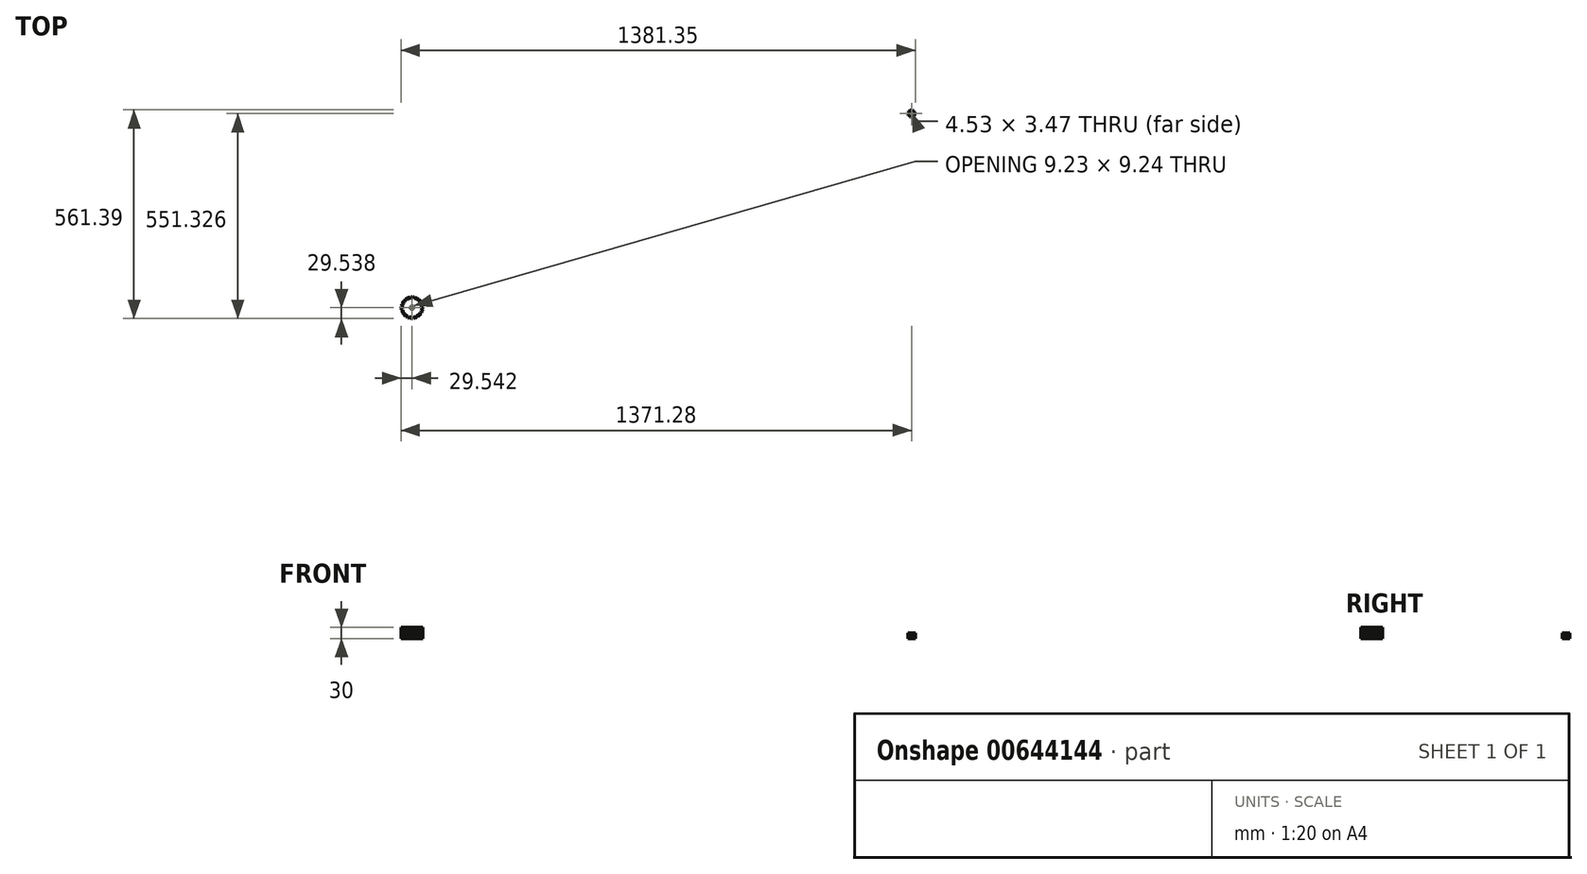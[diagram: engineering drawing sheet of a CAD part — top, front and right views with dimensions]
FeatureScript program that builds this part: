
annotation { "Feature Type Name" : "Feature", "Feature Type Description" : "" }
export const myFeature = defineFeature(function(context is Context, id is Id, definition is map)
    precondition{}
    {
        {
            var Q0;
            Q0=qCreatedBy(makeId("Top.planeOp"),FACE);
            var sketch = newSketch(context, id + "F0", { "sketchPlane" : qUnion([Q0])});
            skLineSegment(sketch, "E0", {"start": v(-554.7, 834.7) * mm, "end": v(-554.7, 832.86) * mm});
            skLineSegment(sketch, "E1", {"start": v(-545.46, 834.7) * mm, "end": v(-545.46, 832.86) * mm});
            skLineSegment(sketch, "E2", {"start": v(-499.13, 795.45) * mm, "end": v(-499.01, 795.41) * mm});
            skLineSegment(sketch, "E3", {"start": v(-499.01, 795.41) * mm, "end": v(-498.9, 795.4) * mm});
            skLineSegment(sketch, "E4", {"start": v(-498.9, 795.4) * mm, "end": v(-498.78, 795.37) * mm});
            skLineSegment(sketch, "E5", {"start": v(-498.78, 795.37) * mm, "end": v(-498.66, 795.35) * mm});
            skLineSegment(sketch, "E6", {"start": v(-498.66, 795.35) * mm, "end": v(-498.54, 795.33) * mm});
            skLineSegment(sketch, "E7", {"start": v(-498.54, 795.33) * mm, "end": v(-498.42, 795.3) * mm});
            skLineSegment(sketch, "E8", {"start": v(-498.42, 795.3) * mm, "end": v(-498.3, 795.27) * mm});
            skLineSegment(sketch, "E9", {"start": v(-498.3, 795.27) * mm, "end": v(-498.19, 795.24) * mm});
            skLineSegment(sketch, "E10", {"start": v(-498.19, 795.24) * mm, "end": v(-498.07, 795.2) * mm});
            skLineSegment(sketch, "E11", {"start": v(-498.07, 795.2) * mm, "end": v(-497.95, 795.17) * mm});
            skLineSegment(sketch, "E12", {"start": v(-497.95, 795.17) * mm, "end": v(-497.84, 795.14) * mm});
            skLineSegment(sketch, "E13", {"start": v(-497.84, 795.14) * mm, "end": v(-497.72, 795.1) * mm});
            skLineSegment(sketch, "E14", {"start": v(-497.72, 795.1) * mm, "end": v(-497.6, 795.06) * mm});
            skLineSegment(sketch, "E15", {"start": v(-497.6, 795.06) * mm, "end": v(-497.48, 795.02) * mm});
            skLineSegment(sketch, "E16", {"start": v(-497.48, 795.02) * mm, "end": v(-497.37, 794.98) * mm});
            skLineSegment(sketch, "E17", {"start": v(-497.37, 794.98) * mm, "end": v(-497.25, 794.93) * mm});
            skLineSegment(sketch, "E18", {"start": v(-497.25, 794.93) * mm, "end": v(-497.13, 794.88) * mm});
            skLineSegment(sketch, "E19", {"start": v(-497.13, 794.88) * mm, "end": v(-497.02, 794.84) * mm});
            skLineSegment(sketch, "E20", {"start": v(-497.02, 794.84) * mm, "end": v(-496.9, 794.79) * mm});
            skLineSegment(sketch, "E21", {"start": v(-496.9, 794.79) * mm, "end": v(-496.78, 794.74) * mm});
            skLineSegment(sketch, "E22", {"start": v(-496.78, 794.74) * mm, "end": v(-496.67, 794.68) * mm});
            skLineSegment(sketch, "E23", {"start": v(-496.67, 794.68) * mm, "end": v(-496.55, 794.63) * mm});
            skLineSegment(sketch, "E24", {"start": v(-496.55, 794.63) * mm, "end": v(-496.43, 794.57) * mm});
            skLineSegment(sketch, "E25", {"start": v(-496.43, 794.57) * mm, "end": v(-496.32, 794.51) * mm});
            skLineSegment(sketch, "E26", {"start": v(-496.32, 794.51) * mm, "end": v(-496.2, 794.45) * mm});
            skLineSegment(sketch, "E27", {"start": v(-496.2, 794.45) * mm, "end": v(-496.08, 794.4) * mm});
            skLineSegment(sketch, "E28", {"start": v(-496.08, 794.4) * mm, "end": v(-495.97, 794.33) * mm});
            skLineSegment(sketch, "E29", {"start": v(-495.97, 794.33) * mm, "end": v(-495.85, 794.27) * mm});
            skLineSegment(sketch, "E30", {"start": v(-495.85, 794.27) * mm, "end": v(-495.74, 794.2) * mm});
            skLineSegment(sketch, "E31", {"start": v(-495.74, 794.2) * mm, "end": v(-495.62, 794.13) * mm});
            skLineSegment(sketch, "E32", {"start": v(-495.62, 794.13) * mm, "end": v(-495.65, 793.46) * mm});
            skLineSegment(sketch, "E33", {"start": v(-495.65, 793.46) * mm, "end": v(-495.7, 792.79) * mm});
            skLineSegment(sketch, "E34", {"start": v(-495.7, 792.79) * mm, "end": v(-495.81, 792.73) * mm});
            skLineSegment(sketch, "E35", {"start": v(-495.81, 792.73) * mm, "end": v(-495.93, 792.68) * mm});
            skLineSegment(sketch, "E36", {"start": v(-495.93, 792.68) * mm, "end": v(-496.06, 792.63) * mm});
            skLineSegment(sketch, "E37", {"start": v(-496.06, 792.63) * mm, "end": v(-496.18, 792.58) * mm});
            skLineSegment(sketch, "E38", {"start": v(-496.18, 792.58) * mm, "end": v(-496.3, 792.53) * mm});
            skLineSegment(sketch, "E39", {"start": v(-496.3, 792.53) * mm, "end": v(-496.42, 792.49) * mm});
            skLineSegment(sketch, "E40", {"start": v(-496.42, 792.49) * mm, "end": v(-496.54, 792.44) * mm});
            skLineSegment(sketch, "E41", {"start": v(-496.54, 792.44) * mm, "end": v(-496.67, 792.4) * mm});
            skLineSegment(sketch, "E42", {"start": v(-496.67, 792.4) * mm, "end": v(-496.79, 792.35) * mm});
            skLineSegment(sketch, "E43", {"start": v(-496.79, 792.35) * mm, "end": v(-496.9, 792.31) * mm});
            skLineSegment(sketch, "E44", {"start": v(-496.9, 792.31) * mm, "end": v(-497.03, 792.27) * mm});
            skLineSegment(sketch, "E45", {"start": v(-497.03, 792.27) * mm, "end": v(-497.15, 792.24) * mm});
            skLineSegment(sketch, "E46", {"start": v(-497.15, 792.24) * mm, "end": v(-497.27, 792.2) * mm});
            skLineSegment(sketch, "E47", {"start": v(-497.27, 792.2) * mm, "end": v(-497.4, 792.17) * mm});
            skLineSegment(sketch, "E48", {"start": v(-497.4, 792.17) * mm, "end": v(-497.52, 792.14) * mm});
            skLineSegment(sketch, "E49", {"start": v(-497.52, 792.14) * mm, "end": v(-497.64, 792.1) * mm});
            skLineSegment(sketch, "E50", {"start": v(-497.64, 792.1) * mm, "end": v(-497.76, 792.08) * mm});
            skLineSegment(sketch, "E51", {"start": v(-497.76, 792.08) * mm, "end": v(-497.88, 792.05) * mm});
            skLineSegment(sketch, "E52", {"start": v(-497.88, 792.05) * mm, "end": v(-498, 792.02) * mm});
            skLineSegment(sketch, "E53", {"start": v(-498, 792.02) * mm, "end": v(-498.12, 792) * mm});
            skLineSegment(sketch, "E54", {"start": v(-498.12, 792) * mm, "end": v(-498.24, 791.98) * mm});
            skLineSegment(sketch, "E55", {"start": v(-498.24, 791.98) * mm, "end": v(-498.36, 791.96) * mm});
            skLineSegment(sketch, "E56", {"start": v(-498.36, 791.96) * mm, "end": v(-498.48, 791.94) * mm});
            skLineSegment(sketch, "E57", {"start": v(-498.48, 791.94) * mm, "end": v(-498.6, 791.92) * mm});
            skLineSegment(sketch, "E58", {"start": v(-498.6, 791.92) * mm, "end": v(-498.72, 791.91) * mm});
            skLineSegment(sketch, "E59", {"start": v(-498.72, 791.91) * mm, "end": v(-498.84, 791.9) * mm});
            skLineSegment(sketch, "E60", {"start": v(-498.84, 791.9) * mm, "end": v(-498.96, 791.89) * mm});
            skLineSegment(sketch, "E61", {"start": v(-498.96, 791.89) * mm, "end": v(-499.08, 791.88) * mm});
            skLineSegment(sketch, "E62", {"start": v(-499.08, 791.88) * mm, "end": v(-499.2, 791.87) * mm});
            skLineSegment(sketch, "E63", {"start": v(-499.2, 791.87) * mm, "end": v(-499.32, 791.85) * mm});
            skLineSegment(sketch, "E64", {"start": v(-499.32, 791.85) * mm, "end": v(-499.95, 791.93) * mm});
            skLineSegment(sketch, "E65", {"start": v(-499.95, 791.93) * mm, "end": v(-500.23, 790.15) * mm});
            skLineSegment(sketch, "E66", {"start": v(-500.23, 790.15) * mm, "end": v(-499.6, 790.03) * mm});
            skLineSegment(sketch, "E67", {"start": v(-499.6, 790.03) * mm, "end": v(-499.5, 789.97) * mm});
            skLineSegment(sketch, "E68", {"start": v(-499.5, 789.97) * mm, "end": v(-499.39, 789.92) * mm});
            skLineSegment(sketch, "E69", {"start": v(-499.39, 789.92) * mm, "end": v(-499.28, 789.88) * mm});
            skLineSegment(sketch, "E70", {"start": v(-499.28, 789.88) * mm, "end": v(-499.17, 789.83) * mm});
            skLineSegment(sketch, "E71", {"start": v(-499.17, 789.83) * mm, "end": v(-499.06, 789.78) * mm});
            skLineSegment(sketch, "E72", {"start": v(-499.06, 789.78) * mm, "end": v(-498.95, 789.73) * mm});
            skLineSegment(sketch, "E73", {"start": v(-498.95, 789.73) * mm, "end": v(-498.84, 789.68) * mm});
            skLineSegment(sketch, "E74", {"start": v(-498.84, 789.68) * mm, "end": v(-498.73, 789.63) * mm});
            skLineSegment(sketch, "E75", {"start": v(-498.73, 789.63) * mm, "end": v(-498.62, 789.57) * mm});
            skLineSegment(sketch, "E76", {"start": v(-498.62, 789.57) * mm, "end": v(-498.51, 789.51) * mm});
            skLineSegment(sketch, "E77", {"start": v(-498.51, 789.51) * mm, "end": v(-498.4, 789.45) * mm});
            skLineSegment(sketch, "E78", {"start": v(-498.4, 789.45) * mm, "end": v(-498.3, 789.4) * mm});
            skLineSegment(sketch, "E79", {"start": v(-498.3, 789.4) * mm, "end": v(-498.2, 789.33) * mm});
            skLineSegment(sketch, "E80", {"start": v(-498.2, 789.33) * mm, "end": v(-498.09, 789.26) * mm});
            skLineSegment(sketch, "E81", {"start": v(-498.09, 789.26) * mm, "end": v(-497.98, 789.2) * mm});
            skLineSegment(sketch, "E82", {"start": v(-497.98, 789.2) * mm, "end": v(-497.88, 789.13) * mm});
            skLineSegment(sketch, "E83", {"start": v(-497.88, 789.13) * mm, "end": v(-497.77, 789.06) * mm});
            skLineSegment(sketch, "E84", {"start": v(-497.77, 789.06) * mm, "end": v(-497.67, 788.99) * mm});
            skLineSegment(sketch, "E85", {"start": v(-497.67, 788.99) * mm, "end": v(-497.56, 788.92) * mm});
            skLineSegment(sketch, "E86", {"start": v(-497.56, 788.92) * mm, "end": v(-497.46, 788.84) * mm});
            skLineSegment(sketch, "E87", {"start": v(-497.46, 788.84) * mm, "end": v(-497.36, 788.77) * mm});
            skLineSegment(sketch, "E88", {"start": v(-497.36, 788.77) * mm, "end": v(-497.25, 788.69) * mm});
            skLineSegment(sketch, "E89", {"start": v(-497.25, 788.69) * mm, "end": v(-497.15, 788.6) * mm});
            skLineSegment(sketch, "E90", {"start": v(-497.15, 788.6) * mm, "end": v(-497.05, 788.53) * mm});
            skLineSegment(sketch, "E91", {"start": v(-497.05, 788.53) * mm, "end": v(-496.95, 788.45) * mm});
            skLineSegment(sketch, "E92", {"start": v(-496.95, 788.45) * mm, "end": v(-496.85, 788.36) * mm});
            skLineSegment(sketch, "E93", {"start": v(-496.85, 788.36) * mm, "end": v(-496.75, 788.28) * mm});
            skLineSegment(sketch, "E94", {"start": v(-496.75, 788.28) * mm, "end": v(-496.65, 788.2) * mm});
            skLineSegment(sketch, "E95", {"start": v(-496.65, 788.2) * mm, "end": v(-496.55, 788.1) * mm});
            skLineSegment(sketch, "E96", {"start": v(-496.55, 788.1) * mm, "end": v(-496.45, 788.01) * mm});
            skLineSegment(sketch, "E97", {"start": v(-496.45, 788.01) * mm, "end": v(-496.61, 787.36) * mm});
            skLineSegment(sketch, "E98", {"start": v(-496.61, 787.36) * mm, "end": v(-496.8, 786.7) * mm});
            skLineSegment(sketch, "E99", {"start": v(-496.8, 786.7) * mm, "end": v(-496.93, 786.68) * mm});
            skLineSegment(sketch, "E100", {"start": v(-496.93, 786.68) * mm, "end": v(-497.06, 786.66) * mm});
            skLineSegment(sketch, "E101", {"start": v(-497.06, 786.66) * mm, "end": v(-497.19, 786.63) * mm});
            skLineSegment(sketch, "E102", {"start": v(-497.19, 786.63) * mm, "end": v(-497.32, 786.6) * mm});
            skLineSegment(sketch, "E103", {"start": v(-497.32, 786.6) * mm, "end": v(-497.45, 786.59) * mm});
            skLineSegment(sketch, "E104", {"start": v(-497.45, 786.59) * mm, "end": v(-497.57, 786.57) * mm});
            skLineSegment(sketch, "E105", {"start": v(-497.57, 786.57) * mm, "end": v(-497.7, 786.55) * mm});
            skLineSegment(sketch, "E106", {"start": v(-497.7, 786.55) * mm, "end": v(-497.83, 786.53) * mm});
            skLineSegment(sketch, "E107", {"start": v(-497.83, 786.53) * mm, "end": v(-497.96, 786.51) * mm});
            skLineSegment(sketch, "E108", {"start": v(-497.96, 786.51) * mm, "end": v(-498.09, 786.5) * mm});
            skLineSegment(sketch, "E109", {"start": v(-498.09, 786.5) * mm, "end": v(-498.21, 786.49) * mm});
            skLineSegment(sketch, "E110", {"start": v(-498.21, 786.49) * mm, "end": v(-498.34, 786.48) * mm});
            skLineSegment(sketch, "E111", {"start": v(-498.34, 786.48) * mm, "end": v(-498.47, 786.47) * mm});
            skLineSegment(sketch, "E112", {"start": v(-498.47, 786.47) * mm, "end": v(-498.6, 786.46) * mm});
            skLineSegment(sketch, "E113", {"start": v(-498.6, 786.46) * mm, "end": v(-498.72, 786.45) * mm});
            skLineSegment(sketch, "E114", {"start": v(-498.72, 786.45) * mm, "end": v(-498.84, 786.45) * mm});
            skLineSegment(sketch, "E115", {"start": v(-498.84, 786.45) * mm, "end": v(-498.97, 786.44) * mm});
            skLineSegment(sketch, "E116", {"start": v(-498.97, 786.44) * mm, "end": v(-499.1, 786.44) * mm});
            skLineSegment(sketch, "E117", {"start": v(-499.1, 786.44) * mm, "end": v(-499.21, 786.44) * mm});
            skLineSegment(sketch, "E118", {"start": v(-499.21, 786.44) * mm, "end": v(-499.34, 786.44) * mm});
            skLineSegment(sketch, "E119", {"start": v(-499.34, 786.44) * mm, "end": v(-499.46, 786.45) * mm});
            skLineSegment(sketch, "E120", {"start": v(-499.46, 786.45) * mm, "end": v(-499.58, 786.45) * mm});
            skLineSegment(sketch, "E121", {"start": v(-499.58, 786.45) * mm, "end": v(-499.7, 786.46) * mm});
            skLineSegment(sketch, "E122", {"start": v(-499.7, 786.46) * mm, "end": v(-499.82, 786.47) * mm});
            skLineSegment(sketch, "E123", {"start": v(-499.82, 786.47) * mm, "end": v(-499.94, 786.48) * mm});
            skLineSegment(sketch, "E124", {"start": v(-499.94, 786.48) * mm, "end": v(-500.06, 786.5) * mm});
            skLineSegment(sketch, "E125", {"start": v(-500.06, 786.5) * mm, "end": v(-500.18, 786.51) * mm});
            skLineSegment(sketch, "E126", {"start": v(-500.18, 786.51) * mm, "end": v(-500.3, 786.53) * mm});
            skLineSegment(sketch, "E127", {"start": v(-500.3, 786.53) * mm, "end": v(-500.42, 786.54) * mm});
            skLineSegment(sketch, "E128", {"start": v(-500.42, 786.54) * mm, "end": v(-500.54, 786.55) * mm});
            skLineSegment(sketch, "E129", {"start": v(-500.54, 786.55) * mm, "end": v(-501.14, 786.75) * mm});
            skLineSegment(sketch, "E130", {"start": v(-501.14, 786.75) * mm, "end": v(-501.79, 785.07) * mm});
            skLineSegment(sketch, "E131", {"start": v(-501.79, 785.07) * mm, "end": v(-501.2, 784.82) * mm});
            skLineSegment(sketch, "E132", {"start": v(-501.2, 784.82) * mm, "end": v(-501.1, 784.74) * mm});
            skLineSegment(sketch, "E133", {"start": v(-501.1, 784.74) * mm, "end": v(-501, 784.67) * mm});
            skLineSegment(sketch, "E134", {"start": v(-501, 784.67) * mm, "end": v(-500.91, 784.6) * mm});
            skLineSegment(sketch, "E135", {"start": v(-500.91, 784.6) * mm, "end": v(-500.81, 784.54) * mm});
            skLineSegment(sketch, "E136", {"start": v(-500.81, 784.54) * mm, "end": v(-500.71, 784.47) * mm});
            skLineSegment(sketch, "E137", {"start": v(-500.71, 784.47) * mm, "end": v(-500.62, 784.4) * mm});
            skLineSegment(sketch, "E138", {"start": v(-500.62, 784.4) * mm, "end": v(-500.52, 784.33) * mm});
            skLineSegment(sketch, "E139", {"start": v(-500.52, 784.33) * mm, "end": v(-500.43, 784.25) * mm});
            skLineSegment(sketch, "E140", {"start": v(-500.43, 784.25) * mm, "end": v(-500.33, 784.17) * mm});
            skLineSegment(sketch, "E141", {"start": v(-500.33, 784.17) * mm, "end": v(-500.24, 784.1) * mm});
            skLineSegment(sketch, "E142", {"start": v(-500.24, 784.1) * mm, "end": v(-500.15, 784.01) * mm});
            skLineSegment(sketch, "E143", {"start": v(-500.15, 784.01) * mm, "end": v(-500.05, 783.93) * mm});
            skLineSegment(sketch, "E144", {"start": v(-500.05, 783.93) * mm, "end": v(-499.96, 783.85) * mm});
            skLineSegment(sketch, "E145", {"start": v(-499.96, 783.85) * mm, "end": v(-499.87, 783.76) * mm});
            skLineSegment(sketch, "E146", {"start": v(-499.87, 783.76) * mm, "end": v(-499.78, 783.67) * mm});
            skLineSegment(sketch, "E147", {"start": v(-499.78, 783.67) * mm, "end": v(-499.7, 783.59) * mm});
            skLineSegment(sketch, "E148", {"start": v(-499.7, 783.59) * mm, "end": v(-499.6, 783.5) * mm});
            skLineSegment(sketch, "E149", {"start": v(-499.6, 783.5) * mm, "end": v(-499.52, 783.4) * mm});
            skLineSegment(sketch, "E150", {"start": v(-499.52, 783.4) * mm, "end": v(-499.43, 783.31) * mm});
            skLineSegment(sketch, "E151", {"start": v(-499.43, 783.31) * mm, "end": v(-499.35, 783.22) * mm});
            skLineSegment(sketch, "E152", {"start": v(-499.35, 783.22) * mm, "end": v(-499.26, 783.12) * mm});
            skLineSegment(sketch, "E153", {"start": v(-499.26, 783.12) * mm, "end": v(-499.18, 783.02) * mm});
            skLineSegment(sketch, "E154", {"start": v(-499.18, 783.02) * mm, "end": v(-499.1, 782.93) * mm});
            skLineSegment(sketch, "E155", {"start": v(-499.1, 782.93) * mm, "end": v(-499.01, 782.82) * mm});
            skLineSegment(sketch, "E156", {"start": v(-499.01, 782.82) * mm, "end": v(-498.93, 782.72) * mm});
            skLineSegment(sketch, "E157", {"start": v(-498.93, 782.72) * mm, "end": v(-498.85, 782.62) * mm});
            skLineSegment(sketch, "E158", {"start": v(-498.85, 782.62) * mm, "end": v(-498.77, 782.52) * mm});
            skLineSegment(sketch, "E159", {"start": v(-498.77, 782.52) * mm, "end": v(-498.69, 782.41) * mm});
            skLineSegment(sketch, "E160", {"start": v(-498.69, 782.41) * mm, "end": v(-498.6, 782.3) * mm});
            skLineSegment(sketch, "E161", {"start": v(-498.6, 782.3) * mm, "end": v(-498.53, 782.2) * mm});
            skLineSegment(sketch, "E162", {"start": v(-498.53, 782.2) * mm, "end": v(-498.83, 781.6) * mm});
            skLineSegment(sketch, "E163", {"start": v(-498.83, 781.6) * mm, "end": v(-499.14, 781) * mm});
            skLineSegment(sketch, "E164", {"start": v(-499.14, 781) * mm, "end": v(-499.27, 781) * mm});
            skLineSegment(sketch, "E165", {"start": v(-499.27, 781) * mm, "end": v(-499.4, 781) * mm});
            skLineSegment(sketch, "E166", {"start": v(-499.4, 781) * mm, "end": v(-499.54, 781) * mm});
            skLineSegment(sketch, "E167", {"start": v(-499.54, 781) * mm, "end": v(-499.67, 781) * mm});
            skLineSegment(sketch, "E168", {"start": v(-499.67, 781) * mm, "end": v(-499.8, 781) * mm});
            skLineSegment(sketch, "E169", {"start": v(-499.8, 781) * mm, "end": v(-499.93, 781.02) * mm});
            skLineSegment(sketch, "E170", {"start": v(-499.93, 781.02) * mm, "end": v(-500.06, 781.02) * mm});
            skLineSegment(sketch, "E171", {"start": v(-500.06, 781.02) * mm, "end": v(-500.2, 781.03) * mm});
            skLineSegment(sketch, "E172", {"start": v(-500.2, 781.03) * mm, "end": v(-500.32, 781.04) * mm});
            skLineSegment(sketch, "E173", {"start": v(-500.32, 781.04) * mm, "end": v(-500.45, 781.06) * mm});
            skLineSegment(sketch, "E174", {"start": v(-500.45, 781.06) * mm, "end": v(-500.57, 781.07) * mm});
            skLineSegment(sketch, "E175", {"start": v(-500.57, 781.07) * mm, "end": v(-500.7, 781.09) * mm});
            skLineSegment(sketch, "E176", {"start": v(-500.7, 781.09) * mm, "end": v(-500.83, 781.1) * mm});
            skLineSegment(sketch, "E177", {"start": v(-500.83, 781.1) * mm, "end": v(-500.95, 781.12) * mm});
            skLineSegment(sketch, "E178", {"start": v(-500.95, 781.12) * mm, "end": v(-501.07, 781.14) * mm});
            skLineSegment(sketch, "E179", {"start": v(-501.07, 781.14) * mm, "end": v(-501.2, 781.16) * mm});
            skLineSegment(sketch, "E180", {"start": v(-501.2, 781.16) * mm, "end": v(-501.32, 781.18) * mm});
            skLineSegment(sketch, "E181", {"start": v(-501.32, 781.18) * mm, "end": v(-501.44, 781.2) * mm});
            skLineSegment(sketch, "E182", {"start": v(-501.44, 781.2) * mm, "end": v(-501.56, 781.24) * mm});
            skLineSegment(sketch, "E183", {"start": v(-501.56, 781.24) * mm, "end": v(-501.68, 781.26) * mm});
            skLineSegment(sketch, "E184", {"start": v(-501.68, 781.26) * mm, "end": v(-501.8, 781.3) * mm});
            skLineSegment(sketch, "E185", {"start": v(-501.8, 781.3) * mm, "end": v(-501.92, 781.32) * mm});
            skLineSegment(sketch, "E186", {"start": v(-501.92, 781.32) * mm, "end": v(-502.03, 781.35) * mm});
            skLineSegment(sketch, "E187", {"start": v(-502.03, 781.35) * mm, "end": v(-502.15, 781.39) * mm});
            skLineSegment(sketch, "E188", {"start": v(-502.15, 781.39) * mm, "end": v(-502.27, 781.42) * mm});
            skLineSegment(sketch, "E189", {"start": v(-502.27, 781.42) * mm, "end": v(-502.38, 781.46) * mm});
            skLineSegment(sketch, "E190", {"start": v(-502.38, 781.46) * mm, "end": v(-502.5, 781.5) * mm});
            skLineSegment(sketch, "E191", {"start": v(-502.5, 781.5) * mm, "end": v(-502.6, 781.54) * mm});
            skLineSegment(sketch, "E192", {"start": v(-502.6, 781.54) * mm, "end": v(-502.72, 781.58) * mm});
            skLineSegment(sketch, "E193", {"start": v(-502.72, 781.58) * mm, "end": v(-502.84, 781.61) * mm});
            skLineSegment(sketch, "E194", {"start": v(-502.84, 781.61) * mm, "end": v(-503.38, 781.94) * mm});
            skLineSegment(sketch, "E195", {"start": v(-503.38, 781.94) * mm, "end": v(-504.36, 780.43) * mm});
            skLineSegment(sketch, "E196", {"start": v(-504.36, 780.43) * mm, "end": v(-503.84, 780.07) * mm});
            skLineSegment(sketch, "E197", {"start": v(-503.84, 780.07) * mm, "end": v(-503.77, 779.97) * mm});
            skLineSegment(sketch, "E198", {"start": v(-503.77, 779.97) * mm, "end": v(-503.68, 779.88) * mm});
            skLineSegment(sketch, "E199", {"start": v(-503.68, 779.88) * mm, "end": v(-503.6, 779.8) * mm});
            skLineSegment(sketch, "E200", {"start": v(-503.6, 779.8) * mm, "end": v(-503.52, 779.7) * mm});
            skLineSegment(sketch, "E201", {"start": v(-503.52, 779.7) * mm, "end": v(-503.44, 779.62) * mm});
            skLineSegment(sketch, "E202", {"start": v(-503.44, 779.62) * mm, "end": v(-503.36, 779.53) * mm});
            skLineSegment(sketch, "E203", {"start": v(-503.36, 779.53) * mm, "end": v(-503.28, 779.44) * mm});
            skLineSegment(sketch, "E204", {"start": v(-503.28, 779.44) * mm, "end": v(-503.2, 779.34) * mm});
            skLineSegment(sketch, "E205", {"start": v(-503.2, 779.34) * mm, "end": v(-503.13, 779.25) * mm});
            skLineSegment(sketch, "E206", {"start": v(-503.13, 779.25) * mm, "end": v(-503.05, 779.15) * mm});
            skLineSegment(sketch, "E207", {"start": v(-503.05, 779.15) * mm, "end": v(-502.98, 779.05) * mm});
            skLineSegment(sketch, "E208", {"start": v(-502.98, 779.05) * mm, "end": v(-502.9, 778.95) * mm});
            skLineSegment(sketch, "E209", {"start": v(-502.9, 778.95) * mm, "end": v(-502.83, 778.85) * mm});
            skLineSegment(sketch, "E210", {"start": v(-502.83, 778.85) * mm, "end": v(-502.76, 778.75) * mm});
            skLineSegment(sketch, "E211", {"start": v(-502.76, 778.75) * mm, "end": v(-502.7, 778.65) * mm});
            skLineSegment(sketch, "E212", {"start": v(-502.7, 778.65) * mm, "end": v(-502.62, 778.54) * mm});
            skLineSegment(sketch, "E213", {"start": v(-502.62, 778.54) * mm, "end": v(-502.56, 778.43) * mm});
            skLineSegment(sketch, "E214", {"start": v(-502.56, 778.43) * mm, "end": v(-502.5, 778.33) * mm});
            skLineSegment(sketch, "E215", {"start": v(-502.5, 778.33) * mm, "end": v(-502.43, 778.22) * mm});
            skLineSegment(sketch, "E216", {"start": v(-502.43, 778.22) * mm, "end": v(-502.36, 778.1) * mm});
            skLineSegment(sketch, "E217", {"start": v(-502.36, 778.1) * mm, "end": v(-502.3, 778) * mm});
            skLineSegment(sketch, "E218", {"start": v(-502.3, 778) * mm, "end": v(-502.24, 777.88) * mm});
            skLineSegment(sketch, "E219", {"start": v(-502.24, 777.88) * mm, "end": v(-502.18, 777.77) * mm});
            skLineSegment(sketch, "E220", {"start": v(-502.18, 777.77) * mm, "end": v(-502.11, 777.65) * mm});
            skLineSegment(sketch, "E221", {"start": v(-502.11, 777.65) * mm, "end": v(-502.06, 777.54) * mm});
            skLineSegment(sketch, "E222", {"start": v(-502.06, 777.54) * mm, "end": v(-502, 777.42) * mm});
            skLineSegment(sketch, "E223", {"start": v(-502, 777.42) * mm, "end": v(-501.94, 777.3) * mm});
            skLineSegment(sketch, "E224", {"start": v(-501.94, 777.3) * mm, "end": v(-501.88, 777.18) * mm});
            skLineSegment(sketch, "E225", {"start": v(-501.88, 777.18) * mm, "end": v(-501.83, 777.06) * mm});
            skLineSegment(sketch, "E226", {"start": v(-501.83, 777.06) * mm, "end": v(-501.77, 776.94) * mm});
            skLineSegment(sketch, "E227", {"start": v(-501.77, 776.94) * mm, "end": v(-502.2, 776.41) * mm});
            skLineSegment(sketch, "E228", {"start": v(-502.2, 776.41) * mm, "end": v(-502.62, 775.9) * mm});
            skLineSegment(sketch, "E229", {"start": v(-502.62, 775.9) * mm, "end": v(-502.75, 775.92) * mm});
            skLineSegment(sketch, "E230", {"start": v(-502.75, 775.92) * mm, "end": v(-502.88, 775.95) * mm});
            skLineSegment(sketch, "E231", {"start": v(-502.88, 775.95) * mm, "end": v(-503.01, 775.98) * mm});
            skLineSegment(sketch, "E232", {"start": v(-503.01, 775.98) * mm, "end": v(-503.14, 776.01) * mm});
            skLineSegment(sketch, "E233", {"start": v(-503.14, 776.01) * mm, "end": v(-503.27, 776.04) * mm});
            skLineSegment(sketch, "E234", {"start": v(-503.27, 776.04) * mm, "end": v(-503.4, 776.08) * mm});
            skLineSegment(sketch, "E235", {"start": v(-503.4, 776.08) * mm, "end": v(-503.52, 776.11) * mm});
            skLineSegment(sketch, "E236", {"start": v(-503.52, 776.11) * mm, "end": v(-503.64, 776.15) * mm});
            skLineSegment(sketch, "E237", {"start": v(-503.64, 776.15) * mm, "end": v(-503.77, 776.18) * mm});
            skLineSegment(sketch, "E238", {"start": v(-503.77, 776.18) * mm, "end": v(-503.89, 776.22) * mm});
            skLineSegment(sketch, "E239", {"start": v(-503.89, 776.22) * mm, "end": v(-504, 776.26) * mm});
            skLineSegment(sketch, "E240", {"start": v(-504, 776.26) * mm, "end": v(-504.13, 776.3) * mm});
            skLineSegment(sketch, "E241", {"start": v(-504.13, 776.3) * mm, "end": v(-504.25, 776.35) * mm});
            skLineSegment(sketch, "E242", {"start": v(-504.25, 776.35) * mm, "end": v(-504.37, 776.4) * mm});
            skLineSegment(sketch, "E243", {"start": v(-504.37, 776.4) * mm, "end": v(-504.48, 776.44) * mm});
            skLineSegment(sketch, "E244", {"start": v(-504.48, 776.44) * mm, "end": v(-504.6, 776.48) * mm});
            skLineSegment(sketch, "E245", {"start": v(-504.6, 776.48) * mm, "end": v(-504.71, 776.53) * mm});
            skLineSegment(sketch, "E246", {"start": v(-504.71, 776.53) * mm, "end": v(-504.83, 776.58) * mm});
            skLineSegment(sketch, "E247", {"start": v(-504.83, 776.58) * mm, "end": v(-504.94, 776.63) * mm});
            skLineSegment(sketch, "E248", {"start": v(-504.94, 776.63) * mm, "end": v(-505.05, 776.68) * mm});
            skLineSegment(sketch, "E249", {"start": v(-505.05, 776.68) * mm, "end": v(-505.16, 776.74) * mm});
            skLineSegment(sketch, "E250", {"start": v(-505.16, 776.74) * mm, "end": v(-505.27, 776.8) * mm});
            skLineSegment(sketch, "E251", {"start": v(-505.27, 776.8) * mm, "end": v(-505.38, 776.85) * mm});
            skLineSegment(sketch, "E252", {"start": v(-505.38, 776.85) * mm, "end": v(-505.48, 776.9) * mm});
            skLineSegment(sketch, "E253", {"start": v(-505.48, 776.9) * mm, "end": v(-505.59, 776.96) * mm});
            skLineSegment(sketch, "E254", {"start": v(-505.59, 776.96) * mm, "end": v(-505.7, 777.02) * mm});
            skLineSegment(sketch, "E255", {"start": v(-505.7, 777.02) * mm, "end": v(-505.8, 777.09) * mm});
            skLineSegment(sketch, "E256", {"start": v(-505.8, 777.09) * mm, "end": v(-505.9, 777.15) * mm});
            skLineSegment(sketch, "E257", {"start": v(-505.9, 777.15) * mm, "end": v(-506, 777.21) * mm});
            skLineSegment(sketch, "E258", {"start": v(-506, 777.21) * mm, "end": v(-506.1, 777.26) * mm});
            skLineSegment(sketch, "E259", {"start": v(-506.1, 777.26) * mm, "end": v(-506.58, 777.7) * mm});
            skLineSegment(sketch, "E260", {"start": v(-506.58, 777.7) * mm, "end": v(-507.85, 776.43) * mm});
            skLineSegment(sketch, "E261", {"start": v(-507.85, 776.43) * mm, "end": v(-507.41, 775.96) * mm});
            skLineSegment(sketch, "E262", {"start": v(-507.41, 775.96) * mm, "end": v(-507.36, 775.85) * mm});
            skLineSegment(sketch, "E263", {"start": v(-507.36, 775.85) * mm, "end": v(-507.3, 775.75) * mm});
            skLineSegment(sketch, "E264", {"start": v(-507.3, 775.75) * mm, "end": v(-507.24, 775.65) * mm});
            skLineSegment(sketch, "E265", {"start": v(-507.24, 775.65) * mm, "end": v(-507.17, 775.54) * mm});
            skLineSegment(sketch, "E266", {"start": v(-507.17, 775.54) * mm, "end": v(-507.11, 775.44) * mm});
            skLineSegment(sketch, "E267", {"start": v(-507.11, 775.44) * mm, "end": v(-507.05, 775.33) * mm});
            skLineSegment(sketch, "E268", {"start": v(-507.05, 775.33) * mm, "end": v(-507, 775.23) * mm});
            skLineSegment(sketch, "E269", {"start": v(-507, 775.23) * mm, "end": v(-506.94, 775.12) * mm});
            skLineSegment(sketch, "E270", {"start": v(-506.94, 775.12) * mm, "end": v(-506.89, 775.01) * mm});
            skLineSegment(sketch, "E271", {"start": v(-506.89, 775.01) * mm, "end": v(-506.83, 774.9) * mm});
            skLineSegment(sketch, "E272", {"start": v(-506.83, 774.9) * mm, "end": v(-506.78, 774.8) * mm});
            skLineSegment(sketch, "E273", {"start": v(-506.78, 774.8) * mm, "end": v(-506.73, 774.68) * mm});
            skLineSegment(sketch, "E274", {"start": v(-506.73, 774.68) * mm, "end": v(-506.68, 774.56) * mm});
            skLineSegment(sketch, "E275", {"start": v(-506.68, 774.56) * mm, "end": v(-506.63, 774.45) * mm});
            skLineSegment(sketch, "E276", {"start": v(-506.63, 774.45) * mm, "end": v(-506.59, 774.33) * mm});
            skLineSegment(sketch, "E277", {"start": v(-506.59, 774.33) * mm, "end": v(-506.54, 774.22) * mm});
            skLineSegment(sketch, "E278", {"start": v(-506.54, 774.22) * mm, "end": v(-506.5, 774.1) * mm});
            skLineSegment(sketch, "E279", {"start": v(-506.5, 774.1) * mm, "end": v(-506.46, 773.98) * mm});
            skLineSegment(sketch, "E280", {"start": v(-506.46, 773.98) * mm, "end": v(-506.41, 773.86) * mm});
            skLineSegment(sketch, "E281", {"start": v(-506.41, 773.86) * mm, "end": v(-506.37, 773.74) * mm});
            skLineSegment(sketch, "E282", {"start": v(-506.37, 773.74) * mm, "end": v(-506.33, 773.62) * mm});
            skLineSegment(sketch, "E283", {"start": v(-506.33, 773.62) * mm, "end": v(-506.3, 773.5) * mm});
            skLineSegment(sketch, "E284", {"start": v(-506.3, 773.5) * mm, "end": v(-506.26, 773.37) * mm});
            skLineSegment(sketch, "E285", {"start": v(-506.26, 773.37) * mm, "end": v(-506.23, 773.24) * mm});
            skLineSegment(sketch, "E286", {"start": v(-506.23, 773.24) * mm, "end": v(-506.2, 773.12) * mm});
            skLineSegment(sketch, "E287", {"start": v(-506.2, 773.12) * mm, "end": v(-506.16, 773) * mm});
            skLineSegment(sketch, "E288", {"start": v(-506.16, 773) * mm, "end": v(-506.13, 772.86) * mm});
            skLineSegment(sketch, "E289", {"start": v(-506.13, 772.86) * mm, "end": v(-506.1, 772.73) * mm});
            skLineSegment(sketch, "E290", {"start": v(-506.1, 772.73) * mm, "end": v(-506.07, 772.6) * mm});
            skLineSegment(sketch, "E291", {"start": v(-506.07, 772.6) * mm, "end": v(-506.04, 772.47) * mm});
            skLineSegment(sketch, "E292", {"start": v(-506.04, 772.47) * mm, "end": v(-506.56, 772.04) * mm});
            skLineSegment(sketch, "E293", {"start": v(-506.56, 772.04) * mm, "end": v(-507.1, 771.62) * mm});
            skLineSegment(sketch, "E294", {"start": v(-507.1, 771.62) * mm, "end": v(-507.21, 771.68) * mm});
            skLineSegment(sketch, "E295", {"start": v(-507.21, 771.68) * mm, "end": v(-507.33, 771.73) * mm});
            skLineSegment(sketch, "E296", {"start": v(-507.33, 771.73) * mm, "end": v(-507.45, 771.8) * mm});
            skLineSegment(sketch, "E297", {"start": v(-507.45, 771.8) * mm, "end": v(-507.57, 771.85) * mm});
            skLineSegment(sketch, "E298", {"start": v(-507.57, 771.85) * mm, "end": v(-507.69, 771.9) * mm});
            skLineSegment(sketch, "E299", {"start": v(-507.69, 771.9) * mm, "end": v(-507.8, 771.96) * mm});
            skLineSegment(sketch, "E300", {"start": v(-507.8, 771.96) * mm, "end": v(-507.92, 772.03) * mm});
            skLineSegment(sketch, "E301", {"start": v(-507.92, 772.03) * mm, "end": v(-508.03, 772.09) * mm});
            skLineSegment(sketch, "E302", {"start": v(-508.03, 772.09) * mm, "end": v(-508.15, 772.15) * mm});
            skLineSegment(sketch, "E303", {"start": v(-508.15, 772.15) * mm, "end": v(-508.26, 772.21) * mm});
            skLineSegment(sketch, "E304", {"start": v(-508.26, 772.21) * mm, "end": v(-508.37, 772.28) * mm});
            skLineSegment(sketch, "E305", {"start": v(-508.37, 772.28) * mm, "end": v(-508.48, 772.34) * mm});
            skLineSegment(sketch, "E306", {"start": v(-508.48, 772.34) * mm, "end": v(-508.59, 772.4) * mm});
            skLineSegment(sketch, "E307", {"start": v(-508.59, 772.4) * mm, "end": v(-508.7, 772.47) * mm});
            skLineSegment(sketch, "E308", {"start": v(-508.7, 772.47) * mm, "end": v(-508.8, 772.54) * mm});
            skLineSegment(sketch, "E309", {"start": v(-508.8, 772.54) * mm, "end": v(-508.9, 772.61) * mm});
            skLineSegment(sketch, "E310", {"start": v(-508.9, 772.61) * mm, "end": v(-509, 772.68) * mm});
            skLineSegment(sketch, "E311", {"start": v(-509, 772.68) * mm, "end": v(-509.1, 772.76) * mm});
            skLineSegment(sketch, "E312", {"start": v(-509.1, 772.76) * mm, "end": v(-509.2, 772.83) * mm});
            skLineSegment(sketch, "E313", {"start": v(-509.2, 772.83) * mm, "end": v(-509.3, 772.9) * mm});
            skLineSegment(sketch, "E314", {"start": v(-509.3, 772.9) * mm, "end": v(-509.4, 772.98) * mm});
            skLineSegment(sketch, "E315", {"start": v(-509.4, 772.98) * mm, "end": v(-509.5, 773.05) * mm});
            skLineSegment(sketch, "E316", {"start": v(-509.5, 773.05) * mm, "end": v(-509.59, 773.13) * mm});
            skLineSegment(sketch, "E317", {"start": v(-509.59, 773.13) * mm, "end": v(-509.68, 773.2) * mm});
            skLineSegment(sketch, "E318", {"start": v(-509.68, 773.2) * mm, "end": v(-509.77, 773.29) * mm});
            skLineSegment(sketch, "E319", {"start": v(-509.77, 773.29) * mm, "end": v(-509.86, 773.37) * mm});
            skLineSegment(sketch, "E320", {"start": v(-509.86, 773.37) * mm, "end": v(-509.94, 773.45) * mm});
            skLineSegment(sketch, "E321", {"start": v(-509.94, 773.45) * mm, "end": v(-510.03, 773.53) * mm});
            skLineSegment(sketch, "E322", {"start": v(-510.03, 773.53) * mm, "end": v(-510.12, 773.62) * mm});
            skLineSegment(sketch, "E323", {"start": v(-510.12, 773.62) * mm, "end": v(-510.22, 773.7) * mm});
            skLineSegment(sketch, "E324", {"start": v(-510.22, 773.7) * mm, "end": v(-510.58, 774.21) * mm});
            skLineSegment(sketch, "E325", {"start": v(-510.58, 774.21) * mm, "end": v(-512.1, 773.23) * mm});
            skLineSegment(sketch, "E326", {"start": v(-512.1, 773.23) * mm, "end": v(-511.76, 772.69) * mm});
            skLineSegment(sketch, "E327", {"start": v(-511.76, 772.69) * mm, "end": v(-511.73, 772.57) * mm});
            skLineSegment(sketch, "E328", {"start": v(-511.73, 772.57) * mm, "end": v(-511.7, 772.46) * mm});
            skLineSegment(sketch, "E329", {"start": v(-511.7, 772.46) * mm, "end": v(-511.65, 772.34) * mm});
            skLineSegment(sketch, "E330", {"start": v(-511.65, 772.34) * mm, "end": v(-511.61, 772.23) * mm});
            skLineSegment(sketch, "E331", {"start": v(-511.61, 772.23) * mm, "end": v(-511.58, 772.12) * mm});
            skLineSegment(sketch, "E332", {"start": v(-511.58, 772.12) * mm, "end": v(-511.54, 772) * mm});
            skLineSegment(sketch, "E333", {"start": v(-511.54, 772) * mm, "end": v(-511.5, 771.88) * mm});
            skLineSegment(sketch, "E334", {"start": v(-511.5, 771.88) * mm, "end": v(-511.47, 771.77) * mm});
            skLineSegment(sketch, "E335", {"start": v(-511.47, 771.77) * mm, "end": v(-511.44, 771.65) * mm});
            skLineSegment(sketch, "E336", {"start": v(-511.44, 771.65) * mm, "end": v(-511.41, 771.53) * mm});
            skLineSegment(sketch, "E337", {"start": v(-511.41, 771.53) * mm, "end": v(-511.38, 771.41) * mm});
            skLineSegment(sketch, "E338", {"start": v(-511.38, 771.41) * mm, "end": v(-511.36, 771.3) * mm});
            skLineSegment(sketch, "E339", {"start": v(-511.36, 771.3) * mm, "end": v(-511.33, 771.17) * mm});
            skLineSegment(sketch, "E340", {"start": v(-511.33, 771.17) * mm, "end": v(-511.31, 771.05) * mm});
            skLineSegment(sketch, "E341", {"start": v(-511.31, 771.05) * mm, "end": v(-511.3, 770.92) * mm});
            skLineSegment(sketch, "E342", {"start": v(-511.3, 770.92) * mm, "end": v(-511.27, 770.8) * mm});
            skLineSegment(sketch, "E343", {"start": v(-511.27, 770.8) * mm, "end": v(-511.25, 770.67) * mm});
            skLineSegment(sketch, "E344", {"start": v(-511.25, 770.67) * mm, "end": v(-511.24, 770.55) * mm});
            skLineSegment(sketch, "E345", {"start": v(-511.24, 770.55) * mm, "end": v(-511.22, 770.42) * mm});
            skLineSegment(sketch, "E346", {"start": v(-511.22, 770.42) * mm, "end": v(-511.2, 770.3) * mm});
            skLineSegment(sketch, "E347", {"start": v(-511.2, 770.3) * mm, "end": v(-511.2, 770.17) * mm});
            skLineSegment(sketch, "E348", {"start": v(-511.2, 770.17) * mm, "end": v(-511.18, 770.04) * mm});
            skLineSegment(sketch, "E349", {"start": v(-511.18, 770.04) * mm, "end": v(-511.17, 769.91) * mm});
            skLineSegment(sketch, "E350", {"start": v(-511.17, 769.91) * mm, "end": v(-511.17, 769.78) * mm});
            skLineSegment(sketch, "E351", {"start": v(-511.17, 769.78) * mm, "end": v(-511.16, 769.65) * mm});
            skLineSegment(sketch, "E352", {"start": v(-511.16, 769.65) * mm, "end": v(-511.15, 769.52) * mm});
            skLineSegment(sketch, "E353", {"start": v(-511.15, 769.52) * mm, "end": v(-511.15, 769.4) * mm});
            skLineSegment(sketch, "E354", {"start": v(-511.15, 769.4) * mm, "end": v(-511.15, 769.26) * mm});
            skLineSegment(sketch, "E355", {"start": v(-511.15, 769.26) * mm, "end": v(-511.14, 769.12) * mm});
            skLineSegment(sketch, "E356", {"start": v(-511.14, 769.12) * mm, "end": v(-511.14, 769) * mm});
            skLineSegment(sketch, "E357", {"start": v(-511.14, 769) * mm, "end": v(-511.74, 768.68) * mm});
            skLineSegment(sketch, "E358", {"start": v(-511.74, 768.68) * mm, "end": v(-512.35, 768.38) * mm});
            skLineSegment(sketch, "E359", {"start": v(-512.35, 768.38) * mm, "end": v(-512.46, 768.46) * mm});
            skLineSegment(sketch, "E360", {"start": v(-512.46, 768.46) * mm, "end": v(-512.56, 768.54) * mm});
            skLineSegment(sketch, "E361", {"start": v(-512.56, 768.54) * mm, "end": v(-512.67, 768.62) * mm});
            skLineSegment(sketch, "E362", {"start": v(-512.67, 768.62) * mm, "end": v(-512.77, 768.7) * mm});
            skLineSegment(sketch, "E363", {"start": v(-512.77, 768.7) * mm, "end": v(-512.87, 768.78) * mm});
            skLineSegment(sketch, "E364", {"start": v(-512.87, 768.78) * mm, "end": v(-512.98, 768.86) * mm});
            skLineSegment(sketch, "E365", {"start": v(-512.98, 768.86) * mm, "end": v(-513.08, 768.94) * mm});
            skLineSegment(sketch, "E366", {"start": v(-513.08, 768.94) * mm, "end": v(-513.17, 769.03) * mm});
            skLineSegment(sketch, "E367", {"start": v(-513.17, 769.03) * mm, "end": v(-513.27, 769.11) * mm});
            skLineSegment(sketch, "E368", {"start": v(-513.27, 769.11) * mm, "end": v(-513.37, 769.2) * mm});
            skLineSegment(sketch, "E369", {"start": v(-513.37, 769.2) * mm, "end": v(-513.46, 769.28) * mm});
            skLineSegment(sketch, "E370", {"start": v(-513.46, 769.28) * mm, "end": v(-513.55, 769.37) * mm});
            skLineSegment(sketch, "E371", {"start": v(-513.55, 769.37) * mm, "end": v(-513.65, 769.45) * mm});
            skLineSegment(sketch, "E372", {"start": v(-513.65, 769.45) * mm, "end": v(-513.74, 769.54) * mm});
            skLineSegment(sketch, "E373", {"start": v(-513.74, 769.54) * mm, "end": v(-513.82, 769.63) * mm});
            skLineSegment(sketch, "E374", {"start": v(-513.82, 769.63) * mm, "end": v(-513.91, 769.72) * mm});
            skLineSegment(sketch, "E375", {"start": v(-513.91, 769.72) * mm, "end": v(-514, 769.81) * mm});
            skLineSegment(sketch, "E376", {"start": v(-514, 769.81) * mm, "end": v(-514.08, 769.9) * mm});
            skLineSegment(sketch, "E377", {"start": v(-514.08, 769.9) * mm, "end": v(-514.16, 770) * mm});
            skLineSegment(sketch, "E378", {"start": v(-514.16, 770) * mm, "end": v(-514.24, 770.09) * mm});
            skLineSegment(sketch, "E379", {"start": v(-514.24, 770.09) * mm, "end": v(-514.32, 770.18) * mm});
            skLineSegment(sketch, "E380", {"start": v(-514.32, 770.18) * mm, "end": v(-514.4, 770.28) * mm});
            skLineSegment(sketch, "E381", {"start": v(-514.4, 770.28) * mm, "end": v(-514.48, 770.37) * mm});
            skLineSegment(sketch, "E382", {"start": v(-514.48, 770.37) * mm, "end": v(-514.55, 770.47) * mm});
            skLineSegment(sketch, "E383", {"start": v(-514.55, 770.47) * mm, "end": v(-514.62, 770.56) * mm});
            skLineSegment(sketch, "E384", {"start": v(-514.62, 770.56) * mm, "end": v(-514.7, 770.66) * mm});
            skLineSegment(sketch, "E385", {"start": v(-514.7, 770.66) * mm, "end": v(-514.76, 770.76) * mm});
            skLineSegment(sketch, "E386", {"start": v(-514.76, 770.76) * mm, "end": v(-514.83, 770.86) * mm});
            skLineSegment(sketch, "E387", {"start": v(-514.83, 770.86) * mm, "end": v(-514.9, 770.96) * mm});
            skLineSegment(sketch, "E388", {"start": v(-514.9, 770.96) * mm, "end": v(-514.97, 771.05) * mm});
            skLineSegment(sketch, "E389", {"start": v(-514.97, 771.05) * mm, "end": v(-515.22, 771.64) * mm});
            skLineSegment(sketch, "E390", {"start": v(-515.22, 771.64) * mm, "end": v(-516.9, 771) * mm});
            skLineSegment(sketch, "E391", {"start": v(-516.9, 771) * mm, "end": v(-516.7, 770.39) * mm});
            skLineSegment(sketch, "E392", {"start": v(-516.7, 770.39) * mm, "end": v(-516.7, 770.27) * mm});
            skLineSegment(sketch, "E393", {"start": v(-516.7, 770.27) * mm, "end": v(-516.68, 770.15) * mm});
            skLineSegment(sketch, "E394", {"start": v(-516.68, 770.15) * mm, "end": v(-516.66, 770.03) * mm});
            skLineSegment(sketch, "E395", {"start": v(-516.66, 770.03) * mm, "end": v(-516.64, 769.91) * mm});
            skLineSegment(sketch, "E396", {"start": v(-516.64, 769.91) * mm, "end": v(-516.63, 769.8) * mm});
            skLineSegment(sketch, "E397", {"start": v(-516.63, 769.8) * mm, "end": v(-516.62, 769.67) * mm});
            skLineSegment(sketch, "E398", {"start": v(-516.62, 769.67) * mm, "end": v(-516.61, 769.55) * mm});
            skLineSegment(sketch, "E399", {"start": v(-516.61, 769.55) * mm, "end": v(-516.6, 769.43) * mm});
            skLineSegment(sketch, "E400", {"start": v(-516.6, 769.43) * mm, "end": v(-516.6, 769.3) * mm});
            skLineSegment(sketch, "E401", {"start": v(-516.6, 769.3) * mm, "end": v(-516.6, 769.19) * mm});
            skLineSegment(sketch, "E402", {"start": v(-516.6, 769.19) * mm, "end": v(-516.6, 769.06) * mm});
            skLineSegment(sketch, "E403", {"start": v(-516.6, 769.06) * mm, "end": v(-516.6, 768.94) * mm});
            skLineSegment(sketch, "E404", {"start": v(-516.6, 768.94) * mm, "end": v(-516.6, 768.82) * mm});
            skLineSegment(sketch, "E405", {"start": v(-516.6, 768.82) * mm, "end": v(-516.6, 768.7) * mm});
            skLineSegment(sketch, "E406", {"start": v(-516.6, 768.7) * mm, "end": v(-516.6, 768.57) * mm});
            skLineSegment(sketch, "E407", {"start": v(-516.6, 768.57) * mm, "end": v(-516.6, 768.44) * mm});
            skLineSegment(sketch, "E408", {"start": v(-516.6, 768.44) * mm, "end": v(-516.62, 768.32) * mm});
            skLineSegment(sketch, "E409", {"start": v(-516.62, 768.32) * mm, "end": v(-516.63, 768.2) * mm});
            skLineSegment(sketch, "E410", {"start": v(-516.63, 768.2) * mm, "end": v(-516.64, 768.06) * mm});
            skLineSegment(sketch, "E411", {"start": v(-516.64, 768.06) * mm, "end": v(-516.65, 767.94) * mm});
            skLineSegment(sketch, "E412", {"start": v(-516.65, 767.94) * mm, "end": v(-516.66, 767.8) * mm});
            skLineSegment(sketch, "E413", {"start": v(-516.66, 767.8) * mm, "end": v(-516.68, 767.68) * mm});
            skLineSegment(sketch, "E414", {"start": v(-516.68, 767.68) * mm, "end": v(-516.7, 767.55) * mm});
            skLineSegment(sketch, "E415", {"start": v(-516.7, 767.55) * mm, "end": v(-516.71, 767.42) * mm});
            skLineSegment(sketch, "E416", {"start": v(-516.71, 767.42) * mm, "end": v(-516.74, 767.3) * mm});
            skLineSegment(sketch, "E417", {"start": v(-516.74, 767.3) * mm, "end": v(-516.76, 767.17) * mm});
            skLineSegment(sketch, "E418", {"start": v(-516.76, 767.17) * mm, "end": v(-516.78, 767.04) * mm});
            skLineSegment(sketch, "E419", {"start": v(-516.78, 767.04) * mm, "end": v(-516.8, 766.9) * mm});
            skLineSegment(sketch, "E420", {"start": v(-516.8, 766.9) * mm, "end": v(-516.83, 766.78) * mm});
            skLineSegment(sketch, "E421", {"start": v(-516.83, 766.78) * mm, "end": v(-516.86, 766.65) * mm});
            skLineSegment(sketch, "E422", {"start": v(-516.86, 766.65) * mm, "end": v(-517.51, 766.46) * mm});
            skLineSegment(sketch, "E423", {"start": v(-517.51, 766.46) * mm, "end": v(-518.16, 766.3) * mm});
            skLineSegment(sketch, "E424", {"start": v(-518.16, 766.3) * mm, "end": v(-518.25, 766.4) * mm});
            skLineSegment(sketch, "E425", {"start": v(-518.25, 766.4) * mm, "end": v(-518.34, 766.5) * mm});
            skLineSegment(sketch, "E426", {"start": v(-518.34, 766.5) * mm, "end": v(-518.43, 766.6) * mm});
            skLineSegment(sketch, "E427", {"start": v(-518.43, 766.6) * mm, "end": v(-518.51, 766.7) * mm});
            skLineSegment(sketch, "E428", {"start": v(-518.51, 766.7) * mm, "end": v(-518.6, 766.8) * mm});
            skLineSegment(sketch, "E429", {"start": v(-518.6, 766.8) * mm, "end": v(-518.68, 766.9) * mm});
            skLineSegment(sketch, "E430", {"start": v(-518.68, 766.9) * mm, "end": v(-518.76, 767) * mm});
            skLineSegment(sketch, "E431", {"start": v(-518.76, 767) * mm, "end": v(-518.84, 767.1) * mm});
            skLineSegment(sketch, "E432", {"start": v(-518.84, 767.1) * mm, "end": v(-518.92, 767.2) * mm});
            skLineSegment(sketch, "E433", {"start": v(-518.92, 767.2) * mm, "end": v(-519, 767.3) * mm});
            skLineSegment(sketch, "E434", {"start": v(-519, 767.3) * mm, "end": v(-519.07, 767.41) * mm});
            skLineSegment(sketch, "E435", {"start": v(-519.07, 767.41) * mm, "end": v(-519.14, 767.52) * mm});
            skLineSegment(sketch, "E436", {"start": v(-519.14, 767.52) * mm, "end": v(-519.21, 767.62) * mm});
            skLineSegment(sketch, "E437", {"start": v(-519.21, 767.62) * mm, "end": v(-519.28, 767.73) * mm});
            skLineSegment(sketch, "E438", {"start": v(-519.28, 767.73) * mm, "end": v(-519.35, 767.83) * mm});
            skLineSegment(sketch, "E439", {"start": v(-519.35, 767.83) * mm, "end": v(-519.41, 767.94) * mm});
            skLineSegment(sketch, "E440", {"start": v(-519.41, 767.94) * mm, "end": v(-519.48, 768.04) * mm});
            skLineSegment(sketch, "E441", {"start": v(-519.48, 768.04) * mm, "end": v(-519.54, 768.15) * mm});
            skLineSegment(sketch, "E442", {"start": v(-519.54, 768.15) * mm, "end": v(-519.6, 768.26) * mm});
            skLineSegment(sketch, "E443", {"start": v(-519.6, 768.26) * mm, "end": v(-519.66, 768.36) * mm});
            skLineSegment(sketch, "E444", {"start": v(-519.66, 768.36) * mm, "end": v(-519.72, 768.47) * mm});
            skLineSegment(sketch, "E445", {"start": v(-519.72, 768.47) * mm, "end": v(-519.78, 768.58) * mm});
            skLineSegment(sketch, "E446", {"start": v(-519.78, 768.58) * mm, "end": v(-519.83, 768.69) * mm});
            skLineSegment(sketch, "E447", {"start": v(-519.83, 768.69) * mm, "end": v(-519.88, 768.8) * mm});
            skLineSegment(sketch, "E448", {"start": v(-519.88, 768.8) * mm, "end": v(-519.93, 768.9) * mm});
            skLineSegment(sketch, "E449", {"start": v(-519.93, 768.9) * mm, "end": v(-519.98, 769.02) * mm});
            skLineSegment(sketch, "E450", {"start": v(-519.98, 769.02) * mm, "end": v(-520.03, 769.13) * mm});
            skLineSegment(sketch, "E451", {"start": v(-520.03, 769.13) * mm, "end": v(-520.07, 769.24) * mm});
            skLineSegment(sketch, "E452", {"start": v(-520.07, 769.24) * mm, "end": v(-520.12, 769.35) * mm});
            skLineSegment(sketch, "E453", {"start": v(-520.12, 769.35) * mm, "end": v(-520.18, 769.46) * mm});
            skLineSegment(sketch, "E454", {"start": v(-520.18, 769.46) * mm, "end": v(-520.3, 770.08) * mm});
            skLineSegment(sketch, "E455", {"start": v(-520.3, 770.08) * mm, "end": v(-522.08, 769.8) * mm});
            skLineSegment(sketch, "E456", {"start": v(-522.08, 769.8) * mm, "end": v(-522, 769.17) * mm});
            skLineSegment(sketch, "E457", {"start": v(-522, 769.17) * mm, "end": v(-522.02, 769.05) * mm});
            skLineSegment(sketch, "E458", {"start": v(-522.02, 769.05) * mm, "end": v(-522.03, 768.93) * mm});
            skLineSegment(sketch, "E459", {"start": v(-522.03, 768.93) * mm, "end": v(-522.04, 768.8) * mm});
            skLineSegment(sketch, "E460", {"start": v(-522.04, 768.8) * mm, "end": v(-522.05, 768.69) * mm});
            skLineSegment(sketch, "E461", {"start": v(-522.05, 768.69) * mm, "end": v(-522.06, 768.57) * mm});
            skLineSegment(sketch, "E462", {"start": v(-522.06, 768.57) * mm, "end": v(-522.07, 768.45) * mm});
            skLineSegment(sketch, "E463", {"start": v(-522.07, 768.45) * mm, "end": v(-522.1, 768.33) * mm});
            skLineSegment(sketch, "E464", {"start": v(-522.1, 768.33) * mm, "end": v(-522.1, 768.2) * mm});
            skLineSegment(sketch, "E465", {"start": v(-522.1, 768.2) * mm, "end": v(-522.13, 768.1) * mm});
            skLineSegment(sketch, "E466", {"start": v(-522.13, 768.1) * mm, "end": v(-522.15, 767.97) * mm});
            skLineSegment(sketch, "E467", {"start": v(-522.15, 767.97) * mm, "end": v(-522.17, 767.85) * mm});
            skLineSegment(sketch, "E468", {"start": v(-522.17, 767.85) * mm, "end": v(-522.2, 767.73) * mm});
            skLineSegment(sketch, "E469", {"start": v(-522.2, 767.73) * mm, "end": v(-522.23, 767.6) * mm});
            skLineSegment(sketch, "E470", {"start": v(-522.23, 767.6) * mm, "end": v(-522.25, 767.49) * mm});
            skLineSegment(sketch, "E471", {"start": v(-522.25, 767.49) * mm, "end": v(-522.29, 767.37) * mm});
            skLineSegment(sketch, "E472", {"start": v(-522.29, 767.37) * mm, "end": v(-522.32, 767.24) * mm});
            skLineSegment(sketch, "E473", {"start": v(-522.32, 767.24) * mm, "end": v(-522.35, 767.12) * mm});
            skLineSegment(sketch, "E474", {"start": v(-522.35, 767.12) * mm, "end": v(-522.39, 767) * mm});
            skLineSegment(sketch, "E475", {"start": v(-522.39, 767) * mm, "end": v(-522.42, 766.88) * mm});
            skLineSegment(sketch, "E476", {"start": v(-522.42, 766.88) * mm, "end": v(-522.46, 766.76) * mm});
            skLineSegment(sketch, "E477", {"start": v(-522.46, 766.76) * mm, "end": v(-522.5, 766.64) * mm});
            skLineSegment(sketch, "E478", {"start": v(-522.5, 766.64) * mm, "end": v(-522.55, 766.52) * mm});
            skLineSegment(sketch, "E479", {"start": v(-522.55, 766.52) * mm, "end": v(-522.6, 766.4) * mm});
            skLineSegment(sketch, "E480", {"start": v(-522.6, 766.4) * mm, "end": v(-522.64, 766.27) * mm});
            skLineSegment(sketch, "E481", {"start": v(-522.64, 766.27) * mm, "end": v(-522.68, 766.15) * mm});
            skLineSegment(sketch, "E482", {"start": v(-522.68, 766.15) * mm, "end": v(-522.73, 766.03) * mm});
            skLineSegment(sketch, "E483", {"start": v(-522.73, 766.03) * mm, "end": v(-522.78, 765.9) * mm});
            skLineSegment(sketch, "E484", {"start": v(-522.78, 765.9) * mm, "end": v(-522.83, 765.78) * mm});
            skLineSegment(sketch, "E485", {"start": v(-522.83, 765.78) * mm, "end": v(-522.88, 765.66) * mm});
            skLineSegment(sketch, "E486", {"start": v(-522.88, 765.66) * mm, "end": v(-522.94, 765.54) * mm});
            skLineSegment(sketch, "E487", {"start": v(-522.94, 765.54) * mm, "end": v(-523.61, 765.5) * mm});
            skLineSegment(sketch, "E488", {"start": v(-523.61, 765.5) * mm, "end": v(-524.28, 765.47) * mm});
            skLineSegment(sketch, "E489", {"start": v(-524.28, 765.47) * mm, "end": v(-524.35, 765.59) * mm});
            skLineSegment(sketch, "E490", {"start": v(-524.35, 765.59) * mm, "end": v(-524.42, 765.7) * mm});
            skLineSegment(sketch, "E491", {"start": v(-524.42, 765.7) * mm, "end": v(-524.48, 765.82) * mm});
            skLineSegment(sketch, "E492", {"start": v(-524.48, 765.82) * mm, "end": v(-524.54, 765.93) * mm});
            skLineSegment(sketch, "E493", {"start": v(-524.54, 765.93) * mm, "end": v(-524.6, 766.05) * mm});
            skLineSegment(sketch, "E494", {"start": v(-524.6, 766.05) * mm, "end": v(-524.66, 766.17) * mm});
            skLineSegment(sketch, "E495", {"start": v(-524.66, 766.17) * mm, "end": v(-524.72, 766.28) * mm});
            skLineSegment(sketch, "E496", {"start": v(-524.72, 766.28) * mm, "end": v(-524.78, 766.4) * mm});
            skLineSegment(sketch, "E497", {"start": v(-524.78, 766.4) * mm, "end": v(-524.83, 766.52) * mm});
            skLineSegment(sketch, "E498", {"start": v(-524.83, 766.52) * mm, "end": v(-524.88, 766.63) * mm});
            skLineSegment(sketch, "E499", {"start": v(-524.88, 766.63) * mm, "end": v(-524.94, 766.75) * mm});
            skLineSegment(sketch, "E500", {"start": v(-524.94, 766.75) * mm, "end": v(-524.99, 766.87) * mm});
            skLineSegment(sketch, "E501", {"start": v(-524.99, 766.87) * mm, "end": v(-525.03, 766.98) * mm});
            skLineSegment(sketch, "E502", {"start": v(-525.03, 766.98) * mm, "end": v(-525.08, 767.1) * mm});
            skLineSegment(sketch, "E503", {"start": v(-525.08, 767.1) * mm, "end": v(-525.13, 767.22) * mm});
            skLineSegment(sketch, "E504", {"start": v(-525.13, 767.22) * mm, "end": v(-525.17, 767.33) * mm});
            skLineSegment(sketch, "E505", {"start": v(-525.17, 767.33) * mm, "end": v(-525.2, 767.45) * mm});
            skLineSegment(sketch, "E506", {"start": v(-525.2, 767.45) * mm, "end": v(-525.25, 767.57) * mm});
            skLineSegment(sketch, "E507", {"start": v(-525.25, 767.57) * mm, "end": v(-525.29, 767.69) * mm});
            skLineSegment(sketch, "E508", {"start": v(-525.29, 767.69) * mm, "end": v(-525.32, 767.8) * mm});
            skLineSegment(sketch, "E509", {"start": v(-525.32, 767.8) * mm, "end": v(-525.36, 767.92) * mm});
            skLineSegment(sketch, "E510", {"start": v(-525.36, 767.92) * mm, "end": v(-525.39, 768.04) * mm});
            skLineSegment(sketch, "E511", {"start": v(-525.39, 768.04) * mm, "end": v(-525.42, 768.16) * mm});
            skLineSegment(sketch, "E512", {"start": v(-525.42, 768.16) * mm, "end": v(-525.45, 768.27) * mm});
            skLineSegment(sketch, "E513", {"start": v(-525.45, 768.27) * mm, "end": v(-525.48, 768.4) * mm});
            skLineSegment(sketch, "E514", {"start": v(-525.48, 768.4) * mm, "end": v(-525.5, 768.5) * mm});
            skLineSegment(sketch, "E515", {"start": v(-525.5, 768.5) * mm, "end": v(-525.52, 768.63) * mm});
            skLineSegment(sketch, "E516", {"start": v(-525.52, 768.63) * mm, "end": v(-525.54, 768.74) * mm});
            skLineSegment(sketch, "E517", {"start": v(-525.54, 768.74) * mm, "end": v(-525.56, 768.86) * mm});
            skLineSegment(sketch, "E518", {"start": v(-525.56, 768.86) * mm, "end": v(-525.6, 768.98) * mm});
            skLineSegment(sketch, "E519", {"start": v(-525.6, 768.98) * mm, "end": v(-525.59, 769.62) * mm});
            skLineSegment(sketch, "E520", {"start": v(-525.59, 769.62) * mm, "end": v(-527.38, 769.71) * mm});
            skLineSegment(sketch, "E521", {"start": v(-527.38, 769.71) * mm, "end": v(-527.44, 769.08) * mm});
            skLineSegment(sketch, "E522", {"start": v(-527.44, 769.08) * mm, "end": v(-527.5, 768.96) * mm});
            skLineSegment(sketch, "E523", {"start": v(-527.5, 768.96) * mm, "end": v(-527.52, 768.85) * mm});
            skLineSegment(sketch, "E524", {"start": v(-527.52, 768.85) * mm, "end": v(-527.55, 768.73) * mm});
            skLineSegment(sketch, "E525", {"start": v(-527.55, 768.73) * mm, "end": v(-527.59, 768.62) * mm});
            skLineSegment(sketch, "E526", {"start": v(-527.59, 768.62) * mm, "end": v(-527.63, 768.5) * mm});
            skLineSegment(sketch, "E527", {"start": v(-527.63, 768.5) * mm, "end": v(-527.66, 768.39) * mm});
            skLineSegment(sketch, "E528", {"start": v(-527.66, 768.39) * mm, "end": v(-527.7, 768.28) * mm});
            skLineSegment(sketch, "E529", {"start": v(-527.7, 768.28) * mm, "end": v(-527.75, 768.16) * mm});
            skLineSegment(sketch, "E530", {"start": v(-527.75, 768.16) * mm, "end": v(-527.8, 768.05) * mm});
            skLineSegment(sketch, "E531", {"start": v(-527.8, 768.05) * mm, "end": v(-527.84, 767.93) * mm});
            skLineSegment(sketch, "E532", {"start": v(-527.84, 767.93) * mm, "end": v(-527.89, 767.82) * mm});
            skLineSegment(sketch, "E533", {"start": v(-527.89, 767.82) * mm, "end": v(-527.94, 767.7) * mm});
            skLineSegment(sketch, "E534", {"start": v(-527.94, 767.7) * mm, "end": v(-527.99, 767.6) * mm});
            skLineSegment(sketch, "E535", {"start": v(-527.99, 767.6) * mm, "end": v(-528.04, 767.48) * mm});
            skLineSegment(sketch, "E536", {"start": v(-528.04, 767.48) * mm, "end": v(-528.1, 767.37) * mm});
            skLineSegment(sketch, "E537", {"start": v(-528.1, 767.37) * mm, "end": v(-528.15, 767.26) * mm});
            skLineSegment(sketch, "E538", {"start": v(-528.15, 767.26) * mm, "end": v(-528.21, 767.15) * mm});
            skLineSegment(sketch, "E539", {"start": v(-528.21, 767.15) * mm, "end": v(-528.27, 767.04) * mm});
            skLineSegment(sketch, "E540", {"start": v(-528.27, 767.04) * mm, "end": v(-528.33, 766.93) * mm});
            skLineSegment(sketch, "E541", {"start": v(-528.33, 766.93) * mm, "end": v(-528.4, 766.82) * mm});
            skLineSegment(sketch, "E542", {"start": v(-528.4, 766.82) * mm, "end": v(-528.46, 766.7) * mm});
            skLineSegment(sketch, "E543", {"start": v(-528.46, 766.7) * mm, "end": v(-528.53, 766.6) * mm});
            skLineSegment(sketch, "E544", {"start": v(-528.53, 766.6) * mm, "end": v(-528.6, 766.49) * mm});
            skLineSegment(sketch, "E545", {"start": v(-528.6, 766.49) * mm, "end": v(-528.66, 766.37) * mm});
            skLineSegment(sketch, "E546", {"start": v(-528.66, 766.37) * mm, "end": v(-528.74, 766.27) * mm});
            skLineSegment(sketch, "E547", {"start": v(-528.74, 766.27) * mm, "end": v(-528.8, 766.16) * mm});
            skLineSegment(sketch, "E548", {"start": v(-528.8, 766.16) * mm, "end": v(-528.88, 766.05) * mm});
            skLineSegment(sketch, "E549", {"start": v(-528.88, 766.05) * mm, "end": v(-528.96, 765.94) * mm});
            skLineSegment(sketch, "E550", {"start": v(-528.96, 765.94) * mm, "end": v(-529.03, 765.83) * mm});
            skLineSegment(sketch, "E551", {"start": v(-529.03, 765.83) * mm, "end": v(-529.11, 765.72) * mm});
            skLineSegment(sketch, "E552", {"start": v(-529.11, 765.72) * mm, "end": v(-529.78, 765.82) * mm});
            skLineSegment(sketch, "E553", {"start": v(-529.78, 765.82) * mm, "end": v(-530.45, 765.93) * mm});
            skLineSegment(sketch, "E554", {"start": v(-530.45, 765.93) * mm, "end": v(-530.49, 766.06) * mm});
            skLineSegment(sketch, "E555", {"start": v(-530.49, 766.06) * mm, "end": v(-530.53, 766.19) * mm});
            skLineSegment(sketch, "E556", {"start": v(-530.53, 766.19) * mm, "end": v(-530.56, 766.31) * mm});
            skLineSegment(sketch, "E557", {"start": v(-530.56, 766.31) * mm, "end": v(-530.6, 766.44) * mm});
            skLineSegment(sketch, "E558", {"start": v(-530.6, 766.44) * mm, "end": v(-530.64, 766.57) * mm});
            skLineSegment(sketch, "E559", {"start": v(-530.64, 766.57) * mm, "end": v(-530.67, 766.7) * mm});
            skLineSegment(sketch, "E560", {"start": v(-530.67, 766.7) * mm, "end": v(-530.7, 766.82) * mm});
            skLineSegment(sketch, "E561", {"start": v(-530.7, 766.82) * mm, "end": v(-530.73, 766.95) * mm});
            skLineSegment(sketch, "E562", {"start": v(-530.73, 766.95) * mm, "end": v(-530.76, 767.07) * mm});
            skLineSegment(sketch, "E563", {"start": v(-530.76, 767.07) * mm, "end": v(-530.8, 767.2) * mm});
            skLineSegment(sketch, "E564", {"start": v(-530.8, 767.2) * mm, "end": v(-530.82, 767.32) * mm});
            skLineSegment(sketch, "E565", {"start": v(-530.82, 767.32) * mm, "end": v(-530.84, 767.45) * mm});
            skLineSegment(sketch, "E566", {"start": v(-530.84, 767.45) * mm, "end": v(-530.86, 767.57) * mm});
            skLineSegment(sketch, "E567", {"start": v(-530.86, 767.57) * mm, "end": v(-530.89, 767.7) * mm});
            skLineSegment(sketch, "E568", {"start": v(-530.89, 767.7) * mm, "end": v(-530.9, 767.82) * mm});
            skLineSegment(sketch, "E569", {"start": v(-530.9, 767.82) * mm, "end": v(-530.92, 767.94) * mm});
            skLineSegment(sketch, "E570", {"start": v(-530.92, 767.94) * mm, "end": v(-530.94, 768.07) * mm});
            skLineSegment(sketch, "E571", {"start": v(-530.94, 768.07) * mm, "end": v(-530.95, 768.19) * mm});
            skLineSegment(sketch, "E572", {"start": v(-530.95, 768.19) * mm, "end": v(-530.97, 768.3) * mm});
            skLineSegment(sketch, "E573", {"start": v(-530.97, 768.3) * mm, "end": v(-530.98, 768.43) * mm});
            skLineSegment(sketch, "E574", {"start": v(-530.98, 768.43) * mm, "end": v(-530.99, 768.55) * mm});
            skLineSegment(sketch, "E575", {"start": v(-530.99, 768.55) * mm, "end": v(-531, 768.68) * mm});
            skLineSegment(sketch, "E576", {"start": v(-531, 768.68) * mm, "end": v(-531, 768.8) * mm});
            skLineSegment(sketch, "E577", {"start": v(-531, 768.8) * mm, "end": v(-531, 768.92) * mm});
            skLineSegment(sketch, "E578", {"start": v(-531, 768.92) * mm, "end": v(-531, 769.04) * mm});
            skLineSegment(sketch, "E579", {"start": v(-531, 769.04) * mm, "end": v(-531, 769.16) * mm});
            skLineSegment(sketch, "E580", {"start": v(-531, 769.16) * mm, "end": v(-531, 769.28) * mm});
            skLineSegment(sketch, "E581", {"start": v(-531, 769.28) * mm, "end": v(-531, 769.4) * mm});
            skLineSegment(sketch, "E582", {"start": v(-531, 769.4) * mm, "end": v(-530.99, 769.52) * mm});
            skLineSegment(sketch, "E583", {"start": v(-530.99, 769.52) * mm, "end": v(-531, 769.64) * mm});
            skLineSegment(sketch, "E584", {"start": v(-531, 769.64) * mm, "end": v(-530.86, 770.26) * mm});
            skLineSegment(sketch, "E585", {"start": v(-530.86, 770.26) * mm, "end": v(-532.6, 770.73) * mm});
            skLineSegment(sketch, "E586", {"start": v(-532.6, 770.73) * mm, "end": v(-532.78, 770.12) * mm});
            skLineSegment(sketch, "E587", {"start": v(-532.78, 770.12) * mm, "end": v(-532.85, 770.02) * mm});
            skLineSegment(sketch, "E588", {"start": v(-532.85, 770.02) * mm, "end": v(-532.91, 769.91) * mm});
            skLineSegment(sketch, "E589", {"start": v(-532.91, 769.91) * mm, "end": v(-532.96, 769.8) * mm});
            skLineSegment(sketch, "E590", {"start": v(-532.96, 769.8) * mm, "end": v(-533.02, 769.7) * mm});
            skLineSegment(sketch, "E591", {"start": v(-533.02, 769.7) * mm, "end": v(-533.08, 769.6) * mm});
            skLineSegment(sketch, "E592", {"start": v(-533.08, 769.6) * mm, "end": v(-533.14, 769.5) * mm});
            skLineSegment(sketch, "E593", {"start": v(-533.14, 769.5) * mm, "end": v(-533.2, 769.39) * mm});
            skLineSegment(sketch, "E594", {"start": v(-533.2, 769.39) * mm, "end": v(-533.27, 769.29) * mm});
            skLineSegment(sketch, "E595", {"start": v(-533.27, 769.29) * mm, "end": v(-533.34, 769.19) * mm});
            skLineSegment(sketch, "E596", {"start": v(-533.34, 769.19) * mm, "end": v(-533.4, 769.08) * mm});
            skLineSegment(sketch, "E597", {"start": v(-533.4, 769.08) * mm, "end": v(-533.48, 768.98) * mm});
            skLineSegment(sketch, "E598", {"start": v(-533.48, 768.98) * mm, "end": v(-533.55, 768.88) * mm});
            skLineSegment(sketch, "E599", {"start": v(-533.55, 768.88) * mm, "end": v(-533.62, 768.78) * mm});
            skLineSegment(sketch, "E600", {"start": v(-533.62, 768.78) * mm, "end": v(-533.7, 768.68) * mm});
            skLineSegment(sketch, "E601", {"start": v(-533.7, 768.68) * mm, "end": v(-533.78, 768.59) * mm});
            skLineSegment(sketch, "E602", {"start": v(-533.78, 768.59) * mm, "end": v(-533.86, 768.49) * mm});
            skLineSegment(sketch, "E603", {"start": v(-533.86, 768.49) * mm, "end": v(-533.94, 768.4) * mm});
            skLineSegment(sketch, "E604", {"start": v(-533.94, 768.4) * mm, "end": v(-534.02, 768.3) * mm});
            skLineSegment(sketch, "E605", {"start": v(-534.02, 768.3) * mm, "end": v(-534.1, 768.2) * mm});
            skLineSegment(sketch, "E606", {"start": v(-534.1, 768.2) * mm, "end": v(-534.19, 768.1) * mm});
            skLineSegment(sketch, "E607", {"start": v(-534.19, 768.1) * mm, "end": v(-534.27, 768.01) * mm});
            skLineSegment(sketch, "E608", {"start": v(-534.27, 768.01) * mm, "end": v(-534.36, 767.92) * mm});
            skLineSegment(sketch, "E609", {"start": v(-534.36, 767.92) * mm, "end": v(-534.45, 767.82) * mm});
            skLineSegment(sketch, "E610", {"start": v(-534.45, 767.82) * mm, "end": v(-534.54, 767.73) * mm});
            skLineSegment(sketch, "E611", {"start": v(-534.54, 767.73) * mm, "end": v(-534.63, 767.64) * mm});
            skLineSegment(sketch, "E612", {"start": v(-534.63, 767.64) * mm, "end": v(-534.73, 767.55) * mm});
            skLineSegment(sketch, "E613", {"start": v(-534.73, 767.55) * mm, "end": v(-534.82, 767.46) * mm});
            skLineSegment(sketch, "E614", {"start": v(-534.82, 767.46) * mm, "end": v(-534.92, 767.37) * mm});
            skLineSegment(sketch, "E615", {"start": v(-534.92, 767.37) * mm, "end": v(-535.02, 767.28) * mm});
            skLineSegment(sketch, "E616", {"start": v(-535.02, 767.28) * mm, "end": v(-535.11, 767.19) * mm});
            skLineSegment(sketch, "E617", {"start": v(-535.11, 767.19) * mm, "end": v(-535.75, 767.42) * mm});
            skLineSegment(sketch, "E618", {"start": v(-535.75, 767.42) * mm, "end": v(-536.38, 767.67) * mm});
            skLineSegment(sketch, "E619", {"start": v(-536.38, 767.67) * mm, "end": v(-536.39, 767.8) * mm});
            skLineSegment(sketch, "E620", {"start": v(-536.39, 767.8) * mm, "end": v(-536.4, 767.93) * mm});
            skLineSegment(sketch, "E621", {"start": v(-536.4, 767.93) * mm, "end": v(-536.41, 768.07) * mm});
            skLineSegment(sketch, "E622", {"start": v(-536.41, 768.07) * mm, "end": v(-536.42, 768.2) * mm});
            skLineSegment(sketch, "E623", {"start": v(-536.42, 768.2) * mm, "end": v(-536.43, 768.33) * mm});
            skLineSegment(sketch, "E624", {"start": v(-536.43, 768.33) * mm, "end": v(-536.44, 768.46) * mm});
            skLineSegment(sketch, "E625", {"start": v(-536.44, 768.46) * mm, "end": v(-536.44, 768.59) * mm});
            skLineSegment(sketch, "E626", {"start": v(-536.44, 768.59) * mm, "end": v(-536.45, 768.72) * mm});
            skLineSegment(sketch, "E627", {"start": v(-536.45, 768.72) * mm, "end": v(-536.45, 768.85) * mm});
            skLineSegment(sketch, "E628", {"start": v(-536.45, 768.85) * mm, "end": v(-536.45, 768.97) * mm});
            skLineSegment(sketch, "E629", {"start": v(-536.45, 768.97) * mm, "end": v(-536.45, 769.1) * mm});
            skLineSegment(sketch, "E630", {"start": v(-536.45, 769.1) * mm, "end": v(-536.45, 769.23) * mm});
            skLineSegment(sketch, "E631", {"start": v(-536.45, 769.23) * mm, "end": v(-536.44, 769.36) * mm});
            skLineSegment(sketch, "E632", {"start": v(-536.44, 769.36) * mm, "end": v(-536.44, 769.48) * mm});
            skLineSegment(sketch, "E633", {"start": v(-536.44, 769.48) * mm, "end": v(-536.43, 769.6) * mm});
            skLineSegment(sketch, "E634", {"start": v(-536.43, 769.6) * mm, "end": v(-536.42, 769.73) * mm});
            skLineSegment(sketch, "E635", {"start": v(-536.42, 769.73) * mm, "end": v(-536.41, 769.86) * mm});
            skLineSegment(sketch, "E636", {"start": v(-536.41, 769.86) * mm, "end": v(-536.4, 769.98) * mm});
            skLineSegment(sketch, "E637", {"start": v(-536.4, 769.98) * mm, "end": v(-536.39, 770.1) * mm});
            skLineSegment(sketch, "E638", {"start": v(-536.39, 770.1) * mm, "end": v(-536.37, 770.22) * mm});
            skLineSegment(sketch, "E639", {"start": v(-536.37, 770.22) * mm, "end": v(-536.36, 770.34) * mm});
            skLineSegment(sketch, "E640", {"start": v(-536.36, 770.34) * mm, "end": v(-536.34, 770.46) * mm});
            skLineSegment(sketch, "E641", {"start": v(-536.34, 770.46) * mm, "end": v(-536.32, 770.58) * mm});
            skLineSegment(sketch, "E642", {"start": v(-536.32, 770.58) * mm, "end": v(-536.3, 770.7) * mm});
            skLineSegment(sketch, "E643", {"start": v(-536.3, 770.7) * mm, "end": v(-536.27, 770.82) * mm});
            skLineSegment(sketch, "E644", {"start": v(-536.27, 770.82) * mm, "end": v(-536.25, 770.94) * mm});
            skLineSegment(sketch, "E645", {"start": v(-536.25, 770.94) * mm, "end": v(-536.22, 771.06) * mm});
            skLineSegment(sketch, "E646", {"start": v(-536.22, 771.06) * mm, "end": v(-536.2, 771.17) * mm});
            skLineSegment(sketch, "E647", {"start": v(-536.2, 771.17) * mm, "end": v(-536.16, 771.29) * mm});
            skLineSegment(sketch, "E648", {"start": v(-536.16, 771.29) * mm, "end": v(-536.15, 771.4) * mm});
            skLineSegment(sketch, "E649", {"start": v(-536.15, 771.4) * mm, "end": v(-535.88, 771.99) * mm});
            skLineSegment(sketch, "E650", {"start": v(-535.88, 771.99) * mm, "end": v(-537.48, 772.8) * mm});
            skLineSegment(sketch, "E651", {"start": v(-537.48, 772.8) * mm, "end": v(-537.8, 772.25) * mm});
            skLineSegment(sketch, "E652", {"start": v(-537.8, 772.25) * mm, "end": v(-537.88, 772.16) * mm});
            skLineSegment(sketch, "E653", {"start": v(-537.88, 772.16) * mm, "end": v(-537.96, 772.07) * mm});
            skLineSegment(sketch, "E654", {"start": v(-537.96, 772.07) * mm, "end": v(-538.04, 771.98) * mm});
            skLineSegment(sketch, "E655", {"start": v(-538.04, 771.98) * mm, "end": v(-538.11, 771.89) * mm});
            skLineSegment(sketch, "E656", {"start": v(-538.11, 771.89) * mm, "end": v(-538.2, 771.8) * mm});
            skLineSegment(sketch, "E657", {"start": v(-538.2, 771.8) * mm, "end": v(-538.27, 771.71) * mm});
            skLineSegment(sketch, "E658", {"start": v(-538.27, 771.71) * mm, "end": v(-538.36, 771.62) * mm});
            skLineSegment(sketch, "E659", {"start": v(-538.36, 771.62) * mm, "end": v(-538.44, 771.54) * mm});
            skLineSegment(sketch, "E660", {"start": v(-538.44, 771.54) * mm, "end": v(-538.53, 771.45) * mm});
            skLineSegment(sketch, "E661", {"start": v(-538.53, 771.45) * mm, "end": v(-538.62, 771.37) * mm});
            skLineSegment(sketch, "E662", {"start": v(-538.62, 771.37) * mm, "end": v(-538.7, 771.28) * mm});
            skLineSegment(sketch, "E663", {"start": v(-538.7, 771.28) * mm, "end": v(-538.8, 771.2) * mm});
            skLineSegment(sketch, "E664", {"start": v(-538.8, 771.2) * mm, "end": v(-538.9, 771.12) * mm});
            skLineSegment(sketch, "E665", {"start": v(-538.9, 771.12) * mm, "end": v(-538.99, 771.04) * mm});
            skLineSegment(sketch, "E666", {"start": v(-538.99, 771.04) * mm, "end": v(-539.08, 770.96) * mm});
            skLineSegment(sketch, "E667", {"start": v(-539.08, 770.96) * mm, "end": v(-539.18, 770.88) * mm});
            skLineSegment(sketch, "E668", {"start": v(-539.18, 770.88) * mm, "end": v(-539.28, 770.8) * mm});
            skLineSegment(sketch, "E669", {"start": v(-539.28, 770.8) * mm, "end": v(-539.38, 770.72) * mm});
            skLineSegment(sketch, "E670", {"start": v(-539.38, 770.72) * mm, "end": v(-539.48, 770.65) * mm});
            skLineSegment(sketch, "E671", {"start": v(-539.48, 770.65) * mm, "end": v(-539.58, 770.57) * mm});
            skLineSegment(sketch, "E672", {"start": v(-539.58, 770.57) * mm, "end": v(-539.69, 770.5) * mm});
            skLineSegment(sketch, "E673", {"start": v(-539.69, 770.5) * mm, "end": v(-539.8, 770.42) * mm});
            skLineSegment(sketch, "E674", {"start": v(-539.8, 770.42) * mm, "end": v(-539.9, 770.35) * mm});
            skLineSegment(sketch, "E675", {"start": v(-539.9, 770.35) * mm, "end": v(-540, 770.28) * mm});
            skLineSegment(sketch, "E676", {"start": v(-540, 770.28) * mm, "end": v(-540.12, 770.2) * mm});
            skLineSegment(sketch, "E677", {"start": v(-540.12, 770.2) * mm, "end": v(-540.23, 770.14) * mm});
            skLineSegment(sketch, "E678", {"start": v(-540.23, 770.14) * mm, "end": v(-540.34, 770.07) * mm});
            skLineSegment(sketch, "E679", {"start": v(-540.34, 770.07) * mm, "end": v(-540.45, 770) * mm});
            skLineSegment(sketch, "E680", {"start": v(-540.45, 770) * mm, "end": v(-540.57, 769.93) * mm});
            skLineSegment(sketch, "E681", {"start": v(-540.57, 769.93) * mm, "end": v(-540.68, 769.86) * mm});
            skLineSegment(sketch, "E682", {"start": v(-540.68, 769.86) * mm, "end": v(-541.25, 770.23) * mm});
            skLineSegment(sketch, "E683", {"start": v(-541.25, 770.23) * mm, "end": v(-541.81, 770.6) * mm});
            skLineSegment(sketch, "E684", {"start": v(-541.81, 770.6) * mm, "end": v(-541.8, 770.73) * mm});
            skLineSegment(sketch, "E685", {"start": v(-541.8, 770.73) * mm, "end": v(-541.79, 770.86) * mm});
            skLineSegment(sketch, "E686", {"start": v(-541.79, 770.86) * mm, "end": v(-541.77, 771) * mm});
            skLineSegment(sketch, "E687", {"start": v(-541.77, 771) * mm, "end": v(-541.75, 771.12) * mm});
            skLineSegment(sketch, "E688", {"start": v(-541.75, 771.12) * mm, "end": v(-541.73, 771.26) * mm});
            skLineSegment(sketch, "E689", {"start": v(-541.73, 771.26) * mm, "end": v(-541.71, 771.38) * mm});
            skLineSegment(sketch, "E690", {"start": v(-541.71, 771.38) * mm, "end": v(-541.7, 771.51) * mm});
            skLineSegment(sketch, "E691", {"start": v(-541.7, 771.51) * mm, "end": v(-541.67, 771.64) * mm});
            skLineSegment(sketch, "E692", {"start": v(-541.67, 771.64) * mm, "end": v(-541.64, 771.77) * mm});
            skLineSegment(sketch, "E693", {"start": v(-541.64, 771.77) * mm, "end": v(-541.62, 771.9) * mm});
            skLineSegment(sketch, "E694", {"start": v(-541.62, 771.9) * mm, "end": v(-541.59, 772.02) * mm});
            skLineSegment(sketch, "E695", {"start": v(-541.59, 772.02) * mm, "end": v(-541.56, 772.14) * mm});
            skLineSegment(sketch, "E696", {"start": v(-541.56, 772.14) * mm, "end": v(-541.53, 772.26) * mm});
            skLineSegment(sketch, "E697", {"start": v(-541.53, 772.26) * mm, "end": v(-541.5, 772.38) * mm});
            skLineSegment(sketch, "E698", {"start": v(-541.5, 772.38) * mm, "end": v(-541.47, 772.5) * mm});
            skLineSegment(sketch, "E699", {"start": v(-541.47, 772.5) * mm, "end": v(-541.43, 772.63) * mm});
            skLineSegment(sketch, "E700", {"start": v(-541.43, 772.63) * mm, "end": v(-541.4, 772.74) * mm});
            skLineSegment(sketch, "E701", {"start": v(-541.4, 772.74) * mm, "end": v(-541.36, 772.86) * mm});
            skLineSegment(sketch, "E702", {"start": v(-541.36, 772.86) * mm, "end": v(-541.32, 772.98) * mm});
            skLineSegment(sketch, "E703", {"start": v(-541.32, 772.98) * mm, "end": v(-541.28, 773.1) * mm});
            skLineSegment(sketch, "E704", {"start": v(-541.28, 773.1) * mm, "end": v(-541.24, 773.21) * mm});
            skLineSegment(sketch, "E705", {"start": v(-541.24, 773.21) * mm, "end": v(-541.2, 773.32) * mm});
            skLineSegment(sketch, "E706", {"start": v(-541.2, 773.32) * mm, "end": v(-541.15, 773.44) * mm});
            skLineSegment(sketch, "E707", {"start": v(-541.15, 773.44) * mm, "end": v(-541.1, 773.55) * mm});
            skLineSegment(sketch, "E708", {"start": v(-541.1, 773.55) * mm, "end": v(-541.06, 773.66) * mm});
            skLineSegment(sketch, "E709", {"start": v(-541.06, 773.66) * mm, "end": v(-541, 773.77) * mm});
            skLineSegment(sketch, "E710", {"start": v(-541, 773.77) * mm, "end": v(-540.96, 773.88) * mm});
            skLineSegment(sketch, "E711", {"start": v(-540.96, 773.88) * mm, "end": v(-540.9, 773.99) * mm});
            skLineSegment(sketch, "E712", {"start": v(-540.9, 773.99) * mm, "end": v(-540.85, 774.1) * mm});
            skLineSegment(sketch, "E713", {"start": v(-540.85, 774.1) * mm, "end": v(-540.81, 774.21) * mm});
            skLineSegment(sketch, "E714", {"start": v(-540.81, 774.21) * mm, "end": v(-540.43, 774.72) * mm});
            skLineSegment(sketch, "E715", {"start": v(-540.43, 774.72) * mm, "end": v(-541.83, 775.85) * mm});
            skLineSegment(sketch, "E716", {"start": v(-541.83, 775.85) * mm, "end": v(-542.25, 775.37) * mm});
            skLineSegment(sketch, "E717", {"start": v(-542.25, 775.37) * mm, "end": v(-542.35, 775.3) * mm});
            skLineSegment(sketch, "E718", {"start": v(-542.35, 775.3) * mm, "end": v(-542.45, 775.23) * mm});
            skLineSegment(sketch, "E719", {"start": v(-542.45, 775.23) * mm, "end": v(-542.54, 775.16) * mm});
            skLineSegment(sketch, "E720", {"start": v(-542.54, 775.16) * mm, "end": v(-542.64, 775.09) * mm});
            skLineSegment(sketch, "E721", {"start": v(-542.64, 775.09) * mm, "end": v(-542.73, 775.02) * mm});
            skLineSegment(sketch, "E722", {"start": v(-542.73, 775.02) * mm, "end": v(-542.83, 774.95) * mm});
            skLineSegment(sketch, "E723", {"start": v(-542.83, 774.95) * mm, "end": v(-542.93, 774.88) * mm});
            skLineSegment(sketch, "E724", {"start": v(-542.93, 774.88) * mm, "end": v(-543.03, 774.81) * mm});
            skLineSegment(sketch, "E725", {"start": v(-543.03, 774.81) * mm, "end": v(-543.13, 774.75) * mm});
            skLineSegment(sketch, "E726", {"start": v(-543.13, 774.75) * mm, "end": v(-543.24, 774.68) * mm});
            skLineSegment(sketch, "E727", {"start": v(-543.24, 774.68) * mm, "end": v(-543.34, 774.62) * mm});
            skLineSegment(sketch, "E728", {"start": v(-543.34, 774.62) * mm, "end": v(-543.45, 774.56) * mm});
            skLineSegment(sketch, "E729", {"start": v(-543.45, 774.56) * mm, "end": v(-543.56, 774.5) * mm});
            skLineSegment(sketch, "E730", {"start": v(-543.56, 774.5) * mm, "end": v(-543.67, 774.44) * mm});
            skLineSegment(sketch, "E731", {"start": v(-543.67, 774.44) * mm, "end": v(-543.78, 774.38) * mm});
            skLineSegment(sketch, "E732", {"start": v(-543.78, 774.38) * mm, "end": v(-543.9, 774.32) * mm});
            skLineSegment(sketch, "E733", {"start": v(-543.9, 774.32) * mm, "end": v(-544, 774.26) * mm});
            skLineSegment(sketch, "E734", {"start": v(-544, 774.26) * mm, "end": v(-544.12, 774.2) * mm});
            skLineSegment(sketch, "E735", {"start": v(-544.12, 774.2) * mm, "end": v(-544.23, 774.16) * mm});
            skLineSegment(sketch, "E736", {"start": v(-544.23, 774.16) * mm, "end": v(-544.35, 774.1) * mm});
            skLineSegment(sketch, "E737", {"start": v(-544.35, 774.1) * mm, "end": v(-544.47, 774.05) * mm});
            skLineSegment(sketch, "E738", {"start": v(-544.47, 774.05) * mm, "end": v(-544.58, 774) * mm});
            skLineSegment(sketch, "E739", {"start": v(-544.58, 774) * mm, "end": v(-544.7, 773.95) * mm});
            skLineSegment(sketch, "E740", {"start": v(-544.7, 773.95) * mm, "end": v(-544.83, 773.9) * mm});
            skLineSegment(sketch, "E741", {"start": v(-544.83, 773.9) * mm, "end": v(-544.95, 773.86) * mm});
            skLineSegment(sketch, "E742", {"start": v(-544.95, 773.86) * mm, "end": v(-545.07, 773.81) * mm});
            skLineSegment(sketch, "E743", {"start": v(-545.07, 773.81) * mm, "end": v(-545.2, 773.77) * mm});
            skLineSegment(sketch, "E744", {"start": v(-545.2, 773.77) * mm, "end": v(-545.32, 773.73) * mm});
            skLineSegment(sketch, "E745", {"start": v(-545.32, 773.73) * mm, "end": v(-545.44, 773.68) * mm});
            skLineSegment(sketch, "E746", {"start": v(-545.44, 773.68) * mm, "end": v(-545.57, 773.64) * mm});
            skLineSegment(sketch, "E747", {"start": v(-545.57, 773.64) * mm, "end": v(-546.05, 774.11) * mm});
            skLineSegment(sketch, "E748", {"start": v(-546.05, 774.11) * mm, "end": v(-546.53, 774.6) * mm});
            skLineSegment(sketch, "E749", {"start": v(-546.53, 774.6) * mm, "end": v(-546.48, 774.72) * mm});
            skLineSegment(sketch, "E750", {"start": v(-546.48, 774.72) * mm, "end": v(-546.44, 774.85) * mm});
            skLineSegment(sketch, "E751", {"start": v(-546.44, 774.85) * mm, "end": v(-546.4, 774.97) * mm});
            skLineSegment(sketch, "E752", {"start": v(-546.4, 774.97) * mm, "end": v(-546.35, 775.1) * mm});
            skLineSegment(sketch, "E753", {"start": v(-546.35, 775.1) * mm, "end": v(-546.3, 775.22) * mm});
            skLineSegment(sketch, "E754", {"start": v(-546.3, 775.22) * mm, "end": v(-546.26, 775.34) * mm});
            skLineSegment(sketch, "E755", {"start": v(-546.26, 775.34) * mm, "end": v(-546.21, 775.46) * mm});
            skLineSegment(sketch, "E756", {"start": v(-546.21, 775.46) * mm, "end": v(-546.16, 775.58) * mm});
            skLineSegment(sketch, "E757", {"start": v(-546.16, 775.58) * mm, "end": v(-546.12, 775.7) * mm});
            skLineSegment(sketch, "E758", {"start": v(-546.12, 775.7) * mm, "end": v(-546.06, 775.82) * mm});
            skLineSegment(sketch, "E759", {"start": v(-546.06, 775.82) * mm, "end": v(-546.01, 775.93) * mm});
            skLineSegment(sketch, "E760", {"start": v(-546.01, 775.93) * mm, "end": v(-545.96, 776.05) * mm});
            skLineSegment(sketch, "E761", {"start": v(-545.96, 776.05) * mm, "end": v(-545.9, 776.16) * mm});
            skLineSegment(sketch, "E762", {"start": v(-545.9, 776.16) * mm, "end": v(-545.85, 776.28) * mm});
            skLineSegment(sketch, "E763", {"start": v(-545.85, 776.28) * mm, "end": v(-545.79, 776.39) * mm});
            skLineSegment(sketch, "E764", {"start": v(-545.79, 776.39) * mm, "end": v(-545.73, 776.5) * mm});
            skLineSegment(sketch, "E765", {"start": v(-545.73, 776.5) * mm, "end": v(-545.67, 776.6) * mm});
            skLineSegment(sketch, "E766", {"start": v(-545.67, 776.6) * mm, "end": v(-545.61, 776.72) * mm});
            skLineSegment(sketch, "E767", {"start": v(-545.61, 776.72) * mm, "end": v(-545.55, 776.82) * mm});
            skLineSegment(sketch, "E768", {"start": v(-545.55, 776.82) * mm, "end": v(-545.49, 776.93) * mm});
            skLineSegment(sketch, "E769", {"start": v(-545.49, 776.93) * mm, "end": v(-545.42, 777.03) * mm});
            skLineSegment(sketch, "E770", {"start": v(-545.42, 777.03) * mm, "end": v(-545.35, 777.13) * mm});
            skLineSegment(sketch, "E771", {"start": v(-545.35, 777.13) * mm, "end": v(-545.29, 777.24) * mm});
            skLineSegment(sketch, "E772", {"start": v(-545.29, 777.24) * mm, "end": v(-545.22, 777.34) * mm});
            skLineSegment(sketch, "E773", {"start": v(-545.22, 777.34) * mm, "end": v(-545.15, 777.43) * mm});
            skLineSegment(sketch, "E774", {"start": v(-545.15, 777.43) * mm, "end": v(-545.08, 777.53) * mm});
            skLineSegment(sketch, "E775", {"start": v(-545.08, 777.53) * mm, "end": v(-545, 777.63) * mm});
            skLineSegment(sketch, "E776", {"start": v(-545, 777.63) * mm, "end": v(-544.93, 777.72) * mm});
            skLineSegment(sketch, "E777", {"start": v(-544.93, 777.72) * mm, "end": v(-544.86, 777.81) * mm});
            skLineSegment(sketch, "E778", {"start": v(-544.86, 777.81) * mm, "end": v(-544.8, 777.92) * mm});
            skLineSegment(sketch, "E779", {"start": v(-544.8, 777.92) * mm, "end": v(-544.31, 778.34) * mm});
            skLineSegment(sketch, "E780", {"start": v(-544.31, 778.34) * mm, "end": v(-545.45, 779.74) * mm});
            skLineSegment(sketch, "E781", {"start": v(-545.45, 779.74) * mm, "end": v(-545.96, 779.35) * mm});
            skLineSegment(sketch, "E782", {"start": v(-545.96, 779.35) * mm, "end": v(-546.07, 779.31) * mm});
            skLineSegment(sketch, "E783", {"start": v(-546.07, 779.31) * mm, "end": v(-546.18, 779.26) * mm});
            skLineSegment(sketch, "E784", {"start": v(-546.18, 779.26) * mm, "end": v(-546.29, 779.2) * mm});
            skLineSegment(sketch, "E785", {"start": v(-546.29, 779.2) * mm, "end": v(-546.4, 779.16) * mm});
            skLineSegment(sketch, "E786", {"start": v(-546.4, 779.16) * mm, "end": v(-546.5, 779.1) * mm});
            skLineSegment(sketch, "E787", {"start": v(-546.5, 779.1) * mm, "end": v(-546.62, 779.06) * mm});
            skLineSegment(sketch, "E788", {"start": v(-546.62, 779.06) * mm, "end": v(-546.73, 779.01) * mm});
            skLineSegment(sketch, "E789", {"start": v(-546.73, 779.01) * mm, "end": v(-546.84, 778.97) * mm});
            skLineSegment(sketch, "E790", {"start": v(-546.84, 778.97) * mm, "end": v(-546.96, 778.92) * mm});
            skLineSegment(sketch, "E791", {"start": v(-546.96, 778.92) * mm, "end": v(-547.07, 778.88) * mm});
            skLineSegment(sketch, "E792", {"start": v(-547.07, 778.88) * mm, "end": v(-547.19, 778.84) * mm});
            skLineSegment(sketch, "E793", {"start": v(-547.19, 778.84) * mm, "end": v(-547.3, 778.8) * mm});
            skLineSegment(sketch, "E794", {"start": v(-547.3, 778.8) * mm, "end": v(-547.42, 778.77) * mm});
            skLineSegment(sketch, "E795", {"start": v(-547.42, 778.77) * mm, "end": v(-547.54, 778.73) * mm});
            skLineSegment(sketch, "E796", {"start": v(-547.54, 778.73) * mm, "end": v(-547.66, 778.7) * mm});
            skLineSegment(sketch, "E797", {"start": v(-547.66, 778.7) * mm, "end": v(-547.78, 778.67) * mm});
            skLineSegment(sketch, "E798", {"start": v(-547.78, 778.67) * mm, "end": v(-547.9, 778.64) * mm});
            skLineSegment(sketch, "E799", {"start": v(-547.9, 778.64) * mm, "end": v(-548.03, 778.6) * mm});
            skLineSegment(sketch, "E800", {"start": v(-548.03, 778.6) * mm, "end": v(-548.15, 778.58) * mm});
            skLineSegment(sketch, "E801", {"start": v(-548.15, 778.58) * mm, "end": v(-548.27, 778.55) * mm});
            skLineSegment(sketch, "E802", {"start": v(-548.27, 778.55) * mm, "end": v(-548.4, 778.52) * mm});
            skLineSegment(sketch, "E803", {"start": v(-548.4, 778.52) * mm, "end": v(-548.53, 778.5) * mm});
            skLineSegment(sketch, "E804", {"start": v(-548.53, 778.5) * mm, "end": v(-548.65, 778.48) * mm});
            skLineSegment(sketch, "E805", {"start": v(-548.65, 778.48) * mm, "end": v(-548.78, 778.46) * mm});
            skLineSegment(sketch, "E806", {"start": v(-548.78, 778.46) * mm, "end": v(-548.91, 778.43) * mm});
            skLineSegment(sketch, "E807", {"start": v(-548.91, 778.43) * mm, "end": v(-549.04, 778.42) * mm});
            skLineSegment(sketch, "E808", {"start": v(-549.04, 778.42) * mm, "end": v(-549.17, 778.4) * mm});
            skLineSegment(sketch, "E809", {"start": v(-549.17, 778.4) * mm, "end": v(-549.3, 778.38) * mm});
            skLineSegment(sketch, "E810", {"start": v(-549.3, 778.38) * mm, "end": v(-549.43, 778.37) * mm});
            skLineSegment(sketch, "E811", {"start": v(-549.43, 778.37) * mm, "end": v(-549.57, 778.35) * mm});
            skLineSegment(sketch, "E812", {"start": v(-549.57, 778.35) * mm, "end": v(-549.94, 778.91) * mm});
            skLineSegment(sketch, "E813", {"start": v(-549.94, 778.91) * mm, "end": v(-550.3, 779.48) * mm});
            skLineSegment(sketch, "E814", {"start": v(-550.3, 779.48) * mm, "end": v(-550.24, 779.6) * mm});
            skLineSegment(sketch, "E815", {"start": v(-550.24, 779.6) * mm, "end": v(-550.17, 779.71) * mm});
            skLineSegment(sketch, "E816", {"start": v(-550.17, 779.71) * mm, "end": v(-550.1, 779.83) * mm});
            skLineSegment(sketch, "E817", {"start": v(-550.1, 779.83) * mm, "end": v(-550.03, 779.94) * mm});
            skLineSegment(sketch, "E818", {"start": v(-550.03, 779.94) * mm, "end": v(-549.96, 780.05) * mm});
            skLineSegment(sketch, "E819", {"start": v(-549.96, 780.05) * mm, "end": v(-549.89, 780.16) * mm});
            skLineSegment(sketch, "E820", {"start": v(-549.89, 780.16) * mm, "end": v(-549.82, 780.27) * mm});
            skLineSegment(sketch, "E821", {"start": v(-549.82, 780.27) * mm, "end": v(-549.74, 780.37) * mm});
            skLineSegment(sketch, "E822", {"start": v(-549.74, 780.37) * mm, "end": v(-549.67, 780.48) * mm});
            skLineSegment(sketch, "E823", {"start": v(-549.67, 780.48) * mm, "end": v(-549.6, 780.58) * mm});
            skLineSegment(sketch, "E824", {"start": v(-549.6, 780.58) * mm, "end": v(-549.52, 780.69) * mm});
            skLineSegment(sketch, "E825", {"start": v(-549.52, 780.69) * mm, "end": v(-549.44, 780.79) * mm});
            skLineSegment(sketch, "E826", {"start": v(-549.44, 780.79) * mm, "end": v(-549.37, 780.89) * mm});
            skLineSegment(sketch, "E827", {"start": v(-549.37, 780.89) * mm, "end": v(-549.29, 780.99) * mm});
            skLineSegment(sketch, "E828", {"start": v(-549.29, 780.99) * mm, "end": v(-549.2, 781.08) * mm});
            skLineSegment(sketch, "E829", {"start": v(-549.2, 781.08) * mm, "end": v(-549.13, 781.18) * mm});
            skLineSegment(sketch, "E830", {"start": v(-549.13, 781.18) * mm, "end": v(-549.05, 781.27) * mm});
            skLineSegment(sketch, "E831", {"start": v(-549.05, 781.27) * mm, "end": v(-548.97, 781.37) * mm});
            skLineSegment(sketch, "E832", {"start": v(-548.97, 781.37) * mm, "end": v(-548.88, 781.46) * mm});
            skLineSegment(sketch, "E833", {"start": v(-548.88, 781.46) * mm, "end": v(-548.8, 781.55) * mm});
            skLineSegment(sketch, "E834", {"start": v(-548.8, 781.55) * mm, "end": v(-548.72, 781.64) * mm});
            skLineSegment(sketch, "E835", {"start": v(-548.72, 781.64) * mm, "end": v(-548.63, 781.72) * mm});
            skLineSegment(sketch, "E836", {"start": v(-548.63, 781.72) * mm, "end": v(-548.54, 781.8) * mm});
            skLineSegment(sketch, "E837", {"start": v(-548.54, 781.8) * mm, "end": v(-548.46, 781.9) * mm});
            skLineSegment(sketch, "E838", {"start": v(-548.46, 781.9) * mm, "end": v(-548.37, 781.97) * mm});
            skLineSegment(sketch, "E839", {"start": v(-548.37, 781.97) * mm, "end": v(-548.28, 782.05) * mm});
            skLineSegment(sketch, "E840", {"start": v(-548.28, 782.05) * mm, "end": v(-548.19, 782.13) * mm});
            skLineSegment(sketch, "E841", {"start": v(-548.19, 782.13) * mm, "end": v(-548.1, 782.2) * mm});
            skLineSegment(sketch, "E842", {"start": v(-548.1, 782.2) * mm, "end": v(-548, 782.28) * mm});
            skLineSegment(sketch, "E843", {"start": v(-548, 782.28) * mm, "end": v(-547.92, 782.38) * mm});
            skLineSegment(sketch, "E844", {"start": v(-547.92, 782.38) * mm, "end": v(-547.36, 782.69) * mm});
            skLineSegment(sketch, "E845", {"start": v(-547.36, 782.69) * mm, "end": v(-548.18, 784.29) * mm});
            skLineSegment(sketch, "E846", {"start": v(-548.18, 784.29) * mm, "end": v(-548.76, 784.02) * mm});
            skLineSegment(sketch, "E847", {"start": v(-548.76, 784.02) * mm, "end": v(-548.88, 784) * mm});
            skLineSegment(sketch, "E848", {"start": v(-548.88, 784) * mm, "end": v(-549, 783.98) * mm});
            skLineSegment(sketch, "E849", {"start": v(-549, 783.98) * mm, "end": v(-549.11, 783.95) * mm});
            skLineSegment(sketch, "E850", {"start": v(-549.11, 783.95) * mm, "end": v(-549.23, 783.92) * mm});
            skLineSegment(sketch, "E851", {"start": v(-549.23, 783.92) * mm, "end": v(-549.35, 783.9) * mm});
            skLineSegment(sketch, "E852", {"start": v(-549.35, 783.9) * mm, "end": v(-549.46, 783.87) * mm});
            skLineSegment(sketch, "E853", {"start": v(-549.46, 783.87) * mm, "end": v(-549.58, 783.85) * mm});
            skLineSegment(sketch, "E854", {"start": v(-549.58, 783.85) * mm, "end": v(-549.7, 783.83) * mm});
            skLineSegment(sketch, "E855", {"start": v(-549.7, 783.83) * mm, "end": v(-549.82, 783.8) * mm});
            skLineSegment(sketch, "E856", {"start": v(-549.82, 783.8) * mm, "end": v(-549.94, 783.8) * mm});
            skLineSegment(sketch, "E857", {"start": v(-549.94, 783.8) * mm, "end": v(-550.07, 783.78) * mm});
            skLineSegment(sketch, "E858", {"start": v(-550.07, 783.78) * mm, "end": v(-550.19, 783.76) * mm});
            skLineSegment(sketch, "E859", {"start": v(-550.19, 783.76) * mm, "end": v(-550.31, 783.75) * mm});
            skLineSegment(sketch, "E860", {"start": v(-550.31, 783.75) * mm, "end": v(-550.43, 783.74) * mm});
            skLineSegment(sketch, "E861", {"start": v(-550.43, 783.74) * mm, "end": v(-550.56, 783.73) * mm});
            skLineSegment(sketch, "E862", {"start": v(-550.56, 783.73) * mm, "end": v(-550.68, 783.73) * mm});
            skLineSegment(sketch, "E863", {"start": v(-550.68, 783.73) * mm, "end": v(-550.81, 783.72) * mm});
            skLineSegment(sketch, "E864", {"start": v(-550.81, 783.72) * mm, "end": v(-550.94, 783.72) * mm});
            skLineSegment(sketch, "E865", {"start": v(-550.94, 783.72) * mm, "end": v(-551.06, 783.72) * mm});
            skLineSegment(sketch, "E866", {"start": v(-551.06, 783.72) * mm, "end": v(-551.2, 783.72) * mm});
            skLineSegment(sketch, "E867", {"start": v(-551.2, 783.72) * mm, "end": v(-551.32, 783.72) * mm});
            skLineSegment(sketch, "E868", {"start": v(-551.32, 783.72) * mm, "end": v(-551.45, 783.72) * mm});
            skLineSegment(sketch, "E869", {"start": v(-551.45, 783.72) * mm, "end": v(-551.58, 783.72) * mm});
            skLineSegment(sketch, "E870", {"start": v(-551.58, 783.72) * mm, "end": v(-551.7, 783.73) * mm});
            skLineSegment(sketch, "E871", {"start": v(-551.7, 783.73) * mm, "end": v(-551.84, 783.73) * mm});
            skLineSegment(sketch, "E872", {"start": v(-551.84, 783.73) * mm, "end": v(-551.97, 783.74) * mm});
            skLineSegment(sketch, "E873", {"start": v(-551.97, 783.74) * mm, "end": v(-552.1, 783.75) * mm});
            skLineSegment(sketch, "E874", {"start": v(-552.1, 783.75) * mm, "end": v(-552.23, 783.76) * mm});
            skLineSegment(sketch, "E875", {"start": v(-552.23, 783.76) * mm, "end": v(-552.36, 783.78) * mm});
            skLineSegment(sketch, "E876", {"start": v(-552.36, 783.78) * mm, "end": v(-552.5, 783.8) * mm});
            skLineSegment(sketch, "E877", {"start": v(-552.5, 783.8) * mm, "end": v(-552.74, 784.42) * mm});
            skLineSegment(sketch, "E878", {"start": v(-552.74, 784.42) * mm, "end": v(-552.98, 785.05) * mm});
            skLineSegment(sketch, "E879", {"start": v(-552.98, 785.05) * mm, "end": v(-552.9, 785.15) * mm});
            skLineSegment(sketch, "E880", {"start": v(-552.9, 785.15) * mm, "end": v(-552.8, 785.25) * mm});
            skLineSegment(sketch, "E881", {"start": v(-552.8, 785.25) * mm, "end": v(-552.71, 785.34) * mm});
            skLineSegment(sketch, "E882", {"start": v(-552.71, 785.34) * mm, "end": v(-552.62, 785.44) * mm});
            skLineSegment(sketch, "E883", {"start": v(-552.62, 785.44) * mm, "end": v(-552.53, 785.53) * mm});
            skLineSegment(sketch, "E884", {"start": v(-552.53, 785.53) * mm, "end": v(-552.44, 785.62) * mm});
            skLineSegment(sketch, "E885", {"start": v(-552.44, 785.62) * mm, "end": v(-552.34, 785.71) * mm});
            skLineSegment(sketch, "E886", {"start": v(-552.34, 785.71) * mm, "end": v(-552.25, 785.8) * mm});
            skLineSegment(sketch, "E887", {"start": v(-552.25, 785.8) * mm, "end": v(-552.16, 785.9) * mm});
            skLineSegment(sketch, "E888", {"start": v(-552.16, 785.9) * mm, "end": v(-552.06, 785.98) * mm});
            skLineSegment(sketch, "E889", {"start": v(-552.06, 785.98) * mm, "end": v(-551.96, 786.06) * mm});
            skLineSegment(sketch, "E890", {"start": v(-551.96, 786.06) * mm, "end": v(-551.87, 786.15) * mm});
            skLineSegment(sketch, "E891", {"start": v(-551.87, 786.15) * mm, "end": v(-551.77, 786.23) * mm});
            skLineSegment(sketch, "E892", {"start": v(-551.77, 786.23) * mm, "end": v(-551.68, 786.31) * mm});
            skLineSegment(sketch, "E893", {"start": v(-551.68, 786.31) * mm, "end": v(-551.58, 786.39) * mm});
            skLineSegment(sketch, "E894", {"start": v(-551.58, 786.39) * mm, "end": v(-551.48, 786.47) * mm});
            skLineSegment(sketch, "E895", {"start": v(-551.48, 786.47) * mm, "end": v(-551.38, 786.54) * mm});
            skLineSegment(sketch, "E896", {"start": v(-551.38, 786.54) * mm, "end": v(-551.28, 786.62) * mm});
            skLineSegment(sketch, "E897", {"start": v(-551.28, 786.62) * mm, "end": v(-551.18, 786.69) * mm});
            skLineSegment(sketch, "E898", {"start": v(-551.18, 786.69) * mm, "end": v(-551.08, 786.76) * mm});
            skLineSegment(sketch, "E899", {"start": v(-551.08, 786.76) * mm, "end": v(-550.98, 786.83) * mm});
            skLineSegment(sketch, "E900", {"start": v(-550.98, 786.83) * mm, "end": v(-550.88, 786.9) * mm});
            skLineSegment(sketch, "E901", {"start": v(-550.88, 786.9) * mm, "end": v(-550.78, 786.96) * mm});
            skLineSegment(sketch, "E902", {"start": v(-550.78, 786.96) * mm, "end": v(-550.67, 787.02) * mm});
            skLineSegment(sketch, "E903", {"start": v(-550.67, 787.02) * mm, "end": v(-550.57, 787.08) * mm});
            skLineSegment(sketch, "E904", {"start": v(-550.57, 787.08) * mm, "end": v(-550.47, 787.14) * mm});
            skLineSegment(sketch, "E905", {"start": v(-550.47, 787.14) * mm, "end": v(-550.36, 787.2) * mm});
            skLineSegment(sketch, "E906", {"start": v(-550.36, 787.2) * mm, "end": v(-550.25, 787.26) * mm});
            skLineSegment(sketch, "E907", {"start": v(-550.25, 787.26) * mm, "end": v(-550.15, 787.31) * mm});
            skLineSegment(sketch, "E908", {"start": v(-550.15, 787.31) * mm, "end": v(-550.05, 787.38) * mm});
            skLineSegment(sketch, "E909", {"start": v(-550.05, 787.38) * mm, "end": v(-549.44, 787.57) * mm});
            skLineSegment(sketch, "E910", {"start": v(-549.44, 787.57) * mm, "end": v(-549.9, 789.3) * mm});
            skLineSegment(sketch, "E911", {"start": v(-549.9, 789.3) * mm, "end": v(-550.53, 789.16) * mm});
            skLineSegment(sketch, "E912", {"start": v(-550.53, 789.16) * mm, "end": v(-550.65, 789.18) * mm});
            skLineSegment(sketch, "E913", {"start": v(-550.65, 789.18) * mm, "end": v(-550.77, 789.17) * mm});
            skLineSegment(sketch, "E914", {"start": v(-550.77, 789.17) * mm, "end": v(-550.89, 789.17) * mm});
            skLineSegment(sketch, "E915", {"start": v(-550.89, 789.17) * mm, "end": v(-551, 789.16) * mm});
            skLineSegment(sketch, "E916", {"start": v(-551, 789.16) * mm, "end": v(-551.13, 789.16) * mm});
            skLineSegment(sketch, "E917", {"start": v(-551.13, 789.16) * mm, "end": v(-551.25, 789.17) * mm});
            skLineSegment(sketch, "E918", {"start": v(-551.25, 789.17) * mm, "end": v(-551.37, 789.17) * mm});
            skLineSegment(sketch, "E919", {"start": v(-551.37, 789.17) * mm, "end": v(-551.5, 789.17) * mm});
            skLineSegment(sketch, "E920", {"start": v(-551.5, 789.17) * mm, "end": v(-551.61, 789.18) * mm});
            skLineSegment(sketch, "E921", {"start": v(-551.61, 789.18) * mm, "end": v(-551.73, 789.19) * mm});
            skLineSegment(sketch, "E922", {"start": v(-551.73, 789.19) * mm, "end": v(-551.86, 789.2) * mm});
            skLineSegment(sketch, "E923", {"start": v(-551.86, 789.2) * mm, "end": v(-551.98, 789.21) * mm});
            skLineSegment(sketch, "E924", {"start": v(-551.98, 789.21) * mm, "end": v(-552.1, 789.23) * mm});
            skLineSegment(sketch, "E925", {"start": v(-552.1, 789.23) * mm, "end": v(-552.22, 789.24) * mm});
            skLineSegment(sketch, "E926", {"start": v(-552.22, 789.24) * mm, "end": v(-552.35, 789.26) * mm});
            skLineSegment(sketch, "E927", {"start": v(-552.35, 789.26) * mm, "end": v(-552.47, 789.28) * mm});
            skLineSegment(sketch, "E928", {"start": v(-552.47, 789.28) * mm, "end": v(-552.6, 789.3) * mm});
            skLineSegment(sketch, "E929", {"start": v(-552.6, 789.3) * mm, "end": v(-552.72, 789.32) * mm});
            skLineSegment(sketch, "E930", {"start": v(-552.72, 789.32) * mm, "end": v(-552.85, 789.35) * mm});
            skLineSegment(sketch, "E931", {"start": v(-552.85, 789.35) * mm, "end": v(-552.97, 789.38) * mm});
            skLineSegment(sketch, "E932", {"start": v(-552.97, 789.38) * mm, "end": v(-553.1, 789.4) * mm});
            skLineSegment(sketch, "E933", {"start": v(-553.1, 789.4) * mm, "end": v(-553.22, 789.43) * mm});
            skLineSegment(sketch, "E934", {"start": v(-553.22, 789.43) * mm, "end": v(-553.35, 789.46) * mm});
            skLineSegment(sketch, "E935", {"start": v(-553.35, 789.46) * mm, "end": v(-553.47, 789.5) * mm});
            skLineSegment(sketch, "E936", {"start": v(-553.47, 789.5) * mm, "end": v(-553.6, 789.53) * mm});
            skLineSegment(sketch, "E937", {"start": v(-553.6, 789.53) * mm, "end": v(-553.73, 789.56) * mm});
            skLineSegment(sketch, "E938", {"start": v(-553.73, 789.56) * mm, "end": v(-553.85, 789.6) * mm});
            skLineSegment(sketch, "E939", {"start": v(-553.85, 789.6) * mm, "end": v(-553.98, 789.64) * mm});
            skLineSegment(sketch, "E940", {"start": v(-553.98, 789.64) * mm, "end": v(-554.1, 789.68) * mm});
            skLineSegment(sketch, "E941", {"start": v(-554.1, 789.68) * mm, "end": v(-554.23, 789.72) * mm});
            skLineSegment(sketch, "E942", {"start": v(-554.23, 789.72) * mm, "end": v(-554.34, 790.39) * mm});
            skLineSegment(sketch, "E943", {"start": v(-554.34, 790.39) * mm, "end": v(-554.44, 791.05) * mm});
            skLineSegment(sketch, "E944", {"start": v(-554.44, 791.05) * mm, "end": v(-554.33, 791.13) * mm});
            skLineSegment(sketch, "E945", {"start": v(-554.33, 791.13) * mm, "end": v(-554.23, 791.2) * mm});
            skLineSegment(sketch, "E946", {"start": v(-554.23, 791.2) * mm, "end": v(-554.12, 791.28) * mm});
            skLineSegment(sketch, "E947", {"start": v(-554.12, 791.28) * mm, "end": v(-554, 791.36) * mm});
            skLineSegment(sketch, "E948", {"start": v(-554, 791.36) * mm, "end": v(-553.9, 791.43) * mm});
            skLineSegment(sketch, "E949", {"start": v(-553.9, 791.43) * mm, "end": v(-553.8, 791.5) * mm});
            skLineSegment(sketch, "E950", {"start": v(-553.8, 791.5) * mm, "end": v(-553.68, 791.57) * mm});
            skLineSegment(sketch, "E951", {"start": v(-553.68, 791.57) * mm, "end": v(-553.57, 791.64) * mm});
            skLineSegment(sketch, "E952", {"start": v(-553.57, 791.64) * mm, "end": v(-553.46, 791.7) * mm});
            skLineSegment(sketch, "E953", {"start": v(-553.46, 791.7) * mm, "end": v(-553.35, 791.77) * mm});
            skLineSegment(sketch, "E954", {"start": v(-553.35, 791.77) * mm, "end": v(-553.24, 791.83) * mm});
            skLineSegment(sketch, "E955", {"start": v(-553.24, 791.83) * mm, "end": v(-553.13, 791.9) * mm});
            skLineSegment(sketch, "E956", {"start": v(-553.13, 791.9) * mm, "end": v(-553.02, 791.96) * mm});
            skLineSegment(sketch, "E957", {"start": v(-553.02, 791.96) * mm, "end": v(-552.9, 792.01) * mm});
            skLineSegment(sketch, "E958", {"start": v(-552.9, 792.01) * mm, "end": v(-552.8, 792.07) * mm});
            skLineSegment(sketch, "E959", {"start": v(-552.8, 792.07) * mm, "end": v(-552.68, 792.13) * mm});
            skLineSegment(sketch, "E960", {"start": v(-552.68, 792.13) * mm, "end": v(-552.57, 792.18) * mm});
            skLineSegment(sketch, "E961", {"start": v(-552.57, 792.18) * mm, "end": v(-552.46, 792.23) * mm});
            skLineSegment(sketch, "E962", {"start": v(-552.46, 792.23) * mm, "end": v(-552.34, 792.28) * mm});
            skLineSegment(sketch, "E963", {"start": v(-552.34, 792.28) * mm, "end": v(-552.23, 792.33) * mm});
            skLineSegment(sketch, "E964", {"start": v(-552.23, 792.33) * mm, "end": v(-552.12, 792.38) * mm});
            skLineSegment(sketch, "E965", {"start": v(-552.12, 792.38) * mm, "end": v(-552, 792.42) * mm});
            skLineSegment(sketch, "E966", {"start": v(-552, 792.42) * mm, "end": v(-551.9, 792.46) * mm});
            skLineSegment(sketch, "E967", {"start": v(-551.9, 792.46) * mm, "end": v(-551.78, 792.5) * mm});
            skLineSegment(sketch, "E968", {"start": v(-551.78, 792.5) * mm, "end": v(-551.66, 792.54) * mm});
            skLineSegment(sketch, "E969", {"start": v(-551.66, 792.54) * mm, "end": v(-551.55, 792.58) * mm});
            skLineSegment(sketch, "E970", {"start": v(-551.55, 792.58) * mm, "end": v(-551.43, 792.61) * mm});
            skLineSegment(sketch, "E971", {"start": v(-551.43, 792.61) * mm, "end": v(-551.32, 792.64) * mm});
            skLineSegment(sketch, "E972", {"start": v(-551.32, 792.64) * mm, "end": v(-551.2, 792.68) * mm});
            skLineSegment(sketch, "E973", {"start": v(-551.2, 792.68) * mm, "end": v(-551.1, 792.73) * mm});
            skLineSegment(sketch, "E974", {"start": v(-551.1, 792.73) * mm, "end": v(-550.45, 792.78) * mm});
            skLineSegment(sketch, "E975", {"start": v(-550.45, 792.78) * mm, "end": v(-550.55, 794.58) * mm});
            skLineSegment(sketch, "E976", {"start": v(-550.55, 794.58) * mm, "end": v(-551.19, 794.57) * mm});
            skLineSegment(sketch, "E977", {"start": v(-551.19, 794.57) * mm, "end": v(-551.3, 794.6) * mm});
            skLineSegment(sketch, "E978", {"start": v(-551.3, 794.6) * mm, "end": v(-551.42, 794.62) * mm});
            skLineSegment(sketch, "E979", {"start": v(-551.42, 794.62) * mm, "end": v(-551.54, 794.65) * mm});
            skLineSegment(sketch, "E980", {"start": v(-551.54, 794.65) * mm, "end": v(-551.66, 794.67) * mm});
            skLineSegment(sketch, "E981", {"start": v(-551.66, 794.67) * mm, "end": v(-551.78, 794.7) * mm});
            skLineSegment(sketch, "E982", {"start": v(-551.78, 794.7) * mm, "end": v(-551.9, 794.72) * mm});
            skLineSegment(sketch, "E983", {"start": v(-551.9, 794.72) * mm, "end": v(-552, 794.75) * mm});
            skLineSegment(sketch, "E984", {"start": v(-552, 794.75) * mm, "end": v(-552.13, 794.78) * mm});
            skLineSegment(sketch, "E985", {"start": v(-552.13, 794.78) * mm, "end": v(-552.24, 794.8) * mm});
            skLineSegment(sketch, "E986", {"start": v(-552.24, 794.8) * mm, "end": v(-552.36, 794.84) * mm});
            skLineSegment(sketch, "E987", {"start": v(-552.36, 794.84) * mm, "end": v(-552.48, 794.88) * mm});
            skLineSegment(sketch, "E988", {"start": v(-552.48, 794.88) * mm, "end": v(-552.6, 794.92) * mm});
            skLineSegment(sketch, "E989", {"start": v(-552.6, 794.92) * mm, "end": v(-552.72, 794.96) * mm});
            skLineSegment(sketch, "E990", {"start": v(-552.72, 794.96) * mm, "end": v(-552.83, 795) * mm});
            skLineSegment(sketch, "E991", {"start": v(-552.83, 795) * mm, "end": v(-552.95, 795.04) * mm});
            skLineSegment(sketch, "E992", {"start": v(-552.95, 795.04) * mm, "end": v(-553.07, 795.08) * mm});
            skLineSegment(sketch, "E993", {"start": v(-553.07, 795.08) * mm, "end": v(-553.18, 795.13) * mm});
            skLineSegment(sketch, "E994", {"start": v(-553.18, 795.13) * mm, "end": v(-553.3, 795.18) * mm});
            skLineSegment(sketch, "E995", {"start": v(-553.3, 795.18) * mm, "end": v(-553.42, 795.23) * mm});
            skLineSegment(sketch, "E996", {"start": v(-553.42, 795.23) * mm, "end": v(-553.53, 795.28) * mm});
            skLineSegment(sketch, "E997", {"start": v(-553.53, 795.28) * mm, "end": v(-553.65, 795.34) * mm});
            skLineSegment(sketch, "E998", {"start": v(-553.65, 795.34) * mm, "end": v(-553.77, 795.39) * mm});
            skLineSegment(sketch, "E999", {"start": v(-553.77, 795.39) * mm, "end": v(-553.88, 795.44) * mm});
            skLineSegment(sketch, "E1000", {"start": v(-553.88, 795.44) * mm, "end": v(-554, 795.5) * mm});
            skLineSegment(sketch, "E1001", {"start": v(-554, 795.5) * mm, "end": v(-554.23, 795.62) * mm});
            skLineSegment(sketch, "E1002", {"start": v(-554.23, 795.62) * mm, "end": v(-554.35, 795.68) * mm});
            skLineSegment(sketch, "E1003", {"start": v(-554.35, 795.68) * mm, "end": v(-554.46, 795.75) * mm});
            skLineSegment(sketch, "E1004", {"start": v(-554.46, 795.75) * mm, "end": v(-554.58, 795.81) * mm});
            skLineSegment(sketch, "E1005", {"start": v(-554.58, 795.81) * mm, "end": v(-554.7, 795.88) * mm});
            skLineSegment(sketch, "E1006", {"start": v(-554.7, 795.88) * mm, "end": v(-554.67, 796.55) * mm});
            skLineSegment(sketch, "E1007", {"start": v(-554.67, 796.55) * mm, "end": v(-554.63, 797.23) * mm});
            skLineSegment(sketch, "E1008", {"start": v(-554.63, 797.23) * mm, "end": v(-554.5, 797.28) * mm});
            skLineSegment(sketch, "E1009", {"start": v(-554.5, 797.28) * mm, "end": v(-554.38, 797.33) * mm});
            skLineSegment(sketch, "E1010", {"start": v(-554.38, 797.33) * mm, "end": v(-554.26, 797.39) * mm});
            skLineSegment(sketch, "E1011", {"start": v(-554.26, 797.39) * mm, "end": v(-554.14, 797.44) * mm});
            skLineSegment(sketch, "E1012", {"start": v(-554.14, 797.44) * mm, "end": v(-554.02, 797.49) * mm});
            skLineSegment(sketch, "E1013", {"start": v(-554.02, 797.49) * mm, "end": v(-553.9, 797.53) * mm});
            skLineSegment(sketch, "E1014", {"start": v(-553.9, 797.53) * mm, "end": v(-553.77, 797.58) * mm});
            skLineSegment(sketch, "E1015", {"start": v(-553.77, 797.58) * mm, "end": v(-553.65, 797.62) * mm});
            skLineSegment(sketch, "E1016", {"start": v(-553.65, 797.62) * mm, "end": v(-553.53, 797.66) * mm});
            skLineSegment(sketch, "E1017", {"start": v(-553.53, 797.66) * mm, "end": v(-553.4, 797.7) * mm});
            skLineSegment(sketch, "E1018", {"start": v(-553.4, 797.7) * mm, "end": v(-553.29, 797.74) * mm});
            skLineSegment(sketch, "E1019", {"start": v(-553.29, 797.74) * mm, "end": v(-553.17, 797.78) * mm});
            skLineSegment(sketch, "E1020", {"start": v(-553.17, 797.78) * mm, "end": v(-553.04, 797.81) * mm});
            skLineSegment(sketch, "E1021", {"start": v(-553.04, 797.81) * mm, "end": v(-552.92, 797.85) * mm});
            skLineSegment(sketch, "E1022", {"start": v(-552.92, 797.85) * mm, "end": v(-552.8, 797.88) * mm});
            skLineSegment(sketch, "E1023", {"start": v(-552.8, 797.88) * mm, "end": v(-552.68, 797.91) * mm});
            skLineSegment(sketch, "E1024", {"start": v(-552.68, 797.91) * mm, "end": v(-552.56, 797.94) * mm});
            skLineSegment(sketch, "E1025", {"start": v(-552.56, 797.94) * mm, "end": v(-552.44, 797.97) * mm});
            skLineSegment(sketch, "E1026", {"start": v(-552.44, 797.97) * mm, "end": v(-552.32, 798) * mm});
            skLineSegment(sketch, "E1027", {"start": v(-552.32, 798) * mm, "end": v(-552.2, 798.02) * mm});
            skLineSegment(sketch, "E1028", {"start": v(-552.2, 798.02) * mm, "end": v(-552.08, 798.04) * mm});
            skLineSegment(sketch, "E1029", {"start": v(-552.08, 798.04) * mm, "end": v(-551.96, 798.06) * mm});
            skLineSegment(sketch, "E1030", {"start": v(-551.96, 798.06) * mm, "end": v(-551.84, 798.08) * mm});
            skLineSegment(sketch, "E1031", {"start": v(-551.84, 798.08) * mm, "end": v(-551.71, 798.1) * mm});
            skLineSegment(sketch, "E1032", {"start": v(-551.71, 798.1) * mm, "end": v(-551.6, 798.1) * mm});
            skLineSegment(sketch, "E1033", {"start": v(-551.6, 798.1) * mm, "end": v(-551.48, 798.12) * mm});
            skLineSegment(sketch, "E1034", {"start": v(-551.48, 798.12) * mm, "end": v(-551.36, 798.13) * mm});
            skLineSegment(sketch, "E1035", {"start": v(-551.36, 798.13) * mm, "end": v(-551.24, 798.14) * mm});
            skLineSegment(sketch, "E1036", {"start": v(-551.24, 798.14) * mm, "end": v(-551.12, 798.14) * mm});
            skLineSegment(sketch, "E1037", {"start": v(-551.12, 798.14) * mm, "end": v(-551, 798.17) * mm});
            skLineSegment(sketch, "E1038", {"start": v(-551, 798.17) * mm, "end": v(-550.36, 798.1) * mm});
            skLineSegment(sketch, "E1039", {"start": v(-550.36, 798.1) * mm, "end": v(-550.08, 799.87) * mm});
            skLineSegment(sketch, "E1040", {"start": v(-550.08, 799.87) * mm, "end": v(-550.71, 799.99) * mm});
            skLineSegment(sketch, "E1041", {"start": v(-550.71, 799.99) * mm, "end": v(-550.82, 800.05) * mm});
            skLineSegment(sketch, "E1042", {"start": v(-550.82, 800.05) * mm, "end": v(-550.93, 800.1) * mm});
            skLineSegment(sketch, "E1043", {"start": v(-550.93, 800.1) * mm, "end": v(-551.04, 800.14) * mm});
            skLineSegment(sketch, "E1044", {"start": v(-551.04, 800.14) * mm, "end": v(-551.15, 800.18) * mm});
            skLineSegment(sketch, "E1045", {"start": v(-551.15, 800.18) * mm, "end": v(-551.26, 800.23) * mm});
            skLineSegment(sketch, "E1046", {"start": v(-551.26, 800.23) * mm, "end": v(-551.37, 800.28) * mm});
            skLineSegment(sketch, "E1047", {"start": v(-551.37, 800.28) * mm, "end": v(-551.48, 800.33) * mm});
            skLineSegment(sketch, "E1048", {"start": v(-551.48, 800.33) * mm, "end": v(-551.59, 800.39) * mm});
            skLineSegment(sketch, "E1049", {"start": v(-551.59, 800.39) * mm, "end": v(-551.7, 800.44) * mm});
            skLineSegment(sketch, "E1050", {"start": v(-551.7, 800.44) * mm, "end": v(-551.8, 800.5) * mm});
            skLineSegment(sketch, "E1051", {"start": v(-551.8, 800.5) * mm, "end": v(-551.91, 800.56) * mm});
            skLineSegment(sketch, "E1052", {"start": v(-551.91, 800.56) * mm, "end": v(-552.02, 800.62) * mm});
            skLineSegment(sketch, "E1053", {"start": v(-552.02, 800.62) * mm, "end": v(-552.12, 800.69) * mm});
            skLineSegment(sketch, "E1054", {"start": v(-552.12, 800.69) * mm, "end": v(-552.23, 800.75) * mm});
            skLineSegment(sketch, "E1055", {"start": v(-552.23, 800.75) * mm, "end": v(-552.33, 800.82) * mm});
            skLineSegment(sketch, "E1056", {"start": v(-552.33, 800.82) * mm, "end": v(-552.44, 800.89) * mm});
            skLineSegment(sketch, "E1057", {"start": v(-552.44, 800.89) * mm, "end": v(-552.55, 800.96) * mm});
            skLineSegment(sketch, "E1058", {"start": v(-552.55, 800.96) * mm, "end": v(-552.65, 801.03) * mm});
            skLineSegment(sketch, "E1059", {"start": v(-552.65, 801.03) * mm, "end": v(-552.75, 801.1) * mm});
            skLineSegment(sketch, "E1060", {"start": v(-552.75, 801.1) * mm, "end": v(-552.86, 801.18) * mm});
            skLineSegment(sketch, "E1061", {"start": v(-552.86, 801.18) * mm, "end": v(-552.96, 801.25) * mm});
            skLineSegment(sketch, "E1062", {"start": v(-552.96, 801.25) * mm, "end": v(-553.06, 801.33) * mm});
            skLineSegment(sketch, "E1063", {"start": v(-553.06, 801.33) * mm, "end": v(-553.17, 801.4) * mm});
            skLineSegment(sketch, "E1064", {"start": v(-553.17, 801.4) * mm, "end": v(-553.27, 801.49) * mm});
            skLineSegment(sketch, "E1065", {"start": v(-553.27, 801.49) * mm, "end": v(-553.37, 801.57) * mm});
            skLineSegment(sketch, "E1066", {"start": v(-553.37, 801.57) * mm, "end": v(-553.47, 801.65) * mm});
            skLineSegment(sketch, "E1067", {"start": v(-553.47, 801.65) * mm, "end": v(-553.57, 801.74) * mm});
            skLineSegment(sketch, "E1068", {"start": v(-553.57, 801.74) * mm, "end": v(-553.67, 801.83) * mm});
            skLineSegment(sketch, "E1069", {"start": v(-553.67, 801.83) * mm, "end": v(-553.77, 801.91) * mm});
            skLineSegment(sketch, "E1070", {"start": v(-553.77, 801.91) * mm, "end": v(-553.87, 802) * mm});
            skLineSegment(sketch, "E1071", {"start": v(-553.87, 802) * mm, "end": v(-553.7, 802.66) * mm});
            skLineSegment(sketch, "E1072", {"start": v(-553.7, 802.66) * mm, "end": v(-553.52, 803.3) * mm});
            skLineSegment(sketch, "E1073", {"start": v(-553.52, 803.3) * mm, "end": v(-553.39, 803.33) * mm});
            skLineSegment(sketch, "E1074", {"start": v(-553.39, 803.33) * mm, "end": v(-553.26, 803.36) * mm});
            skLineSegment(sketch, "E1075", {"start": v(-553.26, 803.36) * mm, "end": v(-553.13, 803.38) * mm});
            skLineSegment(sketch, "E1076", {"start": v(-553.13, 803.38) * mm, "end": v(-553, 803.4) * mm});
            skLineSegment(sketch, "E1077", {"start": v(-553, 803.4) * mm, "end": v(-552.87, 803.43) * mm});
            skLineSegment(sketch, "E1078", {"start": v(-552.87, 803.43) * mm, "end": v(-552.74, 803.45) * mm});
            skLineSegment(sketch, "E1079", {"start": v(-552.74, 803.45) * mm, "end": v(-552.61, 803.47) * mm});
            skLineSegment(sketch, "E1080", {"start": v(-552.61, 803.47) * mm, "end": v(-552.48, 803.49) * mm});
            skLineSegment(sketch, "E1081", {"start": v(-552.48, 803.49) * mm, "end": v(-552.36, 803.5) * mm});
            skLineSegment(sketch, "E1082", {"start": v(-552.36, 803.5) * mm, "end": v(-552.23, 803.52) * mm});
            skLineSegment(sketch, "E1083", {"start": v(-552.23, 803.52) * mm, "end": v(-552.1, 803.53) * mm});
            skLineSegment(sketch, "E1084", {"start": v(-552.1, 803.53) * mm, "end": v(-551.98, 803.54) * mm});
            skLineSegment(sketch, "E1085", {"start": v(-551.98, 803.54) * mm, "end": v(-551.85, 803.55) * mm});
            skLineSegment(sketch, "E1086", {"start": v(-551.85, 803.55) * mm, "end": v(-551.72, 803.56) * mm});
            skLineSegment(sketch, "E1087", {"start": v(-551.72, 803.56) * mm, "end": v(-551.6, 803.57) * mm});
            skLineSegment(sketch, "E1088", {"start": v(-551.6, 803.57) * mm, "end": v(-551.47, 803.57) * mm});
            skLineSegment(sketch, "E1089", {"start": v(-551.47, 803.57) * mm, "end": v(-551.35, 803.57) * mm});
            skLineSegment(sketch, "E1090", {"start": v(-551.35, 803.57) * mm, "end": v(-551.23, 803.57) * mm});
            skLineSegment(sketch, "E1091", {"start": v(-551.23, 803.57) * mm, "end": v(-551.1, 803.57) * mm});
            skLineSegment(sketch, "E1092", {"start": v(-551.1, 803.57) * mm, "end": v(-550.98, 803.57) * mm});
            skLineSegment(sketch, "E1093", {"start": v(-550.98, 803.57) * mm, "end": v(-550.86, 803.57) * mm});
            skLineSegment(sketch, "E1094", {"start": v(-550.86, 803.57) * mm, "end": v(-550.74, 803.56) * mm});
            skLineSegment(sketch, "E1095", {"start": v(-550.74, 803.56) * mm, "end": v(-550.61, 803.56) * mm});
            skLineSegment(sketch, "E1096", {"start": v(-550.61, 803.56) * mm, "end": v(-550.5, 803.55) * mm});
            skLineSegment(sketch, "E1097", {"start": v(-550.5, 803.55) * mm, "end": v(-550.37, 803.53) * mm});
            skLineSegment(sketch, "E1098", {"start": v(-550.37, 803.53) * mm, "end": v(-550.25, 803.52) * mm});
            skLineSegment(sketch, "E1099", {"start": v(-550.25, 803.52) * mm, "end": v(-550.14, 803.5) * mm});
            skLineSegment(sketch, "E1100", {"start": v(-550.14, 803.5) * mm, "end": v(-550.02, 803.49) * mm});
            skLineSegment(sketch, "E1101", {"start": v(-550.02, 803.49) * mm, "end": v(-549.9, 803.47) * mm});
            skLineSegment(sketch, "E1102", {"start": v(-549.9, 803.47) * mm, "end": v(-549.78, 803.47) * mm});
            skLineSegment(sketch, "E1103", {"start": v(-549.78, 803.47) * mm, "end": v(-549.17, 803.26) * mm});
            skLineSegment(sketch, "E1104", {"start": v(-549.17, 803.26) * mm, "end": v(-548.53, 804.94) * mm});
            skLineSegment(sketch, "E1105", {"start": v(-548.53, 804.94) * mm, "end": v(-549.12, 805.2) * mm});
            skLineSegment(sketch, "E1106", {"start": v(-549.12, 805.2) * mm, "end": v(-549.2, 805.27) * mm});
            skLineSegment(sketch, "E1107", {"start": v(-549.2, 805.27) * mm, "end": v(-549.3, 805.34) * mm});
            skLineSegment(sketch, "E1108", {"start": v(-549.3, 805.34) * mm, "end": v(-549.4, 805.4) * mm});
            skLineSegment(sketch, "E1109", {"start": v(-549.4, 805.4) * mm, "end": v(-549.5, 805.48) * mm});
            skLineSegment(sketch, "E1110", {"start": v(-549.5, 805.48) * mm, "end": v(-549.6, 805.55) * mm});
            skLineSegment(sketch, "E1111", {"start": v(-549.6, 805.55) * mm, "end": v(-549.7, 805.62) * mm});
            skLineSegment(sketch, "E1112", {"start": v(-549.7, 805.62) * mm, "end": v(-549.8, 805.7) * mm});
            skLineSegment(sketch, "E1113", {"start": v(-549.8, 805.7) * mm, "end": v(-549.9, 805.77) * mm});
            skLineSegment(sketch, "E1114", {"start": v(-549.9, 805.77) * mm, "end": v(-549.99, 805.84) * mm});
            skLineSegment(sketch, "E1115", {"start": v(-549.99, 805.84) * mm, "end": v(-550.08, 805.92) * mm});
            skLineSegment(sketch, "E1116", {"start": v(-550.08, 805.92) * mm, "end": v(-550.17, 806) * mm});
            skLineSegment(sketch, "E1117", {"start": v(-550.17, 806) * mm, "end": v(-550.26, 806.09) * mm});
            skLineSegment(sketch, "E1118", {"start": v(-550.26, 806.09) * mm, "end": v(-550.35, 806.17) * mm});
            skLineSegment(sketch, "E1119", {"start": v(-550.35, 806.17) * mm, "end": v(-550.44, 806.26) * mm});
            skLineSegment(sketch, "E1120", {"start": v(-550.44, 806.26) * mm, "end": v(-550.53, 806.34) * mm});
            skLineSegment(sketch, "E1121", {"start": v(-550.53, 806.34) * mm, "end": v(-550.62, 806.43) * mm});
            skLineSegment(sketch, "E1122", {"start": v(-550.62, 806.43) * mm, "end": v(-550.71, 806.52) * mm});
            skLineSegment(sketch, "E1123", {"start": v(-550.71, 806.52) * mm, "end": v(-550.8, 806.61) * mm});
            skLineSegment(sketch, "E1124", {"start": v(-550.8, 806.61) * mm, "end": v(-550.88, 806.7) * mm});
            skLineSegment(sketch, "E1125", {"start": v(-550.88, 806.7) * mm, "end": v(-550.97, 806.8) * mm});
            skLineSegment(sketch, "E1126", {"start": v(-550.97, 806.8) * mm, "end": v(-551.05, 806.9) * mm});
            skLineSegment(sketch, "E1127", {"start": v(-551.05, 806.9) * mm, "end": v(-551.14, 807) * mm});
            skLineSegment(sketch, "E1128", {"start": v(-551.14, 807) * mm, "end": v(-551.22, 807.1) * mm});
            skLineSegment(sketch, "E1129", {"start": v(-551.22, 807.1) * mm, "end": v(-551.3, 807.2) * mm});
            skLineSegment(sketch, "E1130", {"start": v(-551.3, 807.2) * mm, "end": v(-551.39, 807.3) * mm});
            skLineSegment(sketch, "E1131", {"start": v(-551.39, 807.3) * mm, "end": v(-551.47, 807.4) * mm});
            skLineSegment(sketch, "E1132", {"start": v(-551.47, 807.4) * mm, "end": v(-551.55, 807.5) * mm});
            skLineSegment(sketch, "E1133", {"start": v(-551.55, 807.5) * mm, "end": v(-551.63, 807.6) * mm});
            skLineSegment(sketch, "E1134", {"start": v(-551.63, 807.6) * mm, "end": v(-551.7, 807.71) * mm});
            skLineSegment(sketch, "E1135", {"start": v(-551.7, 807.71) * mm, "end": v(-551.79, 807.82) * mm});
            skLineSegment(sketch, "E1136", {"start": v(-551.79, 807.82) * mm, "end": v(-551.49, 808.42) * mm});
            skLineSegment(sketch, "E1137", {"start": v(-551.49, 808.42) * mm, "end": v(-551.18, 809.02) * mm});
            skLineSegment(sketch, "E1138", {"start": v(-551.18, 809.02) * mm, "end": v(-551.04, 809.02) * mm});
            skLineSegment(sketch, "E1139", {"start": v(-551.04, 809.02) * mm, "end": v(-550.9, 809.02) * mm});
            skLineSegment(sketch, "E1140", {"start": v(-550.9, 809.02) * mm, "end": v(-550.78, 809.02) * mm});
            skLineSegment(sketch, "E1141", {"start": v(-550.78, 809.02) * mm, "end": v(-550.65, 809.01) * mm});
            skLineSegment(sketch, "E1142", {"start": v(-550.65, 809.01) * mm, "end": v(-550.51, 809) * mm});
            skLineSegment(sketch, "E1143", {"start": v(-550.51, 809) * mm, "end": v(-550.38, 809) * mm});
            skLineSegment(sketch, "E1144", {"start": v(-550.38, 809) * mm, "end": v(-550.25, 809) * mm});
            skLineSegment(sketch, "E1145", {"start": v(-550.25, 809) * mm, "end": v(-550.13, 808.98) * mm});
            skLineSegment(sketch, "E1146", {"start": v(-550.13, 808.98) * mm, "end": v(-550, 808.97) * mm});
            skLineSegment(sketch, "E1147", {"start": v(-550, 808.97) * mm, "end": v(-549.87, 808.96) * mm});
            skLineSegment(sketch, "E1148", {"start": v(-549.87, 808.96) * mm, "end": v(-549.74, 808.95) * mm});
            skLineSegment(sketch, "E1149", {"start": v(-549.74, 808.95) * mm, "end": v(-549.62, 808.93) * mm});
            skLineSegment(sketch, "E1150", {"start": v(-549.62, 808.93) * mm, "end": v(-549.5, 808.91) * mm});
            skLineSegment(sketch, "E1151", {"start": v(-549.5, 808.91) * mm, "end": v(-549.37, 808.9) * mm});
            skLineSegment(sketch, "E1152", {"start": v(-549.37, 808.9) * mm, "end": v(-549.24, 808.88) * mm});
            skLineSegment(sketch, "E1153", {"start": v(-549.24, 808.88) * mm, "end": v(-549.12, 808.85) * mm});
            skLineSegment(sketch, "E1154", {"start": v(-549.12, 808.85) * mm, "end": v(-549, 808.83) * mm});
            skLineSegment(sketch, "E1155", {"start": v(-549, 808.83) * mm, "end": v(-548.87, 808.8) * mm});
            skLineSegment(sketch, "E1156", {"start": v(-548.87, 808.8) * mm, "end": v(-548.76, 808.78) * mm});
            skLineSegment(sketch, "E1157", {"start": v(-548.76, 808.78) * mm, "end": v(-548.63, 808.75) * mm});
            skLineSegment(sketch, "E1158", {"start": v(-548.63, 808.75) * mm, "end": v(-548.52, 808.72) * mm});
            skLineSegment(sketch, "E1159", {"start": v(-548.52, 808.72) * mm, "end": v(-548.4, 808.7) * mm});
            skLineSegment(sketch, "E1160", {"start": v(-548.4, 808.7) * mm, "end": v(-548.28, 808.66) * mm});
            skLineSegment(sketch, "E1161", {"start": v(-548.28, 808.66) * mm, "end": v(-548.17, 808.63) * mm});
            skLineSegment(sketch, "E1162", {"start": v(-548.17, 808.63) * mm, "end": v(-548.05, 808.6) * mm});
            skLineSegment(sketch, "E1163", {"start": v(-548.05, 808.6) * mm, "end": v(-547.94, 808.55) * mm});
            skLineSegment(sketch, "E1164", {"start": v(-547.94, 808.55) * mm, "end": v(-547.82, 808.51) * mm});
            skLineSegment(sketch, "E1165", {"start": v(-547.82, 808.51) * mm, "end": v(-547.71, 808.47) * mm});
            skLineSegment(sketch, "E1166", {"start": v(-547.71, 808.47) * mm, "end": v(-547.6, 808.43) * mm});
            skLineSegment(sketch, "E1167", {"start": v(-547.6, 808.43) * mm, "end": v(-547.48, 808.4) * mm});
            skLineSegment(sketch, "E1168", {"start": v(-547.48, 808.4) * mm, "end": v(-546.93, 808.08) * mm});
            skLineSegment(sketch, "E1169", {"start": v(-546.93, 808.08) * mm, "end": v(-545.95, 809.58) * mm});
            skLineSegment(sketch, "E1170", {"start": v(-545.95, 809.58) * mm, "end": v(-546.47, 809.95) * mm});
            skLineSegment(sketch, "E1171", {"start": v(-546.47, 809.95) * mm, "end": v(-546.55, 810.05) * mm});
            skLineSegment(sketch, "E1172", {"start": v(-546.55, 810.05) * mm, "end": v(-546.63, 810.13) * mm});
            skLineSegment(sketch, "E1173", {"start": v(-546.63, 810.13) * mm, "end": v(-546.72, 810.22) * mm});
            skLineSegment(sketch, "E1174", {"start": v(-546.72, 810.22) * mm, "end": v(-546.8, 810.3) * mm});
            skLineSegment(sketch, "E1175", {"start": v(-546.8, 810.3) * mm, "end": v(-546.88, 810.4) * mm});
            skLineSegment(sketch, "E1176", {"start": v(-546.88, 810.4) * mm, "end": v(-546.96, 810.49) * mm});
            skLineSegment(sketch, "E1177", {"start": v(-546.96, 810.49) * mm, "end": v(-547.04, 810.58) * mm});
            skLineSegment(sketch, "E1178", {"start": v(-547.04, 810.58) * mm, "end": v(-547.11, 810.67) * mm});
            skLineSegment(sketch, "E1179", {"start": v(-547.11, 810.67) * mm, "end": v(-547.2, 810.77) * mm});
            skLineSegment(sketch, "E1180", {"start": v(-547.2, 810.77) * mm, "end": v(-547.26, 810.86) * mm});
            skLineSegment(sketch, "E1181", {"start": v(-547.26, 810.86) * mm, "end": v(-547.34, 810.96) * mm});
            skLineSegment(sketch, "E1182", {"start": v(-547.34, 810.96) * mm, "end": v(-547.41, 811.06) * mm});
            skLineSegment(sketch, "E1183", {"start": v(-547.41, 811.06) * mm, "end": v(-547.48, 811.16) * mm});
            skLineSegment(sketch, "E1184", {"start": v(-547.48, 811.16) * mm, "end": v(-547.55, 811.27) * mm});
            skLineSegment(sketch, "E1185", {"start": v(-547.55, 811.27) * mm, "end": v(-547.62, 811.37) * mm});
            skLineSegment(sketch, "E1186", {"start": v(-547.62, 811.37) * mm, "end": v(-547.7, 811.48) * mm});
            skLineSegment(sketch, "E1187", {"start": v(-547.7, 811.48) * mm, "end": v(-547.76, 811.58) * mm});
            skLineSegment(sketch, "E1188", {"start": v(-547.76, 811.58) * mm, "end": v(-547.83, 811.69) * mm});
            skLineSegment(sketch, "E1189", {"start": v(-547.83, 811.69) * mm, "end": v(-547.89, 811.8) * mm});
            skLineSegment(sketch, "E1190", {"start": v(-547.89, 811.8) * mm, "end": v(-547.95, 811.9) * mm});
            skLineSegment(sketch, "E1191", {"start": v(-547.95, 811.9) * mm, "end": v(-548.02, 812.02) * mm});
            skLineSegment(sketch, "E1192", {"start": v(-548.02, 812.02) * mm, "end": v(-548.08, 812.13) * mm});
            skLineSegment(sketch, "E1193", {"start": v(-548.08, 812.13) * mm, "end": v(-548.14, 812.25) * mm});
            skLineSegment(sketch, "E1194", {"start": v(-548.14, 812.25) * mm, "end": v(-548.2, 812.36) * mm});
            skLineSegment(sketch, "E1195", {"start": v(-548.2, 812.36) * mm, "end": v(-548.26, 812.48) * mm});
            skLineSegment(sketch, "E1196", {"start": v(-548.26, 812.48) * mm, "end": v(-548.32, 812.6) * mm});
            skLineSegment(sketch, "E1197", {"start": v(-548.32, 812.6) * mm, "end": v(-548.38, 812.71) * mm});
            skLineSegment(sketch, "E1198", {"start": v(-548.38, 812.71) * mm, "end": v(-548.43, 812.83) * mm});
            skLineSegment(sketch, "E1199", {"start": v(-548.43, 812.83) * mm, "end": v(-548.49, 812.95) * mm});
            skLineSegment(sketch, "E1200", {"start": v(-548.49, 812.95) * mm, "end": v(-548.54, 813.08) * mm});
            skLineSegment(sketch, "E1201", {"start": v(-548.54, 813.08) * mm, "end": v(-548.12, 813.6) * mm});
            skLineSegment(sketch, "E1202", {"start": v(-548.12, 813.6) * mm, "end": v(-547.7, 814.12) * mm});
            skLineSegment(sketch, "E1203", {"start": v(-547.7, 814.12) * mm, "end": v(-547.56, 814.1) * mm});
            skLineSegment(sketch, "E1204", {"start": v(-547.56, 814.1) * mm, "end": v(-547.43, 814.07) * mm});
            skLineSegment(sketch, "E1205", {"start": v(-547.43, 814.07) * mm, "end": v(-547.3, 814.04) * mm});
            skLineSegment(sketch, "E1206", {"start": v(-547.3, 814.04) * mm, "end": v(-547.18, 814) * mm});
            skLineSegment(sketch, "E1207", {"start": v(-547.18, 814) * mm, "end": v(-547.05, 813.97) * mm});
            skLineSegment(sketch, "E1208", {"start": v(-547.05, 813.97) * mm, "end": v(-546.92, 813.94) * mm});
            skLineSegment(sketch, "E1209", {"start": v(-546.92, 813.94) * mm, "end": v(-546.8, 813.9) * mm});
            skLineSegment(sketch, "E1210", {"start": v(-546.8, 813.9) * mm, "end": v(-546.67, 813.87) * mm});
            skLineSegment(sketch, "E1211", {"start": v(-546.67, 813.87) * mm, "end": v(-546.55, 813.83) * mm});
            skLineSegment(sketch, "E1212", {"start": v(-546.55, 813.83) * mm, "end": v(-546.43, 813.8) * mm});
            skLineSegment(sketch, "E1213", {"start": v(-546.43, 813.8) * mm, "end": v(-546.3, 813.75) * mm});
            skLineSegment(sketch, "E1214", {"start": v(-546.3, 813.75) * mm, "end": v(-546.19, 813.71) * mm});
            skLineSegment(sketch, "E1215", {"start": v(-546.19, 813.71) * mm, "end": v(-546.07, 813.67) * mm});
            skLineSegment(sketch, "E1216", {"start": v(-546.07, 813.67) * mm, "end": v(-545.95, 813.63) * mm});
            skLineSegment(sketch, "E1217", {"start": v(-545.95, 813.63) * mm, "end": v(-545.83, 813.58) * mm});
            skLineSegment(sketch, "E1218", {"start": v(-545.83, 813.58) * mm, "end": v(-545.72, 813.53) * mm});
            skLineSegment(sketch, "E1219", {"start": v(-545.72, 813.53) * mm, "end": v(-545.6, 813.48) * mm});
            skLineSegment(sketch, "E1220", {"start": v(-545.6, 813.48) * mm, "end": v(-545.49, 813.44) * mm});
            skLineSegment(sketch, "E1221", {"start": v(-545.49, 813.44) * mm, "end": v(-545.38, 813.39) * mm});
            skLineSegment(sketch, "E1222", {"start": v(-545.38, 813.39) * mm, "end": v(-545.26, 813.33) * mm});
            skLineSegment(sketch, "E1223", {"start": v(-545.26, 813.33) * mm, "end": v(-545.15, 813.28) * mm});
            skLineSegment(sketch, "E1224", {"start": v(-545.15, 813.28) * mm, "end": v(-545.05, 813.23) * mm});
            skLineSegment(sketch, "E1225", {"start": v(-545.05, 813.23) * mm, "end": v(-544.94, 813.17) * mm});
            skLineSegment(sketch, "E1226", {"start": v(-544.94, 813.17) * mm, "end": v(-544.83, 813.11) * mm});
            skLineSegment(sketch, "E1227", {"start": v(-544.83, 813.11) * mm, "end": v(-544.73, 813.05) * mm});
            skLineSegment(sketch, "E1228", {"start": v(-544.73, 813.05) * mm, "end": v(-544.62, 813) * mm});
            skLineSegment(sketch, "E1229", {"start": v(-544.62, 813) * mm, "end": v(-544.52, 812.93) * mm});
            skLineSegment(sketch, "E1230", {"start": v(-544.52, 812.93) * mm, "end": v(-544.42, 812.87) * mm});
            skLineSegment(sketch, "E1231", {"start": v(-544.42, 812.87) * mm, "end": v(-544.32, 812.8) * mm});
            skLineSegment(sketch, "E1232", {"start": v(-544.32, 812.8) * mm, "end": v(-544.2, 812.75) * mm});
            skLineSegment(sketch, "E1233", {"start": v(-544.2, 812.75) * mm, "end": v(-543.74, 812.32) * mm});
            skLineSegment(sketch, "E1234", {"start": v(-543.74, 812.32) * mm, "end": v(-542.47, 813.59) * mm});
            skLineSegment(sketch, "E1235", {"start": v(-542.47, 813.59) * mm, "end": v(-542.9, 814.06) * mm});
            skLineSegment(sketch, "E1236", {"start": v(-542.9, 814.06) * mm, "end": v(-542.95, 814.17) * mm});
            skLineSegment(sketch, "E1237", {"start": v(-542.95, 814.17) * mm, "end": v(-543.02, 814.27) * mm});
            skLineSegment(sketch, "E1238", {"start": v(-543.02, 814.27) * mm, "end": v(-543.08, 814.37) * mm});
            skLineSegment(sketch, "E1239", {"start": v(-543.08, 814.37) * mm, "end": v(-543.14, 814.47) * mm});
            skLineSegment(sketch, "E1240", {"start": v(-543.14, 814.47) * mm, "end": v(-543.2, 814.58) * mm});
            skLineSegment(sketch, "E1241", {"start": v(-543.2, 814.58) * mm, "end": v(-543.26, 814.68) * mm});
            skLineSegment(sketch, "E1242", {"start": v(-543.26, 814.68) * mm, "end": v(-543.32, 814.79) * mm});
            skLineSegment(sketch, "E1243", {"start": v(-543.32, 814.79) * mm, "end": v(-543.38, 814.9) * mm});
            skLineSegment(sketch, "E1244", {"start": v(-543.38, 814.9) * mm, "end": v(-543.43, 815) * mm});
            skLineSegment(sketch, "E1245", {"start": v(-543.43, 815) * mm, "end": v(-543.48, 815.11) * mm});
            skLineSegment(sketch, "E1246", {"start": v(-543.48, 815.11) * mm, "end": v(-543.54, 815.23) * mm});
            skLineSegment(sketch, "E1247", {"start": v(-543.54, 815.23) * mm, "end": v(-543.59, 815.34) * mm});
            skLineSegment(sketch, "E1248", {"start": v(-543.59, 815.34) * mm, "end": v(-543.64, 815.45) * mm});
            skLineSegment(sketch, "E1249", {"start": v(-543.64, 815.45) * mm, "end": v(-543.68, 815.57) * mm});
            skLineSegment(sketch, "E1250", {"start": v(-543.68, 815.57) * mm, "end": v(-543.73, 815.68) * mm});
            skLineSegment(sketch, "E1251", {"start": v(-543.73, 815.68) * mm, "end": v(-543.78, 815.8) * mm});
            skLineSegment(sketch, "E1252", {"start": v(-543.78, 815.8) * mm, "end": v(-543.82, 815.92) * mm});
            skLineSegment(sketch, "E1253", {"start": v(-543.82, 815.92) * mm, "end": v(-543.86, 816.04) * mm});
            skLineSegment(sketch, "E1254", {"start": v(-543.86, 816.04) * mm, "end": v(-543.9, 816.16) * mm});
            skLineSegment(sketch, "E1255", {"start": v(-543.9, 816.16) * mm, "end": v(-543.94, 816.28) * mm});
            skLineSegment(sketch, "E1256", {"start": v(-543.94, 816.28) * mm, "end": v(-543.98, 816.4) * mm});
            skLineSegment(sketch, "E1257", {"start": v(-543.98, 816.4) * mm, "end": v(-544.02, 816.52) * mm});
            skLineSegment(sketch, "E1258", {"start": v(-544.02, 816.52) * mm, "end": v(-544.06, 816.65) * mm});
            skLineSegment(sketch, "E1259", {"start": v(-544.06, 816.65) * mm, "end": v(-544.1, 816.77) * mm});
            skLineSegment(sketch, "E1260", {"start": v(-544.1, 816.77) * mm, "end": v(-544.12, 816.9) * mm});
            skLineSegment(sketch, "E1261", {"start": v(-544.12, 816.9) * mm, "end": v(-544.16, 817.03) * mm});
            skLineSegment(sketch, "E1262", {"start": v(-544.16, 817.03) * mm, "end": v(-544.19, 817.15) * mm});
            skLineSegment(sketch, "E1263", {"start": v(-544.19, 817.15) * mm, "end": v(-544.22, 817.28) * mm});
            skLineSegment(sketch, "E1264", {"start": v(-544.22, 817.28) * mm, "end": v(-544.25, 817.41) * mm});
            skLineSegment(sketch, "E1265", {"start": v(-544.25, 817.41) * mm, "end": v(-544.27, 817.54) * mm});
            skLineSegment(sketch, "E1266", {"start": v(-544.27, 817.54) * mm, "end": v(-543.75, 817.97) * mm});
            skLineSegment(sketch, "E1267", {"start": v(-543.75, 817.97) * mm, "end": v(-543.23, 818.4) * mm});
            skLineSegment(sketch, "E1268", {"start": v(-543.23, 818.4) * mm, "end": v(-543.1, 818.34) * mm});
            skLineSegment(sketch, "E1269", {"start": v(-543.1, 818.34) * mm, "end": v(-542.98, 818.28) * mm});
            skLineSegment(sketch, "E1270", {"start": v(-542.98, 818.28) * mm, "end": v(-542.86, 818.23) * mm});
            skLineSegment(sketch, "E1271", {"start": v(-542.86, 818.23) * mm, "end": v(-542.75, 818.17) * mm});
            skLineSegment(sketch, "E1272", {"start": v(-542.75, 818.17) * mm, "end": v(-542.63, 818.11) * mm});
            skLineSegment(sketch, "E1273", {"start": v(-542.63, 818.11) * mm, "end": v(-542.51, 818.05) * mm});
            skLineSegment(sketch, "E1274", {"start": v(-542.51, 818.05) * mm, "end": v(-542.4, 818) * mm});
            skLineSegment(sketch, "E1275", {"start": v(-542.4, 818) * mm, "end": v(-542.28, 817.93) * mm});
            skLineSegment(sketch, "E1276", {"start": v(-542.28, 817.93) * mm, "end": v(-542.17, 817.87) * mm});
            skLineSegment(sketch, "E1277", {"start": v(-542.17, 817.87) * mm, "end": v(-542.06, 817.8) * mm});
            skLineSegment(sketch, "E1278", {"start": v(-542.06, 817.8) * mm, "end": v(-541.95, 817.74) * mm});
            skLineSegment(sketch, "E1279", {"start": v(-541.95, 817.74) * mm, "end": v(-541.84, 817.68) * mm});
            skLineSegment(sketch, "E1280", {"start": v(-541.84, 817.68) * mm, "end": v(-541.73, 817.6) * mm});
            skLineSegment(sketch, "E1281", {"start": v(-541.73, 817.6) * mm, "end": v(-541.63, 817.54) * mm});
            skLineSegment(sketch, "E1282", {"start": v(-541.63, 817.54) * mm, "end": v(-541.52, 817.47) * mm});
            skLineSegment(sketch, "E1283", {"start": v(-541.52, 817.47) * mm, "end": v(-541.42, 817.4) * mm});
            skLineSegment(sketch, "E1284", {"start": v(-541.42, 817.4) * mm, "end": v(-541.31, 817.33) * mm});
            skLineSegment(sketch, "E1285", {"start": v(-541.31, 817.33) * mm, "end": v(-541.21, 817.26) * mm});
            skLineSegment(sketch, "E1286", {"start": v(-541.21, 817.26) * mm, "end": v(-541.11, 817.19) * mm});
            skLineSegment(sketch, "E1287", {"start": v(-541.11, 817.19) * mm, "end": v(-541.02, 817.11) * mm});
            skLineSegment(sketch, "E1288", {"start": v(-541.02, 817.11) * mm, "end": v(-540.92, 817.04) * mm});
            skLineSegment(sketch, "E1289", {"start": v(-540.92, 817.04) * mm, "end": v(-540.82, 816.96) * mm});
            skLineSegment(sketch, "E1290", {"start": v(-540.82, 816.96) * mm, "end": v(-540.73, 816.89) * mm});
            skLineSegment(sketch, "E1291", {"start": v(-540.73, 816.89) * mm, "end": v(-540.64, 816.8) * mm});
            skLineSegment(sketch, "E1292", {"start": v(-540.64, 816.8) * mm, "end": v(-540.55, 816.73) * mm});
            skLineSegment(sketch, "E1293", {"start": v(-540.55, 816.73) * mm, "end": v(-540.46, 816.65) * mm});
            skLineSegment(sketch, "E1294", {"start": v(-540.46, 816.65) * mm, "end": v(-540.37, 816.57) * mm});
            skLineSegment(sketch, "E1295", {"start": v(-540.37, 816.57) * mm, "end": v(-540.28, 816.48) * mm});
            skLineSegment(sketch, "E1296", {"start": v(-540.28, 816.48) * mm, "end": v(-540.2, 816.4) * mm});
            skLineSegment(sketch, "E1297", {"start": v(-540.2, 816.4) * mm, "end": v(-540.1, 816.32) * mm});
            skLineSegment(sketch, "E1298", {"start": v(-540.1, 816.32) * mm, "end": v(-539.74, 815.8) * mm});
            skLineSegment(sketch, "E1299", {"start": v(-539.74, 815.8) * mm, "end": v(-538.23, 816.78) * mm});
            skLineSegment(sketch, "E1300", {"start": v(-538.23, 816.78) * mm, "end": v(-538.55, 817.33) * mm});
            skLineSegment(sketch, "E1301", {"start": v(-538.55, 817.33) * mm, "end": v(-538.58, 817.45) * mm});
            skLineSegment(sketch, "E1302", {"start": v(-538.58, 817.45) * mm, "end": v(-538.62, 817.56) * mm});
            skLineSegment(sketch, "E1303", {"start": v(-538.62, 817.56) * mm, "end": v(-538.66, 817.67) * mm});
            skLineSegment(sketch, "E1304", {"start": v(-538.66, 817.67) * mm, "end": v(-538.7, 817.79) * mm});
            skLineSegment(sketch, "E1305", {"start": v(-538.7, 817.79) * mm, "end": v(-538.74, 817.9) * mm});
            skLineSegment(sketch, "E1306", {"start": v(-538.74, 817.9) * mm, "end": v(-538.78, 818.02) * mm});
            skLineSegment(sketch, "E1307", {"start": v(-538.78, 818.02) * mm, "end": v(-538.81, 818.13) * mm});
            skLineSegment(sketch, "E1308", {"start": v(-538.81, 818.13) * mm, "end": v(-538.84, 818.25) * mm});
            skLineSegment(sketch, "E1309", {"start": v(-538.84, 818.25) * mm, "end": v(-538.87, 818.37) * mm});
            skLineSegment(sketch, "E1310", {"start": v(-538.87, 818.37) * mm, "end": v(-538.9, 818.48) * mm});
            skLineSegment(sketch, "E1311", {"start": v(-538.9, 818.48) * mm, "end": v(-538.93, 818.6) * mm});
            skLineSegment(sketch, "E1312", {"start": v(-538.93, 818.6) * mm, "end": v(-538.96, 818.72) * mm});
            skLineSegment(sketch, "E1313", {"start": v(-538.96, 818.72) * mm, "end": v(-538.98, 818.85) * mm});
            skLineSegment(sketch, "E1314", {"start": v(-538.98, 818.85) * mm, "end": v(-539, 818.97) * mm});
            skLineSegment(sketch, "E1315", {"start": v(-539, 818.97) * mm, "end": v(-539.03, 819.1) * mm});
            skLineSegment(sketch, "E1316", {"start": v(-539.03, 819.1) * mm, "end": v(-539.05, 819.22) * mm});
            skLineSegment(sketch, "E1317", {"start": v(-539.05, 819.22) * mm, "end": v(-539.06, 819.34) * mm});
            skLineSegment(sketch, "E1318", {"start": v(-539.06, 819.34) * mm, "end": v(-539.08, 819.47) * mm});
            skLineSegment(sketch, "E1319", {"start": v(-539.08, 819.47) * mm, "end": v(-539.1, 819.6) * mm});
            skLineSegment(sketch, "E1320", {"start": v(-539.1, 819.6) * mm, "end": v(-539.1, 819.72) * mm});
            skLineSegment(sketch, "E1321", {"start": v(-539.1, 819.72) * mm, "end": v(-539.12, 819.85) * mm});
            skLineSegment(sketch, "E1322", {"start": v(-539.12, 819.85) * mm, "end": v(-539.13, 819.97) * mm});
            skLineSegment(sketch, "E1323", {"start": v(-539.13, 819.97) * mm, "end": v(-539.14, 820.1) * mm});
            skLineSegment(sketch, "E1324", {"start": v(-539.14, 820.1) * mm, "end": v(-539.15, 820.23) * mm});
            skLineSegment(sketch, "E1325", {"start": v(-539.15, 820.23) * mm, "end": v(-539.16, 820.36) * mm});
            skLineSegment(sketch, "E1326", {"start": v(-539.16, 820.36) * mm, "end": v(-539.16, 820.5) * mm});
            skLineSegment(sketch, "E1327", {"start": v(-539.16, 820.5) * mm, "end": v(-539.17, 820.63) * mm});
            skLineSegment(sketch, "E1328", {"start": v(-539.17, 820.63) * mm, "end": v(-539.17, 820.76) * mm});
            skLineSegment(sketch, "E1329", {"start": v(-539.17, 820.76) * mm, "end": v(-539.17, 820.9) * mm});
            skLineSegment(sketch, "E1330", {"start": v(-539.17, 820.9) * mm, "end": v(-539.17, 821.02) * mm});
            skLineSegment(sketch, "E1331", {"start": v(-539.17, 821.02) * mm, "end": v(-538.57, 821.34) * mm});
            skLineSegment(sketch, "E1332", {"start": v(-538.57, 821.34) * mm, "end": v(-537.97, 821.64) * mm});
            skLineSegment(sketch, "E1333", {"start": v(-537.97, 821.64) * mm, "end": v(-537.86, 821.56) * mm});
            skLineSegment(sketch, "E1334", {"start": v(-537.86, 821.56) * mm, "end": v(-537.76, 821.48) * mm});
            skLineSegment(sketch, "E1335", {"start": v(-537.76, 821.48) * mm, "end": v(-537.65, 821.4) * mm});
            skLineSegment(sketch, "E1336", {"start": v(-537.65, 821.4) * mm, "end": v(-537.54, 821.32) * mm});
            skLineSegment(sketch, "E1337", {"start": v(-537.54, 821.32) * mm, "end": v(-537.44, 821.24) * mm});
            skLineSegment(sketch, "E1338", {"start": v(-537.44, 821.24) * mm, "end": v(-537.34, 821.16) * mm});
            skLineSegment(sketch, "E1339", {"start": v(-537.34, 821.16) * mm, "end": v(-537.24, 821.07) * mm});
            skLineSegment(sketch, "E1340", {"start": v(-537.24, 821.07) * mm, "end": v(-537.14, 820.99) * mm});
            skLineSegment(sketch, "E1341", {"start": v(-537.14, 820.99) * mm, "end": v(-537.05, 820.9) * mm});
            skLineSegment(sketch, "E1342", {"start": v(-537.05, 820.9) * mm, "end": v(-536.95, 820.82) * mm});
            skLineSegment(sketch, "E1343", {"start": v(-536.95, 820.82) * mm, "end": v(-536.85, 820.73) * mm});
            skLineSegment(sketch, "E1344", {"start": v(-536.85, 820.73) * mm, "end": v(-536.76, 820.65) * mm});
            skLineSegment(sketch, "E1345", {"start": v(-536.76, 820.65) * mm, "end": v(-536.67, 820.56) * mm});
            skLineSegment(sketch, "E1346", {"start": v(-536.67, 820.56) * mm, "end": v(-536.58, 820.47) * mm});
            skLineSegment(sketch, "E1347", {"start": v(-536.58, 820.47) * mm, "end": v(-536.5, 820.38) * mm});
            skLineSegment(sketch, "E1348", {"start": v(-536.5, 820.38) * mm, "end": v(-536.4, 820.3) * mm});
            skLineSegment(sketch, "E1349", {"start": v(-536.4, 820.3) * mm, "end": v(-536.32, 820.2) * mm});
            skLineSegment(sketch, "E1350", {"start": v(-536.32, 820.2) * mm, "end": v(-536.23, 820.11) * mm});
            skLineSegment(sketch, "E1351", {"start": v(-536.23, 820.11) * mm, "end": v(-536.15, 820.02) * mm});
            skLineSegment(sketch, "E1352", {"start": v(-536.15, 820.02) * mm, "end": v(-536.07, 819.93) * mm});
            skLineSegment(sketch, "E1353", {"start": v(-536.07, 819.93) * mm, "end": v(-536, 819.84) * mm});
            skLineSegment(sketch, "E1354", {"start": v(-536, 819.84) * mm, "end": v(-535.92, 819.74) * mm});
            skLineSegment(sketch, "E1355", {"start": v(-535.92, 819.74) * mm, "end": v(-535.84, 819.65) * mm});
            skLineSegment(sketch, "E1356", {"start": v(-535.84, 819.65) * mm, "end": v(-535.77, 819.55) * mm});
            skLineSegment(sketch, "E1357", {"start": v(-535.77, 819.55) * mm, "end": v(-535.7, 819.45) * mm});
            skLineSegment(sketch, "E1358", {"start": v(-535.7, 819.45) * mm, "end": v(-535.63, 819.35) * mm});
            skLineSegment(sketch, "E1359", {"start": v(-535.63, 819.35) * mm, "end": v(-535.56, 819.26) * mm});
            skLineSegment(sketch, "E1360", {"start": v(-535.56, 819.26) * mm, "end": v(-535.5, 819.16) * mm});
            skLineSegment(sketch, "E1361", {"start": v(-535.5, 819.16) * mm, "end": v(-535.42, 819.06) * mm});
            skLineSegment(sketch, "E1362", {"start": v(-535.42, 819.06) * mm, "end": v(-535.34, 818.97) * mm});
            skLineSegment(sketch, "E1363", {"start": v(-535.34, 818.97) * mm, "end": v(-535.1, 818.38) * mm});
            skLineSegment(sketch, "E1364", {"start": v(-535.1, 818.38) * mm, "end": v(-533.41, 819.02) * mm});
            skLineSegment(sketch, "E1365", {"start": v(-533.41, 819.02) * mm, "end": v(-533.62, 819.63) * mm});
            skLineSegment(sketch, "E1366", {"start": v(-533.62, 819.63) * mm, "end": v(-533.62, 819.75) * mm});
            skLineSegment(sketch, "E1367", {"start": v(-533.62, 819.75) * mm, "end": v(-533.64, 819.87) * mm});
            skLineSegment(sketch, "E1368", {"start": v(-533.64, 819.87) * mm, "end": v(-533.66, 819.99) * mm});
            skLineSegment(sketch, "E1369", {"start": v(-533.66, 819.99) * mm, "end": v(-533.67, 820.1) * mm});
            skLineSegment(sketch, "E1370", {"start": v(-533.67, 820.1) * mm, "end": v(-533.68, 820.22) * mm});
            skLineSegment(sketch, "E1371", {"start": v(-533.68, 820.22) * mm, "end": v(-533.7, 820.34) * mm});
            skLineSegment(sketch, "E1372", {"start": v(-533.7, 820.34) * mm, "end": v(-533.7, 820.46) * mm});
            skLineSegment(sketch, "E1373", {"start": v(-533.7, 820.46) * mm, "end": v(-533.71, 820.59) * mm});
            skLineSegment(sketch, "E1374", {"start": v(-533.71, 820.59) * mm, "end": v(-533.72, 820.7) * mm});
            skLineSegment(sketch, "E1375", {"start": v(-533.72, 820.7) * mm, "end": v(-533.72, 820.83) * mm});
            skLineSegment(sketch, "E1376", {"start": v(-533.72, 820.83) * mm, "end": v(-533.72, 820.95) * mm});
            skLineSegment(sketch, "E1377", {"start": v(-533.72, 820.95) * mm, "end": v(-533.73, 821.08) * mm});
            skLineSegment(sketch, "E1378", {"start": v(-533.73, 821.08) * mm, "end": v(-533.72, 821.2) * mm});
            skLineSegment(sketch, "E1379", {"start": v(-533.72, 821.2) * mm, "end": v(-533.72, 821.32) * mm});
            skLineSegment(sketch, "E1380", {"start": v(-533.72, 821.32) * mm, "end": v(-533.72, 821.45) * mm});
            skLineSegment(sketch, "E1381", {"start": v(-533.72, 821.45) * mm, "end": v(-533.7, 821.57) * mm});
            skLineSegment(sketch, "E1382", {"start": v(-533.7, 821.57) * mm, "end": v(-533.7, 821.7) * mm});
            skLineSegment(sketch, "E1383", {"start": v(-533.7, 821.7) * mm, "end": v(-533.7, 821.83) * mm});
            skLineSegment(sketch, "E1384", {"start": v(-533.7, 821.83) * mm, "end": v(-533.68, 821.95) * mm});
            skLineSegment(sketch, "E1385", {"start": v(-533.68, 821.95) * mm, "end": v(-533.67, 822.08) * mm});
            skLineSegment(sketch, "E1386", {"start": v(-533.67, 822.08) * mm, "end": v(-533.65, 822.2) * mm});
            skLineSegment(sketch, "E1387", {"start": v(-533.65, 822.2) * mm, "end": v(-533.64, 822.34) * mm});
            skLineSegment(sketch, "E1388", {"start": v(-533.64, 822.34) * mm, "end": v(-533.62, 822.46) * mm});
            skLineSegment(sketch, "E1389", {"start": v(-533.62, 822.46) * mm, "end": v(-533.6, 822.6) * mm});
            skLineSegment(sketch, "E1390", {"start": v(-533.6, 822.6) * mm, "end": v(-533.58, 822.72) * mm});
            skLineSegment(sketch, "E1391", {"start": v(-533.58, 822.72) * mm, "end": v(-533.56, 822.85) * mm});
            skLineSegment(sketch, "E1392", {"start": v(-533.56, 822.85) * mm, "end": v(-533.54, 822.98) * mm});
            skLineSegment(sketch, "E1393", {"start": v(-533.54, 822.98) * mm, "end": v(-533.51, 823.1) * mm});
            skLineSegment(sketch, "E1394", {"start": v(-533.51, 823.1) * mm, "end": v(-533.48, 823.24) * mm});
            skLineSegment(sketch, "E1395", {"start": v(-533.48, 823.24) * mm, "end": v(-533.46, 823.37) * mm});
            skLineSegment(sketch, "E1396", {"start": v(-533.46, 823.37) * mm, "end": v(-532.8, 823.55) * mm});
            skLineSegment(sketch, "E1397", {"start": v(-532.8, 823.55) * mm, "end": v(-532.15, 823.72) * mm});
            skLineSegment(sketch, "E1398", {"start": v(-532.15, 823.72) * mm, "end": v(-532.06, 823.62) * mm});
            skLineSegment(sketch, "E1399", {"start": v(-532.06, 823.62) * mm, "end": v(-531.98, 823.52) * mm});
            skLineSegment(sketch, "E1400", {"start": v(-531.98, 823.52) * mm, "end": v(-531.89, 823.42) * mm});
            skLineSegment(sketch, "E1401", {"start": v(-531.89, 823.42) * mm, "end": v(-531.8, 823.32) * mm});
            skLineSegment(sketch, "E1402", {"start": v(-531.8, 823.32) * mm, "end": v(-531.72, 823.22) * mm});
            skLineSegment(sketch, "E1403", {"start": v(-531.72, 823.22) * mm, "end": v(-531.64, 823.12) * mm});
            skLineSegment(sketch, "E1404", {"start": v(-531.64, 823.12) * mm, "end": v(-531.56, 823.02) * mm});
            skLineSegment(sketch, "E1405", {"start": v(-531.56, 823.02) * mm, "end": v(-531.48, 822.91) * mm});
            skLineSegment(sketch, "E1406", {"start": v(-531.48, 822.91) * mm, "end": v(-531.4, 822.81) * mm});
            skLineSegment(sketch, "E1407", {"start": v(-531.4, 822.81) * mm, "end": v(-531.33, 822.7) * mm});
            skLineSegment(sketch, "E1408", {"start": v(-531.33, 822.7) * mm, "end": v(-531.25, 822.6) * mm});
            skLineSegment(sketch, "E1409", {"start": v(-531.25, 822.6) * mm, "end": v(-531.18, 822.5) * mm});
            skLineSegment(sketch, "E1410", {"start": v(-531.18, 822.5) * mm, "end": v(-531.1, 822.4) * mm});
            skLineSegment(sketch, "E1411", {"start": v(-531.1, 822.4) * mm, "end": v(-531.04, 822.3) * mm});
            skLineSegment(sketch, "E1412", {"start": v(-531.04, 822.3) * mm, "end": v(-530.97, 822.18) * mm});
            skLineSegment(sketch, "E1413", {"start": v(-530.97, 822.18) * mm, "end": v(-530.9, 822.08) * mm});
            skLineSegment(sketch, "E1414", {"start": v(-530.9, 822.08) * mm, "end": v(-530.84, 821.97) * mm});
            skLineSegment(sketch, "E1415", {"start": v(-530.84, 821.97) * mm, "end": v(-530.77, 821.87) * mm});
            skLineSegment(sketch, "E1416", {"start": v(-530.77, 821.87) * mm, "end": v(-530.71, 821.76) * mm});
            skLineSegment(sketch, "E1417", {"start": v(-530.71, 821.76) * mm, "end": v(-530.65, 821.65) * mm});
            skLineSegment(sketch, "E1418", {"start": v(-530.65, 821.65) * mm, "end": v(-530.6, 821.55) * mm});
            skLineSegment(sketch, "E1419", {"start": v(-530.6, 821.55) * mm, "end": v(-530.54, 821.44) * mm});
            skLineSegment(sketch, "E1420", {"start": v(-530.54, 821.44) * mm, "end": v(-530.48, 821.33) * mm});
            skLineSegment(sketch, "E1421", {"start": v(-530.48, 821.33) * mm, "end": v(-530.43, 821.22) * mm});
            skLineSegment(sketch, "E1422", {"start": v(-530.43, 821.22) * mm, "end": v(-530.38, 821.1) * mm});
            skLineSegment(sketch, "E1423", {"start": v(-530.38, 821.1) * mm, "end": v(-530.33, 821) * mm});
            skLineSegment(sketch, "E1424", {"start": v(-530.33, 821) * mm, "end": v(-530.29, 820.89) * mm});
            skLineSegment(sketch, "E1425", {"start": v(-530.29, 820.89) * mm, "end": v(-530.24, 820.78) * mm});
            skLineSegment(sketch, "E1426", {"start": v(-530.24, 820.78) * mm, "end": v(-530.2, 820.67) * mm});
            skLineSegment(sketch, "E1427", {"start": v(-530.2, 820.67) * mm, "end": v(-530.14, 820.56) * mm});
            skLineSegment(sketch, "E1428", {"start": v(-530.14, 820.56) * mm, "end": v(-530.02, 819.93) * mm});
            skLineSegment(sketch, "E1429", {"start": v(-530.02, 819.93) * mm, "end": v(-528.24, 820.21) * mm});
            skLineSegment(sketch, "E1430", {"start": v(-528.24, 820.21) * mm, "end": v(-528.32, 820.85) * mm});
            skLineSegment(sketch, "E1431", {"start": v(-528.32, 820.85) * mm, "end": v(-528.3, 820.97) * mm});
            skLineSegment(sketch, "E1432", {"start": v(-528.3, 820.97) * mm, "end": v(-528.29, 821.09) * mm});
            skLineSegment(sketch, "E1433", {"start": v(-528.29, 821.09) * mm, "end": v(-528.28, 821.2) * mm});
            skLineSegment(sketch, "E1434", {"start": v(-528.28, 821.2) * mm, "end": v(-528.27, 821.33) * mm});
            skLineSegment(sketch, "E1435", {"start": v(-528.27, 821.33) * mm, "end": v(-528.25, 821.45) * mm});
            skLineSegment(sketch, "E1436", {"start": v(-528.25, 821.45) * mm, "end": v(-528.24, 821.57) * mm});
            skLineSegment(sketch, "E1437", {"start": v(-528.24, 821.57) * mm, "end": v(-528.23, 821.69) * mm});
            skLineSegment(sketch, "E1438", {"start": v(-528.23, 821.69) * mm, "end": v(-528.2, 821.8) * mm});
            skLineSegment(sketch, "E1439", {"start": v(-528.2, 821.8) * mm, "end": v(-528.19, 821.93) * mm});
            skLineSegment(sketch, "E1440", {"start": v(-528.19, 821.93) * mm, "end": v(-528.17, 822.05) * mm});
            skLineSegment(sketch, "E1441", {"start": v(-528.17, 822.05) * mm, "end": v(-528.14, 822.17) * mm});
            skLineSegment(sketch, "E1442", {"start": v(-528.14, 822.17) * mm, "end": v(-528.12, 822.29) * mm});
            skLineSegment(sketch, "E1443", {"start": v(-528.12, 822.29) * mm, "end": v(-528.1, 822.4) * mm});
            skLineSegment(sketch, "E1444", {"start": v(-528.1, 822.4) * mm, "end": v(-528.06, 822.53) * mm});
            skLineSegment(sketch, "E1445", {"start": v(-528.06, 822.53) * mm, "end": v(-528.03, 822.65) * mm});
            skLineSegment(sketch, "E1446", {"start": v(-528.03, 822.65) * mm, "end": v(-528, 822.77) * mm});
            skLineSegment(sketch, "E1447", {"start": v(-528, 822.77) * mm, "end": v(-527.97, 822.9) * mm});
            skLineSegment(sketch, "E1448", {"start": v(-527.97, 822.9) * mm, "end": v(-527.93, 823.02) * mm});
            skLineSegment(sketch, "E1449", {"start": v(-527.93, 823.02) * mm, "end": v(-527.9, 823.14) * mm});
            skLineSegment(sketch, "E1450", {"start": v(-527.9, 823.14) * mm, "end": v(-527.85, 823.26) * mm});
            skLineSegment(sketch, "E1451", {"start": v(-527.85, 823.26) * mm, "end": v(-527.81, 823.38) * mm});
            skLineSegment(sketch, "E1452", {"start": v(-527.81, 823.38) * mm, "end": v(-527.77, 823.5) * mm});
            skLineSegment(sketch, "E1453", {"start": v(-527.77, 823.5) * mm, "end": v(-527.73, 823.62) * mm});
            skLineSegment(sketch, "E1454", {"start": v(-527.73, 823.62) * mm, "end": v(-527.68, 823.74) * mm});
            skLineSegment(sketch, "E1455", {"start": v(-527.68, 823.74) * mm, "end": v(-527.63, 823.87) * mm});
            skLineSegment(sketch, "E1456", {"start": v(-527.63, 823.87) * mm, "end": v(-527.59, 823.99) * mm});
            skLineSegment(sketch, "E1457", {"start": v(-527.59, 823.99) * mm, "end": v(-527.54, 824.1) * mm});
            skLineSegment(sketch, "E1458", {"start": v(-527.54, 824.1) * mm, "end": v(-527.48, 824.23) * mm});
            skLineSegment(sketch, "E1459", {"start": v(-527.48, 824.23) * mm, "end": v(-527.43, 824.35) * mm});
            skLineSegment(sketch, "E1460", {"start": v(-527.43, 824.35) * mm, "end": v(-527.38, 824.48) * mm});
            skLineSegment(sketch, "E1461", {"start": v(-527.38, 824.48) * mm, "end": v(-526.7, 824.52) * mm});
            skLineSegment(sketch, "E1462", {"start": v(-526.7, 824.52) * mm, "end": v(-526.03, 824.55) * mm});
            skLineSegment(sketch, "E1463", {"start": v(-526.03, 824.55) * mm, "end": v(-525.96, 824.43) * mm});
            skLineSegment(sketch, "E1464", {"start": v(-525.96, 824.43) * mm, "end": v(-525.9, 824.32) * mm});
            skLineSegment(sketch, "E1465", {"start": v(-525.9, 824.32) * mm, "end": v(-525.83, 824.2) * mm});
            skLineSegment(sketch, "E1466", {"start": v(-525.83, 824.2) * mm, "end": v(-525.77, 824.08) * mm});
            skLineSegment(sketch, "E1467", {"start": v(-525.77, 824.08) * mm, "end": v(-525.71, 823.97) * mm});
            skLineSegment(sketch, "E1468", {"start": v(-525.71, 823.97) * mm, "end": v(-525.65, 823.85) * mm});
            skLineSegment(sketch, "E1469", {"start": v(-525.65, 823.85) * mm, "end": v(-525.6, 823.73) * mm});
            skLineSegment(sketch, "E1470", {"start": v(-525.6, 823.73) * mm, "end": v(-525.54, 823.62) * mm});
            skLineSegment(sketch, "E1471", {"start": v(-525.54, 823.62) * mm, "end": v(-525.48, 823.5) * mm});
            skLineSegment(sketch, "E1472", {"start": v(-525.48, 823.5) * mm, "end": v(-525.43, 823.38) * mm});
            skLineSegment(sketch, "E1473", {"start": v(-525.43, 823.38) * mm, "end": v(-525.38, 823.27) * mm});
            skLineSegment(sketch, "E1474", {"start": v(-525.38, 823.27) * mm, "end": v(-525.33, 823.15) * mm});
            skLineSegment(sketch, "E1475", {"start": v(-525.33, 823.15) * mm, "end": v(-525.28, 823.03) * mm});
            skLineSegment(sketch, "E1476", {"start": v(-525.28, 823.03) * mm, "end": v(-525.23, 822.92) * mm});
            skLineSegment(sketch, "E1477", {"start": v(-525.23, 822.92) * mm, "end": v(-525.2, 822.8) * mm});
            skLineSegment(sketch, "E1478", {"start": v(-525.2, 822.8) * mm, "end": v(-525.15, 822.68) * mm});
            skLineSegment(sketch, "E1479", {"start": v(-525.15, 822.68) * mm, "end": v(-525.1, 822.56) * mm});
            skLineSegment(sketch, "E1480", {"start": v(-525.1, 822.56) * mm, "end": v(-525.07, 822.45) * mm});
            skLineSegment(sketch, "E1481", {"start": v(-525.07, 822.45) * mm, "end": v(-525.03, 822.33) * mm});
            skLineSegment(sketch, "E1482", {"start": v(-525.03, 822.33) * mm, "end": v(-525, 822.21) * mm});
            skLineSegment(sketch, "E1483", {"start": v(-525, 822.21) * mm, "end": v(-524.96, 822.1) * mm});
            skLineSegment(sketch, "E1484", {"start": v(-524.96, 822.1) * mm, "end": v(-524.93, 821.98) * mm});
            skLineSegment(sketch, "E1485", {"start": v(-524.93, 821.98) * mm, "end": v(-524.9, 821.86) * mm});
            skLineSegment(sketch, "E1486", {"start": v(-524.9, 821.86) * mm, "end": v(-524.87, 821.74) * mm});
            skLineSegment(sketch, "E1487", {"start": v(-524.87, 821.74) * mm, "end": v(-524.84, 821.63) * mm});
            skLineSegment(sketch, "E1488", {"start": v(-524.84, 821.63) * mm, "end": v(-524.82, 821.5) * mm});
            skLineSegment(sketch, "E1489", {"start": v(-524.82, 821.5) * mm, "end": v(-524.8, 821.39) * mm});
            skLineSegment(sketch, "E1490", {"start": v(-524.8, 821.39) * mm, "end": v(-524.78, 821.27) * mm});
            skLineSegment(sketch, "E1491", {"start": v(-524.78, 821.27) * mm, "end": v(-524.75, 821.15) * mm});
            skLineSegment(sketch, "E1492", {"start": v(-524.75, 821.15) * mm, "end": v(-524.72, 821.04) * mm});
            skLineSegment(sketch, "E1493", {"start": v(-524.72, 821.04) * mm, "end": v(-524.73, 820.4) * mm});
            skLineSegment(sketch, "E1494", {"start": v(-524.73, 820.4) * mm, "end": v(-522.93, 820.3) * mm});
            skLineSegment(sketch, "E1495", {"start": v(-522.93, 820.3) * mm, "end": v(-522.88, 820.94) * mm});
            skLineSegment(sketch, "E1496", {"start": v(-522.88, 820.94) * mm, "end": v(-522.83, 821.05) * mm});
            skLineSegment(sketch, "E1497", {"start": v(-522.83, 821.05) * mm, "end": v(-522.8, 821.17) * mm});
            skLineSegment(sketch, "E1498", {"start": v(-522.8, 821.17) * mm, "end": v(-522.76, 821.28) * mm});
            skLineSegment(sketch, "E1499", {"start": v(-522.76, 821.28) * mm, "end": v(-522.73, 821.4) * mm});
            skLineSegment(sketch, "E1500", {"start": v(-522.73, 821.4) * mm, "end": v(-522.69, 821.51) * mm});
            skLineSegment(sketch, "E1501", {"start": v(-522.69, 821.51) * mm, "end": v(-522.65, 821.63) * mm});
            skLineSegment(sketch, "E1502", {"start": v(-522.65, 821.63) * mm, "end": v(-522.61, 821.74) * mm});
            skLineSegment(sketch, "E1503", {"start": v(-522.61, 821.74) * mm, "end": v(-522.57, 821.85) * mm});
            skLineSegment(sketch, "E1504", {"start": v(-522.57, 821.85) * mm, "end": v(-522.53, 821.97) * mm});
            skLineSegment(sketch, "E1505", {"start": v(-522.53, 821.97) * mm, "end": v(-522.48, 822.08) * mm});
            skLineSegment(sketch, "E1506", {"start": v(-522.48, 822.08) * mm, "end": v(-522.43, 822.2) * mm});
            skLineSegment(sketch, "E1507", {"start": v(-522.43, 822.2) * mm, "end": v(-522.38, 822.3) * mm});
            skLineSegment(sketch, "E1508", {"start": v(-522.38, 822.3) * mm, "end": v(-522.33, 822.42) * mm});
            skLineSegment(sketch, "E1509", {"start": v(-522.33, 822.42) * mm, "end": v(-522.28, 822.53) * mm});
            skLineSegment(sketch, "E1510", {"start": v(-522.28, 822.53) * mm, "end": v(-522.22, 822.64) * mm});
            skLineSegment(sketch, "E1511", {"start": v(-522.22, 822.64) * mm, "end": v(-522.16, 822.76) * mm});
            skLineSegment(sketch, "E1512", {"start": v(-522.16, 822.76) * mm, "end": v(-522.1, 822.87) * mm});
            skLineSegment(sketch, "E1513", {"start": v(-522.1, 822.87) * mm, "end": v(-522.04, 822.98) * mm});
            skLineSegment(sketch, "E1514", {"start": v(-522.04, 822.98) * mm, "end": v(-521.98, 823.09) * mm});
            skLineSegment(sketch, "E1515", {"start": v(-521.98, 823.09) * mm, "end": v(-521.92, 823.2) * mm});
            skLineSegment(sketch, "E1516", {"start": v(-521.92, 823.2) * mm, "end": v(-521.86, 823.31) * mm});
            skLineSegment(sketch, "E1517", {"start": v(-521.86, 823.31) * mm, "end": v(-521.79, 823.42) * mm});
            skLineSegment(sketch, "E1518", {"start": v(-521.79, 823.42) * mm, "end": v(-521.72, 823.53) * mm});
            skLineSegment(sketch, "E1519", {"start": v(-521.72, 823.53) * mm, "end": v(-521.65, 823.64) * mm});
            skLineSegment(sketch, "E1520", {"start": v(-521.65, 823.64) * mm, "end": v(-521.58, 823.75) * mm});
            skLineSegment(sketch, "E1521", {"start": v(-521.58, 823.75) * mm, "end": v(-521.5, 823.86) * mm});
            skLineSegment(sketch, "E1522", {"start": v(-521.5, 823.86) * mm, "end": v(-521.43, 823.97) * mm});
            skLineSegment(sketch, "E1523", {"start": v(-521.43, 823.97) * mm, "end": v(-521.36, 824.08) * mm});
            skLineSegment(sketch, "E1524", {"start": v(-521.36, 824.08) * mm, "end": v(-521.28, 824.18) * mm});
            skLineSegment(sketch, "E1525", {"start": v(-521.28, 824.18) * mm, "end": v(-521.2, 824.3) * mm});
            skLineSegment(sketch, "E1526", {"start": v(-521.2, 824.3) * mm, "end": v(-520.54, 824.2) * mm});
            skLineSegment(sketch, "E1527", {"start": v(-520.54, 824.2) * mm, "end": v(-519.87, 824.08) * mm});
            skLineSegment(sketch, "E1528", {"start": v(-519.87, 824.08) * mm, "end": v(-519.83, 823.95) * mm});
            skLineSegment(sketch, "E1529", {"start": v(-519.83, 823.95) * mm, "end": v(-519.79, 823.83) * mm});
            skLineSegment(sketch, "E1530", {"start": v(-519.79, 823.83) * mm, "end": v(-519.75, 823.7) * mm});
            skLineSegment(sketch, "E1531", {"start": v(-519.75, 823.7) * mm, "end": v(-519.72, 823.57) * mm});
            skLineSegment(sketch, "E1532", {"start": v(-519.72, 823.57) * mm, "end": v(-519.68, 823.45) * mm});
            skLineSegment(sketch, "E1533", {"start": v(-519.68, 823.45) * mm, "end": v(-519.64, 823.32) * mm});
            skLineSegment(sketch, "E1534", {"start": v(-519.64, 823.32) * mm, "end": v(-519.61, 823.2) * mm});
            skLineSegment(sketch, "E1535", {"start": v(-519.61, 823.2) * mm, "end": v(-519.58, 823.07) * mm});
            skLineSegment(sketch, "E1536", {"start": v(-519.58, 823.07) * mm, "end": v(-519.55, 822.95) * mm});
            skLineSegment(sketch, "E1537", {"start": v(-519.55, 822.95) * mm, "end": v(-519.53, 822.82) * mm});
            skLineSegment(sketch, "E1538", {"start": v(-519.53, 822.82) * mm, "end": v(-519.5, 822.7) * mm});
            skLineSegment(sketch, "E1539", {"start": v(-519.5, 822.7) * mm, "end": v(-519.47, 822.57) * mm});
            skLineSegment(sketch, "E1540", {"start": v(-519.47, 822.57) * mm, "end": v(-519.45, 822.45) * mm});
            skLineSegment(sketch, "E1541", {"start": v(-519.45, 822.45) * mm, "end": v(-519.43, 822.32) * mm});
            skLineSegment(sketch, "E1542", {"start": v(-519.43, 822.32) * mm, "end": v(-519.41, 822.2) * mm});
            skLineSegment(sketch, "E1543", {"start": v(-519.41, 822.2) * mm, "end": v(-519.4, 822.08) * mm});
            skLineSegment(sketch, "E1544", {"start": v(-519.4, 822.08) * mm, "end": v(-519.38, 821.95) * mm});
            skLineSegment(sketch, "E1545", {"start": v(-519.38, 821.95) * mm, "end": v(-519.36, 821.83) * mm});
            skLineSegment(sketch, "E1546", {"start": v(-519.36, 821.83) * mm, "end": v(-519.35, 821.7) * mm});
            skLineSegment(sketch, "E1547", {"start": v(-519.35, 821.7) * mm, "end": v(-519.34, 821.58) * mm});
            skLineSegment(sketch, "E1548", {"start": v(-519.34, 821.58) * mm, "end": v(-519.33, 821.46) * mm});
            skLineSegment(sketch, "E1549", {"start": v(-519.33, 821.46) * mm, "end": v(-519.32, 821.34) * mm});
            skLineSegment(sketch, "E1550", {"start": v(-519.32, 821.34) * mm, "end": v(-519.32, 821.22) * mm});
            skLineSegment(sketch, "E1551", {"start": v(-519.32, 821.22) * mm, "end": v(-519.32, 821.1) * mm});
            skLineSegment(sketch, "E1552", {"start": v(-519.32, 821.1) * mm, "end": v(-519.31, 820.98) * mm});
            skLineSegment(sketch, "E1553", {"start": v(-519.31, 820.98) * mm, "end": v(-519.31, 820.86) * mm});
            skLineSegment(sketch, "E1554", {"start": v(-519.31, 820.86) * mm, "end": v(-519.32, 820.74) * mm});
            skLineSegment(sketch, "E1555", {"start": v(-519.32, 820.74) * mm, "end": v(-519.32, 820.62) * mm});
            skLineSegment(sketch, "E1556", {"start": v(-519.32, 820.62) * mm, "end": v(-519.33, 820.5) * mm});
            skLineSegment(sketch, "E1557", {"start": v(-519.33, 820.5) * mm, "end": v(-519.31, 820.38) * mm});
            skLineSegment(sketch, "E1558", {"start": v(-519.31, 820.38) * mm, "end": v(-519.46, 819.76) * mm});
            skLineSegment(sketch, "E1559", {"start": v(-519.46, 819.76) * mm, "end": v(-517.72, 819.29) * mm});
            skLineSegment(sketch, "E1560", {"start": v(-517.72, 819.29) * mm, "end": v(-517.53, 819.9) * mm});
            skLineSegment(sketch, "E1561", {"start": v(-517.53, 819.9) * mm, "end": v(-517.46, 820) * mm});
            skLineSegment(sketch, "E1562", {"start": v(-517.46, 820) * mm, "end": v(-517.4, 820.1) * mm});
            skLineSegment(sketch, "E1563", {"start": v(-517.4, 820.1) * mm, "end": v(-517.35, 820.21) * mm});
            skLineSegment(sketch, "E1564", {"start": v(-517.35, 820.21) * mm, "end": v(-517.3, 820.32) * mm});
            skLineSegment(sketch, "E1565", {"start": v(-517.3, 820.32) * mm, "end": v(-517.23, 820.42) * mm});
            skLineSegment(sketch, "E1566", {"start": v(-517.23, 820.42) * mm, "end": v(-517.17, 820.52) * mm});
            skLineSegment(sketch, "E1567", {"start": v(-517.17, 820.52) * mm, "end": v(-517.1, 820.63) * mm});
            skLineSegment(sketch, "E1568", {"start": v(-517.1, 820.63) * mm, "end": v(-517.05, 820.73) * mm});
            skLineSegment(sketch, "E1569", {"start": v(-517.05, 820.73) * mm, "end": v(-516.98, 820.83) * mm});
            skLineSegment(sketch, "E1570", {"start": v(-516.98, 820.83) * mm, "end": v(-516.9, 820.93) * mm});
            skLineSegment(sketch, "E1571", {"start": v(-516.9, 820.93) * mm, "end": v(-516.84, 821.03) * mm});
            skLineSegment(sketch, "E1572", {"start": v(-516.84, 821.03) * mm, "end": v(-516.77, 821.13) * mm});
            skLineSegment(sketch, "E1573", {"start": v(-516.77, 821.13) * mm, "end": v(-516.7, 821.23) * mm});
            skLineSegment(sketch, "E1574", {"start": v(-516.7, 821.23) * mm, "end": v(-516.62, 821.33) * mm});
            skLineSegment(sketch, "E1575", {"start": v(-516.62, 821.33) * mm, "end": v(-516.54, 821.43) * mm});
            skLineSegment(sketch, "E1576", {"start": v(-516.54, 821.43) * mm, "end": v(-516.46, 821.53) * mm});
            skLineSegment(sketch, "E1577", {"start": v(-516.46, 821.53) * mm, "end": v(-516.38, 821.62) * mm});
            skLineSegment(sketch, "E1578", {"start": v(-516.38, 821.62) * mm, "end": v(-516.3, 821.72) * mm});
            skLineSegment(sketch, "E1579", {"start": v(-516.3, 821.72) * mm, "end": v(-516.21, 821.82) * mm});
            skLineSegment(sketch, "E1580", {"start": v(-516.21, 821.82) * mm, "end": v(-516.13, 821.91) * mm});
            skLineSegment(sketch, "E1581", {"start": v(-516.13, 821.91) * mm, "end": v(-516.04, 822) * mm});
            skLineSegment(sketch, "E1582", {"start": v(-516.04, 822) * mm, "end": v(-515.95, 822.1) * mm});
            skLineSegment(sketch, "E1583", {"start": v(-515.95, 822.1) * mm, "end": v(-515.87, 822.2) * mm});
            skLineSegment(sketch, "E1584", {"start": v(-515.87, 822.2) * mm, "end": v(-515.77, 822.29) * mm});
            skLineSegment(sketch, "E1585", {"start": v(-515.77, 822.29) * mm, "end": v(-515.68, 822.38) * mm});
            skLineSegment(sketch, "E1586", {"start": v(-515.68, 822.38) * mm, "end": v(-515.59, 822.47) * mm});
            skLineSegment(sketch, "E1587", {"start": v(-515.59, 822.47) * mm, "end": v(-515.5, 822.56) * mm});
            skLineSegment(sketch, "E1588", {"start": v(-515.5, 822.56) * mm, "end": v(-515.4, 822.65) * mm});
            skLineSegment(sketch, "E1589", {"start": v(-515.4, 822.65) * mm, "end": v(-515.3, 822.74) * mm});
            skLineSegment(sketch, "E1590", {"start": v(-515.3, 822.74) * mm, "end": v(-515.2, 822.83) * mm});
            skLineSegment(sketch, "E1591", {"start": v(-515.2, 822.83) * mm, "end": v(-514.57, 822.6) * mm});
            skLineSegment(sketch, "E1592", {"start": v(-514.57, 822.6) * mm, "end": v(-513.94, 822.35) * mm});
            skLineSegment(sketch, "E1593", {"start": v(-513.94, 822.35) * mm, "end": v(-513.93, 822.21) * mm});
            skLineSegment(sketch, "E1594", {"start": v(-513.93, 822.21) * mm, "end": v(-513.91, 822.08) * mm});
            skLineSegment(sketch, "E1595", {"start": v(-513.91, 822.08) * mm, "end": v(-513.9, 821.95) * mm});
            skLineSegment(sketch, "E1596", {"start": v(-513.9, 821.95) * mm, "end": v(-513.9, 821.82) * mm});
            skLineSegment(sketch, "E1597", {"start": v(-513.9, 821.82) * mm, "end": v(-513.88, 821.69) * mm});
            skLineSegment(sketch, "E1598", {"start": v(-513.88, 821.69) * mm, "end": v(-513.88, 821.56) * mm});
            skLineSegment(sketch, "E1599", {"start": v(-513.88, 821.56) * mm, "end": v(-513.87, 821.43) * mm});
            skLineSegment(sketch, "E1600", {"start": v(-513.87, 821.43) * mm, "end": v(-513.87, 821.3) * mm});
            skLineSegment(sketch, "E1601", {"start": v(-513.87, 821.3) * mm, "end": v(-513.87, 821.17) * mm});
            skLineSegment(sketch, "E1602", {"start": v(-513.87, 821.17) * mm, "end": v(-513.87, 821.04) * mm});
            skLineSegment(sketch, "E1603", {"start": v(-513.87, 821.04) * mm, "end": v(-513.87, 820.91) * mm});
            skLineSegment(sketch, "E1604", {"start": v(-513.87, 820.91) * mm, "end": v(-513.87, 820.79) * mm});
            skLineSegment(sketch, "E1605", {"start": v(-513.87, 820.79) * mm, "end": v(-513.87, 820.66) * mm});
            skLineSegment(sketch, "E1606", {"start": v(-513.87, 820.66) * mm, "end": v(-513.88, 820.53) * mm});
            skLineSegment(sketch, "E1607", {"start": v(-513.88, 820.53) * mm, "end": v(-513.88, 820.4) * mm});
            skLineSegment(sketch, "E1608", {"start": v(-513.88, 820.4) * mm, "end": v(-513.9, 820.28) * mm});
            skLineSegment(sketch, "E1609", {"start": v(-513.9, 820.28) * mm, "end": v(-513.9, 820.16) * mm});
            skLineSegment(sketch, "E1610", {"start": v(-513.9, 820.16) * mm, "end": v(-513.91, 820.04) * mm});
            skLineSegment(sketch, "E1611", {"start": v(-513.91, 820.04) * mm, "end": v(-513.93, 819.92) * mm});
            skLineSegment(sketch, "E1612", {"start": v(-513.93, 819.92) * mm, "end": v(-513.94, 819.8) * mm});
            skLineSegment(sketch, "E1613", {"start": v(-513.94, 819.8) * mm, "end": v(-513.96, 819.67) * mm});
            skLineSegment(sketch, "E1614", {"start": v(-513.96, 819.67) * mm, "end": v(-513.98, 819.55) * mm});
            skLineSegment(sketch, "E1615", {"start": v(-513.98, 819.55) * mm, "end": v(-514, 819.43) * mm});
            skLineSegment(sketch, "E1616", {"start": v(-514, 819.43) * mm, "end": v(-514.02, 819.31) * mm});
            skLineSegment(sketch, "E1617", {"start": v(-514.02, 819.31) * mm, "end": v(-514.04, 819.2) * mm});
            skLineSegment(sketch, "E1618", {"start": v(-514.04, 819.2) * mm, "end": v(-514.07, 819.08) * mm});
            skLineSegment(sketch, "E1619", {"start": v(-514.07, 819.08) * mm, "end": v(-514.1, 818.96) * mm});
            skLineSegment(sketch, "E1620", {"start": v(-514.1, 818.96) * mm, "end": v(-514.13, 818.85) * mm});
            skLineSegment(sketch, "E1621", {"start": v(-514.13, 818.85) * mm, "end": v(-514.15, 818.73) * mm});
            skLineSegment(sketch, "E1622", {"start": v(-514.15, 818.73) * mm, "end": v(-514.17, 818.6) * mm});
            skLineSegment(sketch, "E1623", {"start": v(-514.17, 818.6) * mm, "end": v(-514.44, 818.03) * mm});
            skLineSegment(sketch, "E1624", {"start": v(-514.44, 818.03) * mm, "end": v(-512.84, 817.21) * mm});
            skLineSegment(sketch, "E1625", {"start": v(-512.84, 817.21) * mm, "end": v(-512.53, 817.77) * mm});
            skLineSegment(sketch, "E1626", {"start": v(-512.53, 817.77) * mm, "end": v(-512.43, 817.85) * mm});
            skLineSegment(sketch, "E1627", {"start": v(-512.43, 817.85) * mm, "end": v(-512.36, 817.95) * mm});
            skLineSegment(sketch, "E1628", {"start": v(-512.36, 817.95) * mm, "end": v(-512.28, 818.04) * mm});
            skLineSegment(sketch, "E1629", {"start": v(-512.28, 818.04) * mm, "end": v(-512.2, 818.13) * mm});
            skLineSegment(sketch, "E1630", {"start": v(-512.2, 818.13) * mm, "end": v(-512.12, 818.22) * mm});
            skLineSegment(sketch, "E1631", {"start": v(-512.12, 818.22) * mm, "end": v(-512.04, 818.3) * mm});
            skLineSegment(sketch, "E1632", {"start": v(-512.04, 818.3) * mm, "end": v(-511.96, 818.4) * mm});
            skLineSegment(sketch, "E1633", {"start": v(-511.96, 818.4) * mm, "end": v(-511.87, 818.48) * mm});
            skLineSegment(sketch, "E1634", {"start": v(-511.87, 818.48) * mm, "end": v(-511.79, 818.57) * mm});
            skLineSegment(sketch, "E1635", {"start": v(-511.79, 818.57) * mm, "end": v(-511.7, 818.65) * mm});
            skLineSegment(sketch, "E1636", {"start": v(-511.7, 818.65) * mm, "end": v(-511.6, 818.73) * mm});
            skLineSegment(sketch, "E1637", {"start": v(-511.6, 818.73) * mm, "end": v(-511.52, 818.82) * mm});
            skLineSegment(sketch, "E1638", {"start": v(-511.52, 818.82) * mm, "end": v(-511.42, 818.9) * mm});
            skLineSegment(sketch, "E1639", {"start": v(-511.42, 818.9) * mm, "end": v(-511.33, 818.98) * mm});
            skLineSegment(sketch, "E1640", {"start": v(-511.33, 818.98) * mm, "end": v(-511.23, 819.06) * mm});
            skLineSegment(sketch, "E1641", {"start": v(-511.23, 819.06) * mm, "end": v(-511.14, 819.14) * mm});
            skLineSegment(sketch, "E1642", {"start": v(-511.14, 819.14) * mm, "end": v(-511.04, 819.22) * mm});
            skLineSegment(sketch, "E1643", {"start": v(-511.04, 819.22) * mm, "end": v(-510.94, 819.3) * mm});
            skLineSegment(sketch, "E1644", {"start": v(-510.94, 819.3) * mm, "end": v(-510.84, 819.37) * mm});
            skLineSegment(sketch, "E1645", {"start": v(-510.84, 819.37) * mm, "end": v(-510.73, 819.45) * mm});
            skLineSegment(sketch, "E1646", {"start": v(-510.73, 819.45) * mm, "end": v(-510.63, 819.52) * mm});
            skLineSegment(sketch, "E1647", {"start": v(-510.63, 819.52) * mm, "end": v(-510.52, 819.6) * mm});
            skLineSegment(sketch, "E1648", {"start": v(-510.52, 819.6) * mm, "end": v(-510.42, 819.67) * mm});
            skLineSegment(sketch, "E1649", {"start": v(-510.42, 819.67) * mm, "end": v(-510.3, 819.74) * mm});
            skLineSegment(sketch, "E1650", {"start": v(-510.3, 819.74) * mm, "end": v(-510.2, 819.8) * mm});
            skLineSegment(sketch, "E1651", {"start": v(-510.2, 819.8) * mm, "end": v(-510.09, 819.88) * mm});
            skLineSegment(sketch, "E1652", {"start": v(-510.09, 819.88) * mm, "end": v(-509.98, 819.95) * mm});
            skLineSegment(sketch, "E1653", {"start": v(-509.98, 819.95) * mm, "end": v(-509.86, 820.02) * mm});
            skLineSegment(sketch, "E1654", {"start": v(-509.86, 820.02) * mm, "end": v(-509.75, 820.09) * mm});
            skLineSegment(sketch, "E1655", {"start": v(-509.75, 820.09) * mm, "end": v(-509.63, 820.15) * mm});
            skLineSegment(sketch, "E1656", {"start": v(-509.63, 820.15) * mm, "end": v(-509.06, 819.8) * mm});
            skLineSegment(sketch, "E1657", {"start": v(-509.06, 819.8) * mm, "end": v(-508.5, 819.42) * mm});
            skLineSegment(sketch, "E1658", {"start": v(-508.5, 819.42) * mm, "end": v(-508.52, 819.28) * mm});
            skLineSegment(sketch, "E1659", {"start": v(-508.52, 819.28) * mm, "end": v(-508.53, 819.15) * mm});
            skLineSegment(sketch, "E1660", {"start": v(-508.53, 819.15) * mm, "end": v(-508.55, 819.02) * mm});
            skLineSegment(sketch, "E1661", {"start": v(-508.55, 819.02) * mm, "end": v(-508.57, 818.9) * mm});
            skLineSegment(sketch, "E1662", {"start": v(-508.57, 818.9) * mm, "end": v(-508.58, 818.76) * mm});
            skLineSegment(sketch, "E1663", {"start": v(-508.58, 818.76) * mm, "end": v(-508.6, 818.63) * mm});
            skLineSegment(sketch, "E1664", {"start": v(-508.6, 818.63) * mm, "end": v(-508.63, 818.5) * mm});
            skLineSegment(sketch, "E1665", {"start": v(-508.63, 818.5) * mm, "end": v(-508.65, 818.38) * mm});
            skLineSegment(sketch, "E1666", {"start": v(-508.65, 818.38) * mm, "end": v(-508.67, 818.25) * mm});
            skLineSegment(sketch, "E1667", {"start": v(-508.67, 818.25) * mm, "end": v(-508.7, 818.12) * mm});
            skLineSegment(sketch, "E1668", {"start": v(-508.7, 818.12) * mm, "end": v(-508.73, 818) * mm});
            skLineSegment(sketch, "E1669", {"start": v(-508.73, 818) * mm, "end": v(-508.76, 817.88) * mm});
            skLineSegment(sketch, "E1670", {"start": v(-508.76, 817.88) * mm, "end": v(-508.79, 817.75) * mm});
            skLineSegment(sketch, "E1671", {"start": v(-508.79, 817.75) * mm, "end": v(-508.82, 817.63) * mm});
            skLineSegment(sketch, "E1672", {"start": v(-508.82, 817.63) * mm, "end": v(-508.85, 817.51) * mm});
            skLineSegment(sketch, "E1673", {"start": v(-508.85, 817.51) * mm, "end": v(-508.88, 817.4) * mm});
            skLineSegment(sketch, "E1674", {"start": v(-508.88, 817.4) * mm, "end": v(-508.92, 817.27) * mm});
            skLineSegment(sketch, "E1675", {"start": v(-508.92, 817.27) * mm, "end": v(-508.96, 817.15) * mm});
            skLineSegment(sketch, "E1676", {"start": v(-508.96, 817.15) * mm, "end": v(-509, 817.04) * mm});
            skLineSegment(sketch, "E1677", {"start": v(-509, 817.04) * mm, "end": v(-509.03, 816.92) * mm});
            skLineSegment(sketch, "E1678", {"start": v(-509.03, 816.92) * mm, "end": v(-509.07, 816.8) * mm});
            skLineSegment(sketch, "E1679", {"start": v(-509.07, 816.8) * mm, "end": v(-509.12, 816.7) * mm});
            skLineSegment(sketch, "E1680", {"start": v(-509.12, 816.7) * mm, "end": v(-509.16, 816.58) * mm});
            skLineSegment(sketch, "E1681", {"start": v(-509.16, 816.58) * mm, "end": v(-509.2, 816.47) * mm});
            skLineSegment(sketch, "E1682", {"start": v(-509.2, 816.47) * mm, "end": v(-509.26, 816.36) * mm});
            skLineSegment(sketch, "E1683", {"start": v(-509.26, 816.36) * mm, "end": v(-509.3, 816.25) * mm});
            skLineSegment(sketch, "E1684", {"start": v(-509.3, 816.25) * mm, "end": v(-509.36, 816.14) * mm});
            skLineSegment(sketch, "E1685", {"start": v(-509.36, 816.14) * mm, "end": v(-509.41, 816.03) * mm});
            skLineSegment(sketch, "E1686", {"start": v(-509.41, 816.03) * mm, "end": v(-509.46, 815.92) * mm});
            skLineSegment(sketch, "E1687", {"start": v(-509.46, 815.92) * mm, "end": v(-509.5, 815.8) * mm});
            skLineSegment(sketch, "E1688", {"start": v(-509.5, 815.8) * mm, "end": v(-509.89, 815.3) * mm});
            skLineSegment(sketch, "E1689", {"start": v(-509.89, 815.3) * mm, "end": v(-508.49, 814.17) * mm});
            skLineSegment(sketch, "E1690", {"start": v(-508.49, 814.17) * mm, "end": v(-508.07, 814.65) * mm});
            skLineSegment(sketch, "E1691", {"start": v(-508.07, 814.65) * mm, "end": v(-507.96, 814.7) * mm});
            skLineSegment(sketch, "E1692", {"start": v(-507.96, 814.7) * mm, "end": v(-507.87, 814.78) * mm});
            skLineSegment(sketch, "E1693", {"start": v(-507.87, 814.78) * mm, "end": v(-507.77, 814.86) * mm});
            skLineSegment(sketch, "E1694", {"start": v(-507.77, 814.86) * mm, "end": v(-507.68, 814.93) * mm});
            skLineSegment(sketch, "E1695", {"start": v(-507.68, 814.93) * mm, "end": v(-507.58, 815) * mm});
            skLineSegment(sketch, "E1696", {"start": v(-507.58, 815) * mm, "end": v(-507.49, 815.07) * mm});
            skLineSegment(sketch, "E1697", {"start": v(-507.49, 815.07) * mm, "end": v(-507.39, 815.14) * mm});
            skLineSegment(sketch, "E1698", {"start": v(-507.39, 815.14) * mm, "end": v(-507.28, 815.2) * mm});
            skLineSegment(sketch, "E1699", {"start": v(-507.28, 815.2) * mm, "end": v(-507.18, 815.27) * mm});
            skLineSegment(sketch, "E1700", {"start": v(-507.18, 815.27) * mm, "end": v(-507.08, 815.34) * mm});
            skLineSegment(sketch, "E1701", {"start": v(-507.08, 815.34) * mm, "end": v(-506.97, 815.4) * mm});
            skLineSegment(sketch, "E1702", {"start": v(-506.97, 815.4) * mm, "end": v(-506.87, 815.46) * mm});
            skLineSegment(sketch, "E1703", {"start": v(-506.87, 815.46) * mm, "end": v(-506.76, 815.52) * mm});
            skLineSegment(sketch, "E1704", {"start": v(-506.76, 815.52) * mm, "end": v(-506.65, 815.58) * mm});
            skLineSegment(sketch, "E1705", {"start": v(-506.65, 815.58) * mm, "end": v(-506.54, 815.64) * mm});
            skLineSegment(sketch, "E1706", {"start": v(-506.54, 815.64) * mm, "end": v(-506.43, 815.7) * mm});
            skLineSegment(sketch, "E1707", {"start": v(-506.43, 815.7) * mm, "end": v(-506.31, 815.75) * mm});
            skLineSegment(sketch, "E1708", {"start": v(-506.31, 815.75) * mm, "end": v(-506.2, 815.8) * mm});
            skLineSegment(sketch, "E1709", {"start": v(-506.2, 815.8) * mm, "end": v(-506.08, 815.86) * mm});
            skLineSegment(sketch, "E1710", {"start": v(-506.08, 815.86) * mm, "end": v(-505.97, 815.91) * mm});
            skLineSegment(sketch, "E1711", {"start": v(-505.97, 815.91) * mm, "end": v(-505.85, 815.96) * mm});
            skLineSegment(sketch, "E1712", {"start": v(-505.85, 815.96) * mm, "end": v(-505.73, 816.01) * mm});
            skLineSegment(sketch, "E1713", {"start": v(-505.73, 816.01) * mm, "end": v(-505.61, 816.06) * mm});
            skLineSegment(sketch, "E1714", {"start": v(-505.61, 816.06) * mm, "end": v(-505.5, 816.11) * mm});
            skLineSegment(sketch, "E1715", {"start": v(-505.5, 816.11) * mm, "end": v(-505.37, 816.16) * mm});
            skLineSegment(sketch, "E1716", {"start": v(-505.37, 816.16) * mm, "end": v(-505.25, 816.2) * mm});
            skLineSegment(sketch, "E1717", {"start": v(-505.25, 816.2) * mm, "end": v(-505.12, 816.25) * mm});
            skLineSegment(sketch, "E1718", {"start": v(-505.12, 816.25) * mm, "end": v(-505, 816.3) * mm});
            skLineSegment(sketch, "E1719", {"start": v(-505, 816.3) * mm, "end": v(-504.87, 816.33) * mm});
            skLineSegment(sketch, "E1720", {"start": v(-504.87, 816.33) * mm, "end": v(-504.75, 816.37) * mm});
            skLineSegment(sketch, "E1721", {"start": v(-504.75, 816.37) * mm, "end": v(-504.26, 815.9) * mm});
            skLineSegment(sketch, "E1722", {"start": v(-504.26, 815.9) * mm, "end": v(-503.8, 815.42) * mm});
            skLineSegment(sketch, "E1723", {"start": v(-503.8, 815.42) * mm, "end": v(-503.83, 815.3) * mm});
            skLineSegment(sketch, "E1724", {"start": v(-503.83, 815.3) * mm, "end": v(-503.88, 815.17) * mm});
            skLineSegment(sketch, "E1725", {"start": v(-503.88, 815.17) * mm, "end": v(-503.92, 815.04) * mm});
            skLineSegment(sketch, "E1726", {"start": v(-503.92, 815.04) * mm, "end": v(-503.96, 814.92) * mm});
            skLineSegment(sketch, "E1727", {"start": v(-503.96, 814.92) * mm, "end": v(-504, 814.8) * mm});
            skLineSegment(sketch, "E1728", {"start": v(-504, 814.8) * mm, "end": v(-504.06, 814.68) * mm});
            skLineSegment(sketch, "E1729", {"start": v(-504.06, 814.68) * mm, "end": v(-504.1, 814.55) * mm});
            skLineSegment(sketch, "E1730", {"start": v(-504.1, 814.55) * mm, "end": v(-504.15, 814.43) * mm});
            skLineSegment(sketch, "E1731", {"start": v(-504.15, 814.43) * mm, "end": v(-504.2, 814.32) * mm});
            skLineSegment(sketch, "E1732", {"start": v(-504.2, 814.32) * mm, "end": v(-504.25, 814.2) * mm});
            skLineSegment(sketch, "E1733", {"start": v(-504.25, 814.2) * mm, "end": v(-504.3, 814.08) * mm});
            skLineSegment(sketch, "E1734", {"start": v(-504.3, 814.08) * mm, "end": v(-504.36, 813.97) * mm});
            skLineSegment(sketch, "E1735", {"start": v(-504.36, 813.97) * mm, "end": v(-504.41, 813.85) * mm});
            skLineSegment(sketch, "E1736", {"start": v(-504.41, 813.85) * mm, "end": v(-504.47, 813.74) * mm});
            skLineSegment(sketch, "E1737", {"start": v(-504.47, 813.74) * mm, "end": v(-504.53, 813.63) * mm});
            skLineSegment(sketch, "E1738", {"start": v(-504.53, 813.63) * mm, "end": v(-504.59, 813.52) * mm});
            skLineSegment(sketch, "E1739", {"start": v(-504.59, 813.52) * mm, "end": v(-504.65, 813.4) * mm});
            skLineSegment(sketch, "E1740", {"start": v(-504.65, 813.4) * mm, "end": v(-504.7, 813.3) * mm});
            skLineSegment(sketch, "E1741", {"start": v(-504.7, 813.3) * mm, "end": v(-504.77, 813.2) * mm});
            skLineSegment(sketch, "E1742", {"start": v(-504.77, 813.2) * mm, "end": v(-504.83, 813.09) * mm});
            skLineSegment(sketch, "E1743", {"start": v(-504.83, 813.09) * mm, "end": v(-504.9, 812.98) * mm});
            skLineSegment(sketch, "E1744", {"start": v(-504.9, 812.98) * mm, "end": v(-504.96, 812.88) * mm});
            skLineSegment(sketch, "E1745", {"start": v(-504.96, 812.88) * mm, "end": v(-505.03, 812.78) * mm});
            skLineSegment(sketch, "E1746", {"start": v(-505.03, 812.78) * mm, "end": v(-505.1, 812.68) * mm});
            skLineSegment(sketch, "E1747", {"start": v(-505.1, 812.68) * mm, "end": v(-505.17, 812.58) * mm});
            skLineSegment(sketch, "E1748", {"start": v(-505.17, 812.58) * mm, "end": v(-505.24, 812.49) * mm});
            skLineSegment(sketch, "E1749", {"start": v(-505.24, 812.49) * mm, "end": v(-505.31, 812.4) * mm});
            skLineSegment(sketch, "E1750", {"start": v(-505.31, 812.4) * mm, "end": v(-505.38, 812.3) * mm});
            skLineSegment(sketch, "E1751", {"start": v(-505.38, 812.3) * mm, "end": v(-505.46, 812.2) * mm});
            skLineSegment(sketch, "E1752", {"start": v(-505.46, 812.2) * mm, "end": v(-505.52, 812.1) * mm});
            skLineSegment(sketch, "E1753", {"start": v(-505.52, 812.1) * mm, "end": v(-506, 811.68) * mm});
            skLineSegment(sketch, "E1754", {"start": v(-506, 811.68) * mm, "end": v(-504.87, 810.28) * mm});
            skLineSegment(sketch, "E1755", {"start": v(-504.87, 810.28) * mm, "end": v(-504.36, 810.66) * mm});
            skLineSegment(sketch, "E1756", {"start": v(-504.36, 810.66) * mm, "end": v(-504.24, 810.7) * mm});
            skLineSegment(sketch, "E1757", {"start": v(-504.24, 810.7) * mm, "end": v(-504.14, 810.76) * mm});
            skLineSegment(sketch, "E1758", {"start": v(-504.14, 810.76) * mm, "end": v(-504.03, 810.8) * mm});
            skLineSegment(sketch, "E1759", {"start": v(-504.03, 810.8) * mm, "end": v(-503.92, 810.86) * mm});
            skLineSegment(sketch, "E1760", {"start": v(-503.92, 810.86) * mm, "end": v(-503.81, 810.9) * mm});
            skLineSegment(sketch, "E1761", {"start": v(-503.81, 810.9) * mm, "end": v(-503.7, 810.96) * mm});
            skLineSegment(sketch, "E1762", {"start": v(-503.7, 810.96) * mm, "end": v(-503.59, 811) * mm});
            skLineSegment(sketch, "E1763", {"start": v(-503.59, 811) * mm, "end": v(-503.47, 811.05) * mm});
            skLineSegment(sketch, "E1764", {"start": v(-503.47, 811.05) * mm, "end": v(-503.36, 811.1) * mm});
            skLineSegment(sketch, "E1765", {"start": v(-503.36, 811.1) * mm, "end": v(-503.25, 811.13) * mm});
            skLineSegment(sketch, "E1766", {"start": v(-503.25, 811.13) * mm, "end": v(-503.13, 811.17) * mm});
            skLineSegment(sketch, "E1767", {"start": v(-503.13, 811.17) * mm, "end": v(-503.01, 811.2) * mm});
            skLineSegment(sketch, "E1768", {"start": v(-503.01, 811.2) * mm, "end": v(-502.9, 811.25) * mm});
            skLineSegment(sketch, "E1769", {"start": v(-502.9, 811.25) * mm, "end": v(-502.78, 811.28) * mm});
            skLineSegment(sketch, "E1770", {"start": v(-502.78, 811.28) * mm, "end": v(-502.66, 811.32) * mm});
            skLineSegment(sketch, "E1771", {"start": v(-502.66, 811.32) * mm, "end": v(-502.53, 811.35) * mm});
            skLineSegment(sketch, "E1772", {"start": v(-502.53, 811.35) * mm, "end": v(-502.41, 811.38) * mm});
            skLineSegment(sketch, "E1773", {"start": v(-502.41, 811.38) * mm, "end": v(-502.29, 811.41) * mm});
            skLineSegment(sketch, "E1774", {"start": v(-502.29, 811.41) * mm, "end": v(-502.17, 811.44) * mm});
            skLineSegment(sketch, "E1775", {"start": v(-502.17, 811.44) * mm, "end": v(-502.04, 811.47) * mm});
            skLineSegment(sketch, "E1776", {"start": v(-502.04, 811.47) * mm, "end": v(-501.92, 811.5) * mm});
            skLineSegment(sketch, "E1777", {"start": v(-501.92, 811.5) * mm, "end": v(-501.79, 811.52) * mm});
            skLineSegment(sketch, "E1778", {"start": v(-501.79, 811.52) * mm, "end": v(-501.66, 811.54) * mm});
            skLineSegment(sketch, "E1779", {"start": v(-501.66, 811.54) * mm, "end": v(-501.53, 811.56) * mm});
            skLineSegment(sketch, "E1780", {"start": v(-501.53, 811.56) * mm, "end": v(-501.4, 811.58) * mm});
            skLineSegment(sketch, "E1781", {"start": v(-501.4, 811.58) * mm, "end": v(-501.28, 811.6) * mm});
            skLineSegment(sketch, "E1782", {"start": v(-501.28, 811.6) * mm, "end": v(-501.15, 811.62) * mm});
            skLineSegment(sketch, "E1783", {"start": v(-501.15, 811.62) * mm, "end": v(-501.01, 811.63) * mm});
            skLineSegment(sketch, "E1784", {"start": v(-501.01, 811.63) * mm, "end": v(-500.88, 811.65) * mm});
            skLineSegment(sketch, "E1785", {"start": v(-500.88, 811.65) * mm, "end": v(-500.75, 811.66) * mm});
            skLineSegment(sketch, "E1786", {"start": v(-500.75, 811.66) * mm, "end": v(-500.37, 811.1) * mm});
            skLineSegment(sketch, "E1787", {"start": v(-500.37, 811.1) * mm, "end": v(-500.02, 810.53) * mm});
            skLineSegment(sketch, "E1788", {"start": v(-500.02, 810.53) * mm, "end": v(-500.08, 810.42) * mm});
            skLineSegment(sketch, "E1789", {"start": v(-500.08, 810.42) * mm, "end": v(-500.15, 810.3) * mm});
            skLineSegment(sketch, "E1790", {"start": v(-500.15, 810.3) * mm, "end": v(-500.22, 810.19) * mm});
            skLineSegment(sketch, "E1791", {"start": v(-500.22, 810.19) * mm, "end": v(-500.29, 810.08) * mm});
            skLineSegment(sketch, "E1792", {"start": v(-500.29, 810.08) * mm, "end": v(-500.36, 809.97) * mm});
            skLineSegment(sketch, "E1793", {"start": v(-500.36, 809.97) * mm, "end": v(-500.43, 809.86) * mm});
            skLineSegment(sketch, "E1794", {"start": v(-500.43, 809.86) * mm, "end": v(-500.5, 809.75) * mm});
            skLineSegment(sketch, "E1795", {"start": v(-500.5, 809.75) * mm, "end": v(-500.57, 809.64) * mm});
            skLineSegment(sketch, "E1796", {"start": v(-500.57, 809.64) * mm, "end": v(-500.65, 809.54) * mm});
            skLineSegment(sketch, "E1797", {"start": v(-500.65, 809.54) * mm, "end": v(-500.72, 809.43) * mm});
            skLineSegment(sketch, "E1798", {"start": v(-500.72, 809.43) * mm, "end": v(-500.8, 809.33) * mm});
            skLineSegment(sketch, "E1799", {"start": v(-500.8, 809.33) * mm, "end": v(-500.87, 809.23) * mm});
            skLineSegment(sketch, "E1800", {"start": v(-500.87, 809.23) * mm, "end": v(-500.95, 809.13) * mm});
            skLineSegment(sketch, "E1801", {"start": v(-500.95, 809.13) * mm, "end": v(-501.03, 809.03) * mm});
            skLineSegment(sketch, "E1802", {"start": v(-501.03, 809.03) * mm, "end": v(-501.1, 808.93) * mm});
            skLineSegment(sketch, "E1803", {"start": v(-501.1, 808.93) * mm, "end": v(-501.19, 808.84) * mm});
            skLineSegment(sketch, "E1804", {"start": v(-501.19, 808.84) * mm, "end": v(-501.27, 808.74) * mm});
            skLineSegment(sketch, "E1805", {"start": v(-501.27, 808.74) * mm, "end": v(-501.35, 808.65) * mm});
            skLineSegment(sketch, "E1806", {"start": v(-501.35, 808.65) * mm, "end": v(-501.43, 808.56) * mm});
            skLineSegment(sketch, "E1807", {"start": v(-501.43, 808.56) * mm, "end": v(-501.52, 808.47) * mm});
            skLineSegment(sketch, "E1808", {"start": v(-501.52, 808.47) * mm, "end": v(-501.6, 808.38) * mm});
            skLineSegment(sketch, "E1809", {"start": v(-501.6, 808.38) * mm, "end": v(-501.69, 808.3) * mm});
            skLineSegment(sketch, "E1810", {"start": v(-501.69, 808.3) * mm, "end": v(-501.77, 808.2) * mm});
            skLineSegment(sketch, "E1811", {"start": v(-501.77, 808.2) * mm, "end": v(-501.86, 808.12) * mm});
            skLineSegment(sketch, "E1812", {"start": v(-501.86, 808.12) * mm, "end": v(-501.95, 808.04) * mm});
            skLineSegment(sketch, "E1813", {"start": v(-501.95, 808.04) * mm, "end": v(-502.04, 807.96) * mm});
            skLineSegment(sketch, "E1814", {"start": v(-502.04, 807.96) * mm, "end": v(-502.13, 807.89) * mm});
            skLineSegment(sketch, "E1815", {"start": v(-502.13, 807.89) * mm, "end": v(-502.22, 807.8) * mm});
            skLineSegment(sketch, "E1816", {"start": v(-502.22, 807.8) * mm, "end": v(-502.31, 807.73) * mm});
            skLineSegment(sketch, "E1817", {"start": v(-502.31, 807.73) * mm, "end": v(-502.4, 807.64) * mm});
            skLineSegment(sketch, "E1818", {"start": v(-502.4, 807.64) * mm, "end": v(-502.95, 807.33) * mm});
            skLineSegment(sketch, "E1819", {"start": v(-502.95, 807.33) * mm, "end": v(-502.14, 805.73) * mm});
            skLineSegment(sketch, "E1820", {"start": v(-502.14, 805.73) * mm, "end": v(-501.56, 806) * mm});
            skLineSegment(sketch, "E1821", {"start": v(-501.56, 806) * mm, "end": v(-501.44, 806.01) * mm});
            skLineSegment(sketch, "E1822", {"start": v(-501.44, 806.01) * mm, "end": v(-501.32, 806.04) * mm});
            skLineSegment(sketch, "E1823", {"start": v(-501.32, 806.04) * mm, "end": v(-501.2, 806.07) * mm});
            skLineSegment(sketch, "E1824", {"start": v(-501.2, 806.07) * mm, "end": v(-501.09, 806.1) * mm});
            skLineSegment(sketch, "E1825", {"start": v(-501.09, 806.1) * mm, "end": v(-500.97, 806.12) * mm});
            skLineSegment(sketch, "E1826", {"start": v(-500.97, 806.12) * mm, "end": v(-500.85, 806.15) * mm});
            skLineSegment(sketch, "E1827", {"start": v(-500.85, 806.15) * mm, "end": v(-500.73, 806.17) * mm});
            skLineSegment(sketch, "E1828", {"start": v(-500.73, 806.17) * mm, "end": v(-500.62, 806.19) * mm});
            skLineSegment(sketch, "E1829", {"start": v(-500.62, 806.19) * mm, "end": v(-500.5, 806.2) * mm});
            skLineSegment(sketch, "E1830", {"start": v(-500.5, 806.2) * mm, "end": v(-500.37, 806.22) * mm});
            skLineSegment(sketch, "E1831", {"start": v(-500.37, 806.22) * mm, "end": v(-500.25, 806.24) * mm});
            skLineSegment(sketch, "E1832", {"start": v(-500.25, 806.24) * mm, "end": v(-500.13, 806.25) * mm});
            skLineSegment(sketch, "E1833", {"start": v(-500.13, 806.25) * mm, "end": v(-500, 806.26) * mm});
            skLineSegment(sketch, "E1834", {"start": v(-500, 806.26) * mm, "end": v(-499.88, 806.27) * mm});
            skLineSegment(sketch, "E1835", {"start": v(-499.88, 806.27) * mm, "end": v(-499.76, 806.28) * mm});
            skLineSegment(sketch, "E1836", {"start": v(-499.76, 806.28) * mm, "end": v(-499.63, 806.29) * mm});
            skLineSegment(sketch, "E1837", {"start": v(-499.63, 806.29) * mm, "end": v(-499.5, 806.3) * mm});
            skLineSegment(sketch, "E1838", {"start": v(-499.5, 806.3) * mm, "end": v(-499.38, 806.3) * mm});
            skLineSegment(sketch, "E1839", {"start": v(-499.38, 806.3) * mm, "end": v(-499.25, 806.3) * mm});
            skLineSegment(sketch, "E1840", {"start": v(-499.25, 806.3) * mm, "end": v(-499.12, 806.3) * mm});
            skLineSegment(sketch, "E1841", {"start": v(-499.12, 806.3) * mm, "end": v(-499, 806.3) * mm});
            skLineSegment(sketch, "E1842", {"start": v(-499, 806.3) * mm, "end": v(-498.87, 806.3) * mm});
            skLineSegment(sketch, "E1843", {"start": v(-498.87, 806.3) * mm, "end": v(-498.74, 806.3) * mm});
            skLineSegment(sketch, "E1844", {"start": v(-498.74, 806.3) * mm, "end": v(-498.6, 806.29) * mm});
            skLineSegment(sketch, "E1845", {"start": v(-498.6, 806.29) * mm, "end": v(-498.48, 806.28) * mm});
            skLineSegment(sketch, "E1846", {"start": v(-498.48, 806.28) * mm, "end": v(-498.35, 806.27) * mm});
            skLineSegment(sketch, "E1847", {"start": v(-498.35, 806.27) * mm, "end": v(-498.22, 806.26) * mm});
            skLineSegment(sketch, "E1848", {"start": v(-498.22, 806.26) * mm, "end": v(-498.08, 806.25) * mm});
            skLineSegment(sketch, "E1849", {"start": v(-498.08, 806.25) * mm, "end": v(-497.95, 806.24) * mm});
            skLineSegment(sketch, "E1850", {"start": v(-497.95, 806.24) * mm, "end": v(-497.82, 806.22) * mm});
            skLineSegment(sketch, "E1851", {"start": v(-497.82, 806.22) * mm, "end": v(-497.57, 805.6) * mm});
            skLineSegment(sketch, "E1852", {"start": v(-497.57, 805.6) * mm, "end": v(-497.34, 804.97) * mm});
            skLineSegment(sketch, "E1853", {"start": v(-497.34, 804.97) * mm, "end": v(-497.43, 804.87) * mm});
            skLineSegment(sketch, "E1854", {"start": v(-497.43, 804.87) * mm, "end": v(-497.52, 804.77) * mm});
            skLineSegment(sketch, "E1855", {"start": v(-497.52, 804.77) * mm, "end": v(-497.6, 804.67) * mm});
            skLineSegment(sketch, "E1856", {"start": v(-497.6, 804.67) * mm, "end": v(-497.7, 804.58) * mm});
            skLineSegment(sketch, "E1857", {"start": v(-497.7, 804.58) * mm, "end": v(-497.79, 804.48) * mm});
            skLineSegment(sketch, "E1858", {"start": v(-497.79, 804.48) * mm, "end": v(-497.88, 804.4) * mm});
            skLineSegment(sketch, "E1859", {"start": v(-497.88, 804.4) * mm, "end": v(-497.97, 804.3) * mm});
            skLineSegment(sketch, "E1860", {"start": v(-497.97, 804.3) * mm, "end": v(-498.07, 804.21) * mm});
            skLineSegment(sketch, "E1861", {"start": v(-498.07, 804.21) * mm, "end": v(-498.16, 804.12) * mm});
            skLineSegment(sketch, "E1862", {"start": v(-498.16, 804.12) * mm, "end": v(-498.26, 804.04) * mm});
            skLineSegment(sketch, "E1863", {"start": v(-498.26, 804.04) * mm, "end": v(-498.35, 803.95) * mm});
            skLineSegment(sketch, "E1864", {"start": v(-498.35, 803.95) * mm, "end": v(-498.45, 803.87) * mm});
            skLineSegment(sketch, "E1865", {"start": v(-498.45, 803.87) * mm, "end": v(-498.54, 803.79) * mm});
            skLineSegment(sketch, "E1866", {"start": v(-498.54, 803.79) * mm, "end": v(-498.64, 803.7) * mm});
            skLineSegment(sketch, "E1867", {"start": v(-498.64, 803.7) * mm, "end": v(-498.74, 803.63) * mm});
            skLineSegment(sketch, "E1868", {"start": v(-498.74, 803.63) * mm, "end": v(-498.83, 803.55) * mm});
            skLineSegment(sketch, "E1869", {"start": v(-498.83, 803.55) * mm, "end": v(-498.93, 803.47) * mm});
            skLineSegment(sketch, "E1870", {"start": v(-498.93, 803.47) * mm, "end": v(-499.03, 803.4) * mm});
            skLineSegment(sketch, "E1871", {"start": v(-499.03, 803.4) * mm, "end": v(-499.13, 803.33) * mm});
            skLineSegment(sketch, "E1872", {"start": v(-499.13, 803.33) * mm, "end": v(-499.23, 803.26) * mm});
            skLineSegment(sketch, "E1873", {"start": v(-499.23, 803.26) * mm, "end": v(-499.34, 803.19) * mm});
            skLineSegment(sketch, "E1874", {"start": v(-499.34, 803.19) * mm, "end": v(-499.44, 803.12) * mm});
            skLineSegment(sketch, "E1875", {"start": v(-499.44, 803.12) * mm, "end": v(-499.54, 803.06) * mm});
            skLineSegment(sketch, "E1876", {"start": v(-499.54, 803.06) * mm, "end": v(-499.64, 803) * mm});
            skLineSegment(sketch, "E1877", {"start": v(-499.64, 803) * mm, "end": v(-499.75, 802.93) * mm});
            skLineSegment(sketch, "E1878", {"start": v(-499.75, 802.93) * mm, "end": v(-499.85, 802.87) * mm});
            skLineSegment(sketch, "E1879", {"start": v(-499.85, 802.87) * mm, "end": v(-499.95, 802.82) * mm});
            skLineSegment(sketch, "E1880", {"start": v(-499.95, 802.82) * mm, "end": v(-500.06, 802.76) * mm});
            skLineSegment(sketch, "E1881", {"start": v(-500.06, 802.76) * mm, "end": v(-500.17, 802.7) * mm});
            skLineSegment(sketch, "E1882", {"start": v(-500.17, 802.7) * mm, "end": v(-500.27, 802.63) * mm});
            skLineSegment(sketch, "E1883", {"start": v(-500.27, 802.63) * mm, "end": v(-500.88, 802.45) * mm});
            skLineSegment(sketch, "E1884", {"start": v(-500.88, 802.45) * mm, "end": v(-500.41, 800.7) * mm});
            skLineSegment(sketch, "E1885", {"start": v(-500.41, 800.7) * mm, "end": v(-499.8, 800.85) * mm});
            skLineSegment(sketch, "E1886", {"start": v(-499.8, 800.85) * mm, "end": v(-499.67, 800.84) * mm});
            skLineSegment(sketch, "E1887", {"start": v(-499.67, 800.84) * mm, "end": v(-499.55, 800.84) * mm});
            skLineSegment(sketch, "E1888", {"start": v(-499.55, 800.84) * mm, "end": v(-499.43, 800.85) * mm});
            skLineSegment(sketch, "E1889", {"start": v(-499.43, 800.85) * mm, "end": v(-499.3, 800.85) * mm});
            skLineSegment(sketch, "E1890", {"start": v(-499.3, 800.85) * mm, "end": v(-499.19, 800.85) * mm});
            skLineSegment(sketch, "E1891", {"start": v(-499.19, 800.85) * mm, "end": v(-499.07, 800.85) * mm});
            skLineSegment(sketch, "E1892", {"start": v(-499.07, 800.85) * mm, "end": v(-498.95, 800.85) * mm});
            skLineSegment(sketch, "E1893", {"start": v(-498.95, 800.85) * mm, "end": v(-498.83, 800.84) * mm});
            skLineSegment(sketch, "E1894", {"start": v(-498.83, 800.84) * mm, "end": v(-498.7, 800.84) * mm});
            skLineSegment(sketch, "E1895", {"start": v(-498.7, 800.84) * mm, "end": v(-498.58, 800.83) * mm});
            skLineSegment(sketch, "E1896", {"start": v(-498.58, 800.83) * mm, "end": v(-498.46, 800.82) * mm});
            skLineSegment(sketch, "E1897", {"start": v(-498.46, 800.82) * mm, "end": v(-498.34, 800.8) * mm});
            skLineSegment(sketch, "E1898", {"start": v(-498.34, 800.8) * mm, "end": v(-498.22, 800.79) * mm});
            skLineSegment(sketch, "E1899", {"start": v(-498.22, 800.79) * mm, "end": v(-498.1, 800.77) * mm});
            skLineSegment(sketch, "E1900", {"start": v(-498.1, 800.77) * mm, "end": v(-497.97, 800.75) * mm});
            skLineSegment(sketch, "E1901", {"start": v(-497.97, 800.75) * mm, "end": v(-497.84, 800.74) * mm});
            skLineSegment(sketch, "E1902", {"start": v(-497.84, 800.74) * mm, "end": v(-497.72, 800.71) * mm});
            skLineSegment(sketch, "E1903", {"start": v(-497.72, 800.71) * mm, "end": v(-497.6, 800.7) * mm});
            skLineSegment(sketch, "E1904", {"start": v(-497.6, 800.7) * mm, "end": v(-497.47, 800.67) * mm});
            skLineSegment(sketch, "E1905", {"start": v(-497.47, 800.67) * mm, "end": v(-497.35, 800.64) * mm});
            skLineSegment(sketch, "E1906", {"start": v(-497.35, 800.64) * mm, "end": v(-497.22, 800.61) * mm});
            skLineSegment(sketch, "E1907", {"start": v(-497.22, 800.61) * mm, "end": v(-497.1, 800.58) * mm});
            skLineSegment(sketch, "E1908", {"start": v(-497.1, 800.58) * mm, "end": v(-496.97, 800.55) * mm});
            skLineSegment(sketch, "E1909", {"start": v(-496.97, 800.55) * mm, "end": v(-496.84, 800.52) * mm});
            skLineSegment(sketch, "E1910", {"start": v(-496.84, 800.52) * mm, "end": v(-496.72, 800.49) * mm});
            skLineSegment(sketch, "E1911", {"start": v(-496.72, 800.49) * mm, "end": v(-496.6, 800.45) * mm});
            skLineSegment(sketch, "E1912", {"start": v(-496.6, 800.45) * mm, "end": v(-496.47, 800.41) * mm});
            skLineSegment(sketch, "E1913", {"start": v(-496.47, 800.41) * mm, "end": v(-496.34, 800.38) * mm});
            skLineSegment(sketch, "E1914", {"start": v(-496.34, 800.38) * mm, "end": v(-496.21, 800.34) * mm});
            skLineSegment(sketch, "E1915", {"start": v(-496.21, 800.34) * mm, "end": v(-496.08, 800.3) * mm});
            skLineSegment(sketch, "E1916", {"start": v(-496.08, 800.3) * mm, "end": v(-495.97, 799.63) * mm});
            skLineSegment(sketch, "E1917", {"start": v(-495.97, 799.63) * mm, "end": v(-495.87, 798.96) * mm});
            skLineSegment(sketch, "E1918", {"start": v(-495.87, 798.96) * mm, "end": v(-495.98, 798.88) * mm});
            skLineSegment(sketch, "E1919", {"start": v(-495.98, 798.88) * mm, "end": v(-496.1, 798.8) * mm});
            skLineSegment(sketch, "E1920", {"start": v(-496.1, 798.8) * mm, "end": v(-496.2, 798.73) * mm});
            skLineSegment(sketch, "E1921", {"start": v(-496.2, 798.73) * mm, "end": v(-496.3, 798.66) * mm});
            skLineSegment(sketch, "E1922", {"start": v(-496.3, 798.66) * mm, "end": v(-496.42, 798.59) * mm});
            skLineSegment(sketch, "E1923", {"start": v(-496.42, 798.59) * mm, "end": v(-496.53, 798.52) * mm});
            skLineSegment(sketch, "E1924", {"start": v(-496.53, 798.52) * mm, "end": v(-496.64, 798.44) * mm});
            skLineSegment(sketch, "E1925", {"start": v(-496.64, 798.44) * mm, "end": v(-496.75, 798.38) * mm});
            skLineSegment(sketch, "E1926", {"start": v(-496.75, 798.38) * mm, "end": v(-496.85, 798.3) * mm});
            skLineSegment(sketch, "E1927", {"start": v(-496.85, 798.3) * mm, "end": v(-496.97, 798.25) * mm});
            skLineSegment(sketch, "E1928", {"start": v(-496.97, 798.25) * mm, "end": v(-497.08, 798.18) * mm});
            skLineSegment(sketch, "E1929", {"start": v(-497.08, 798.18) * mm, "end": v(-497.19, 798.12) * mm});
            skLineSegment(sketch, "E1930", {"start": v(-497.19, 798.12) * mm, "end": v(-497.3, 798.06) * mm});
            skLineSegment(sketch, "E1931", {"start": v(-497.3, 798.06) * mm, "end": v(-497.4, 798) * mm});
            skLineSegment(sketch, "E1932", {"start": v(-497.4, 798) * mm, "end": v(-497.52, 797.95) * mm});
            skLineSegment(sketch, "E1933", {"start": v(-497.52, 797.95) * mm, "end": v(-497.63, 797.89) * mm});
            skLineSegment(sketch, "E1934", {"start": v(-497.63, 797.89) * mm, "end": v(-497.75, 797.84) * mm});
            skLineSegment(sketch, "E1935", {"start": v(-497.75, 797.84) * mm, "end": v(-497.86, 797.79) * mm});
            skLineSegment(sketch, "E1936", {"start": v(-497.86, 797.79) * mm, "end": v(-497.97, 797.74) * mm});
            skLineSegment(sketch, "E1937", {"start": v(-497.97, 797.74) * mm, "end": v(-498.09, 797.69) * mm});
            skLineSegment(sketch, "E1938", {"start": v(-498.09, 797.69) * mm, "end": v(-498.2, 797.64) * mm});
            skLineSegment(sketch, "E1939", {"start": v(-498.2, 797.64) * mm, "end": v(-498.31, 797.6) * mm});
            skLineSegment(sketch, "E1940", {"start": v(-498.31, 797.6) * mm, "end": v(-498.43, 797.55) * mm});
            skLineSegment(sketch, "E1941", {"start": v(-498.43, 797.55) * mm, "end": v(-498.54, 797.51) * mm});
            skLineSegment(sketch, "E1942", {"start": v(-498.54, 797.51) * mm, "end": v(-498.65, 797.48) * mm});
            skLineSegment(sketch, "E1943", {"start": v(-498.65, 797.48) * mm, "end": v(-498.77, 797.44) * mm});
            skLineSegment(sketch, "E1944", {"start": v(-498.77, 797.44) * mm, "end": v(-498.88, 797.4) * mm});
            skLineSegment(sketch, "E1945", {"start": v(-498.88, 797.4) * mm, "end": v(-499, 797.37) * mm});
            skLineSegment(sketch, "E1946", {"start": v(-499, 797.37) * mm, "end": v(-499.11, 797.34) * mm});
            skLineSegment(sketch, "E1947", {"start": v(-499.11, 797.34) * mm, "end": v(-499.23, 797.29) * mm});
            skLineSegment(sketch, "E1948", {"start": v(-499.23, 797.29) * mm, "end": v(-499.86, 797.23) * mm});
            skLineSegment(sketch, "E1949", {"start": v(-499.86, 797.23) * mm, "end": v(-499.77, 795.44) * mm});
            skLineSegment(sketch, "E1950", {"start": v(-499.77, 795.44) * mm, "end": v(-499.13, 795.45) * mm});
            skLineSegment(sketch, "E1951", {"start": v(-520.54, 795) * mm, "end": v(-520.54, 794.89) * mm});
            skLineSegment(sketch, "E1952", {"start": v(-520.54, 794.89) * mm, "end": v(-520.55, 794.65) * mm});
            skLineSegment(sketch, "E1953", {"start": v(-520.55, 794.65) * mm, "end": v(-520.58, 794.42) * mm});
            skLineSegment(sketch, "E1954", {"start": v(-520.58, 794.42) * mm, "end": v(-520.61, 794.19) * mm});
            skLineSegment(sketch, "E1955", {"start": v(-520.61, 794.19) * mm, "end": v(-520.66, 793.96) * mm});
            skLineSegment(sketch, "E1956", {"start": v(-520.66, 793.96) * mm, "end": v(-520.72, 793.74) * mm});
            skLineSegment(sketch, "E1957", {"start": v(-520.72, 793.74) * mm, "end": v(-520.78, 793.53) * mm});
            skLineSegment(sketch, "E1958", {"start": v(-520.78, 793.53) * mm, "end": v(-520.86, 793.31) * mm});
            skLineSegment(sketch, "E1959", {"start": v(-520.86, 793.31) * mm, "end": v(-520.95, 793.1) * mm});
            skLineSegment(sketch, "E1960", {"start": v(-520.95, 793.1) * mm, "end": v(-521.05, 792.9) * mm});
            skLineSegment(sketch, "E1961", {"start": v(-521.05, 792.9) * mm, "end": v(-521.15, 792.71) * mm});
            skLineSegment(sketch, "E1962", {"start": v(-521.15, 792.71) * mm, "end": v(-521.27, 792.52) * mm});
            skLineSegment(sketch, "E1963", {"start": v(-521.27, 792.52) * mm, "end": v(-521.4, 792.33) * mm});
            skLineSegment(sketch, "E1964", {"start": v(-521.4, 792.33) * mm, "end": v(-521.52, 792.16) * mm});
            skLineSegment(sketch, "E1965", {"start": v(-521.52, 792.16) * mm, "end": v(-521.67, 791.99) * mm});
            skLineSegment(sketch, "E1966", {"start": v(-521.67, 791.99) * mm, "end": v(-521.82, 791.82) * mm});
            skLineSegment(sketch, "E1967", {"start": v(-521.82, 791.82) * mm, "end": v(-521.97, 791.67) * mm});
            skLineSegment(sketch, "E1968", {"start": v(-521.97, 791.67) * mm, "end": v(-522.14, 791.52) * mm});
            skLineSegment(sketch, "E1969", {"start": v(-522.14, 791.52) * mm, "end": v(-522.3, 791.38) * mm});
            skLineSegment(sketch, "E1970", {"start": v(-522.3, 791.38) * mm, "end": v(-522.48, 791.24) * mm});
            skLineSegment(sketch, "E1971", {"start": v(-522.48, 791.24) * mm, "end": v(-522.67, 791.12) * mm});
            skLineSegment(sketch, "E1972", {"start": v(-522.67, 791.12) * mm, "end": v(-522.86, 791) * mm});
            skLineSegment(sketch, "E1973", {"start": v(-522.86, 791) * mm, "end": v(-523.06, 790.9) * mm});
            skLineSegment(sketch, "E1974", {"start": v(-523.06, 790.9) * mm, "end": v(-523.26, 790.8) * mm});
            skLineSegment(sketch, "E1975", {"start": v(-523.26, 790.8) * mm, "end": v(-523.47, 790.71) * mm});
            skLineSegment(sketch, "E1976", {"start": v(-523.47, 790.71) * mm, "end": v(-523.68, 790.63) * mm});
            skLineSegment(sketch, "E1977", {"start": v(-523.68, 790.63) * mm, "end": v(-523.9, 790.57) * mm});
            skLineSegment(sketch, "E1978", {"start": v(-523.9, 790.57) * mm, "end": v(-524.11, 790.5) * mm});
            skLineSegment(sketch, "E1979", {"start": v(-524.11, 790.5) * mm, "end": v(-524.34, 790.46) * mm});
            skLineSegment(sketch, "E1980", {"start": v(-524.34, 790.46) * mm, "end": v(-524.57, 790.43) * mm});
            skLineSegment(sketch, "E1981", {"start": v(-524.57, 790.43) * mm, "end": v(-524.8, 790.4) * mm});
            skLineSegment(sketch, "E1982", {"start": v(-524.8, 790.4) * mm, "end": v(-525.04, 790.4) * mm});
            skLineSegment(sketch, "E1983", {"start": v(-525.04, 790.4) * mm, "end": v(-525.16, 790.4) * mm});
            skLineSegment(sketch, "E1984", {"start": v(-525.16, 790.4) * mm, "end": v(-525.28, 790.4) * mm});
            skLineSegment(sketch, "E1985", {"start": v(-525.28, 790.4) * mm, "end": v(-525.51, 790.4) * mm});
            skLineSegment(sketch, "E1986", {"start": v(-525.51, 790.4) * mm, "end": v(-525.75, 790.43) * mm});
            skLineSegment(sketch, "E1987", {"start": v(-525.75, 790.43) * mm, "end": v(-525.98, 790.46) * mm});
            skLineSegment(sketch, "E1988", {"start": v(-525.98, 790.46) * mm, "end": v(-526.2, 790.5) * mm});
            skLineSegment(sketch, "E1989", {"start": v(-526.2, 790.5) * mm, "end": v(-526.42, 790.57) * mm});
            skLineSegment(sketch, "E1990", {"start": v(-526.42, 790.57) * mm, "end": v(-526.64, 790.63) * mm});
            skLineSegment(sketch, "E1991", {"start": v(-526.64, 790.63) * mm, "end": v(-526.85, 790.71) * mm});
            skLineSegment(sketch, "E1992", {"start": v(-526.85, 790.71) * mm, "end": v(-527.06, 790.8) * mm});
            skLineSegment(sketch, "E1993", {"start": v(-527.06, 790.8) * mm, "end": v(-527.26, 790.9) * mm});
            skLineSegment(sketch, "E1994", {"start": v(-527.26, 790.9) * mm, "end": v(-527.46, 791) * mm});
            skLineSegment(sketch, "E1995", {"start": v(-527.46, 791) * mm, "end": v(-527.65, 791.12) * mm});
            skLineSegment(sketch, "E1996", {"start": v(-527.65, 791.12) * mm, "end": v(-527.83, 791.24) * mm});
            skLineSegment(sketch, "E1997", {"start": v(-527.83, 791.24) * mm, "end": v(-528, 791.38) * mm});
            skLineSegment(sketch, "E1998", {"start": v(-528, 791.38) * mm, "end": v(-528.18, 791.52) * mm});
            skLineSegment(sketch, "E1999", {"start": v(-528.18, 791.52) * mm, "end": v(-528.34, 791.67) * mm});
            skLineSegment(sketch, "E2000", {"start": v(-528.34, 791.67) * mm, "end": v(-528.5, 791.82) * mm});
            skLineSegment(sketch, "E2001", {"start": v(-528.5, 791.82) * mm, "end": v(-528.65, 791.99) * mm});
            skLineSegment(sketch, "E2002", {"start": v(-528.65, 791.99) * mm, "end": v(-528.8, 792.16) * mm});
            skLineSegment(sketch, "E2003", {"start": v(-528.8, 792.16) * mm, "end": v(-528.92, 792.33) * mm});
            skLineSegment(sketch, "E2004", {"start": v(-528.92, 792.33) * mm, "end": v(-529.05, 792.52) * mm});
            skLineSegment(sketch, "E2005", {"start": v(-529.05, 792.52) * mm, "end": v(-529.16, 792.71) * mm});
            skLineSegment(sketch, "E2006", {"start": v(-529.16, 792.71) * mm, "end": v(-529.27, 792.9) * mm});
            skLineSegment(sketch, "E2007", {"start": v(-529.27, 792.9) * mm, "end": v(-529.37, 793.1) * mm});
            skLineSegment(sketch, "E2008", {"start": v(-529.37, 793.1) * mm, "end": v(-529.46, 793.31) * mm});
            skLineSegment(sketch, "E2009", {"start": v(-529.46, 793.31) * mm, "end": v(-529.53, 793.53) * mm});
            skLineSegment(sketch, "E2010", {"start": v(-529.53, 793.53) * mm, "end": v(-529.6, 793.74) * mm});
            skLineSegment(sketch, "E2011", {"start": v(-529.6, 793.74) * mm, "end": v(-529.66, 793.96) * mm});
            skLineSegment(sketch, "E2012", {"start": v(-529.66, 793.96) * mm, "end": v(-529.7, 794.19) * mm});
            skLineSegment(sketch, "E2013", {"start": v(-529.7, 794.19) * mm, "end": v(-529.74, 794.42) * mm});
            skLineSegment(sketch, "E2014", {"start": v(-529.74, 794.42) * mm, "end": v(-529.76, 794.65) * mm});
            skLineSegment(sketch, "E2015", {"start": v(-529.76, 794.65) * mm, "end": v(-529.78, 794.89) * mm});
            skLineSegment(sketch, "E2016", {"start": v(-529.78, 794.89) * mm, "end": v(-529.78, 795) * mm});
            skLineSegment(sketch, "E2017", {"start": v(-529.78, 795) * mm, "end": v(-529.78, 795.13) * mm});
            skLineSegment(sketch, "E2018", {"start": v(-529.78, 795.13) * mm, "end": v(-529.76, 795.36) * mm});
            skLineSegment(sketch, "E2019", {"start": v(-529.76, 795.36) * mm, "end": v(-529.74, 795.6) * mm});
            skLineSegment(sketch, "E2020", {"start": v(-529.74, 795.6) * mm, "end": v(-529.7, 795.83) * mm});
            skLineSegment(sketch, "E2021", {"start": v(-529.7, 795.83) * mm, "end": v(-529.66, 796.05) * mm});
            skLineSegment(sketch, "E2022", {"start": v(-529.66, 796.05) * mm, "end": v(-529.6, 796.27) * mm});
            skLineSegment(sketch, "E2023", {"start": v(-529.6, 796.27) * mm, "end": v(-529.53, 796.49) * mm});
            skLineSegment(sketch, "E2024", {"start": v(-529.53, 796.49) * mm, "end": v(-529.46, 796.7) * mm});
            skLineSegment(sketch, "E2025", {"start": v(-529.46, 796.7) * mm, "end": v(-529.37, 796.9) * mm});
            skLineSegment(sketch, "E2026", {"start": v(-529.37, 796.9) * mm, "end": v(-529.27, 797.1) * mm});
            skLineSegment(sketch, "E2027", {"start": v(-529.27, 797.1) * mm, "end": v(-529.16, 797.3) * mm});
            skLineSegment(sketch, "E2028", {"start": v(-529.16, 797.3) * mm, "end": v(-529.05, 797.5) * mm});
            skLineSegment(sketch, "E2029", {"start": v(-529.05, 797.5) * mm, "end": v(-528.92, 797.68) * mm});
            skLineSegment(sketch, "E2030", {"start": v(-528.92, 797.68) * mm, "end": v(-528.8, 797.86) * mm});
            skLineSegment(sketch, "E2031", {"start": v(-528.8, 797.86) * mm, "end": v(-528.65, 798.03) * mm});
            skLineSegment(sketch, "E2032", {"start": v(-528.65, 798.03) * mm, "end": v(-528.5, 798.2) * mm});
            skLineSegment(sketch, "E2033", {"start": v(-528.5, 798.2) * mm, "end": v(-528.34, 798.35) * mm});
            skLineSegment(sketch, "E2034", {"start": v(-528.34, 798.35) * mm, "end": v(-528.18, 798.5) * mm});
            skLineSegment(sketch, "E2035", {"start": v(-528.18, 798.5) * mm, "end": v(-528, 798.64) * mm});
            skLineSegment(sketch, "E2036", {"start": v(-528, 798.64) * mm, "end": v(-527.83, 798.77) * mm});
            skLineSegment(sketch, "E2037", {"start": v(-527.83, 798.77) * mm, "end": v(-527.65, 798.9) * mm});
            skLineSegment(sketch, "E2038", {"start": v(-527.65, 798.9) * mm, "end": v(-527.46, 799.01) * mm});
            skLineSegment(sketch, "E2039", {"start": v(-527.46, 799.01) * mm, "end": v(-527.26, 799.12) * mm});
            skLineSegment(sketch, "E2040", {"start": v(-527.26, 799.12) * mm, "end": v(-527.06, 799.22) * mm});
            skLineSegment(sketch, "E2041", {"start": v(-527.06, 799.22) * mm, "end": v(-526.85, 799.3) * mm});
            skLineSegment(sketch, "E2042", {"start": v(-526.85, 799.3) * mm, "end": v(-526.64, 799.38) * mm});
            skLineSegment(sketch, "E2043", {"start": v(-526.64, 799.38) * mm, "end": v(-526.42, 799.45) * mm});
            skLineSegment(sketch, "E2044", {"start": v(-526.42, 799.45) * mm, "end": v(-526.2, 799.5) * mm});
            skLineSegment(sketch, "E2045", {"start": v(-526.2, 799.5) * mm, "end": v(-525.98, 799.55) * mm});
            skLineSegment(sketch, "E2046", {"start": v(-525.98, 799.55) * mm, "end": v(-525.75, 799.59) * mm});
            skLineSegment(sketch, "E2047", {"start": v(-525.75, 799.59) * mm, "end": v(-525.51, 799.61) * mm});
            skLineSegment(sketch, "E2048", {"start": v(-525.51, 799.61) * mm, "end": v(-525.28, 799.62) * mm});
            skLineSegment(sketch, "E2049", {"start": v(-525.28, 799.62) * mm, "end": v(-525.16, 799.63) * mm});
            skLineSegment(sketch, "E2050", {"start": v(-525.16, 799.63) * mm, "end": v(-525.04, 799.62) * mm});
            skLineSegment(sketch, "E2051", {"start": v(-525.04, 799.62) * mm, "end": v(-524.8, 799.61) * mm});
            skLineSegment(sketch, "E2052", {"start": v(-524.8, 799.61) * mm, "end": v(-524.57, 799.59) * mm});
            skLineSegment(sketch, "E2053", {"start": v(-524.57, 799.59) * mm, "end": v(-524.34, 799.55) * mm});
            skLineSegment(sketch, "E2054", {"start": v(-524.34, 799.55) * mm, "end": v(-524.11, 799.5) * mm});
            skLineSegment(sketch, "E2055", {"start": v(-524.11, 799.5) * mm, "end": v(-523.9, 799.45) * mm});
            skLineSegment(sketch, "E2056", {"start": v(-523.9, 799.45) * mm, "end": v(-523.68, 799.38) * mm});
            skLineSegment(sketch, "E2057", {"start": v(-523.68, 799.38) * mm, "end": v(-523.47, 799.3) * mm});
            skLineSegment(sketch, "E2058", {"start": v(-523.47, 799.3) * mm, "end": v(-523.26, 799.22) * mm});
            skLineSegment(sketch, "E2059", {"start": v(-523.26, 799.22) * mm, "end": v(-523.06, 799.12) * mm});
            skLineSegment(sketch, "E2060", {"start": v(-523.06, 799.12) * mm, "end": v(-522.86, 799.01) * mm});
            skLineSegment(sketch, "E2061", {"start": v(-522.86, 799.01) * mm, "end": v(-522.67, 798.9) * mm});
            skLineSegment(sketch, "E2062", {"start": v(-522.67, 798.9) * mm, "end": v(-522.48, 798.77) * mm});
            skLineSegment(sketch, "E2063", {"start": v(-522.48, 798.77) * mm, "end": v(-522.3, 798.64) * mm});
            skLineSegment(sketch, "E2064", {"start": v(-522.3, 798.64) * mm, "end": v(-522.14, 798.5) * mm});
            skLineSegment(sketch, "E2065", {"start": v(-522.14, 798.5) * mm, "end": v(-521.97, 798.35) * mm});
            skLineSegment(sketch, "E2066", {"start": v(-521.97, 798.35) * mm, "end": v(-521.82, 798.2) * mm});
            skLineSegment(sketch, "E2067", {"start": v(-521.82, 798.2) * mm, "end": v(-521.67, 798.03) * mm});
            skLineSegment(sketch, "E2068", {"start": v(-521.67, 798.03) * mm, "end": v(-521.52, 797.86) * mm});
            skLineSegment(sketch, "E2069", {"start": v(-521.52, 797.86) * mm, "end": v(-521.4, 797.68) * mm});
            skLineSegment(sketch, "E2070", {"start": v(-521.4, 797.68) * mm, "end": v(-521.27, 797.5) * mm});
            skLineSegment(sketch, "E2071", {"start": v(-521.27, 797.5) * mm, "end": v(-521.15, 797.3) * mm});
            skLineSegment(sketch, "E2072", {"start": v(-521.15, 797.3) * mm, "end": v(-521.05, 797.1) * mm});
            skLineSegment(sketch, "E2073", {"start": v(-521.05, 797.1) * mm, "end": v(-520.95, 796.9) * mm});
            skLineSegment(sketch, "E2074", {"start": v(-520.95, 796.9) * mm, "end": v(-520.86, 796.7) * mm});
            skLineSegment(sketch, "E2075", {"start": v(-520.86, 796.7) * mm, "end": v(-520.78, 796.49) * mm});
            skLineSegment(sketch, "E2076", {"start": v(-520.78, 796.49) * mm, "end": v(-520.72, 796.27) * mm});
            skLineSegment(sketch, "E2077", {"start": v(-520.72, 796.27) * mm, "end": v(-520.66, 796.05) * mm});
            skLineSegment(sketch, "E2078", {"start": v(-520.66, 796.05) * mm, "end": v(-520.61, 795.83) * mm});
            skLineSegment(sketch, "E2079", {"start": v(-520.61, 795.83) * mm, "end": v(-520.58, 795.6) * mm});
            skLineSegment(sketch, "E2080", {"start": v(-520.58, 795.6) * mm, "end": v(-520.55, 795.36) * mm});
            skLineSegment(sketch, "E2081", {"start": v(-520.55, 795.36) * mm, "end": v(-520.54, 795.13) * mm});
            skLineSegment(sketch, "E2082", {"start": v(-520.54, 795.13) * mm, "end": v(-520.54, 795) * mm});
            skSolve(sketch);
        }
        {
            var Q0;
            Q0=makeQuery(id+"F0.imprint","IMPRINT",FACE,{"disambiguationData":[TD([[makeQuery(id+"F0.imprint","IMPRINT",EDGE,{"derivedFrom":sQuery(id+"F0.wireOp",EDGE,"E2")}),-1.0]])]});
            extrude(context, id + "F1", {"entities" : qUnion([Q0]), "depth" : 30 * mm, "offsetDistance" : 25 * mm});
        }
        {
            var Q0;
            Q0=qCreatedBy(makeId("Top.planeOp"),FACE);
            var sketch = newSketch(context, id + "F2", { "sketchPlane" : qUnion([Q0])});
            skLineSegment(sketch, "E2083", {"start": v(813.73, 1334.07) * mm, "end": v(943.6, 1334.07) * mm});
            skLineSegment(sketch, "E2084", {"start": v(808.16, 1312.43) * mm, "end": v(808.76, 1312.43) * mm});
            skLineSegment(sketch, "E2085", {"start": v(806.51, 1305.21) * mm, "end": v(813.73, 1305.21) * mm});
            skLineSegment(sketch, "E2086", {"start": v(806.51, 1298) * mm, "end": v(943.6, 1298) * mm});
            skLineSegment(sketch, "E2087", {"start": v(806.51, 1290.78) * mm, "end": v(943.6, 1290.78) * mm});
            skLineSegment(sketch, "E2088", {"start": v(806.51, 1283.57) * mm, "end": v(943.6, 1283.57) * mm});
            skLineSegment(sketch, "E2089", {"start": v(806.51, 1276.36) * mm, "end": v(943.6, 1276.36) * mm});
            skLineSegment(sketch, "E2090", {"start": v(806.51, 1269.14) * mm, "end": v(943.6, 1269.14) * mm});
            skLineSegment(sketch, "E2091", {"start": v(806.51, 1261.93) * mm, "end": v(943.6, 1261.93) * mm});
            skLineSegment(sketch, "E2092", {"start": v(806.51, 1254.71) * mm, "end": v(943.6, 1254.71) * mm});
            skLineSegment(sketch, "E2093", {"start": v(806.51, 1247.5) * mm, "end": v(943.6, 1247.5) * mm});
            skLineSegment(sketch, "E2094", {"start": v(806.51, 1240.28) * mm, "end": v(943.6, 1240.28) * mm});
            skLineSegment(sketch, "E2095", {"start": v(806.51, 1233.07) * mm, "end": v(943.6, 1233.07) * mm});
            skLineSegment(sketch, "E2096", {"start": v(806.51, 1225.85) * mm, "end": v(943.6, 1225.85) * mm});
            skLineSegment(sketch, "E2097", {"start": v(806.51, 1218.64) * mm, "end": v(943.6, 1218.64) * mm});
            skLineSegment(sketch, "E2098", {"start": v(806.51, 1211.42) * mm, "end": v(943.6, 1211.42) * mm});
            skLineSegment(sketch, "E2099", {"start": v(806.51, 1204.2) * mm, "end": v(943.6, 1204.2) * mm});
            skLineSegment(sketch, "E2100", {"start": v(806.51, 1197) * mm, "end": v(943.6, 1197) * mm});
            skLineSegment(sketch, "E2101", {"start": v(806.51, 1189.78) * mm, "end": v(943.6, 1189.78) * mm});
            skLineSegment(sketch, "E2102", {"start": v(806.51, 1182.56) * mm, "end": v(943.6, 1182.56) * mm});
            skLineSegment(sketch, "E2103", {"start": v(806.51, 1175.35) * mm, "end": v(943.6, 1175.35) * mm});
            skLineSegment(sketch, "E2104", {"start": v(806.51, 1168.14) * mm, "end": v(943.6, 1168.14) * mm});
            skLineSegment(sketch, "E2105", {"start": v(806.51, 1160.92) * mm, "end": v(943.6, 1160.92) * mm});
            skLineSegment(sketch, "E2106", {"start": v(806.51, 1153.7) * mm, "end": v(943.6, 1153.7) * mm});
            skLineSegment(sketch, "E2107", {"start": v(806.51, 1148.66) * mm, "end": v(943.6, 1148.66) * mm});
            skLineSegment(sketch, "E2108", {"start": v(806.51, 1334.07) * mm, "end": v(806.51, 1333.35) * mm});
            skLineSegment(sketch, "E2109", {"start": v(813.73, 1334.07) * mm, "end": v(813.73, 1333.35) * mm});
            skLineSegment(sketch, "E2110", {"start": v(820.94, 1334.07) * mm, "end": v(820.94, 1326.86) * mm});
            skLineSegment(sketch, "E2111", {"start": v(828.16, 1334.07) * mm, "end": v(828.16, 1148.66) * mm});
            skLineSegment(sketch, "E2112", {"start": v(835.37, 1334.07) * mm, "end": v(835.37, 1148.66) * mm});
            skLineSegment(sketch, "E2113", {"start": v(842.59, 1334.07) * mm, "end": v(842.59, 1148.66) * mm});
            skLineSegment(sketch, "E2114", {"start": v(849.8, 1334.07) * mm, "end": v(849.8, 1148.66) * mm});
            skLineSegment(sketch, "E2115", {"start": v(857.02, 1334.07) * mm, "end": v(857.02, 1148.66) * mm});
            skLineSegment(sketch, "E2116", {"start": v(864.23, 1334.07) * mm, "end": v(864.23, 1148.66) * mm});
            skLineSegment(sketch, "E2117", {"start": v(871.45, 1334.07) * mm, "end": v(871.45, 1148.66) * mm});
            skLineSegment(sketch, "E2118", {"start": v(878.66, 1334.07) * mm, "end": v(878.66, 1148.66) * mm});
            skLineSegment(sketch, "E2119", {"start": v(885.87, 1334.07) * mm, "end": v(885.87, 1148.66) * mm});
            skLineSegment(sketch, "E2120", {"start": v(893.1, 1334.07) * mm, "end": v(893.1, 1148.66) * mm});
            skLineSegment(sketch, "E2121", {"start": v(900.3, 1334.07) * mm, "end": v(900.3, 1148.66) * mm});
            skLineSegment(sketch, "E2122", {"start": v(907.52, 1334.07) * mm, "end": v(907.52, 1148.66) * mm});
            skLineSegment(sketch, "E2123", {"start": v(914.73, 1334.07) * mm, "end": v(914.73, 1148.66) * mm});
            skLineSegment(sketch, "E2124", {"start": v(921.95, 1334.07) * mm, "end": v(921.95, 1148.66) * mm});
            skLineSegment(sketch, "E2125", {"start": v(929.16, 1334.07) * mm, "end": v(929.16, 1148.66) * mm});
            skLineSegment(sketch, "E2126", {"start": v(936.38, 1334.07) * mm, "end": v(936.38, 1148.66) * mm});
            skLineSegment(sketch, "E2127", {"start": v(943.6, 1334.07) * mm, "end": v(943.6, 1148.66) * mm});
            skLineSegment(sketch, "E2128", {"start": v(806.51, 1334.8) * mm, "end": v(806.51, 1333.35) * mm});
            skLineSegment(sketch, "E2129", {"start": v(813.73, 1334.8) * mm, "end": v(813.73, 1333.35) * mm});
            skLineSegment(sketch, "E2130", {"start": v(806.51, 1334.07) * mm, "end": v(813.73, 1334.07) * mm});
            skLineSegment(sketch, "E2131", {"start": v(824.7, 1316.93) * mm, "end": v(824.77, 1316.92) * mm});
            skLineSegment(sketch, "E2132", {"start": v(824.77, 1316.92) * mm, "end": v(824.84, 1316.9) * mm});
            skLineSegment(sketch, "E2133", {"start": v(824.84, 1316.9) * mm, "end": v(824.9, 1316.9) * mm});
            skLineSegment(sketch, "E2134", {"start": v(824.9, 1316.9) * mm, "end": v(824.97, 1316.88) * mm});
            skLineSegment(sketch, "E2135", {"start": v(824.97, 1316.88) * mm, "end": v(825.04, 1316.86) * mm});
            skLineSegment(sketch, "E2136", {"start": v(825.04, 1316.86) * mm, "end": v(825.1, 1316.84) * mm});
            skLineSegment(sketch, "E2137", {"start": v(825.1, 1316.84) * mm, "end": v(825.17, 1316.82) * mm});
            skLineSegment(sketch, "E2138", {"start": v(825.17, 1316.82) * mm, "end": v(825.23, 1316.8) * mm});
            skLineSegment(sketch, "E2139", {"start": v(825.23, 1316.8) * mm, "end": v(825.3, 1316.77) * mm});
            skLineSegment(sketch, "E2140", {"start": v(825.3, 1316.77) * mm, "end": v(825.37, 1316.74) * mm});
            skLineSegment(sketch, "E2141", {"start": v(825.37, 1316.74) * mm, "end": v(825.43, 1316.72) * mm});
            skLineSegment(sketch, "E2142", {"start": v(825.43, 1316.72) * mm, "end": v(825.5, 1316.69) * mm});
            skLineSegment(sketch, "E2143", {"start": v(825.5, 1316.69) * mm, "end": v(825.56, 1316.66) * mm});
            skLineSegment(sketch, "E2144", {"start": v(825.56, 1316.66) * mm, "end": v(825.63, 1316.62) * mm});
            skLineSegment(sketch, "E2145", {"start": v(825.63, 1316.62) * mm, "end": v(825.7, 1316.59) * mm});
            skLineSegment(sketch, "E2146", {"start": v(825.7, 1316.59) * mm, "end": v(825.76, 1316.55) * mm});
            skLineSegment(sketch, "E2147", {"start": v(825.76, 1316.55) * mm, "end": v(825.82, 1316.51) * mm});
            skLineSegment(sketch, "E2148", {"start": v(825.82, 1316.51) * mm, "end": v(825.89, 1316.48) * mm});
            skLineSegment(sketch, "E2149", {"start": v(825.89, 1316.48) * mm, "end": v(825.95, 1316.44) * mm});
            skLineSegment(sketch, "E2150", {"start": v(825.95, 1316.44) * mm, "end": v(826.01, 1316.4) * mm});
            skLineSegment(sketch, "E2151", {"start": v(826.01, 1316.4) * mm, "end": v(826.08, 1316.35) * mm});
            skLineSegment(sketch, "E2152", {"start": v(826.08, 1316.35) * mm, "end": v(826.14, 1316.3) * mm});
            skLineSegment(sketch, "E2153", {"start": v(826.14, 1316.3) * mm, "end": v(826.2, 1316.26) * mm});
            skLineSegment(sketch, "E2154", {"start": v(826.2, 1316.26) * mm, "end": v(826.27, 1316.21) * mm});
            skLineSegment(sketch, "E2155", {"start": v(826.27, 1316.21) * mm, "end": v(826.33, 1316.17) * mm});
            skLineSegment(sketch, "E2156", {"start": v(826.33, 1316.17) * mm, "end": v(826.4, 1316.11) * mm});
            skLineSegment(sketch, "E2157", {"start": v(826.4, 1316.11) * mm, "end": v(826.45, 1316.06) * mm});
            skLineSegment(sketch, "E2158", {"start": v(826.45, 1316.06) * mm, "end": v(826.51, 1316.01) * mm});
            skLineSegment(sketch, "E2159", {"start": v(826.51, 1316.01) * mm, "end": v(826.65, 1315.9) * mm});
            skLineSegment(sketch, "E2160", {"start": v(826.65, 1315.9) * mm, "end": v(826.52, 1315.06) * mm});
            skLineSegment(sketch, "E2161", {"start": v(826.52, 1315.06) * mm, "end": v(826.45, 1315.02) * mm});
            skLineSegment(sketch, "E2162", {"start": v(826.45, 1315.02) * mm, "end": v(826.38, 1314.98) * mm});
            skLineSegment(sketch, "E2163", {"start": v(826.38, 1314.98) * mm, "end": v(826.3, 1314.95) * mm});
            skLineSegment(sketch, "E2164", {"start": v(826.3, 1314.95) * mm, "end": v(826.23, 1314.91) * mm});
            skLineSegment(sketch, "E2165", {"start": v(826.23, 1314.91) * mm, "end": v(826.16, 1314.88) * mm});
            skLineSegment(sketch, "E2166", {"start": v(826.16, 1314.88) * mm, "end": v(826.09, 1314.85) * mm});
            skLineSegment(sketch, "E2167", {"start": v(826.09, 1314.85) * mm, "end": v(826.01, 1314.82) * mm});
            skLineSegment(sketch, "E2168", {"start": v(826.01, 1314.82) * mm, "end": v(825.94, 1314.8) * mm});
            skLineSegment(sketch, "E2169", {"start": v(825.94, 1314.8) * mm, "end": v(825.87, 1314.77) * mm});
            skLineSegment(sketch, "E2170", {"start": v(825.87, 1314.77) * mm, "end": v(825.8, 1314.74) * mm});
            skLineSegment(sketch, "E2171", {"start": v(825.8, 1314.74) * mm, "end": v(825.72, 1314.72) * mm});
            skLineSegment(sketch, "E2172", {"start": v(825.72, 1314.72) * mm, "end": v(825.65, 1314.7) * mm});
            skLineSegment(sketch, "E2173", {"start": v(825.65, 1314.7) * mm, "end": v(825.58, 1314.67) * mm});
            skLineSegment(sketch, "E2174", {"start": v(825.58, 1314.67) * mm, "end": v(825.5, 1314.66) * mm});
            skLineSegment(sketch, "E2175", {"start": v(825.5, 1314.66) * mm, "end": v(825.43, 1314.64) * mm});
            skLineSegment(sketch, "E2176", {"start": v(825.43, 1314.64) * mm, "end": v(825.36, 1314.62) * mm});
            skLineSegment(sketch, "E2177", {"start": v(825.36, 1314.62) * mm, "end": v(825.3, 1314.6) * mm});
            skLineSegment(sketch, "E2178", {"start": v(825.3, 1314.6) * mm, "end": v(825.22, 1314.6) * mm});
            skLineSegment(sketch, "E2179", {"start": v(825.22, 1314.6) * mm, "end": v(825.15, 1314.58) * mm});
            skLineSegment(sketch, "E2180", {"start": v(825.15, 1314.58) * mm, "end": v(825.08, 1314.57) * mm});
            skLineSegment(sketch, "E2181", {"start": v(825.08, 1314.57) * mm, "end": v(825.01, 1314.56) * mm});
            skLineSegment(sketch, "E2182", {"start": v(825.01, 1314.56) * mm, "end": v(824.94, 1314.56) * mm});
            skLineSegment(sketch, "E2183", {"start": v(824.94, 1314.56) * mm, "end": v(824.87, 1314.55) * mm});
            skLineSegment(sketch, "E2184", {"start": v(824.87, 1314.55) * mm, "end": v(824.8, 1314.55) * mm});
            skLineSegment(sketch, "E2185", {"start": v(824.8, 1314.55) * mm, "end": v(824.73, 1314.54) * mm});
            skLineSegment(sketch, "E2186", {"start": v(824.73, 1314.54) * mm, "end": v(824.66, 1314.54) * mm});
            skLineSegment(sketch, "E2187", {"start": v(824.66, 1314.54) * mm, "end": v(824.6, 1314.55) * mm});
            skLineSegment(sketch, "E2188", {"start": v(824.6, 1314.55) * mm, "end": v(824.53, 1314.55) * mm});
            skLineSegment(sketch, "E2189", {"start": v(824.53, 1314.55) * mm, "end": v(824.46, 1314.56) * mm});
            skLineSegment(sketch, "E2190", {"start": v(824.46, 1314.56) * mm, "end": v(824.4, 1314.56) * mm});
            skLineSegment(sketch, "E2191", {"start": v(824.4, 1314.56) * mm, "end": v(823.17, 1314.9) * mm});
            skLineSegment(sketch, "E2192", {"start": v(823.17, 1314.9) * mm, "end": v(822.57, 1313.47) * mm});
            skLineSegment(sketch, "E2193", {"start": v(822.57, 1313.47) * mm, "end": v(823.69, 1312.85) * mm});
            skLineSegment(sketch, "E2194", {"start": v(823.69, 1312.85) * mm, "end": v(823.74, 1312.8) * mm});
            skLineSegment(sketch, "E2195", {"start": v(823.74, 1312.8) * mm, "end": v(823.79, 1312.76) * mm});
            skLineSegment(sketch, "E2196", {"start": v(823.79, 1312.76) * mm, "end": v(823.84, 1312.71) * mm});
            skLineSegment(sketch, "E2197", {"start": v(823.84, 1312.71) * mm, "end": v(823.89, 1312.67) * mm});
            skLineSegment(sketch, "E2198", {"start": v(823.89, 1312.67) * mm, "end": v(823.94, 1312.62) * mm});
            skLineSegment(sketch, "E2199", {"start": v(823.94, 1312.62) * mm, "end": v(823.98, 1312.57) * mm});
            skLineSegment(sketch, "E2200", {"start": v(823.98, 1312.57) * mm, "end": v(824.03, 1312.52) * mm});
            skLineSegment(sketch, "E2201", {"start": v(824.03, 1312.52) * mm, "end": v(824.07, 1312.47) * mm});
            skLineSegment(sketch, "E2202", {"start": v(824.07, 1312.47) * mm, "end": v(824.12, 1312.41) * mm});
            skLineSegment(sketch, "E2203", {"start": v(824.12, 1312.41) * mm, "end": v(824.16, 1312.36) * mm});
            skLineSegment(sketch, "E2204", {"start": v(824.16, 1312.36) * mm, "end": v(824.2, 1312.3) * mm});
            skLineSegment(sketch, "E2205", {"start": v(824.2, 1312.3) * mm, "end": v(824.25, 1312.24) * mm});
            skLineSegment(sketch, "E2206", {"start": v(824.25, 1312.24) * mm, "end": v(824.29, 1312.18) * mm});
            skLineSegment(sketch, "E2207", {"start": v(824.29, 1312.18) * mm, "end": v(824.33, 1312.12) * mm});
            skLineSegment(sketch, "E2208", {"start": v(824.33, 1312.12) * mm, "end": v(824.37, 1312.06) * mm});
            skLineSegment(sketch, "E2209", {"start": v(824.37, 1312.06) * mm, "end": v(824.4, 1312) * mm});
            skLineSegment(sketch, "E2210", {"start": v(824.4, 1312) * mm, "end": v(824.44, 1311.93) * mm});
            skLineSegment(sketch, "E2211", {"start": v(824.44, 1311.93) * mm, "end": v(824.48, 1311.86) * mm});
            skLineSegment(sketch, "E2212", {"start": v(824.48, 1311.86) * mm, "end": v(824.51, 1311.8) * mm});
            skLineSegment(sketch, "E2213", {"start": v(824.51, 1311.8) * mm, "end": v(824.55, 1311.73) * mm});
            skLineSegment(sketch, "E2214", {"start": v(824.55, 1311.73) * mm, "end": v(824.58, 1311.66) * mm});
            skLineSegment(sketch, "E2215", {"start": v(824.58, 1311.66) * mm, "end": v(824.61, 1311.6) * mm});
            skLineSegment(sketch, "E2216", {"start": v(824.61, 1311.6) * mm, "end": v(824.65, 1311.52) * mm});
            skLineSegment(sketch, "E2217", {"start": v(824.65, 1311.52) * mm, "end": v(824.68, 1311.45) * mm});
            skLineSegment(sketch, "E2218", {"start": v(824.68, 1311.45) * mm, "end": v(824.7, 1311.37) * mm});
            skLineSegment(sketch, "E2219", {"start": v(824.7, 1311.37) * mm, "end": v(824.74, 1311.3) * mm});
            skLineSegment(sketch, "E2220", {"start": v(824.74, 1311.3) * mm, "end": v(824.76, 1311.22) * mm});
            skLineSegment(sketch, "E2221", {"start": v(824.76, 1311.22) * mm, "end": v(824.8, 1311.15) * mm});
            skLineSegment(sketch, "E2222", {"start": v(824.8, 1311.15) * mm, "end": v(824.82, 1311.07) * mm});
            skLineSegment(sketch, "E2223", {"start": v(824.82, 1311.07) * mm, "end": v(824.84, 1311) * mm});
            skLineSegment(sketch, "E2224", {"start": v(824.84, 1311) * mm, "end": v(824.59, 1310.65) * mm});
            skLineSegment(sketch, "E2225", {"start": v(824.59, 1310.65) * mm, "end": v(824.32, 1310.31) * mm});
            skLineSegment(sketch, "E2226", {"start": v(824.32, 1310.31) * mm, "end": v(824.24, 1310.32) * mm});
            skLineSegment(sketch, "E2227", {"start": v(824.24, 1310.32) * mm, "end": v(824.16, 1310.32) * mm});
            skLineSegment(sketch, "E2228", {"start": v(824.16, 1310.32) * mm, "end": v(824.08, 1310.33) * mm});
            skLineSegment(sketch, "E2229", {"start": v(824.08, 1310.33) * mm, "end": v(824, 1310.34) * mm});
            skLineSegment(sketch, "E2230", {"start": v(824, 1310.34) * mm, "end": v(823.92, 1310.35) * mm});
            skLineSegment(sketch, "E2231", {"start": v(823.92, 1310.35) * mm, "end": v(823.84, 1310.36) * mm});
            skLineSegment(sketch, "E2232", {"start": v(823.84, 1310.36) * mm, "end": v(823.76, 1310.37) * mm});
            skLineSegment(sketch, "E2233", {"start": v(823.76, 1310.37) * mm, "end": v(823.68, 1310.38) * mm});
            skLineSegment(sketch, "E2234", {"start": v(823.68, 1310.38) * mm, "end": v(823.6, 1310.4) * mm});
            skLineSegment(sketch, "E2235", {"start": v(823.6, 1310.4) * mm, "end": v(823.53, 1310.4) * mm});
            skLineSegment(sketch, "E2236", {"start": v(823.53, 1310.4) * mm, "end": v(823.46, 1310.42) * mm});
            skLineSegment(sketch, "E2237", {"start": v(823.46, 1310.42) * mm, "end": v(823.38, 1310.44) * mm});
            skLineSegment(sketch, "E2238", {"start": v(823.38, 1310.44) * mm, "end": v(823.31, 1310.46) * mm});
            skLineSegment(sketch, "E2239", {"start": v(823.31, 1310.46) * mm, "end": v(823.24, 1310.48) * mm});
            skLineSegment(sketch, "E2240", {"start": v(823.24, 1310.48) * mm, "end": v(823.17, 1310.5) * mm});
            skLineSegment(sketch, "E2241", {"start": v(823.17, 1310.5) * mm, "end": v(823.1, 1310.52) * mm});
            skLineSegment(sketch, "E2242", {"start": v(823.1, 1310.52) * mm, "end": v(823.03, 1310.54) * mm});
            skLineSegment(sketch, "E2243", {"start": v(823.03, 1310.54) * mm, "end": v(822.96, 1310.57) * mm});
            skLineSegment(sketch, "E2244", {"start": v(822.96, 1310.57) * mm, "end": v(822.9, 1310.6) * mm});
            skLineSegment(sketch, "E2245", {"start": v(822.9, 1310.6) * mm, "end": v(822.83, 1310.62) * mm});
            skLineSegment(sketch, "E2246", {"start": v(822.83, 1310.62) * mm, "end": v(822.76, 1310.64) * mm});
            skLineSegment(sketch, "E2247", {"start": v(822.76, 1310.64) * mm, "end": v(822.7, 1310.67) * mm});
            skLineSegment(sketch, "E2248", {"start": v(822.7, 1310.67) * mm, "end": v(822.64, 1310.7) * mm});
            skLineSegment(sketch, "E2249", {"start": v(822.64, 1310.7) * mm, "end": v(822.57, 1310.73) * mm});
            skLineSegment(sketch, "E2250", {"start": v(822.57, 1310.73) * mm, "end": v(822.51, 1310.77) * mm});
            skLineSegment(sketch, "E2251", {"start": v(822.51, 1310.77) * mm, "end": v(822.46, 1310.8) * mm});
            skLineSegment(sketch, "E2252", {"start": v(822.46, 1310.8) * mm, "end": v(822.4, 1310.84) * mm});
            skLineSegment(sketch, "E2253", {"start": v(822.4, 1310.84) * mm, "end": v(822.34, 1310.87) * mm});
            skLineSegment(sketch, "E2254", {"start": v(822.34, 1310.87) * mm, "end": v(822.29, 1310.91) * mm});
            skLineSegment(sketch, "E2255", {"start": v(822.29, 1310.91) * mm, "end": v(822.23, 1310.95) * mm});
            skLineSegment(sketch, "E2256", {"start": v(822.23, 1310.95) * mm, "end": v(821.34, 1311.87) * mm});
            skLineSegment(sketch, "E2257", {"start": v(821.34, 1311.87) * mm, "end": v(820.1, 1310.92) * mm});
            skLineSegment(sketch, "E2258", {"start": v(820.1, 1310.92) * mm, "end": v(820.76, 1309.82) * mm});
            skLineSegment(sketch, "E2259", {"start": v(820.76, 1309.82) * mm, "end": v(820.78, 1309.76) * mm});
            skLineSegment(sketch, "E2260", {"start": v(820.78, 1309.76) * mm, "end": v(820.8, 1309.7) * mm});
            skLineSegment(sketch, "E2261", {"start": v(820.8, 1309.7) * mm, "end": v(820.82, 1309.63) * mm});
            skLineSegment(sketch, "E2262", {"start": v(820.82, 1309.63) * mm, "end": v(820.84, 1309.57) * mm});
            skLineSegment(sketch, "E2263", {"start": v(820.84, 1309.57) * mm, "end": v(820.86, 1309.5) * mm});
            skLineSegment(sketch, "E2264", {"start": v(820.86, 1309.5) * mm, "end": v(820.88, 1309.43) * mm});
            skLineSegment(sketch, "E2265", {"start": v(820.88, 1309.43) * mm, "end": v(820.9, 1309.37) * mm});
            skLineSegment(sketch, "E2266", {"start": v(820.9, 1309.37) * mm, "end": v(820.9, 1309.3) * mm});
            skLineSegment(sketch, "E2267", {"start": v(820.9, 1309.3) * mm, "end": v(820.92, 1309.23) * mm});
            skLineSegment(sketch, "E2268", {"start": v(820.92, 1309.23) * mm, "end": v(820.93, 1309.16) * mm});
            skLineSegment(sketch, "E2269", {"start": v(820.93, 1309.16) * mm, "end": v(820.93, 1309.09) * mm});
            skLineSegment(sketch, "E2270", {"start": v(820.93, 1309.09) * mm, "end": v(820.94, 1309.02) * mm});
            skLineSegment(sketch, "E2271", {"start": v(820.94, 1309.02) * mm, "end": v(820.95, 1308.94) * mm});
            skLineSegment(sketch, "E2272", {"start": v(820.95, 1308.94) * mm, "end": v(820.95, 1308.87) * mm});
            skLineSegment(sketch, "E2273", {"start": v(820.95, 1308.87) * mm, "end": v(820.95, 1308.8) * mm});
            skLineSegment(sketch, "E2274", {"start": v(820.95, 1308.8) * mm, "end": v(820.95, 1308.72) * mm});
            skLineSegment(sketch, "E2275", {"start": v(820.95, 1308.72) * mm, "end": v(820.95, 1308.65) * mm});
            skLineSegment(sketch, "E2276", {"start": v(820.95, 1308.65) * mm, "end": v(820.95, 1308.57) * mm});
            skLineSegment(sketch, "E2277", {"start": v(820.95, 1308.57) * mm, "end": v(820.95, 1308.5) * mm});
            skLineSegment(sketch, "E2278", {"start": v(820.95, 1308.5) * mm, "end": v(820.95, 1308.42) * mm});
            skLineSegment(sketch, "E2279", {"start": v(820.95, 1308.42) * mm, "end": v(820.94, 1308.35) * mm});
            skLineSegment(sketch, "E2280", {"start": v(820.94, 1308.35) * mm, "end": v(820.93, 1308.27) * mm});
            skLineSegment(sketch, "E2281", {"start": v(820.93, 1308.27) * mm, "end": v(820.93, 1308.2) * mm});
            skLineSegment(sketch, "E2282", {"start": v(820.93, 1308.2) * mm, "end": v(820.92, 1308.11) * mm});
            skLineSegment(sketch, "E2283", {"start": v(820.92, 1308.11) * mm, "end": v(820.9, 1308.04) * mm});
            skLineSegment(sketch, "E2284", {"start": v(820.9, 1308.04) * mm, "end": v(820.9, 1307.96) * mm});
            skLineSegment(sketch, "E2285", {"start": v(820.9, 1307.96) * mm, "end": v(820.88, 1307.88) * mm});
            skLineSegment(sketch, "E2286", {"start": v(820.88, 1307.88) * mm, "end": v(820.86, 1307.8) * mm});
            skLineSegment(sketch, "E2287", {"start": v(820.86, 1307.8) * mm, "end": v(820.85, 1307.72) * mm});
            skLineSegment(sketch, "E2288", {"start": v(820.85, 1307.72) * mm, "end": v(820.83, 1307.64) * mm});
            skLineSegment(sketch, "E2289", {"start": v(820.83, 1307.64) * mm, "end": v(820.44, 1307.46) * mm});
            skLineSegment(sketch, "E2290", {"start": v(820.44, 1307.46) * mm, "end": v(820.04, 1307.3) * mm});
            skLineSegment(sketch, "E2291", {"start": v(820.04, 1307.3) * mm, "end": v(819.97, 1307.35) * mm});
            skLineSegment(sketch, "E2292", {"start": v(819.97, 1307.35) * mm, "end": v(819.9, 1307.4) * mm});
            skLineSegment(sketch, "E2293", {"start": v(819.9, 1307.4) * mm, "end": v(819.84, 1307.45) * mm});
            skLineSegment(sketch, "E2294", {"start": v(819.84, 1307.45) * mm, "end": v(819.77, 1307.5) * mm});
            skLineSegment(sketch, "E2295", {"start": v(819.77, 1307.5) * mm, "end": v(819.7, 1307.54) * mm});
            skLineSegment(sketch, "E2296", {"start": v(819.7, 1307.54) * mm, "end": v(819.65, 1307.59) * mm});
            skLineSegment(sketch, "E2297", {"start": v(819.65, 1307.59) * mm, "end": v(819.58, 1307.64) * mm});
            skLineSegment(sketch, "E2298", {"start": v(819.58, 1307.64) * mm, "end": v(819.52, 1307.69) * mm});
            skLineSegment(sketch, "E2299", {"start": v(819.52, 1307.69) * mm, "end": v(819.46, 1307.73) * mm});
            skLineSegment(sketch, "E2300", {"start": v(819.46, 1307.73) * mm, "end": v(819.4, 1307.78) * mm});
            skLineSegment(sketch, "E2301", {"start": v(819.4, 1307.78) * mm, "end": v(819.35, 1307.84) * mm});
            skLineSegment(sketch, "E2302", {"start": v(819.35, 1307.84) * mm, "end": v(819.3, 1307.89) * mm});
            skLineSegment(sketch, "E2303", {"start": v(819.3, 1307.89) * mm, "end": v(819.24, 1307.94) * mm});
            skLineSegment(sketch, "E2304", {"start": v(819.24, 1307.94) * mm, "end": v(819.19, 1308) * mm});
            skLineSegment(sketch, "E2305", {"start": v(819.19, 1308) * mm, "end": v(819.14, 1308.05) * mm});
            skLineSegment(sketch, "E2306", {"start": v(819.14, 1308.05) * mm, "end": v(819.09, 1308.1) * mm});
            skLineSegment(sketch, "E2307", {"start": v(819.09, 1308.1) * mm, "end": v(819.04, 1308.15) * mm});
            skLineSegment(sketch, "E2308", {"start": v(819.04, 1308.15) * mm, "end": v(819, 1308.2) * mm});
            skLineSegment(sketch, "E2309", {"start": v(819, 1308.2) * mm, "end": v(818.94, 1308.26) * mm});
            skLineSegment(sketch, "E2310", {"start": v(818.94, 1308.26) * mm, "end": v(818.9, 1308.32) * mm});
            skLineSegment(sketch, "E2311", {"start": v(818.9, 1308.32) * mm, "end": v(818.86, 1308.38) * mm});
            skLineSegment(sketch, "E2312", {"start": v(818.86, 1308.38) * mm, "end": v(818.82, 1308.43) * mm});
            skLineSegment(sketch, "E2313", {"start": v(818.82, 1308.43) * mm, "end": v(818.78, 1308.5) * mm});
            skLineSegment(sketch, "E2314", {"start": v(818.78, 1308.5) * mm, "end": v(818.74, 1308.55) * mm});
            skLineSegment(sketch, "E2315", {"start": v(818.74, 1308.55) * mm, "end": v(818.7, 1308.6) * mm});
            skLineSegment(sketch, "E2316", {"start": v(818.7, 1308.6) * mm, "end": v(818.67, 1308.66) * mm});
            skLineSegment(sketch, "E2317", {"start": v(818.67, 1308.66) * mm, "end": v(818.64, 1308.72) * mm});
            skLineSegment(sketch, "E2318", {"start": v(818.64, 1308.72) * mm, "end": v(818.6, 1308.78) * mm});
            skLineSegment(sketch, "E2319", {"start": v(818.6, 1308.78) * mm, "end": v(818.58, 1308.84) * mm});
            skLineSegment(sketch, "E2320", {"start": v(818.58, 1308.84) * mm, "end": v(818.55, 1308.9) * mm});
            skLineSegment(sketch, "E2321", {"start": v(818.55, 1308.9) * mm, "end": v(818.24, 1310.15) * mm});
            skLineSegment(sketch, "E2322", {"start": v(818.24, 1310.15) * mm, "end": v(816.7, 1309.94) * mm});
            skLineSegment(sketch, "E2323", {"start": v(816.7, 1309.94) * mm, "end": v(816.71, 1308.66) * mm});
            skLineSegment(sketch, "E2324", {"start": v(816.71, 1308.66) * mm, "end": v(816.7, 1308.6) * mm});
            skLineSegment(sketch, "E2325", {"start": v(816.7, 1308.6) * mm, "end": v(816.68, 1308.53) * mm});
            skLineSegment(sketch, "E2326", {"start": v(816.68, 1308.53) * mm, "end": v(816.67, 1308.46) * mm});
            skLineSegment(sketch, "E2327", {"start": v(816.67, 1308.46) * mm, "end": v(816.66, 1308.4) * mm});
            skLineSegment(sketch, "E2328", {"start": v(816.66, 1308.4) * mm, "end": v(816.64, 1308.33) * mm});
            skLineSegment(sketch, "E2329", {"start": v(816.64, 1308.33) * mm, "end": v(816.62, 1308.27) * mm});
            skLineSegment(sketch, "E2330", {"start": v(816.62, 1308.27) * mm, "end": v(816.6, 1308.2) * mm});
            skLineSegment(sketch, "E2331", {"start": v(816.6, 1308.2) * mm, "end": v(816.57, 1308.14) * mm});
            skLineSegment(sketch, "E2332", {"start": v(816.57, 1308.14) * mm, "end": v(816.55, 1308.07) * mm});
            skLineSegment(sketch, "E2333", {"start": v(816.55, 1308.07) * mm, "end": v(816.52, 1308) * mm});
            skLineSegment(sketch, "E2334", {"start": v(816.52, 1308) * mm, "end": v(816.5, 1307.94) * mm});
            skLineSegment(sketch, "E2335", {"start": v(816.5, 1307.94) * mm, "end": v(816.47, 1307.87) * mm});
            skLineSegment(sketch, "E2336", {"start": v(816.47, 1307.87) * mm, "end": v(816.43, 1307.81) * mm});
            skLineSegment(sketch, "E2337", {"start": v(816.43, 1307.81) * mm, "end": v(816.4, 1307.75) * mm});
            skLineSegment(sketch, "E2338", {"start": v(816.4, 1307.75) * mm, "end": v(816.37, 1307.68) * mm});
            skLineSegment(sketch, "E2339", {"start": v(816.37, 1307.68) * mm, "end": v(816.33, 1307.62) * mm});
            skLineSegment(sketch, "E2340", {"start": v(816.33, 1307.62) * mm, "end": v(816.3, 1307.55) * mm});
            skLineSegment(sketch, "E2341", {"start": v(816.3, 1307.55) * mm, "end": v(816.26, 1307.49) * mm});
            skLineSegment(sketch, "E2342", {"start": v(816.26, 1307.49) * mm, "end": v(816.22, 1307.42) * mm});
            skLineSegment(sketch, "E2343", {"start": v(816.22, 1307.42) * mm, "end": v(816.17, 1307.36) * mm});
            skLineSegment(sketch, "E2344", {"start": v(816.17, 1307.36) * mm, "end": v(816.13, 1307.3) * mm});
            skLineSegment(sketch, "E2345", {"start": v(816.13, 1307.3) * mm, "end": v(816.09, 1307.23) * mm});
            skLineSegment(sketch, "E2346", {"start": v(816.09, 1307.23) * mm, "end": v(816.04, 1307.17) * mm});
            skLineSegment(sketch, "E2347", {"start": v(816.04, 1307.17) * mm, "end": v(816, 1307.1) * mm});
            skLineSegment(sketch, "E2348", {"start": v(816, 1307.1) * mm, "end": v(815.94, 1307.04) * mm});
            skLineSegment(sketch, "E2349", {"start": v(815.94, 1307.04) * mm, "end": v(815.9, 1306.98) * mm});
            skLineSegment(sketch, "E2350", {"start": v(815.9, 1306.98) * mm, "end": v(815.84, 1306.92) * mm});
            skLineSegment(sketch, "E2351", {"start": v(815.84, 1306.92) * mm, "end": v(815.79, 1306.86) * mm});
            skLineSegment(sketch, "E2352", {"start": v(815.79, 1306.86) * mm, "end": v(815.74, 1306.8) * mm});
            skLineSegment(sketch, "E2353", {"start": v(815.74, 1306.8) * mm, "end": v(815.68, 1306.74) * mm});
            skLineSegment(sketch, "E2354", {"start": v(815.68, 1306.74) * mm, "end": v(815.26, 1306.78) * mm});
            skLineSegment(sketch, "E2355", {"start": v(815.26, 1306.78) * mm, "end": v(814.84, 1306.85) * mm});
            skLineSegment(sketch, "E2356", {"start": v(814.84, 1306.85) * mm, "end": v(814.8, 1306.92) * mm});
            skLineSegment(sketch, "E2357", {"start": v(814.8, 1306.92) * mm, "end": v(814.76, 1307) * mm});
            skLineSegment(sketch, "E2358", {"start": v(814.76, 1307) * mm, "end": v(814.73, 1307.07) * mm});
            skLineSegment(sketch, "E2359", {"start": v(814.73, 1307.07) * mm, "end": v(814.7, 1307.14) * mm});
            skLineSegment(sketch, "E2360", {"start": v(814.7, 1307.14) * mm, "end": v(814.66, 1307.21) * mm});
            skLineSegment(sketch, "E2361", {"start": v(814.66, 1307.21) * mm, "end": v(814.63, 1307.29) * mm});
            skLineSegment(sketch, "E2362", {"start": v(814.63, 1307.29) * mm, "end": v(814.6, 1307.36) * mm});
            skLineSegment(sketch, "E2363", {"start": v(814.6, 1307.36) * mm, "end": v(814.57, 1307.43) * mm});
            skLineSegment(sketch, "E2364", {"start": v(814.57, 1307.43) * mm, "end": v(814.55, 1307.5) * mm});
            skLineSegment(sketch, "E2365", {"start": v(814.55, 1307.5) * mm, "end": v(814.52, 1307.58) * mm});
            skLineSegment(sketch, "E2366", {"start": v(814.52, 1307.58) * mm, "end": v(814.5, 1307.65) * mm});
            skLineSegment(sketch, "E2367", {"start": v(814.5, 1307.65) * mm, "end": v(814.48, 1307.72) * mm});
            skLineSegment(sketch, "E2368", {"start": v(814.48, 1307.72) * mm, "end": v(814.45, 1307.8) * mm});
            skLineSegment(sketch, "E2369", {"start": v(814.45, 1307.8) * mm, "end": v(814.44, 1307.87) * mm});
            skLineSegment(sketch, "E2370", {"start": v(814.44, 1307.87) * mm, "end": v(814.42, 1307.94) * mm});
            skLineSegment(sketch, "E2371", {"start": v(814.42, 1307.94) * mm, "end": v(814.4, 1308) * mm});
            skLineSegment(sketch, "E2372", {"start": v(814.4, 1308) * mm, "end": v(814.39, 1308.08) * mm});
            skLineSegment(sketch, "E2373", {"start": v(814.39, 1308.08) * mm, "end": v(814.37, 1308.15) * mm});
            skLineSegment(sketch, "E2374", {"start": v(814.37, 1308.15) * mm, "end": v(814.36, 1308.22) * mm});
            skLineSegment(sketch, "E2375", {"start": v(814.36, 1308.22) * mm, "end": v(814.35, 1308.3) * mm});
            skLineSegment(sketch, "E2376", {"start": v(814.35, 1308.3) * mm, "end": v(814.34, 1308.36) * mm});
            skLineSegment(sketch, "E2377", {"start": v(814.34, 1308.36) * mm, "end": v(814.33, 1308.43) * mm});
            skLineSegment(sketch, "E2378", {"start": v(814.33, 1308.43) * mm, "end": v(814.33, 1308.5) * mm});
            skLineSegment(sketch, "E2379", {"start": v(814.33, 1308.5) * mm, "end": v(814.33, 1308.57) * mm});
            skLineSegment(sketch, "E2380", {"start": v(814.33, 1308.57) * mm, "end": v(814.32, 1308.64) * mm});
            skLineSegment(sketch, "E2381", {"start": v(814.32, 1308.64) * mm, "end": v(814.32, 1308.7) * mm});
            skLineSegment(sketch, "E2382", {"start": v(814.32, 1308.7) * mm, "end": v(814.33, 1308.77) * mm});
            skLineSegment(sketch, "E2383", {"start": v(814.33, 1308.77) * mm, "end": v(814.33, 1308.84) * mm});
            skLineSegment(sketch, "E2384", {"start": v(814.33, 1308.84) * mm, "end": v(814.34, 1308.9) * mm});
            skLineSegment(sketch, "E2385", {"start": v(814.34, 1308.9) * mm, "end": v(814.34, 1308.97) * mm});
            skLineSegment(sketch, "E2386", {"start": v(814.34, 1308.97) * mm, "end": v(814.7, 1310.2) * mm});
            skLineSegment(sketch, "E2387", {"start": v(814.7, 1310.2) * mm, "end": v(813.25, 1310.8) * mm});
            skLineSegment(sketch, "E2388", {"start": v(813.25, 1310.8) * mm, "end": v(812.63, 1309.68) * mm});
            skLineSegment(sketch, "E2389", {"start": v(812.63, 1309.68) * mm, "end": v(812.58, 1309.63) * mm});
            skLineSegment(sketch, "E2390", {"start": v(812.58, 1309.63) * mm, "end": v(812.54, 1309.58) * mm});
            skLineSegment(sketch, "E2391", {"start": v(812.54, 1309.58) * mm, "end": v(812.5, 1309.53) * mm});
            skLineSegment(sketch, "E2392", {"start": v(812.5, 1309.53) * mm, "end": v(812.45, 1309.48) * mm});
            skLineSegment(sketch, "E2393", {"start": v(812.45, 1309.48) * mm, "end": v(812.4, 1309.44) * mm});
            skLineSegment(sketch, "E2394", {"start": v(812.4, 1309.44) * mm, "end": v(812.35, 1309.39) * mm});
            skLineSegment(sketch, "E2395", {"start": v(812.35, 1309.39) * mm, "end": v(812.3, 1309.34) * mm});
            skLineSegment(sketch, "E2396", {"start": v(812.3, 1309.34) * mm, "end": v(812.25, 1309.3) * mm});
            skLineSegment(sketch, "E2397", {"start": v(812.25, 1309.3) * mm, "end": v(812.2, 1309.25) * mm});
            skLineSegment(sketch, "E2398", {"start": v(812.2, 1309.25) * mm, "end": v(812.14, 1309.2) * mm});
            skLineSegment(sketch, "E2399", {"start": v(812.14, 1309.2) * mm, "end": v(812.08, 1309.17) * mm});
            skLineSegment(sketch, "E2400", {"start": v(812.08, 1309.17) * mm, "end": v(812.02, 1309.13) * mm});
            skLineSegment(sketch, "E2401", {"start": v(812.02, 1309.13) * mm, "end": v(811.96, 1309.08) * mm});
            skLineSegment(sketch, "E2402", {"start": v(811.96, 1309.08) * mm, "end": v(811.9, 1309.04) * mm});
            skLineSegment(sketch, "E2403", {"start": v(811.9, 1309.04) * mm, "end": v(811.84, 1309) * mm});
            skLineSegment(sketch, "E2404", {"start": v(811.84, 1309) * mm, "end": v(811.77, 1308.97) * mm});
            skLineSegment(sketch, "E2405", {"start": v(811.77, 1308.97) * mm, "end": v(811.7, 1308.93) * mm});
            skLineSegment(sketch, "E2406", {"start": v(811.7, 1308.93) * mm, "end": v(811.64, 1308.9) * mm});
            skLineSegment(sketch, "E2407", {"start": v(811.64, 1308.9) * mm, "end": v(811.58, 1308.86) * mm});
            skLineSegment(sketch, "E2408", {"start": v(811.58, 1308.86) * mm, "end": v(811.5, 1308.82) * mm});
            skLineSegment(sketch, "E2409", {"start": v(811.5, 1308.82) * mm, "end": v(811.44, 1308.8) * mm});
            skLineSegment(sketch, "E2410", {"start": v(811.44, 1308.8) * mm, "end": v(811.37, 1308.76) * mm});
            skLineSegment(sketch, "E2411", {"start": v(811.37, 1308.76) * mm, "end": v(811.3, 1308.73) * mm});
            skLineSegment(sketch, "E2412", {"start": v(811.3, 1308.73) * mm, "end": v(811.23, 1308.7) * mm});
            skLineSegment(sketch, "E2413", {"start": v(811.23, 1308.7) * mm, "end": v(811.15, 1308.67) * mm});
            skLineSegment(sketch, "E2414", {"start": v(811.15, 1308.67) * mm, "end": v(811.08, 1308.64) * mm});
            skLineSegment(sketch, "E2415", {"start": v(811.08, 1308.64) * mm, "end": v(811, 1308.6) * mm});
            skLineSegment(sketch, "E2416", {"start": v(811, 1308.6) * mm, "end": v(810.93, 1308.58) * mm});
            skLineSegment(sketch, "E2417", {"start": v(810.93, 1308.58) * mm, "end": v(810.85, 1308.56) * mm});
            skLineSegment(sketch, "E2418", {"start": v(810.85, 1308.56) * mm, "end": v(810.77, 1308.53) * mm});
            skLineSegment(sketch, "E2419", {"start": v(810.77, 1308.53) * mm, "end": v(810.43, 1308.78) * mm});
            skLineSegment(sketch, "E2420", {"start": v(810.43, 1308.78) * mm, "end": v(810.1, 1309.05) * mm});
            skLineSegment(sketch, "E2421", {"start": v(810.1, 1309.05) * mm, "end": v(810.1, 1309.13) * mm});
            skLineSegment(sketch, "E2422", {"start": v(810.1, 1309.13) * mm, "end": v(810.1, 1309.21) * mm});
            skLineSegment(sketch, "E2423", {"start": v(810.1, 1309.21) * mm, "end": v(810.1, 1309.3) * mm});
            skLineSegment(sketch, "E2424", {"start": v(810.1, 1309.3) * mm, "end": v(810.12, 1309.37) * mm});
            skLineSegment(sketch, "E2425", {"start": v(810.12, 1309.37) * mm, "end": v(810.13, 1309.45) * mm});
            skLineSegment(sketch, "E2426", {"start": v(810.13, 1309.45) * mm, "end": v(810.14, 1309.53) * mm});
            skLineSegment(sketch, "E2427", {"start": v(810.14, 1309.53) * mm, "end": v(810.15, 1309.61) * mm});
            skLineSegment(sketch, "E2428", {"start": v(810.15, 1309.61) * mm, "end": v(810.16, 1309.69) * mm});
            skLineSegment(sketch, "E2429", {"start": v(810.16, 1309.69) * mm, "end": v(810.17, 1309.76) * mm});
            skLineSegment(sketch, "E2430", {"start": v(810.17, 1309.76) * mm, "end": v(810.19, 1309.84) * mm});
            skLineSegment(sketch, "E2431", {"start": v(810.19, 1309.84) * mm, "end": v(810.2, 1309.91) * mm});
            skLineSegment(sketch, "E2432", {"start": v(810.2, 1309.91) * mm, "end": v(810.22, 1309.99) * mm});
            skLineSegment(sketch, "E2433", {"start": v(810.22, 1309.99) * mm, "end": v(810.24, 1310.06) * mm});
            skLineSegment(sketch, "E2434", {"start": v(810.24, 1310.06) * mm, "end": v(810.26, 1310.13) * mm});
            skLineSegment(sketch, "E2435", {"start": v(810.26, 1310.13) * mm, "end": v(810.28, 1310.2) * mm});
            skLineSegment(sketch, "E2436", {"start": v(810.28, 1310.2) * mm, "end": v(810.3, 1310.27) * mm});
            skLineSegment(sketch, "E2437", {"start": v(810.3, 1310.27) * mm, "end": v(810.32, 1310.34) * mm});
            skLineSegment(sketch, "E2438", {"start": v(810.32, 1310.34) * mm, "end": v(810.34, 1310.41) * mm});
            skLineSegment(sketch, "E2439", {"start": v(810.34, 1310.41) * mm, "end": v(810.37, 1310.48) * mm});
            skLineSegment(sketch, "E2440", {"start": v(810.37, 1310.48) * mm, "end": v(810.4, 1310.54) * mm});
            skLineSegment(sketch, "E2441", {"start": v(810.4, 1310.54) * mm, "end": v(810.42, 1310.6) * mm});
            skLineSegment(sketch, "E2442", {"start": v(810.42, 1310.6) * mm, "end": v(810.45, 1310.67) * mm});
            skLineSegment(sketch, "E2443", {"start": v(810.45, 1310.67) * mm, "end": v(810.48, 1310.73) * mm});
            skLineSegment(sketch, "E2444", {"start": v(810.48, 1310.73) * mm, "end": v(810.51, 1310.8) * mm});
            skLineSegment(sketch, "E2445", {"start": v(810.51, 1310.8) * mm, "end": v(810.55, 1310.86) * mm});
            skLineSegment(sketch, "E2446", {"start": v(810.55, 1310.86) * mm, "end": v(810.58, 1310.92) * mm});
            skLineSegment(sketch, "E2447", {"start": v(810.58, 1310.92) * mm, "end": v(810.62, 1310.97) * mm});
            skLineSegment(sketch, "E2448", {"start": v(810.62, 1310.97) * mm, "end": v(810.65, 1311.03) * mm});
            skLineSegment(sketch, "E2449", {"start": v(810.65, 1311.03) * mm, "end": v(810.7, 1311.08) * mm});
            skLineSegment(sketch, "E2450", {"start": v(810.7, 1311.08) * mm, "end": v(810.73, 1311.14) * mm});
            skLineSegment(sketch, "E2451", {"start": v(810.73, 1311.14) * mm, "end": v(811.65, 1312.03) * mm});
            skLineSegment(sketch, "E2452", {"start": v(811.65, 1312.03) * mm, "end": v(810.7, 1313.27) * mm});
            skLineSegment(sketch, "E2453", {"start": v(810.7, 1313.27) * mm, "end": v(809.6, 1312.61) * mm});
            skLineSegment(sketch, "E2454", {"start": v(809.6, 1312.61) * mm, "end": v(809.54, 1312.6) * mm});
            skLineSegment(sketch, "E2455", {"start": v(809.54, 1312.6) * mm, "end": v(809.47, 1312.57) * mm});
            skLineSegment(sketch, "E2456", {"start": v(809.47, 1312.57) * mm, "end": v(809.4, 1312.55) * mm});
            skLineSegment(sketch, "E2457", {"start": v(809.4, 1312.55) * mm, "end": v(809.34, 1312.53) * mm});
            skLineSegment(sketch, "E2458", {"start": v(809.34, 1312.53) * mm, "end": v(809.28, 1312.51) * mm});
            skLineSegment(sketch, "E2459", {"start": v(809.28, 1312.51) * mm, "end": v(809.21, 1312.5) * mm});
            skLineSegment(sketch, "E2460", {"start": v(809.21, 1312.5) * mm, "end": v(809.14, 1312.48) * mm});
            skLineSegment(sketch, "E2461", {"start": v(809.14, 1312.48) * mm, "end": v(809.08, 1312.47) * mm});
            skLineSegment(sketch, "E2462", {"start": v(809.08, 1312.47) * mm, "end": v(809, 1312.46) * mm});
            skLineSegment(sketch, "E2463", {"start": v(809, 1312.46) * mm, "end": v(808.94, 1312.45) * mm});
            skLineSegment(sketch, "E2464", {"start": v(808.94, 1312.45) * mm, "end": v(808.87, 1312.44) * mm});
            skLineSegment(sketch, "E2465", {"start": v(808.87, 1312.44) * mm, "end": v(808.8, 1312.43) * mm});
            skLineSegment(sketch, "E2466", {"start": v(808.8, 1312.43) * mm, "end": v(808.72, 1312.43) * mm});
            skLineSegment(sketch, "E2467", {"start": v(808.72, 1312.43) * mm, "end": v(808.65, 1312.42) * mm});
            skLineSegment(sketch, "E2468", {"start": v(808.65, 1312.42) * mm, "end": v(808.58, 1312.42) * mm});
            skLineSegment(sketch, "E2469", {"start": v(808.58, 1312.42) * mm, "end": v(808.5, 1312.42) * mm});
            skLineSegment(sketch, "E2470", {"start": v(808.5, 1312.42) * mm, "end": v(808.43, 1312.42) * mm});
            skLineSegment(sketch, "E2471", {"start": v(808.43, 1312.42) * mm, "end": v(808.35, 1312.42) * mm});
            skLineSegment(sketch, "E2472", {"start": v(808.35, 1312.42) * mm, "end": v(808.28, 1312.42) * mm});
            skLineSegment(sketch, "E2473", {"start": v(808.28, 1312.42) * mm, "end": v(808.2, 1312.43) * mm});
            skLineSegment(sketch, "E2474", {"start": v(808.2, 1312.43) * mm, "end": v(808.13, 1312.43) * mm});
            skLineSegment(sketch, "E2475", {"start": v(808.13, 1312.43) * mm, "end": v(808.05, 1312.44) * mm});
            skLineSegment(sketch, "E2476", {"start": v(808.05, 1312.44) * mm, "end": v(807.97, 1312.45) * mm});
            skLineSegment(sketch, "E2477", {"start": v(807.97, 1312.45) * mm, "end": v(807.9, 1312.46) * mm});
            skLineSegment(sketch, "E2478", {"start": v(807.9, 1312.46) * mm, "end": v(807.81, 1312.47) * mm});
            skLineSegment(sketch, "E2479", {"start": v(807.81, 1312.47) * mm, "end": v(807.73, 1312.48) * mm});
            skLineSegment(sketch, "E2480", {"start": v(807.73, 1312.48) * mm, "end": v(807.66, 1312.5) * mm});
            skLineSegment(sketch, "E2481", {"start": v(807.66, 1312.5) * mm, "end": v(807.58, 1312.5) * mm});
            skLineSegment(sketch, "E2482", {"start": v(807.58, 1312.5) * mm, "end": v(807.5, 1312.52) * mm});
            skLineSegment(sketch, "E2483", {"start": v(807.5, 1312.52) * mm, "end": v(807.42, 1312.54) * mm});
            skLineSegment(sketch, "E2484", {"start": v(807.42, 1312.54) * mm, "end": v(807.24, 1312.93) * mm});
            skLineSegment(sketch, "E2485", {"start": v(807.24, 1312.93) * mm, "end": v(807.09, 1313.33) * mm});
            skLineSegment(sketch, "E2486", {"start": v(807.09, 1313.33) * mm, "end": v(807.13, 1313.4) * mm});
            skLineSegment(sketch, "E2487", {"start": v(807.13, 1313.4) * mm, "end": v(807.18, 1313.47) * mm});
            skLineSegment(sketch, "E2488", {"start": v(807.18, 1313.47) * mm, "end": v(807.22, 1313.53) * mm});
            skLineSegment(sketch, "E2489", {"start": v(807.22, 1313.53) * mm, "end": v(807.27, 1313.6) * mm});
            skLineSegment(sketch, "E2490", {"start": v(807.27, 1313.6) * mm, "end": v(807.32, 1313.66) * mm});
            skLineSegment(sketch, "E2491", {"start": v(807.32, 1313.66) * mm, "end": v(807.37, 1313.73) * mm});
            skLineSegment(sketch, "E2492", {"start": v(807.37, 1313.73) * mm, "end": v(807.42, 1313.79) * mm});
            skLineSegment(sketch, "E2493", {"start": v(807.42, 1313.79) * mm, "end": v(807.46, 1313.85) * mm});
            skLineSegment(sketch, "E2494", {"start": v(807.46, 1313.85) * mm, "end": v(807.51, 1313.9) * mm});
            skLineSegment(sketch, "E2495", {"start": v(807.51, 1313.9) * mm, "end": v(807.56, 1313.97) * mm});
            skLineSegment(sketch, "E2496", {"start": v(807.56, 1313.97) * mm, "end": v(807.62, 1314.02) * mm});
            skLineSegment(sketch, "E2497", {"start": v(807.62, 1314.02) * mm, "end": v(807.67, 1314.08) * mm});
            skLineSegment(sketch, "E2498", {"start": v(807.67, 1314.08) * mm, "end": v(807.72, 1314.13) * mm});
            skLineSegment(sketch, "E2499", {"start": v(807.72, 1314.13) * mm, "end": v(807.77, 1314.18) * mm});
            skLineSegment(sketch, "E2500", {"start": v(807.77, 1314.18) * mm, "end": v(807.82, 1314.24) * mm});
            skLineSegment(sketch, "E2501", {"start": v(807.82, 1314.24) * mm, "end": v(807.88, 1314.29) * mm});
            skLineSegment(sketch, "E2502", {"start": v(807.88, 1314.29) * mm, "end": v(807.93, 1314.33) * mm});
            skLineSegment(sketch, "E2503", {"start": v(807.93, 1314.33) * mm, "end": v(807.99, 1314.38) * mm});
            skLineSegment(sketch, "E2504", {"start": v(807.99, 1314.38) * mm, "end": v(808.04, 1314.43) * mm});
            skLineSegment(sketch, "E2505", {"start": v(808.04, 1314.43) * mm, "end": v(808.1, 1314.47) * mm});
            skLineSegment(sketch, "E2506", {"start": v(808.1, 1314.47) * mm, "end": v(808.15, 1314.51) * mm});
            skLineSegment(sketch, "E2507", {"start": v(808.15, 1314.51) * mm, "end": v(808.21, 1314.55) * mm});
            skLineSegment(sketch, "E2508", {"start": v(808.21, 1314.55) * mm, "end": v(808.27, 1314.6) * mm});
            skLineSegment(sketch, "E2509", {"start": v(808.27, 1314.6) * mm, "end": v(808.33, 1314.63) * mm});
            skLineSegment(sketch, "E2510", {"start": v(808.33, 1314.63) * mm, "end": v(808.39, 1314.67) * mm});
            skLineSegment(sketch, "E2511", {"start": v(808.39, 1314.67) * mm, "end": v(808.44, 1314.7) * mm});
            skLineSegment(sketch, "E2512", {"start": v(808.44, 1314.7) * mm, "end": v(808.5, 1314.73) * mm});
            skLineSegment(sketch, "E2513", {"start": v(808.5, 1314.73) * mm, "end": v(808.56, 1314.76) * mm});
            skLineSegment(sketch, "E2514", {"start": v(808.56, 1314.76) * mm, "end": v(808.62, 1314.8) * mm});
            skLineSegment(sketch, "E2515", {"start": v(808.62, 1314.8) * mm, "end": v(808.68, 1314.82) * mm});
            skLineSegment(sketch, "E2516", {"start": v(808.68, 1314.82) * mm, "end": v(809.93, 1315.13) * mm});
            skLineSegment(sketch, "E2517", {"start": v(809.93, 1315.13) * mm, "end": v(809.72, 1316.68) * mm});
            skLineSegment(sketch, "E2518", {"start": v(809.72, 1316.68) * mm, "end": v(808.44, 1316.66) * mm});
            skLineSegment(sketch, "E2519", {"start": v(808.44, 1316.66) * mm, "end": v(808.38, 1316.68) * mm});
            skLineSegment(sketch, "E2520", {"start": v(808.38, 1316.68) * mm, "end": v(808.31, 1316.69) * mm});
            skLineSegment(sketch, "E2521", {"start": v(808.31, 1316.69) * mm, "end": v(808.24, 1316.7) * mm});
            skLineSegment(sketch, "E2522", {"start": v(808.24, 1316.7) * mm, "end": v(808.18, 1316.72) * mm});
            skLineSegment(sketch, "E2523", {"start": v(808.18, 1316.72) * mm, "end": v(808.11, 1316.73) * mm});
            skLineSegment(sketch, "E2524", {"start": v(808.11, 1316.73) * mm, "end": v(808.05, 1316.75) * mm});
            skLineSegment(sketch, "E2525", {"start": v(808.05, 1316.75) * mm, "end": v(807.98, 1316.77) * mm});
            skLineSegment(sketch, "E2526", {"start": v(807.98, 1316.77) * mm, "end": v(807.92, 1316.8) * mm});
            skLineSegment(sketch, "E2527", {"start": v(807.92, 1316.8) * mm, "end": v(807.85, 1316.82) * mm});
            skLineSegment(sketch, "E2528", {"start": v(807.85, 1316.82) * mm, "end": v(807.79, 1316.85) * mm});
            skLineSegment(sketch, "E2529", {"start": v(807.79, 1316.85) * mm, "end": v(807.72, 1316.88) * mm});
            skLineSegment(sketch, "E2530", {"start": v(807.72, 1316.88) * mm, "end": v(807.66, 1316.9) * mm});
            skLineSegment(sketch, "E2531", {"start": v(807.66, 1316.9) * mm, "end": v(807.59, 1316.94) * mm});
            skLineSegment(sketch, "E2532", {"start": v(807.59, 1316.94) * mm, "end": v(807.52, 1316.97) * mm});
            skLineSegment(sketch, "E2533", {"start": v(807.52, 1316.97) * mm, "end": v(807.46, 1317) * mm});
            skLineSegment(sketch, "E2534", {"start": v(807.46, 1317) * mm, "end": v(807.4, 1317.04) * mm});
            skLineSegment(sketch, "E2535", {"start": v(807.4, 1317.04) * mm, "end": v(807.33, 1317.08) * mm});
            skLineSegment(sketch, "E2536", {"start": v(807.33, 1317.08) * mm, "end": v(807.27, 1317.12) * mm});
            skLineSegment(sketch, "E2537", {"start": v(807.27, 1317.12) * mm, "end": v(807.2, 1317.16) * mm});
            skLineSegment(sketch, "E2538", {"start": v(807.2, 1317.16) * mm, "end": v(807.14, 1317.2) * mm});
            skLineSegment(sketch, "E2539", {"start": v(807.14, 1317.2) * mm, "end": v(807.08, 1317.24) * mm});
            skLineSegment(sketch, "E2540", {"start": v(807.08, 1317.24) * mm, "end": v(807.01, 1317.29) * mm});
            skLineSegment(sketch, "E2541", {"start": v(807.01, 1317.29) * mm, "end": v(806.95, 1317.33) * mm});
            skLineSegment(sketch, "E2542", {"start": v(806.95, 1317.33) * mm, "end": v(806.89, 1317.38) * mm});
            skLineSegment(sketch, "E2543", {"start": v(806.89, 1317.38) * mm, "end": v(806.82, 1317.43) * mm});
            skLineSegment(sketch, "E2544", {"start": v(806.82, 1317.43) * mm, "end": v(806.76, 1317.48) * mm});
            skLineSegment(sketch, "E2545", {"start": v(806.76, 1317.48) * mm, "end": v(806.7, 1317.53) * mm});
            skLineSegment(sketch, "E2546", {"start": v(806.7, 1317.53) * mm, "end": v(806.64, 1317.58) * mm});
            skLineSegment(sketch, "E2547", {"start": v(806.64, 1317.58) * mm, "end": v(806.58, 1317.64) * mm});
            skLineSegment(sketch, "E2548", {"start": v(806.58, 1317.64) * mm, "end": v(806.51, 1317.7) * mm});
            skLineSegment(sketch, "E2549", {"start": v(806.51, 1317.7) * mm, "end": v(806.56, 1318.12) * mm});
            skLineSegment(sketch, "E2550", {"start": v(806.56, 1318.12) * mm, "end": v(806.63, 1318.54) * mm});
            skLineSegment(sketch, "E2551", {"start": v(806.63, 1318.54) * mm, "end": v(806.7, 1318.57) * mm});
            skLineSegment(sketch, "E2552", {"start": v(806.7, 1318.57) * mm, "end": v(806.77, 1318.6) * mm});
            skLineSegment(sketch, "E2553", {"start": v(806.77, 1318.6) * mm, "end": v(806.85, 1318.64) * mm});
            skLineSegment(sketch, "E2554", {"start": v(806.85, 1318.64) * mm, "end": v(806.92, 1318.68) * mm});
            skLineSegment(sketch, "E2555", {"start": v(806.92, 1318.68) * mm, "end": v(807, 1318.71) * mm});
            skLineSegment(sketch, "E2556", {"start": v(807, 1318.71) * mm, "end": v(807.06, 1318.74) * mm});
            skLineSegment(sketch, "E2557", {"start": v(807.06, 1318.74) * mm, "end": v(807.14, 1318.77) * mm});
            skLineSegment(sketch, "E2558", {"start": v(807.14, 1318.77) * mm, "end": v(807.21, 1318.8) * mm});
            skLineSegment(sketch, "E2559", {"start": v(807.21, 1318.8) * mm, "end": v(807.28, 1318.83) * mm});
            skLineSegment(sketch, "E2560", {"start": v(807.28, 1318.83) * mm, "end": v(807.36, 1318.85) * mm});
            skLineSegment(sketch, "E2561", {"start": v(807.36, 1318.85) * mm, "end": v(807.43, 1318.87) * mm});
            skLineSegment(sketch, "E2562", {"start": v(807.43, 1318.87) * mm, "end": v(807.5, 1318.9) * mm});
            skLineSegment(sketch, "E2563", {"start": v(807.5, 1318.9) * mm, "end": v(807.57, 1318.92) * mm});
            skLineSegment(sketch, "E2564", {"start": v(807.57, 1318.92) * mm, "end": v(807.64, 1318.94) * mm});
            skLineSegment(sketch, "E2565", {"start": v(807.64, 1318.94) * mm, "end": v(807.72, 1318.95) * mm});
            skLineSegment(sketch, "E2566", {"start": v(807.72, 1318.95) * mm, "end": v(807.79, 1318.97) * mm});
            skLineSegment(sketch, "E2567", {"start": v(807.79, 1318.97) * mm, "end": v(807.86, 1318.99) * mm});
            skLineSegment(sketch, "E2568", {"start": v(807.86, 1318.99) * mm, "end": v(807.93, 1319) * mm});
            skLineSegment(sketch, "E2569", {"start": v(807.93, 1319) * mm, "end": v(808, 1319.01) * mm});
            skLineSegment(sketch, "E2570", {"start": v(808, 1319.01) * mm, "end": v(808.07, 1319.02) * mm});
            skLineSegment(sketch, "E2571", {"start": v(808.07, 1319.02) * mm, "end": v(808.14, 1319.03) * mm});
            skLineSegment(sketch, "E2572", {"start": v(808.14, 1319.03) * mm, "end": v(808.21, 1319.04) * mm});
            skLineSegment(sketch, "E2573", {"start": v(808.21, 1319.04) * mm, "end": v(808.28, 1319.04) * mm});
            skLineSegment(sketch, "E2574", {"start": v(808.28, 1319.04) * mm, "end": v(808.35, 1319.05) * mm});
            skLineSegment(sketch, "E2575", {"start": v(808.35, 1319.05) * mm, "end": v(808.42, 1319.05) * mm});
            skLineSegment(sketch, "E2576", {"start": v(808.42, 1319.05) * mm, "end": v(808.49, 1319.05) * mm});
            skLineSegment(sketch, "E2577", {"start": v(808.49, 1319.05) * mm, "end": v(808.55, 1319.05) * mm});
            skLineSegment(sketch, "E2578", {"start": v(808.55, 1319.05) * mm, "end": v(808.62, 1319.04) * mm});
            skLineSegment(sketch, "E2579", {"start": v(808.62, 1319.04) * mm, "end": v(808.69, 1319.04) * mm});
            skLineSegment(sketch, "E2580", {"start": v(808.69, 1319.04) * mm, "end": v(808.75, 1319.03) * mm});
            skLineSegment(sketch, "E2581", {"start": v(808.75, 1319.03) * mm, "end": v(809.99, 1318.68) * mm});
            skLineSegment(sketch, "E2582", {"start": v(809.99, 1318.68) * mm, "end": v(810.58, 1320.12) * mm});
            skLineSegment(sketch, "E2583", {"start": v(810.58, 1320.12) * mm, "end": v(809.46, 1320.74) * mm});
            skLineSegment(sketch, "E2584", {"start": v(809.46, 1320.74) * mm, "end": v(809.41, 1320.8) * mm});
            skLineSegment(sketch, "E2585", {"start": v(809.41, 1320.8) * mm, "end": v(809.36, 1320.83) * mm});
            skLineSegment(sketch, "E2586", {"start": v(809.36, 1320.83) * mm, "end": v(809.31, 1320.88) * mm});
            skLineSegment(sketch, "E2587", {"start": v(809.31, 1320.88) * mm, "end": v(809.26, 1320.92) * mm});
            skLineSegment(sketch, "E2588", {"start": v(809.26, 1320.92) * mm, "end": v(809.21, 1320.97) * mm});
            skLineSegment(sketch, "E2589", {"start": v(809.21, 1320.97) * mm, "end": v(809.17, 1321.02) * mm});
            skLineSegment(sketch, "E2590", {"start": v(809.17, 1321.02) * mm, "end": v(809.12, 1321.07) * mm});
            skLineSegment(sketch, "E2591", {"start": v(809.12, 1321.07) * mm, "end": v(809.08, 1321.13) * mm});
            skLineSegment(sketch, "E2592", {"start": v(809.08, 1321.13) * mm, "end": v(809.03, 1321.18) * mm});
            skLineSegment(sketch, "E2593", {"start": v(809.03, 1321.18) * mm, "end": v(808.99, 1321.24) * mm});
            skLineSegment(sketch, "E2594", {"start": v(808.99, 1321.24) * mm, "end": v(808.95, 1321.3) * mm});
            skLineSegment(sketch, "E2595", {"start": v(808.95, 1321.3) * mm, "end": v(808.9, 1321.35) * mm});
            skLineSegment(sketch, "E2596", {"start": v(808.9, 1321.35) * mm, "end": v(808.86, 1321.41) * mm});
            skLineSegment(sketch, "E2597", {"start": v(808.86, 1321.41) * mm, "end": v(808.82, 1321.47) * mm});
            skLineSegment(sketch, "E2598", {"start": v(808.82, 1321.47) * mm, "end": v(808.79, 1321.53) * mm});
            skLineSegment(sketch, "E2599", {"start": v(808.79, 1321.53) * mm, "end": v(808.75, 1321.6) * mm});
            skLineSegment(sketch, "E2600", {"start": v(808.75, 1321.6) * mm, "end": v(808.71, 1321.66) * mm});
            skLineSegment(sketch, "E2601", {"start": v(808.71, 1321.66) * mm, "end": v(808.67, 1321.73) * mm});
            skLineSegment(sketch, "E2602", {"start": v(808.67, 1321.73) * mm, "end": v(808.64, 1321.8) * mm});
            skLineSegment(sketch, "E2603", {"start": v(808.64, 1321.8) * mm, "end": v(808.6, 1321.86) * mm});
            skLineSegment(sketch, "E2604", {"start": v(808.6, 1321.86) * mm, "end": v(808.57, 1321.93) * mm});
            skLineSegment(sketch, "E2605", {"start": v(808.57, 1321.93) * mm, "end": v(808.54, 1322) * mm});
            skLineSegment(sketch, "E2606", {"start": v(808.54, 1322) * mm, "end": v(808.5, 1322.07) * mm});
            skLineSegment(sketch, "E2607", {"start": v(808.5, 1322.07) * mm, "end": v(808.48, 1322.14) * mm});
            skLineSegment(sketch, "E2608", {"start": v(808.48, 1322.14) * mm, "end": v(808.44, 1322.22) * mm});
            skLineSegment(sketch, "E2609", {"start": v(808.44, 1322.22) * mm, "end": v(808.42, 1322.3) * mm});
            skLineSegment(sketch, "E2610", {"start": v(808.42, 1322.3) * mm, "end": v(808.39, 1322.37) * mm});
            skLineSegment(sketch, "E2611", {"start": v(808.39, 1322.37) * mm, "end": v(808.36, 1322.45) * mm});
            skLineSegment(sketch, "E2612", {"start": v(808.36, 1322.45) * mm, "end": v(808.33, 1322.52) * mm});
            skLineSegment(sketch, "E2613", {"start": v(808.33, 1322.52) * mm, "end": v(808.31, 1322.6) * mm});
            skLineSegment(sketch, "E2614", {"start": v(808.31, 1322.6) * mm, "end": v(808.56, 1322.95) * mm});
            skLineSegment(sketch, "E2615", {"start": v(808.56, 1322.95) * mm, "end": v(808.83, 1323.28) * mm});
            skLineSegment(sketch, "E2616", {"start": v(808.83, 1323.28) * mm, "end": v(808.91, 1323.27) * mm});
            skLineSegment(sketch, "E2617", {"start": v(808.91, 1323.27) * mm, "end": v(809, 1323.27) * mm});
            skLineSegment(sketch, "E2618", {"start": v(809, 1323.27) * mm, "end": v(809.07, 1323.26) * mm});
            skLineSegment(sketch, "E2619", {"start": v(809.07, 1323.26) * mm, "end": v(809.15, 1323.26) * mm});
            skLineSegment(sketch, "E2620", {"start": v(809.15, 1323.26) * mm, "end": v(809.23, 1323.25) * mm});
            skLineSegment(sketch, "E2621", {"start": v(809.23, 1323.25) * mm, "end": v(809.31, 1323.24) * mm});
            skLineSegment(sketch, "E2622", {"start": v(809.31, 1323.24) * mm, "end": v(809.4, 1323.23) * mm});
            skLineSegment(sketch, "E2623", {"start": v(809.4, 1323.23) * mm, "end": v(809.47, 1323.21) * mm});
            skLineSegment(sketch, "E2624", {"start": v(809.47, 1323.21) * mm, "end": v(809.54, 1323.2) * mm});
            skLineSegment(sketch, "E2625", {"start": v(809.54, 1323.2) * mm, "end": v(809.62, 1323.18) * mm});
            skLineSegment(sketch, "E2626", {"start": v(809.62, 1323.18) * mm, "end": v(809.7, 1323.17) * mm});
            skLineSegment(sketch, "E2627", {"start": v(809.7, 1323.17) * mm, "end": v(809.77, 1323.15) * mm});
            skLineSegment(sketch, "E2628", {"start": v(809.77, 1323.15) * mm, "end": v(809.84, 1323.13) * mm});
            skLineSegment(sketch, "E2629", {"start": v(809.84, 1323.13) * mm, "end": v(809.91, 1323.12) * mm});
            skLineSegment(sketch, "E2630", {"start": v(809.91, 1323.12) * mm, "end": v(809.98, 1323.1) * mm});
            skLineSegment(sketch, "E2631", {"start": v(809.98, 1323.1) * mm, "end": v(810.05, 1323.07) * mm});
            skLineSegment(sketch, "E2632", {"start": v(810.05, 1323.07) * mm, "end": v(810.12, 1323.05) * mm});
            skLineSegment(sketch, "E2633", {"start": v(810.12, 1323.05) * mm, "end": v(810.2, 1323.03) * mm});
            skLineSegment(sketch, "E2634", {"start": v(810.2, 1323.03) * mm, "end": v(810.26, 1323) * mm});
            skLineSegment(sketch, "E2635", {"start": v(810.26, 1323) * mm, "end": v(810.32, 1322.98) * mm});
            skLineSegment(sketch, "E2636", {"start": v(810.32, 1322.98) * mm, "end": v(810.39, 1322.95) * mm});
            skLineSegment(sketch, "E2637", {"start": v(810.39, 1322.95) * mm, "end": v(810.45, 1322.92) * mm});
            skLineSegment(sketch, "E2638", {"start": v(810.45, 1322.92) * mm, "end": v(810.51, 1322.89) * mm});
            skLineSegment(sketch, "E2639", {"start": v(810.51, 1322.89) * mm, "end": v(810.58, 1322.86) * mm});
            skLineSegment(sketch, "E2640", {"start": v(810.58, 1322.86) * mm, "end": v(810.64, 1322.82) * mm});
            skLineSegment(sketch, "E2641", {"start": v(810.64, 1322.82) * mm, "end": v(810.7, 1322.8) * mm});
            skLineSegment(sketch, "E2642", {"start": v(810.7, 1322.8) * mm, "end": v(810.75, 1322.76) * mm});
            skLineSegment(sketch, "E2643", {"start": v(810.75, 1322.76) * mm, "end": v(810.8, 1322.72) * mm});
            skLineSegment(sketch, "E2644", {"start": v(810.8, 1322.72) * mm, "end": v(810.86, 1322.68) * mm});
            skLineSegment(sketch, "E2645", {"start": v(810.86, 1322.68) * mm, "end": v(810.92, 1322.65) * mm});
            skLineSegment(sketch, "E2646", {"start": v(810.92, 1322.65) * mm, "end": v(811.81, 1321.72) * mm});
            skLineSegment(sketch, "E2647", {"start": v(811.81, 1321.72) * mm, "end": v(813.05, 1322.67) * mm});
            skLineSegment(sketch, "E2648", {"start": v(813.05, 1322.67) * mm, "end": v(812.39, 1323.77) * mm});
            skLineSegment(sketch, "E2649", {"start": v(812.39, 1323.77) * mm, "end": v(812.37, 1323.84) * mm});
            skLineSegment(sketch, "E2650", {"start": v(812.37, 1323.84) * mm, "end": v(812.35, 1323.9) * mm});
            skLineSegment(sketch, "E2651", {"start": v(812.35, 1323.9) * mm, "end": v(812.33, 1323.96) * mm});
            skLineSegment(sketch, "E2652", {"start": v(812.33, 1323.96) * mm, "end": v(812.3, 1324.03) * mm});
            skLineSegment(sketch, "E2653", {"start": v(812.3, 1324.03) * mm, "end": v(812.29, 1324.1) * mm});
            skLineSegment(sketch, "E2654", {"start": v(812.29, 1324.1) * mm, "end": v(812.27, 1324.16) * mm});
            skLineSegment(sketch, "E2655", {"start": v(812.27, 1324.16) * mm, "end": v(812.26, 1324.23) * mm});
            skLineSegment(sketch, "E2656", {"start": v(812.26, 1324.23) * mm, "end": v(812.25, 1324.3) * mm});
            skLineSegment(sketch, "E2657", {"start": v(812.25, 1324.3) * mm, "end": v(812.23, 1324.37) * mm});
            skLineSegment(sketch, "E2658", {"start": v(812.23, 1324.37) * mm, "end": v(812.23, 1324.44) * mm});
            skLineSegment(sketch, "E2659", {"start": v(812.23, 1324.44) * mm, "end": v(812.22, 1324.5) * mm});
            skLineSegment(sketch, "E2660", {"start": v(812.22, 1324.5) * mm, "end": v(812.21, 1324.58) * mm});
            skLineSegment(sketch, "E2661", {"start": v(812.21, 1324.58) * mm, "end": v(812.2, 1324.65) * mm});
            skLineSegment(sketch, "E2662", {"start": v(812.2, 1324.65) * mm, "end": v(812.2, 1324.72) * mm});
            skLineSegment(sketch, "E2663", {"start": v(812.2, 1324.72) * mm, "end": v(812.2, 1324.8) * mm});
            skLineSegment(sketch, "E2664", {"start": v(812.2, 1324.8) * mm, "end": v(812.2, 1324.87) * mm});
            skLineSegment(sketch, "E2665", {"start": v(812.2, 1324.87) * mm, "end": v(812.2, 1324.94) * mm});
            skLineSegment(sketch, "E2666", {"start": v(812.2, 1324.94) * mm, "end": v(812.2, 1325.02) * mm});
            skLineSegment(sketch, "E2667", {"start": v(812.2, 1325.02) * mm, "end": v(812.2, 1325.1) * mm});
            skLineSegment(sketch, "E2668", {"start": v(812.2, 1325.1) * mm, "end": v(812.2, 1325.17) * mm});
            skLineSegment(sketch, "E2669", {"start": v(812.2, 1325.17) * mm, "end": v(812.21, 1325.25) * mm});
            skLineSegment(sketch, "E2670", {"start": v(812.21, 1325.25) * mm, "end": v(812.22, 1325.32) * mm});
            skLineSegment(sketch, "E2671", {"start": v(812.22, 1325.32) * mm, "end": v(812.23, 1325.4) * mm});
            skLineSegment(sketch, "E2672", {"start": v(812.23, 1325.4) * mm, "end": v(812.23, 1325.48) * mm});
            skLineSegment(sketch, "E2673", {"start": v(812.23, 1325.48) * mm, "end": v(812.25, 1325.56) * mm});
            skLineSegment(sketch, "E2674", {"start": v(812.25, 1325.56) * mm, "end": v(812.26, 1325.64) * mm});
            skLineSegment(sketch, "E2675", {"start": v(812.26, 1325.64) * mm, "end": v(812.27, 1325.72) * mm});
            skLineSegment(sketch, "E2676", {"start": v(812.27, 1325.72) * mm, "end": v(812.29, 1325.8) * mm});
            skLineSegment(sketch, "E2677", {"start": v(812.29, 1325.8) * mm, "end": v(812.3, 1325.88) * mm});
            skLineSegment(sketch, "E2678", {"start": v(812.3, 1325.88) * mm, "end": v(812.32, 1325.96) * mm});
            skLineSegment(sketch, "E2679", {"start": v(812.32, 1325.96) * mm, "end": v(812.7, 1326.13) * mm});
            skLineSegment(sketch, "E2680", {"start": v(812.7, 1326.13) * mm, "end": v(813.1, 1326.28) * mm});
            skLineSegment(sketch, "E2681", {"start": v(813.1, 1326.28) * mm, "end": v(813.18, 1326.24) * mm});
            skLineSegment(sketch, "E2682", {"start": v(813.18, 1326.24) * mm, "end": v(813.24, 1326.2) * mm});
            skLineSegment(sketch, "E2683", {"start": v(813.24, 1326.2) * mm, "end": v(813.31, 1326.15) * mm});
            skLineSegment(sketch, "E2684", {"start": v(813.31, 1326.15) * mm, "end": v(813.38, 1326.1) * mm});
            skLineSegment(sketch, "E2685", {"start": v(813.38, 1326.1) * mm, "end": v(813.44, 1326.05) * mm});
            skLineSegment(sketch, "E2686", {"start": v(813.44, 1326.05) * mm, "end": v(813.5, 1326) * mm});
            skLineSegment(sketch, "E2687", {"start": v(813.5, 1326) * mm, "end": v(813.57, 1325.96) * mm});
            skLineSegment(sketch, "E2688", {"start": v(813.57, 1325.96) * mm, "end": v(813.63, 1325.9) * mm});
            skLineSegment(sketch, "E2689", {"start": v(813.63, 1325.9) * mm, "end": v(813.69, 1325.86) * mm});
            skLineSegment(sketch, "E2690", {"start": v(813.69, 1325.86) * mm, "end": v(813.75, 1325.8) * mm});
            skLineSegment(sketch, "E2691", {"start": v(813.75, 1325.8) * mm, "end": v(813.8, 1325.76) * mm});
            skLineSegment(sketch, "E2692", {"start": v(813.8, 1325.76) * mm, "end": v(813.86, 1325.7) * mm});
            skLineSegment(sketch, "E2693", {"start": v(813.86, 1325.7) * mm, "end": v(813.91, 1325.65) * mm});
            skLineSegment(sketch, "E2694", {"start": v(813.91, 1325.65) * mm, "end": v(813.96, 1325.6) * mm});
            skLineSegment(sketch, "E2695", {"start": v(813.96, 1325.6) * mm, "end": v(814.02, 1325.55) * mm});
            skLineSegment(sketch, "E2696", {"start": v(814.02, 1325.55) * mm, "end": v(814.07, 1325.5) * mm});
            skLineSegment(sketch, "E2697", {"start": v(814.07, 1325.5) * mm, "end": v(814.11, 1325.44) * mm});
            skLineSegment(sketch, "E2698", {"start": v(814.11, 1325.44) * mm, "end": v(814.16, 1325.39) * mm});
            skLineSegment(sketch, "E2699", {"start": v(814.16, 1325.39) * mm, "end": v(814.2, 1325.33) * mm});
            skLineSegment(sketch, "E2700", {"start": v(814.2, 1325.33) * mm, "end": v(814.25, 1325.27) * mm});
            skLineSegment(sketch, "E2701", {"start": v(814.25, 1325.27) * mm, "end": v(814.3, 1325.22) * mm});
            skLineSegment(sketch, "E2702", {"start": v(814.3, 1325.22) * mm, "end": v(814.33, 1325.16) * mm});
            skLineSegment(sketch, "E2703", {"start": v(814.33, 1325.16) * mm, "end": v(814.37, 1325.1) * mm});
            skLineSegment(sketch, "E2704", {"start": v(814.37, 1325.1) * mm, "end": v(814.41, 1325.04) * mm});
            skLineSegment(sketch, "E2705", {"start": v(814.41, 1325.04) * mm, "end": v(814.45, 1324.99) * mm});
            skLineSegment(sketch, "E2706", {"start": v(814.45, 1324.99) * mm, "end": v(814.48, 1324.93) * mm});
            skLineSegment(sketch, "E2707", {"start": v(814.48, 1324.93) * mm, "end": v(814.51, 1324.87) * mm});
            skLineSegment(sketch, "E2708", {"start": v(814.51, 1324.87) * mm, "end": v(814.54, 1324.8) * mm});
            skLineSegment(sketch, "E2709", {"start": v(814.54, 1324.8) * mm, "end": v(814.57, 1324.75) * mm});
            skLineSegment(sketch, "E2710", {"start": v(814.57, 1324.75) * mm, "end": v(814.6, 1324.69) * mm});
            skLineSegment(sketch, "E2711", {"start": v(814.6, 1324.69) * mm, "end": v(814.91, 1323.45) * mm});
            skLineSegment(sketch, "E2712", {"start": v(814.91, 1323.45) * mm, "end": v(816.46, 1323.65) * mm});
            skLineSegment(sketch, "E2713", {"start": v(816.46, 1323.65) * mm, "end": v(816.44, 1324.93) * mm});
            skLineSegment(sketch, "E2714", {"start": v(816.44, 1324.93) * mm, "end": v(816.45, 1325) * mm});
            skLineSegment(sketch, "E2715", {"start": v(816.45, 1325) * mm, "end": v(816.47, 1325.06) * mm});
            skLineSegment(sketch, "E2716", {"start": v(816.47, 1325.06) * mm, "end": v(816.48, 1325.13) * mm});
            skLineSegment(sketch, "E2717", {"start": v(816.48, 1325.13) * mm, "end": v(816.5, 1325.2) * mm});
            skLineSegment(sketch, "E2718", {"start": v(816.5, 1325.2) * mm, "end": v(816.51, 1325.26) * mm});
            skLineSegment(sketch, "E2719", {"start": v(816.51, 1325.26) * mm, "end": v(816.53, 1325.32) * mm});
            skLineSegment(sketch, "E2720", {"start": v(816.53, 1325.32) * mm, "end": v(816.55, 1325.39) * mm});
            skLineSegment(sketch, "E2721", {"start": v(816.55, 1325.39) * mm, "end": v(816.58, 1325.46) * mm});
            skLineSegment(sketch, "E2722", {"start": v(816.58, 1325.46) * mm, "end": v(816.6, 1325.52) * mm});
            skLineSegment(sketch, "E2723", {"start": v(816.6, 1325.52) * mm, "end": v(816.63, 1325.59) * mm});
            skLineSegment(sketch, "E2724", {"start": v(816.63, 1325.59) * mm, "end": v(816.66, 1325.65) * mm});
            skLineSegment(sketch, "E2725", {"start": v(816.66, 1325.65) * mm, "end": v(816.68, 1325.72) * mm});
            skLineSegment(sketch, "E2726", {"start": v(816.68, 1325.72) * mm, "end": v(816.72, 1325.78) * mm});
            skLineSegment(sketch, "E2727", {"start": v(816.72, 1325.78) * mm, "end": v(816.75, 1325.85) * mm});
            skLineSegment(sketch, "E2728", {"start": v(816.75, 1325.85) * mm, "end": v(816.78, 1325.91) * mm});
            skLineSegment(sketch, "E2729", {"start": v(816.78, 1325.91) * mm, "end": v(816.82, 1325.98) * mm});
            skLineSegment(sketch, "E2730", {"start": v(816.82, 1325.98) * mm, "end": v(816.86, 1326.04) * mm});
            skLineSegment(sketch, "E2731", {"start": v(816.86, 1326.04) * mm, "end": v(816.9, 1326.1) * mm});
            skLineSegment(sketch, "E2732", {"start": v(816.9, 1326.1) * mm, "end": v(816.94, 1326.17) * mm});
            skLineSegment(sketch, "E2733", {"start": v(816.94, 1326.17) * mm, "end": v(816.98, 1326.23) * mm});
            skLineSegment(sketch, "E2734", {"start": v(816.98, 1326.23) * mm, "end": v(817.02, 1326.3) * mm});
            skLineSegment(sketch, "E2735", {"start": v(817.02, 1326.3) * mm, "end": v(817.06, 1326.36) * mm});
            skLineSegment(sketch, "E2736", {"start": v(817.06, 1326.36) * mm, "end": v(817.11, 1326.42) * mm});
            skLineSegment(sketch, "E2737", {"start": v(817.11, 1326.42) * mm, "end": v(817.16, 1326.49) * mm});
            skLineSegment(sketch, "E2738", {"start": v(817.16, 1326.49) * mm, "end": v(817.2, 1326.55) * mm});
            skLineSegment(sketch, "E2739", {"start": v(817.2, 1326.55) * mm, "end": v(817.26, 1326.61) * mm});
            skLineSegment(sketch, "E2740", {"start": v(817.26, 1326.61) * mm, "end": v(817.3, 1326.67) * mm});
            skLineSegment(sketch, "E2741", {"start": v(817.3, 1326.67) * mm, "end": v(817.36, 1326.74) * mm});
            skLineSegment(sketch, "E2742", {"start": v(817.36, 1326.74) * mm, "end": v(817.41, 1326.8) * mm});
            skLineSegment(sketch, "E2743", {"start": v(817.41, 1326.8) * mm, "end": v(817.47, 1326.86) * mm});
            skLineSegment(sketch, "E2744", {"start": v(817.47, 1326.86) * mm, "end": v(817.9, 1326.81) * mm});
            skLineSegment(sketch, "E2745", {"start": v(817.9, 1326.81) * mm, "end": v(818.32, 1326.75) * mm});
            skLineSegment(sketch, "E2746", {"start": v(818.32, 1326.75) * mm, "end": v(818.35, 1326.67) * mm});
            skLineSegment(sketch, "E2747", {"start": v(818.35, 1326.67) * mm, "end": v(818.39, 1326.6) * mm});
            skLineSegment(sketch, "E2748", {"start": v(818.39, 1326.6) * mm, "end": v(818.42, 1326.53) * mm});
            skLineSegment(sketch, "E2749", {"start": v(818.42, 1326.53) * mm, "end": v(818.46, 1326.45) * mm});
            skLineSegment(sketch, "E2750", {"start": v(818.46, 1326.45) * mm, "end": v(818.49, 1326.38) * mm});
            skLineSegment(sketch, "E2751", {"start": v(818.49, 1326.38) * mm, "end": v(818.52, 1326.3) * mm});
            skLineSegment(sketch, "E2752", {"start": v(818.52, 1326.3) * mm, "end": v(818.55, 1326.23) * mm});
            skLineSegment(sketch, "E2753", {"start": v(818.55, 1326.23) * mm, "end": v(818.58, 1326.16) * mm});
            skLineSegment(sketch, "E2754", {"start": v(818.58, 1326.16) * mm, "end": v(818.6, 1326.09) * mm});
            skLineSegment(sketch, "E2755", {"start": v(818.6, 1326.09) * mm, "end": v(818.63, 1326.02) * mm});
            skLineSegment(sketch, "E2756", {"start": v(818.63, 1326.02) * mm, "end": v(818.65, 1325.94) * mm});
            skLineSegment(sketch, "E2757", {"start": v(818.65, 1325.94) * mm, "end": v(818.68, 1325.87) * mm});
            skLineSegment(sketch, "E2758", {"start": v(818.68, 1325.87) * mm, "end": v(818.7, 1325.8) * mm});
            skLineSegment(sketch, "E2759", {"start": v(818.7, 1325.8) * mm, "end": v(818.72, 1325.73) * mm});
            skLineSegment(sketch, "E2760", {"start": v(818.72, 1325.73) * mm, "end": v(818.73, 1325.66) * mm});
            skLineSegment(sketch, "E2761", {"start": v(818.73, 1325.66) * mm, "end": v(818.75, 1325.58) * mm});
            skLineSegment(sketch, "E2762", {"start": v(818.75, 1325.58) * mm, "end": v(818.76, 1325.51) * mm});
            skLineSegment(sketch, "E2763", {"start": v(818.76, 1325.51) * mm, "end": v(818.78, 1325.44) * mm});
            skLineSegment(sketch, "E2764", {"start": v(818.78, 1325.44) * mm, "end": v(818.8, 1325.37) * mm});
            skLineSegment(sketch, "E2765", {"start": v(818.8, 1325.37) * mm, "end": v(818.8, 1325.3) * mm});
            skLineSegment(sketch, "E2766", {"start": v(818.8, 1325.3) * mm, "end": v(818.8, 1325.23) * mm});
            skLineSegment(sketch, "E2767", {"start": v(818.8, 1325.23) * mm, "end": v(818.82, 1325.16) * mm});
            skLineSegment(sketch, "E2768", {"start": v(818.82, 1325.16) * mm, "end": v(818.82, 1325.1) * mm});
            skLineSegment(sketch, "E2769", {"start": v(818.82, 1325.1) * mm, "end": v(818.83, 1325.02) * mm});
            skLineSegment(sketch, "E2770", {"start": v(818.83, 1325.02) * mm, "end": v(818.83, 1324.95) * mm});
            skLineSegment(sketch, "E2771", {"start": v(818.83, 1324.95) * mm, "end": v(818.83, 1324.89) * mm});
            skLineSegment(sketch, "E2772", {"start": v(818.83, 1324.89) * mm, "end": v(818.82, 1324.82) * mm});
            skLineSegment(sketch, "E2773", {"start": v(818.82, 1324.82) * mm, "end": v(818.82, 1324.75) * mm});
            skLineSegment(sketch, "E2774", {"start": v(818.82, 1324.75) * mm, "end": v(818.81, 1324.69) * mm});
            skLineSegment(sketch, "E2775", {"start": v(818.81, 1324.69) * mm, "end": v(818.81, 1324.62) * mm});
            skLineSegment(sketch, "E2776", {"start": v(818.81, 1324.62) * mm, "end": v(818.46, 1323.38) * mm});
            skLineSegment(sketch, "E2777", {"start": v(818.46, 1323.38) * mm, "end": v(819.9, 1322.79) * mm});
            skLineSegment(sketch, "E2778", {"start": v(819.9, 1322.79) * mm, "end": v(820.52, 1323.91) * mm});
            skLineSegment(sketch, "E2779", {"start": v(820.52, 1323.91) * mm, "end": v(820.57, 1323.96) * mm});
            skLineSegment(sketch, "E2780", {"start": v(820.57, 1323.96) * mm, "end": v(820.61, 1324) * mm});
            skLineSegment(sketch, "E2781", {"start": v(820.61, 1324) * mm, "end": v(820.66, 1324.06) * mm});
            skLineSegment(sketch, "E2782", {"start": v(820.66, 1324.06) * mm, "end": v(820.7, 1324.1) * mm});
            skLineSegment(sketch, "E2783", {"start": v(820.7, 1324.1) * mm, "end": v(820.75, 1324.16) * mm});
            skLineSegment(sketch, "E2784", {"start": v(820.75, 1324.16) * mm, "end": v(820.8, 1324.2) * mm});
            skLineSegment(sketch, "E2785", {"start": v(820.8, 1324.2) * mm, "end": v(820.85, 1324.25) * mm});
            skLineSegment(sketch, "E2786", {"start": v(820.85, 1324.25) * mm, "end": v(820.9, 1324.3) * mm});
            skLineSegment(sketch, "E2787", {"start": v(820.9, 1324.3) * mm, "end": v(820.96, 1324.34) * mm});
            skLineSegment(sketch, "E2788", {"start": v(820.96, 1324.34) * mm, "end": v(821.02, 1324.38) * mm});
            skLineSegment(sketch, "E2789", {"start": v(821.02, 1324.38) * mm, "end": v(821.07, 1324.42) * mm});
            skLineSegment(sketch, "E2790", {"start": v(821.07, 1324.42) * mm, "end": v(821.13, 1324.47) * mm});
            skLineSegment(sketch, "E2791", {"start": v(821.13, 1324.47) * mm, "end": v(821.2, 1324.5) * mm});
            skLineSegment(sketch, "E2792", {"start": v(821.2, 1324.5) * mm, "end": v(821.25, 1324.55) * mm});
            skLineSegment(sketch, "E2793", {"start": v(821.25, 1324.55) * mm, "end": v(821.31, 1324.59) * mm});
            skLineSegment(sketch, "E2794", {"start": v(821.31, 1324.59) * mm, "end": v(821.38, 1324.62) * mm});
            skLineSegment(sketch, "E2795", {"start": v(821.38, 1324.62) * mm, "end": v(821.44, 1324.66) * mm});
            skLineSegment(sketch, "E2796", {"start": v(821.44, 1324.66) * mm, "end": v(821.5, 1324.7) * mm});
            skLineSegment(sketch, "E2797", {"start": v(821.5, 1324.7) * mm, "end": v(821.57, 1324.73) * mm});
            skLineSegment(sketch, "E2798", {"start": v(821.57, 1324.73) * mm, "end": v(821.64, 1324.77) * mm});
            skLineSegment(sketch, "E2799", {"start": v(821.64, 1324.77) * mm, "end": v(821.71, 1324.8) * mm});
            skLineSegment(sketch, "E2800", {"start": v(821.71, 1324.8) * mm, "end": v(821.78, 1324.83) * mm});
            skLineSegment(sketch, "E2801", {"start": v(821.78, 1324.83) * mm, "end": v(821.85, 1324.87) * mm});
            skLineSegment(sketch, "E2802", {"start": v(821.85, 1324.87) * mm, "end": v(821.92, 1324.9) * mm});
            skLineSegment(sketch, "E2803", {"start": v(821.92, 1324.9) * mm, "end": v(822, 1324.93) * mm});
            skLineSegment(sketch, "E2804", {"start": v(822, 1324.93) * mm, "end": v(822.07, 1324.96) * mm});
            skLineSegment(sketch, "E2805", {"start": v(822.07, 1324.96) * mm, "end": v(822.15, 1324.98) * mm});
            skLineSegment(sketch, "E2806", {"start": v(822.15, 1324.98) * mm, "end": v(822.22, 1325.01) * mm});
            skLineSegment(sketch, "E2807", {"start": v(822.22, 1325.01) * mm, "end": v(822.3, 1325.04) * mm});
            skLineSegment(sketch, "E2808", {"start": v(822.3, 1325.04) * mm, "end": v(822.38, 1325.06) * mm});
            skLineSegment(sketch, "E2809", {"start": v(822.38, 1325.06) * mm, "end": v(822.72, 1324.8) * mm});
            skLineSegment(sketch, "E2810", {"start": v(822.72, 1324.8) * mm, "end": v(823.06, 1324.54) * mm});
            skLineSegment(sketch, "E2811", {"start": v(823.06, 1324.54) * mm, "end": v(823.05, 1324.46) * mm});
            skLineSegment(sketch, "E2812", {"start": v(823.05, 1324.46) * mm, "end": v(823.05, 1324.38) * mm});
            skLineSegment(sketch, "E2813", {"start": v(823.05, 1324.38) * mm, "end": v(823.04, 1324.3) * mm});
            skLineSegment(sketch, "E2814", {"start": v(823.04, 1324.3) * mm, "end": v(823.03, 1324.22) * mm});
            skLineSegment(sketch, "E2815", {"start": v(823.03, 1324.22) * mm, "end": v(823.02, 1324.14) * mm});
            skLineSegment(sketch, "E2816", {"start": v(823.02, 1324.14) * mm, "end": v(823.02, 1324.06) * mm});
            skLineSegment(sketch, "E2817", {"start": v(823.02, 1324.06) * mm, "end": v(823, 1323.98) * mm});
            skLineSegment(sketch, "E2818", {"start": v(823, 1323.98) * mm, "end": v(823, 1323.9) * mm});
            skLineSegment(sketch, "E2819", {"start": v(823, 1323.9) * mm, "end": v(822.98, 1323.83) * mm});
            skLineSegment(sketch, "E2820", {"start": v(822.98, 1323.83) * mm, "end": v(822.96, 1323.75) * mm});
            skLineSegment(sketch, "E2821", {"start": v(822.96, 1323.75) * mm, "end": v(822.95, 1323.68) * mm});
            skLineSegment(sketch, "E2822", {"start": v(822.95, 1323.68) * mm, "end": v(822.93, 1323.6) * mm});
            skLineSegment(sketch, "E2823", {"start": v(822.93, 1323.6) * mm, "end": v(822.91, 1323.53) * mm});
            skLineSegment(sketch, "E2824", {"start": v(822.91, 1323.53) * mm, "end": v(822.9, 1323.46) * mm});
            skLineSegment(sketch, "E2825", {"start": v(822.9, 1323.46) * mm, "end": v(822.87, 1323.39) * mm});
            skLineSegment(sketch, "E2826", {"start": v(822.87, 1323.39) * mm, "end": v(822.85, 1323.32) * mm});
            skLineSegment(sketch, "E2827", {"start": v(822.85, 1323.32) * mm, "end": v(822.83, 1323.25) * mm});
            skLineSegment(sketch, "E2828", {"start": v(822.83, 1323.25) * mm, "end": v(822.8, 1323.18) * mm});
            skLineSegment(sketch, "E2829", {"start": v(822.8, 1323.18) * mm, "end": v(822.78, 1323.11) * mm});
            skLineSegment(sketch, "E2830", {"start": v(822.78, 1323.11) * mm, "end": v(822.75, 1323.05) * mm});
            skLineSegment(sketch, "E2831", {"start": v(822.75, 1323.05) * mm, "end": v(822.73, 1322.98) * mm});
            skLineSegment(sketch, "E2832", {"start": v(822.73, 1322.98) * mm, "end": v(822.7, 1322.92) * mm});
            skLineSegment(sketch, "E2833", {"start": v(822.7, 1322.92) * mm, "end": v(822.67, 1322.86) * mm});
            skLineSegment(sketch, "E2834", {"start": v(822.67, 1322.86) * mm, "end": v(822.64, 1322.8) * mm});
            skLineSegment(sketch, "E2835", {"start": v(822.64, 1322.8) * mm, "end": v(822.6, 1322.74) * mm});
            skLineSegment(sketch, "E2836", {"start": v(822.6, 1322.74) * mm, "end": v(822.57, 1322.68) * mm});
            skLineSegment(sketch, "E2837", {"start": v(822.57, 1322.68) * mm, "end": v(822.53, 1322.62) * mm});
            skLineSegment(sketch, "E2838", {"start": v(822.53, 1322.62) * mm, "end": v(822.5, 1322.56) * mm});
            skLineSegment(sketch, "E2839", {"start": v(822.5, 1322.56) * mm, "end": v(822.46, 1322.5) * mm});
            skLineSegment(sketch, "E2840", {"start": v(822.46, 1322.5) * mm, "end": v(822.42, 1322.45) * mm});
            skLineSegment(sketch, "E2841", {"start": v(822.42, 1322.45) * mm, "end": v(821.5, 1321.56) * mm});
            skLineSegment(sketch, "E2842", {"start": v(821.5, 1321.56) * mm, "end": v(822.45, 1320.32) * mm});
            skLineSegment(sketch, "E2843", {"start": v(822.45, 1320.32) * mm, "end": v(823.55, 1320.98) * mm});
            skLineSegment(sketch, "E2844", {"start": v(823.55, 1320.98) * mm, "end": v(823.62, 1321) * mm});
            skLineSegment(sketch, "E2845", {"start": v(823.62, 1321) * mm, "end": v(823.68, 1321.02) * mm});
            skLineSegment(sketch, "E2846", {"start": v(823.68, 1321.02) * mm, "end": v(823.74, 1321.05) * mm});
            skLineSegment(sketch, "E2847", {"start": v(823.74, 1321.05) * mm, "end": v(823.8, 1321.06) * mm});
            skLineSegment(sketch, "E2848", {"start": v(823.8, 1321.06) * mm, "end": v(823.87, 1321.08) * mm});
            skLineSegment(sketch, "E2849", {"start": v(823.87, 1321.08) * mm, "end": v(823.94, 1321.1) * mm});
            skLineSegment(sketch, "E2850", {"start": v(823.94, 1321.1) * mm, "end": v(824, 1321.11) * mm});
            skLineSegment(sketch, "E2851", {"start": v(824, 1321.11) * mm, "end": v(824.08, 1321.12) * mm});
            skLineSegment(sketch, "E2852", {"start": v(824.08, 1321.12) * mm, "end": v(824.14, 1321.14) * mm});
            skLineSegment(sketch, "E2853", {"start": v(824.14, 1321.14) * mm, "end": v(824.21, 1321.15) * mm});
            skLineSegment(sketch, "E2854", {"start": v(824.21, 1321.15) * mm, "end": v(824.28, 1321.16) * mm});
            skLineSegment(sketch, "E2855", {"start": v(824.28, 1321.16) * mm, "end": v(824.36, 1321.16) * mm});
            skLineSegment(sketch, "E2856", {"start": v(824.36, 1321.16) * mm, "end": v(824.43, 1321.17) * mm});
            skLineSegment(sketch, "E2857", {"start": v(824.43, 1321.17) * mm, "end": v(824.5, 1321.17) * mm});
            skLineSegment(sketch, "E2858", {"start": v(824.5, 1321.17) * mm, "end": v(824.57, 1321.17) * mm});
            skLineSegment(sketch, "E2859", {"start": v(824.57, 1321.17) * mm, "end": v(824.65, 1321.18) * mm});
            skLineSegment(sketch, "E2860", {"start": v(824.65, 1321.18) * mm, "end": v(824.72, 1321.18) * mm});
            skLineSegment(sketch, "E2861", {"start": v(824.72, 1321.18) * mm, "end": v(824.8, 1321.17) * mm});
            skLineSegment(sketch, "E2862", {"start": v(824.8, 1321.17) * mm, "end": v(824.87, 1321.17) * mm});
            skLineSegment(sketch, "E2863", {"start": v(824.87, 1321.17) * mm, "end": v(824.95, 1321.17) * mm});
            skLineSegment(sketch, "E2864", {"start": v(824.95, 1321.17) * mm, "end": v(825.03, 1321.16) * mm});
            skLineSegment(sketch, "E2865", {"start": v(825.03, 1321.16) * mm, "end": v(825.1, 1321.16) * mm});
            skLineSegment(sketch, "E2866", {"start": v(825.1, 1321.16) * mm, "end": v(825.18, 1321.15) * mm});
            skLineSegment(sketch, "E2867", {"start": v(825.18, 1321.15) * mm, "end": v(825.26, 1321.14) * mm});
            skLineSegment(sketch, "E2868", {"start": v(825.26, 1321.14) * mm, "end": v(825.34, 1321.13) * mm});
            skLineSegment(sketch, "E2869", {"start": v(825.34, 1321.13) * mm, "end": v(825.42, 1321.11) * mm});
            skLineSegment(sketch, "E2870", {"start": v(825.42, 1321.11) * mm, "end": v(825.5, 1321.1) * mm});
            skLineSegment(sketch, "E2871", {"start": v(825.5, 1321.1) * mm, "end": v(825.58, 1321.09) * mm});
            skLineSegment(sketch, "E2872", {"start": v(825.58, 1321.09) * mm, "end": v(825.65, 1321.07) * mm});
            skLineSegment(sketch, "E2873", {"start": v(825.65, 1321.07) * mm, "end": v(825.74, 1321.05) * mm});
            skLineSegment(sketch, "E2874", {"start": v(825.74, 1321.05) * mm, "end": v(825.9, 1320.66) * mm});
            skLineSegment(sketch, "E2875", {"start": v(825.9, 1320.66) * mm, "end": v(826.06, 1320.27) * mm});
            skLineSegment(sketch, "E2876", {"start": v(826.06, 1320.27) * mm, "end": v(826.02, 1320.2) * mm});
            skLineSegment(sketch, "E2877", {"start": v(826.02, 1320.2) * mm, "end": v(825.97, 1320.13) * mm});
            skLineSegment(sketch, "E2878", {"start": v(825.97, 1320.13) * mm, "end": v(825.93, 1320.06) * mm});
            skLineSegment(sketch, "E2879", {"start": v(825.93, 1320.06) * mm, "end": v(825.88, 1320) * mm});
            skLineSegment(sketch, "E2880", {"start": v(825.88, 1320) * mm, "end": v(825.83, 1319.93) * mm});
            skLineSegment(sketch, "E2881", {"start": v(825.83, 1319.93) * mm, "end": v(825.78, 1319.87) * mm});
            skLineSegment(sketch, "E2882", {"start": v(825.78, 1319.87) * mm, "end": v(825.74, 1319.8) * mm});
            skLineSegment(sketch, "E2883", {"start": v(825.74, 1319.8) * mm, "end": v(825.69, 1319.74) * mm});
            skLineSegment(sketch, "E2884", {"start": v(825.69, 1319.74) * mm, "end": v(825.64, 1319.68) * mm});
            skLineSegment(sketch, "E2885", {"start": v(825.64, 1319.68) * mm, "end": v(825.59, 1319.63) * mm});
            skLineSegment(sketch, "E2886", {"start": v(825.59, 1319.63) * mm, "end": v(825.54, 1319.57) * mm});
            skLineSegment(sketch, "E2887", {"start": v(825.54, 1319.57) * mm, "end": v(825.49, 1319.51) * mm});
            skLineSegment(sketch, "E2888", {"start": v(825.49, 1319.51) * mm, "end": v(825.43, 1319.46) * mm});
            skLineSegment(sketch, "E2889", {"start": v(825.43, 1319.46) * mm, "end": v(825.38, 1319.4) * mm});
            skLineSegment(sketch, "E2890", {"start": v(825.38, 1319.4) * mm, "end": v(825.33, 1319.36) * mm});
            skLineSegment(sketch, "E2891", {"start": v(825.33, 1319.36) * mm, "end": v(825.27, 1319.3) * mm});
            skLineSegment(sketch, "E2892", {"start": v(825.27, 1319.3) * mm, "end": v(825.22, 1319.26) * mm});
            skLineSegment(sketch, "E2893", {"start": v(825.22, 1319.26) * mm, "end": v(825.16, 1319.21) * mm});
            skLineSegment(sketch, "E2894", {"start": v(825.16, 1319.21) * mm, "end": v(825.1, 1319.17) * mm});
            skLineSegment(sketch, "E2895", {"start": v(825.1, 1319.17) * mm, "end": v(825.05, 1319.12) * mm});
            skLineSegment(sketch, "E2896", {"start": v(825.05, 1319.12) * mm, "end": v(825, 1319.08) * mm});
            skLineSegment(sketch, "E2897", {"start": v(825, 1319.08) * mm, "end": v(824.94, 1319.04) * mm});
            skLineSegment(sketch, "E2898", {"start": v(824.94, 1319.04) * mm, "end": v(824.88, 1319) * mm});
            skLineSegment(sketch, "E2899", {"start": v(824.88, 1319) * mm, "end": v(824.82, 1318.96) * mm});
            skLineSegment(sketch, "E2900", {"start": v(824.82, 1318.96) * mm, "end": v(824.77, 1318.93) * mm});
            skLineSegment(sketch, "E2901", {"start": v(824.77, 1318.93) * mm, "end": v(824.7, 1318.9) * mm});
            skLineSegment(sketch, "E2902", {"start": v(824.7, 1318.9) * mm, "end": v(824.65, 1318.86) * mm});
            skLineSegment(sketch, "E2903", {"start": v(824.65, 1318.86) * mm, "end": v(824.59, 1318.83) * mm});
            skLineSegment(sketch, "E2904", {"start": v(824.59, 1318.83) * mm, "end": v(824.53, 1318.8) * mm});
            skLineSegment(sketch, "E2905", {"start": v(824.53, 1318.8) * mm, "end": v(824.47, 1318.77) * mm});
            skLineSegment(sketch, "E2906", {"start": v(824.47, 1318.77) * mm, "end": v(823.22, 1318.46) * mm});
            skLineSegment(sketch, "E2907", {"start": v(823.22, 1318.46) * mm, "end": v(823.43, 1316.91) * mm});
            skLineSegment(sketch, "E2908", {"start": v(823.43, 1316.91) * mm, "end": v(824.7, 1316.93) * mm});
            skLineSegment(sketch, "E2909", {"start": v(813.47, 1316.8) * mm, "end": v(815.06, 1316.8) * mm, "construction": true});
            skLineSegment(sketch, "E2910.trimOffspring", {"start": v(813.73, 1305.21) * mm, "end": v(813.73, 1148.66) * mm});
            skLineSegment(sketch, "E2911.trimOffspring", {"start": v(806.51, 1305.21) * mm, "end": v(806.51, 1148.66) * mm});
            skLineSegment(sketch, "E2912.trimOffspring", {"start": v(828.16, 1319.64) * mm, "end": v(943.6, 1319.64) * mm});
            skLineSegment(sketch, "E2913.trimOffspring", {"start": v(828.16, 1312.43) * mm, "end": v(943.6, 1312.43) * mm});
            skLineSegment(sketch, "E2914.trimOffspring", {"start": v(820.94, 1308.98) * mm, "end": v(820.94, 1308.38) * mm});
            skLineSegment(sketch, "E2915.trimOffspring", {"start": v(820.94, 1305.21) * mm, "end": v(943.6, 1305.21) * mm});
            skLineSegment(sketch, "E2916.trimOffspring", {"start": v(820.94, 1305.21) * mm, "end": v(820.94, 1148.66) * mm});
            skLineSegment(sketch, "E2917.trimOffspring", {"start": v(820.94, 1326.86) * mm, "end": v(943.6, 1326.86) * mm});
            skLineSegment(sketch, "E2918.trimOffspring", {"start": v(816.57, 1315.48) * mm, "end": v(816.57, 1313.19) * mm, "construction": true});
            skLineSegment(sketch, "E2919.trimOffspring", {"start": v(819.1, 1316.8) * mm, "end": v(820.69, 1316.8) * mm, "construction": true});
            skPoint(sketch, "E2920.orphan", {"position": v(819.1, 1315.48) * mm});
            skCircle(sketch, "E2921", {"center": v(816.57, 1316.8) * mm, "radius": 2.85 * mm});
            skLineSegment(sketch, "E2922", {"start": v(816.57, 1316.8) * mm, "end": v(824.59, 1310.65) * mm, "construction": true});
            skLineSegment(sketch, "E2923", {"start": v(812.76, 1316.4) * mm, "end": v(810.45, 1315.28) * mm});
            skLineSegment(sketch, "E2924.bottom", {"start": v(818.84, 1315.06) * mm, "end": v(814.31, 1315.06) * mm});
            skLineSegment(sketch, "E2924.top", {"start": v(818.84, 1318.53) * mm, "end": v(814.31, 1318.53) * mm});
            skLineSegment(sketch, "E2924.left", {"start": v(818.84, 1315.06) * mm, "end": v(818.84, 1318.53) * mm});
            skLineSegment(sketch, "E2924.right", {"start": v(814.31, 1315.06) * mm, "end": v(814.31, 1318.53) * mm});
            skSolve(sketch);
        }
        {
            var Q0;
            {var subQ2=sQuery(id+"F2.wireOp",EDGE,"E2084");Q0=makeQuery(id+"F2.imprint","IMPRINT",FACE,{"disambiguationData":[TD([[makeQuery(id+"F2.imprint","IMPRINT",EDGE,{"derivedFrom":subQ2}),1.0]])]});}
            extrude(context, id + "F3", {"entities" : qUnion([Q0]), "depth" : 15 * mm, "offsetDistance" : 25 * mm});
        }
        {
            var Q0;
            {var subQ0=sQuery(id+"F2.wireOp",EDGE,"E2924.bottom");Q0=makeQuery(id+"F2.imprint","IMPRINT",FACE,{"disambiguationData":[TD([[makeQuery(id+"F2.imprint","IMPRINT",EDGE,{"derivedFrom":subQ0}),1.0]])]});}
            var Q1;
            {var subQ0=sQuery(id+"F2.wireOp",EDGE,"E2924.right");Q1=makeQuery(id+"F2.imprint","IMPRINT",FACE,{"disambiguationData":[TD([[makeQuery(id+"F2.imprint","IMPRINT",EDGE,{"derivedFrom":subQ0}),1.0]])]});}
            var Q2;
            {var subQ0=sQuery(id+"F2.wireOp",EDGE,"E2924.top");Q2=makeQuery(id+"F2.imprint","IMPRINT",FACE,{"disambiguationData":[TD([[makeQuery(id+"F2.imprint","IMPRINT",EDGE,{"derivedFrom":subQ0}),-1.0]])]});}
            var Q3;
            {var subQ0=sQuery(id+"F2.wireOp",EDGE,"E2924.left");Q3=makeQuery(id+"F2.imprint","IMPRINT",FACE,{"disambiguationData":[TD([[makeQuery(id+"F2.imprint","IMPRINT",EDGE,{"derivedFrom":subQ0}),-1.0]])]});}
            var Q4;
            Q4=makeQuery(id+"F3.opExtrude","CAP_FACE",FACE,{"disambiguationData":[OSD([sQuery(id+"F2.wireOp",EDGE,"E2084"),sQuery(id+"F2.wireOp",EDGE,"E2131"),sQuery(id+"F2.wireOp",EDGE,"E2132"),sQuery(id+"F2.wireOp",EDGE,"E2133"),sQuery(id+"F2.wireOp",EDGE,"E2134"),sQuery(id+"F2.wireOp",EDGE,"E2135"),sQuery(id+"F2.wireOp",EDGE,"E2136"),sQuery(id+"F2.wireOp",EDGE,"E2137"),sQuery(id+"F2.wireOp",EDGE,"E2138"),sQuery(id+"F2.wireOp",EDGE,"E2139"),sQuery(id+"F2.wireOp",EDGE,"E2140"),sQuery(id+"F2.wireOp",EDGE,"E2141"),sQuery(id+"F2.wireOp",EDGE,"E2142"),sQuery(id+"F2.wireOp",EDGE,"E2143"),sQuery(id+"F2.wireOp",EDGE,"E2144"),sQuery(id+"F2.wireOp",EDGE,"E2145"),sQuery(id+"F2.wireOp",EDGE,"E2146"),sQuery(id+"F2.wireOp",EDGE,"E2147"),sQuery(id+"F2.wireOp",EDGE,"E2148"),sQuery(id+"F2.wireOp",EDGE,"E2149"),sQuery(id+"F2.wireOp",EDGE,"E2150"),sQuery(id+"F2.wireOp",EDGE,"E2151"),sQuery(id+"F2.wireOp",EDGE,"E2152"),sQuery(id+"F2.wireOp",EDGE,"E2153"),sQuery(id+"F2.wireOp",EDGE,"E2154"),sQuery(id+"F2.wireOp",EDGE,"E2155"),sQuery(id+"F2.wireOp",EDGE,"E2156"),sQuery(id+"F2.wireOp",EDGE,"E2157"),sQuery(id+"F2.wireOp",EDGE,"E2158"),sQuery(id+"F2.wireOp",EDGE,"E2159"),sQuery(id+"F2.wireOp",EDGE,"E2160"),sQuery(id+"F2.wireOp",EDGE,"E2161"),sQuery(id+"F2.wireOp",EDGE,"E2162"),sQuery(id+"F2.wireOp",EDGE,"E2163"),sQuery(id+"F2.wireOp",EDGE,"E2164"),sQuery(id+"F2.wireOp",EDGE,"E2165"),sQuery(id+"F2.wireOp",EDGE,"E2166"),sQuery(id+"F2.wireOp",EDGE,"E2167"),sQuery(id+"F2.wireOp",EDGE,"E2168"),sQuery(id+"F2.wireOp",EDGE,"E2169"),sQuery(id+"F2.wireOp",EDGE,"E2170"),sQuery(id+"F2.wireOp",EDGE,"E2171"),sQuery(id+"F2.wireOp",EDGE,"E2172"),sQuery(id+"F2.wireOp",EDGE,"E2173"),sQuery(id+"F2.wireOp",EDGE,"E2174"),sQuery(id+"F2.wireOp",EDGE,"E2175"),sQuery(id+"F2.wireOp",EDGE,"E2176"),sQuery(id+"F2.wireOp",EDGE,"E2177"),sQuery(id+"F2.wireOp",EDGE,"E2178"),sQuery(id+"F2.wireOp",EDGE,"E2179"),sQuery(id+"F2.wireOp",EDGE,"E2180"),sQuery(id+"F2.wireOp",EDGE,"E2181"),sQuery(id+"F2.wireOp",EDGE,"E2182"),sQuery(id+"F2.wireOp",EDGE,"E2183"),sQuery(id+"F2.wireOp",EDGE,"E2184"),sQuery(id+"F2.wireOp",EDGE,"E2185"),sQuery(id+"F2.wireOp",EDGE,"E2186"),sQuery(id+"F2.wireOp",EDGE,"E2187"),sQuery(id+"F2.wireOp",EDGE,"E2188"),sQuery(id+"F2.wireOp",EDGE,"E2189"),sQuery(id+"F2.wireOp",EDGE,"E2190"),sQuery(id+"F2.wireOp",EDGE,"E2191"),sQuery(id+"F2.wireOp",EDGE,"E2192"),sQuery(id+"F2.wireOp",EDGE,"E2193"),sQuery(id+"F2.wireOp",EDGE,"E2194"),sQuery(id+"F2.wireOp",EDGE,"E2195"),sQuery(id+"F2.wireOp",EDGE,"E2196"),sQuery(id+"F2.wireOp",EDGE,"E2197"),sQuery(id+"F2.wireOp",EDGE,"E2198"),sQuery(id+"F2.wireOp",EDGE,"E2199"),sQuery(id+"F2.wireOp",EDGE,"E2200"),sQuery(id+"F2.wireOp",EDGE,"E2201"),sQuery(id+"F2.wireOp",EDGE,"E2202"),sQuery(id+"F2.wireOp",EDGE,"E2203"),sQuery(id+"F2.wireOp",EDGE,"E2204"),sQuery(id+"F2.wireOp",EDGE,"E2205"),sQuery(id+"F2.wireOp",EDGE,"E2206"),sQuery(id+"F2.wireOp",EDGE,"E2207"),sQuery(id+"F2.wireOp",EDGE,"E2208"),sQuery(id+"F2.wireOp",EDGE,"E2209"),sQuery(id+"F2.wireOp",EDGE,"E2210"),sQuery(id+"F2.wireOp",EDGE,"E2211"),sQuery(id+"F2.wireOp",EDGE,"E2212"),sQuery(id+"F2.wireOp",EDGE,"E2213"),sQuery(id+"F2.wireOp",EDGE,"E2214"),sQuery(id+"F2.wireOp",EDGE,"E2215"),sQuery(id+"F2.wireOp",EDGE,"E2216"),sQuery(id+"F2.wireOp",EDGE,"E2217"),sQuery(id+"F2.wireOp",EDGE,"E2218"),sQuery(id+"F2.wireOp",EDGE,"E2219"),sQuery(id+"F2.wireOp",EDGE,"E2220"),sQuery(id+"F2.wireOp",EDGE,"E2221"),sQuery(id+"F2.wireOp",EDGE,"E2222"),sQuery(id+"F2.wireOp",EDGE,"E2223"),sQuery(id+"F2.wireOp",EDGE,"E2224"),sQuery(id+"F2.wireOp",EDGE,"E2225"),sQuery(id+"F2.wireOp",EDGE,"E2226"),sQuery(id+"F2.wireOp",EDGE,"E2227"),sQuery(id+"F2.wireOp",EDGE,"E2228"),sQuery(id+"F2.wireOp",EDGE,"E2229"),sQuery(id+"F2.wireOp",EDGE,"E2230"),sQuery(id+"F2.wireOp",EDGE,"E2231"),sQuery(id+"F2.wireOp",EDGE,"E2232"),sQuery(id+"F2.wireOp",EDGE,"E2233"),sQuery(id+"F2.wireOp",EDGE,"E2234"),sQuery(id+"F2.wireOp",EDGE,"E2235"),sQuery(id+"F2.wireOp",EDGE,"E2236"),sQuery(id+"F2.wireOp",EDGE,"E2237"),sQuery(id+"F2.wireOp",EDGE,"E2238"),sQuery(id+"F2.wireOp",EDGE,"E2239"),sQuery(id+"F2.wireOp",EDGE,"E2240"),sQuery(id+"F2.wireOp",EDGE,"E2241"),sQuery(id+"F2.wireOp",EDGE,"E2242"),sQuery(id+"F2.wireOp",EDGE,"E2243"),sQuery(id+"F2.wireOp",EDGE,"E2244"),sQuery(id+"F2.wireOp",EDGE,"E2245"),sQuery(id+"F2.wireOp",EDGE,"E2246"),sQuery(id+"F2.wireOp",EDGE,"E2247"),sQuery(id+"F2.wireOp",EDGE,"E2248"),sQuery(id+"F2.wireOp",EDGE,"E2249"),sQuery(id+"F2.wireOp",EDGE,"E2250"),sQuery(id+"F2.wireOp",EDGE,"E2251"),sQuery(id+"F2.wireOp",EDGE,"E2252"),sQuery(id+"F2.wireOp",EDGE,"E2253"),sQuery(id+"F2.wireOp",EDGE,"E2254"),sQuery(id+"F2.wireOp",EDGE,"E2255"),sQuery(id+"F2.wireOp",EDGE,"E2256"),sQuery(id+"F2.wireOp",EDGE,"E2257"),sQuery(id+"F2.wireOp",EDGE,"E2258"),sQuery(id+"F2.wireOp",EDGE,"E2259"),sQuery(id+"F2.wireOp",EDGE,"E2260"),sQuery(id+"F2.wireOp",EDGE,"E2261"),sQuery(id+"F2.wireOp",EDGE,"E2262"),sQuery(id+"F2.wireOp",EDGE,"E2263"),sQuery(id+"F2.wireOp",EDGE,"E2264"),sQuery(id+"F2.wireOp",EDGE,"E2265"),sQuery(id+"F2.wireOp",EDGE,"E2266"),sQuery(id+"F2.wireOp",EDGE,"E2267"),sQuery(id+"F2.wireOp",EDGE,"E2268"),sQuery(id+"F2.wireOp",EDGE,"E2269"),sQuery(id+"F2.wireOp",EDGE,"E2270"),sQuery(id+"F2.wireOp",EDGE,"E2271"),sQuery(id+"F2.wireOp",EDGE,"E2279"),sQuery(id+"F2.wireOp",EDGE,"E2280"),sQuery(id+"F2.wireOp",EDGE,"E2281"),sQuery(id+"F2.wireOp",EDGE,"E2282"),sQuery(id+"F2.wireOp",EDGE,"E2283"),sQuery(id+"F2.wireOp",EDGE,"E2284"),sQuery(id+"F2.wireOp",EDGE,"E2285"),sQuery(id+"F2.wireOp",EDGE,"E2286"),sQuery(id+"F2.wireOp",EDGE,"E2287"),sQuery(id+"F2.wireOp",EDGE,"E2288"),sQuery(id+"F2.wireOp",EDGE,"E2289"),sQuery(id+"F2.wireOp",EDGE,"E2290"),sQuery(id+"F2.wireOp",EDGE,"E2291"),sQuery(id+"F2.wireOp",EDGE,"E2292"),sQuery(id+"F2.wireOp",EDGE,"E2293"),sQuery(id+"F2.wireOp",EDGE,"E2294"),sQuery(id+"F2.wireOp",EDGE,"E2295"),sQuery(id+"F2.wireOp",EDGE,"E2296"),sQuery(id+"F2.wireOp",EDGE,"E2297"),sQuery(id+"F2.wireOp",EDGE,"E2298"),sQuery(id+"F2.wireOp",EDGE,"E2299"),sQuery(id+"F2.wireOp",EDGE,"E2300"),sQuery(id+"F2.wireOp",EDGE,"E2301"),sQuery(id+"F2.wireOp",EDGE,"E2302"),sQuery(id+"F2.wireOp",EDGE,"E2303"),sQuery(id+"F2.wireOp",EDGE,"E2304"),sQuery(id+"F2.wireOp",EDGE,"E2305"),sQuery(id+"F2.wireOp",EDGE,"E2306"),sQuery(id+"F2.wireOp",EDGE,"E2307"),sQuery(id+"F2.wireOp",EDGE,"E2308"),sQuery(id+"F2.wireOp",EDGE,"E2309"),sQuery(id+"F2.wireOp",EDGE,"E2310"),sQuery(id+"F2.wireOp",EDGE,"E2311"),sQuery(id+"F2.wireOp",EDGE,"E2312"),sQuery(id+"F2.wireOp",EDGE,"E2313"),sQuery(id+"F2.wireOp",EDGE,"E2314"),sQuery(id+"F2.wireOp",EDGE,"E2315"),sQuery(id+"F2.wireOp",EDGE,"E2316"),sQuery(id+"F2.wireOp",EDGE,"E2317"),sQuery(id+"F2.wireOp",EDGE,"E2318"),sQuery(id+"F2.wireOp",EDGE,"E2319"),sQuery(id+"F2.wireOp",EDGE,"E2320"),sQuery(id+"F2.wireOp",EDGE,"E2321"),sQuery(id+"F2.wireOp",EDGE,"E2322"),sQuery(id+"F2.wireOp",EDGE,"E2323"),sQuery(id+"F2.wireOp",EDGE,"E2324"),sQuery(id+"F2.wireOp",EDGE,"E2325"),sQuery(id+"F2.wireOp",EDGE,"E2326"),sQuery(id+"F2.wireOp",EDGE,"E2327"),sQuery(id+"F2.wireOp",EDGE,"E2328"),sQuery(id+"F2.wireOp",EDGE,"E2329"),sQuery(id+"F2.wireOp",EDGE,"E2330"),sQuery(id+"F2.wireOp",EDGE,"E2331"),sQuery(id+"F2.wireOp",EDGE,"E2332"),sQuery(id+"F2.wireOp",EDGE,"E2333"),sQuery(id+"F2.wireOp",EDGE,"E2334"),sQuery(id+"F2.wireOp",EDGE,"E2335"),sQuery(id+"F2.wireOp",EDGE,"E2336"),sQuery(id+"F2.wireOp",EDGE,"E2337"),sQuery(id+"F2.wireOp",EDGE,"E2338"),sQuery(id+"F2.wireOp",EDGE,"E2339"),sQuery(id+"F2.wireOp",EDGE,"E2340"),sQuery(id+"F2.wireOp",EDGE,"E2341"),sQuery(id+"F2.wireOp",EDGE,"E2342"),sQuery(id+"F2.wireOp",EDGE,"E2343"),sQuery(id+"F2.wireOp",EDGE,"E2344"),sQuery(id+"F2.wireOp",EDGE,"E2345"),sQuery(id+"F2.wireOp",EDGE,"E2346"),sQuery(id+"F2.wireOp",EDGE,"E2347"),sQuery(id+"F2.wireOp",EDGE,"E2348"),sQuery(id+"F2.wireOp",EDGE,"E2349"),sQuery(id+"F2.wireOp",EDGE,"E2350"),sQuery(id+"F2.wireOp",EDGE,"E2351"),sQuery(id+"F2.wireOp",EDGE,"E2352"),sQuery(id+"F2.wireOp",EDGE,"E2353"),sQuery(id+"F2.wireOp",EDGE,"E2354"),sQuery(id+"F2.wireOp",EDGE,"E2355"),sQuery(id+"F2.wireOp",EDGE,"E2356"),sQuery(id+"F2.wireOp",EDGE,"E2357"),sQuery(id+"F2.wireOp",EDGE,"E2358"),sQuery(id+"F2.wireOp",EDGE,"E2359"),sQuery(id+"F2.wireOp",EDGE,"E2360"),sQuery(id+"F2.wireOp",EDGE,"E2361"),sQuery(id+"F2.wireOp",EDGE,"E2362"),sQuery(id+"F2.wireOp",EDGE,"E2363"),sQuery(id+"F2.wireOp",EDGE,"E2364"),sQuery(id+"F2.wireOp",EDGE,"E2365"),sQuery(id+"F2.wireOp",EDGE,"E2366"),sQuery(id+"F2.wireOp",EDGE,"E2367"),sQuery(id+"F2.wireOp",EDGE,"E2368"),sQuery(id+"F2.wireOp",EDGE,"E2369"),sQuery(id+"F2.wireOp",EDGE,"E2370"),sQuery(id+"F2.wireOp",EDGE,"E2371"),sQuery(id+"F2.wireOp",EDGE,"E2372"),sQuery(id+"F2.wireOp",EDGE,"E2373"),sQuery(id+"F2.wireOp",EDGE,"E2374"),sQuery(id+"F2.wireOp",EDGE,"E2375"),sQuery(id+"F2.wireOp",EDGE,"E2376"),sQuery(id+"F2.wireOp",EDGE,"E2377"),sQuery(id+"F2.wireOp",EDGE,"E2378"),sQuery(id+"F2.wireOp",EDGE,"E2379"),sQuery(id+"F2.wireOp",EDGE,"E2380"),sQuery(id+"F2.wireOp",EDGE,"E2381"),sQuery(id+"F2.wireOp",EDGE,"E2382"),sQuery(id+"F2.wireOp",EDGE,"E2383"),sQuery(id+"F2.wireOp",EDGE,"E2384"),sQuery(id+"F2.wireOp",EDGE,"E2385"),sQuery(id+"F2.wireOp",EDGE,"E2386"),sQuery(id+"F2.wireOp",EDGE,"E2387"),sQuery(id+"F2.wireOp",EDGE,"E2388"),sQuery(id+"F2.wireOp",EDGE,"E2389"),sQuery(id+"F2.wireOp",EDGE,"E2390"),sQuery(id+"F2.wireOp",EDGE,"E2391"),sQuery(id+"F2.wireOp",EDGE,"E2392"),sQuery(id+"F2.wireOp",EDGE,"E2393"),sQuery(id+"F2.wireOp",EDGE,"E2394"),sQuery(id+"F2.wireOp",EDGE,"E2395"),sQuery(id+"F2.wireOp",EDGE,"E2396"),sQuery(id+"F2.wireOp",EDGE,"E2397"),sQuery(id+"F2.wireOp",EDGE,"E2398"),sQuery(id+"F2.wireOp",EDGE,"E2399"),sQuery(id+"F2.wireOp",EDGE,"E2400"),sQuery(id+"F2.wireOp",EDGE,"E2401"),sQuery(id+"F2.wireOp",EDGE,"E2402"),sQuery(id+"F2.wireOp",EDGE,"E2403"),sQuery(id+"F2.wireOp",EDGE,"E2404"),sQuery(id+"F2.wireOp",EDGE,"E2405"),sQuery(id+"F2.wireOp",EDGE,"E2406"),sQuery(id+"F2.wireOp",EDGE,"E2407"),sQuery(id+"F2.wireOp",EDGE,"E2408"),sQuery(id+"F2.wireOp",EDGE,"E2409"),sQuery(id+"F2.wireOp",EDGE,"E2410"),sQuery(id+"F2.wireOp",EDGE,"E2411"),sQuery(id+"F2.wireOp",EDGE,"E2412"),sQuery(id+"F2.wireOp",EDGE,"E2413"),sQuery(id+"F2.wireOp",EDGE,"E2414"),sQuery(id+"F2.wireOp",EDGE,"E2415"),sQuery(id+"F2.wireOp",EDGE,"E2416"),sQuery(id+"F2.wireOp",EDGE,"E2417"),sQuery(id+"F2.wireOp",EDGE,"E2418"),sQuery(id+"F2.wireOp",EDGE,"E2419"),sQuery(id+"F2.wireOp",EDGE,"E2420"),sQuery(id+"F2.wireOp",EDGE,"E2421"),sQuery(id+"F2.wireOp",EDGE,"E2422"),sQuery(id+"F2.wireOp",EDGE,"E2423"),sQuery(id+"F2.wireOp",EDGE,"E2424"),sQuery(id+"F2.wireOp",EDGE,"E2425"),sQuery(id+"F2.wireOp",EDGE,"E2426"),sQuery(id+"F2.wireOp",EDGE,"E2427"),sQuery(id+"F2.wireOp",EDGE,"E2428"),sQuery(id+"F2.wireOp",EDGE,"E2429"),sQuery(id+"F2.wireOp",EDGE,"E2430"),sQuery(id+"F2.wireOp",EDGE,"E2431"),sQuery(id+"F2.wireOp",EDGE,"E2432"),sQuery(id+"F2.wireOp",EDGE,"E2433"),sQuery(id+"F2.wireOp",EDGE,"E2434"),sQuery(id+"F2.wireOp",EDGE,"E2435"),sQuery(id+"F2.wireOp",EDGE,"E2436"),sQuery(id+"F2.wireOp",EDGE,"E2437"),sQuery(id+"F2.wireOp",EDGE,"E2438"),sQuery(id+"F2.wireOp",EDGE,"E2439"),sQuery(id+"F2.wireOp",EDGE,"E2440"),sQuery(id+"F2.wireOp",EDGE,"E2441"),sQuery(id+"F2.wireOp",EDGE,"E2442"),sQuery(id+"F2.wireOp",EDGE,"E2443"),sQuery(id+"F2.wireOp",EDGE,"E2444"),sQuery(id+"F2.wireOp",EDGE,"E2445"),sQuery(id+"F2.wireOp",EDGE,"E2446"),sQuery(id+"F2.wireOp",EDGE,"E2447"),sQuery(id+"F2.wireOp",EDGE,"E2448"),sQuery(id+"F2.wireOp",EDGE,"E2449"),sQuery(id+"F2.wireOp",EDGE,"E2450"),sQuery(id+"F2.wireOp",EDGE,"E2451"),sQuery(id+"F2.wireOp",EDGE,"E2452"),sQuery(id+"F2.wireOp",EDGE,"E2453"),sQuery(id+"F2.wireOp",EDGE,"E2454"),sQuery(id+"F2.wireOp",EDGE,"E2455"),sQuery(id+"F2.wireOp",EDGE,"E2456"),sQuery(id+"F2.wireOp",EDGE,"E2457"),sQuery(id+"F2.wireOp",EDGE,"E2458"),sQuery(id+"F2.wireOp",EDGE,"E2459"),sQuery(id+"F2.wireOp",EDGE,"E2460"),sQuery(id+"F2.wireOp",EDGE,"E2461"),sQuery(id+"F2.wireOp",EDGE,"E2462"),sQuery(id+"F2.wireOp",EDGE,"E2463"),sQuery(id+"F2.wireOp",EDGE,"E2464"),sQuery(id+"F2.wireOp",EDGE,"E2465"),sQuery(id+"F2.wireOp",EDGE,"E2466"),sQuery(id+"F2.wireOp",EDGE,"E2474"),sQuery(id+"F2.wireOp",EDGE,"E2475"),sQuery(id+"F2.wireOp",EDGE,"E2476"),sQuery(id+"F2.wireOp",EDGE,"E2477"),sQuery(id+"F2.wireOp",EDGE,"E2478"),sQuery(id+"F2.wireOp",EDGE,"E2479"),sQuery(id+"F2.wireOp",EDGE,"E2480"),sQuery(id+"F2.wireOp",EDGE,"E2481"),sQuery(id+"F2.wireOp",EDGE,"E2482"),sQuery(id+"F2.wireOp",EDGE,"E2483"),sQuery(id+"F2.wireOp",EDGE,"E2484"),sQuery(id+"F2.wireOp",EDGE,"E2485"),sQuery(id+"F2.wireOp",EDGE,"E2486"),sQuery(id+"F2.wireOp",EDGE,"E2487"),sQuery(id+"F2.wireOp",EDGE,"E2488"),sQuery(id+"F2.wireOp",EDGE,"E2489"),sQuery(id+"F2.wireOp",EDGE,"E2490"),sQuery(id+"F2.wireOp",EDGE,"E2491"),sQuery(id+"F2.wireOp",EDGE,"E2492"),sQuery(id+"F2.wireOp",EDGE,"E2493"),sQuery(id+"F2.wireOp",EDGE,"E2494"),sQuery(id+"F2.wireOp",EDGE,"E2495"),sQuery(id+"F2.wireOp",EDGE,"E2496"),sQuery(id+"F2.wireOp",EDGE,"E2497"),sQuery(id+"F2.wireOp",EDGE,"E2498"),sQuery(id+"F2.wireOp",EDGE,"E2499"),sQuery(id+"F2.wireOp",EDGE,"E2500"),sQuery(id+"F2.wireOp",EDGE,"E2501"),sQuery(id+"F2.wireOp",EDGE,"E2502"),sQuery(id+"F2.wireOp",EDGE,"E2503"),sQuery(id+"F2.wireOp",EDGE,"E2504"),sQuery(id+"F2.wireOp",EDGE,"E2505"),sQuery(id+"F2.wireOp",EDGE,"E2506"),sQuery(id+"F2.wireOp",EDGE,"E2507"),sQuery(id+"F2.wireOp",EDGE,"E2508"),sQuery(id+"F2.wireOp",EDGE,"E2509"),sQuery(id+"F2.wireOp",EDGE,"E2510"),sQuery(id+"F2.wireOp",EDGE,"E2511"),sQuery(id+"F2.wireOp",EDGE,"E2512"),sQuery(id+"F2.wireOp",EDGE,"E2513"),sQuery(id+"F2.wireOp",EDGE,"E2514"),sQuery(id+"F2.wireOp",EDGE,"E2515"),sQuery(id+"F2.wireOp",EDGE,"E2516"),sQuery(id+"F2.wireOp",EDGE,"E2517"),sQuery(id+"F2.wireOp",EDGE,"E2518"),sQuery(id+"F2.wireOp",EDGE,"E2519"),sQuery(id+"F2.wireOp",EDGE,"E2520"),sQuery(id+"F2.wireOp",EDGE,"E2521"),sQuery(id+"F2.wireOp",EDGE,"E2522"),sQuery(id+"F2.wireOp",EDGE,"E2523"),sQuery(id+"F2.wireOp",EDGE,"E2524"),sQuery(id+"F2.wireOp",EDGE,"E2525"),sQuery(id+"F2.wireOp",EDGE,"E2526"),sQuery(id+"F2.wireOp",EDGE,"E2527"),sQuery(id+"F2.wireOp",EDGE,"E2528"),sQuery(id+"F2.wireOp",EDGE,"E2529"),sQuery(id+"F2.wireOp",EDGE,"E2530"),sQuery(id+"F2.wireOp",EDGE,"E2531"),sQuery(id+"F2.wireOp",EDGE,"E2532"),sQuery(id+"F2.wireOp",EDGE,"E2533"),sQuery(id+"F2.wireOp",EDGE,"E2534"),sQuery(id+"F2.wireOp",EDGE,"E2535"),sQuery(id+"F2.wireOp",EDGE,"E2536"),sQuery(id+"F2.wireOp",EDGE,"E2537"),sQuery(id+"F2.wireOp",EDGE,"E2538"),sQuery(id+"F2.wireOp",EDGE,"E2539"),sQuery(id+"F2.wireOp",EDGE,"E2540"),sQuery(id+"F2.wireOp",EDGE,"E2541"),sQuery(id+"F2.wireOp",EDGE,"E2542"),sQuery(id+"F2.wireOp",EDGE,"E2543"),sQuery(id+"F2.wireOp",EDGE,"E2544"),sQuery(id+"F2.wireOp",EDGE,"E2545"),sQuery(id+"F2.wireOp",EDGE,"E2546"),sQuery(id+"F2.wireOp",EDGE,"E2547"),sQuery(id+"F2.wireOp",EDGE,"E2548"),sQuery(id+"F2.wireOp",EDGE,"E2549"),sQuery(id+"F2.wireOp",EDGE,"E2550"),sQuery(id+"F2.wireOp",EDGE,"E2551"),sQuery(id+"F2.wireOp",EDGE,"E2552"),sQuery(id+"F2.wireOp",EDGE,"E2553"),sQuery(id+"F2.wireOp",EDGE,"E2554"),sQuery(id+"F2.wireOp",EDGE,"E2555"),sQuery(id+"F2.wireOp",EDGE,"E2556"),sQuery(id+"F2.wireOp",EDGE,"E2557"),sQuery(id+"F2.wireOp",EDGE,"E2558"),sQuery(id+"F2.wireOp",EDGE,"E2559"),sQuery(id+"F2.wireOp",EDGE,"E2560"),sQuery(id+"F2.wireOp",EDGE,"E2561"),sQuery(id+"F2.wireOp",EDGE,"E2562"),sQuery(id+"F2.wireOp",EDGE,"E2563"),sQuery(id+"F2.wireOp",EDGE,"E2564"),sQuery(id+"F2.wireOp",EDGE,"E2565"),sQuery(id+"F2.wireOp",EDGE,"E2566"),sQuery(id+"F2.wireOp",EDGE,"E2567"),sQuery(id+"F2.wireOp",EDGE,"E2568"),sQuery(id+"F2.wireOp",EDGE,"E2569"),sQuery(id+"F2.wireOp",EDGE,"E2570"),sQuery(id+"F2.wireOp",EDGE,"E2571"),sQuery(id+"F2.wireOp",EDGE,"E2572"),sQuery(id+"F2.wireOp",EDGE,"E2573"),sQuery(id+"F2.wireOp",EDGE,"E2574"),sQuery(id+"F2.wireOp",EDGE,"E2575"),sQuery(id+"F2.wireOp",EDGE,"E2576"),sQuery(id+"F2.wireOp",EDGE,"E2577"),sQuery(id+"F2.wireOp",EDGE,"E2578"),sQuery(id+"F2.wireOp",EDGE,"E2579"),sQuery(id+"F2.wireOp",EDGE,"E2580"),sQuery(id+"F2.wireOp",EDGE,"E2581"),sQuery(id+"F2.wireOp",EDGE,"E2582"),sQuery(id+"F2.wireOp",EDGE,"E2583"),sQuery(id+"F2.wireOp",EDGE,"E2584"),sQuery(id+"F2.wireOp",EDGE,"E2585"),sQuery(id+"F2.wireOp",EDGE,"E2586"),sQuery(id+"F2.wireOp",EDGE,"E2587"),sQuery(id+"F2.wireOp",EDGE,"E2588"),sQuery(id+"F2.wireOp",EDGE,"E2589"),sQuery(id+"F2.wireOp",EDGE,"E2590"),sQuery(id+"F2.wireOp",EDGE,"E2591"),sQuery(id+"F2.wireOp",EDGE,"E2592"),sQuery(id+"F2.wireOp",EDGE,"E2593"),sQuery(id+"F2.wireOp",EDGE,"E2594"),sQuery(id+"F2.wireOp",EDGE,"E2595"),sQuery(id+"F2.wireOp",EDGE,"E2596"),sQuery(id+"F2.wireOp",EDGE,"E2597"),sQuery(id+"F2.wireOp",EDGE,"E2598"),sQuery(id+"F2.wireOp",EDGE,"E2599"),sQuery(id+"F2.wireOp",EDGE,"E2600"),sQuery(id+"F2.wireOp",EDGE,"E2601"),sQuery(id+"F2.wireOp",EDGE,"E2602"),sQuery(id+"F2.wireOp",EDGE,"E2603"),sQuery(id+"F2.wireOp",EDGE,"E2604"),sQuery(id+"F2.wireOp",EDGE,"E2605"),sQuery(id+"F2.wireOp",EDGE,"E2606"),sQuery(id+"F2.wireOp",EDGE,"E2607"),sQuery(id+"F2.wireOp",EDGE,"E2608"),sQuery(id+"F2.wireOp",EDGE,"E2609"),sQuery(id+"F2.wireOp",EDGE,"E2610"),sQuery(id+"F2.wireOp",EDGE,"E2611"),sQuery(id+"F2.wireOp",EDGE,"E2612"),sQuery(id+"F2.wireOp",EDGE,"E2613"),sQuery(id+"F2.wireOp",EDGE,"E2614"),sQuery(id+"F2.wireOp",EDGE,"E2615"),sQuery(id+"F2.wireOp",EDGE,"E2616"),sQuery(id+"F2.wireOp",EDGE,"E2617"),sQuery(id+"F2.wireOp",EDGE,"E2618"),sQuery(id+"F2.wireOp",EDGE,"E2619"),sQuery(id+"F2.wireOp",EDGE,"E2620"),sQuery(id+"F2.wireOp",EDGE,"E2621"),sQuery(id+"F2.wireOp",EDGE,"E2622"),sQuery(id+"F2.wireOp",EDGE,"E2623"),sQuery(id+"F2.wireOp",EDGE,"E2624"),sQuery(id+"F2.wireOp",EDGE,"E2625"),sQuery(id+"F2.wireOp",EDGE,"E2626"),sQuery(id+"F2.wireOp",EDGE,"E2627"),sQuery(id+"F2.wireOp",EDGE,"E2628"),sQuery(id+"F2.wireOp",EDGE,"E2629"),sQuery(id+"F2.wireOp",EDGE,"E2630"),sQuery(id+"F2.wireOp",EDGE,"E2631"),sQuery(id+"F2.wireOp",EDGE,"E2632"),sQuery(id+"F2.wireOp",EDGE,"E2633"),sQuery(id+"F2.wireOp",EDGE,"E2634"),sQuery(id+"F2.wireOp",EDGE,"E2635"),sQuery(id+"F2.wireOp",EDGE,"E2636"),sQuery(id+"F2.wireOp",EDGE,"E2637"),sQuery(id+"F2.wireOp",EDGE,"E2638"),sQuery(id+"F2.wireOp",EDGE,"E2639"),sQuery(id+"F2.wireOp",EDGE,"E2640"),sQuery(id+"F2.wireOp",EDGE,"E2641"),sQuery(id+"F2.wireOp",EDGE,"E2642"),sQuery(id+"F2.wireOp",EDGE,"E2643"),sQuery(id+"F2.wireOp",EDGE,"E2644"),sQuery(id+"F2.wireOp",EDGE,"E2645"),sQuery(id+"F2.wireOp",EDGE,"E2646"),sQuery(id+"F2.wireOp",EDGE,"E2647"),sQuery(id+"F2.wireOp",EDGE,"E2648"),sQuery(id+"F2.wireOp",EDGE,"E2649"),sQuery(id+"F2.wireOp",EDGE,"E2650"),sQuery(id+"F2.wireOp",EDGE,"E2651"),sQuery(id+"F2.wireOp",EDGE,"E2652"),sQuery(id+"F2.wireOp",EDGE,"E2653"),sQuery(id+"F2.wireOp",EDGE,"E2654"),sQuery(id+"F2.wireOp",EDGE,"E2655"),sQuery(id+"F2.wireOp",EDGE,"E2656"),sQuery(id+"F2.wireOp",EDGE,"E2657"),sQuery(id+"F2.wireOp",EDGE,"E2658"),sQuery(id+"F2.wireOp",EDGE,"E2659"),sQuery(id+"F2.wireOp",EDGE,"E2660"),sQuery(id+"F2.wireOp",EDGE,"E2661"),sQuery(id+"F2.wireOp",EDGE,"E2662"),sQuery(id+"F2.wireOp",EDGE,"E2663"),sQuery(id+"F2.wireOp",EDGE,"E2664"),sQuery(id+"F2.wireOp",EDGE,"E2665"),sQuery(id+"F2.wireOp",EDGE,"E2666"),sQuery(id+"F2.wireOp",EDGE,"E2667"),sQuery(id+"F2.wireOp",EDGE,"E2668"),sQuery(id+"F2.wireOp",EDGE,"E2669"),sQuery(id+"F2.wireOp",EDGE,"E2670"),sQuery(id+"F2.wireOp",EDGE,"E2671"),sQuery(id+"F2.wireOp",EDGE,"E2672"),sQuery(id+"F2.wireOp",EDGE,"E2673"),sQuery(id+"F2.wireOp",EDGE,"E2674"),sQuery(id+"F2.wireOp",EDGE,"E2675"),sQuery(id+"F2.wireOp",EDGE,"E2676"),sQuery(id+"F2.wireOp",EDGE,"E2677"),sQuery(id+"F2.wireOp",EDGE,"E2678"),sQuery(id+"F2.wireOp",EDGE,"E2679"),sQuery(id+"F2.wireOp",EDGE,"E2680"),sQuery(id+"F2.wireOp",EDGE,"E2681"),sQuery(id+"F2.wireOp",EDGE,"E2682"),sQuery(id+"F2.wireOp",EDGE,"E2683"),sQuery(id+"F2.wireOp",EDGE,"E2684"),sQuery(id+"F2.wireOp",EDGE,"E2685"),sQuery(id+"F2.wireOp",EDGE,"E2686"),sQuery(id+"F2.wireOp",EDGE,"E2687"),sQuery(id+"F2.wireOp",EDGE,"E2688"),sQuery(id+"F2.wireOp",EDGE,"E2689"),sQuery(id+"F2.wireOp",EDGE,"E2690"),sQuery(id+"F2.wireOp",EDGE,"E2691"),sQuery(id+"F2.wireOp",EDGE,"E2692"),sQuery(id+"F2.wireOp",EDGE,"E2693"),sQuery(id+"F2.wireOp",EDGE,"E2694"),sQuery(id+"F2.wireOp",EDGE,"E2695"),sQuery(id+"F2.wireOp",EDGE,"E2696"),sQuery(id+"F2.wireOp",EDGE,"E2697"),sQuery(id+"F2.wireOp",EDGE,"E2698"),sQuery(id+"F2.wireOp",EDGE,"E2699"),sQuery(id+"F2.wireOp",EDGE,"E2700"),sQuery(id+"F2.wireOp",EDGE,"E2701"),sQuery(id+"F2.wireOp",EDGE,"E2702"),sQuery(id+"F2.wireOp",EDGE,"E2703"),sQuery(id+"F2.wireOp",EDGE,"E2704"),sQuery(id+"F2.wireOp",EDGE,"E2705"),sQuery(id+"F2.wireOp",EDGE,"E2706"),sQuery(id+"F2.wireOp",EDGE,"E2707"),sQuery(id+"F2.wireOp",EDGE,"E2708"),sQuery(id+"F2.wireOp",EDGE,"E2709"),sQuery(id+"F2.wireOp",EDGE,"E2710"),sQuery(id+"F2.wireOp",EDGE,"E2711"),sQuery(id+"F2.wireOp",EDGE,"E2712"),sQuery(id+"F2.wireOp",EDGE,"E2713"),sQuery(id+"F2.wireOp",EDGE,"E2714"),sQuery(id+"F2.wireOp",EDGE,"E2715"),sQuery(id+"F2.wireOp",EDGE,"E2716"),sQuery(id+"F2.wireOp",EDGE,"E2717"),sQuery(id+"F2.wireOp",EDGE,"E2718"),sQuery(id+"F2.wireOp",EDGE,"E2719"),sQuery(id+"F2.wireOp",EDGE,"E2720"),sQuery(id+"F2.wireOp",EDGE,"E2721"),sQuery(id+"F2.wireOp",EDGE,"E2722"),sQuery(id+"F2.wireOp",EDGE,"E2723"),sQuery(id+"F2.wireOp",EDGE,"E2724"),sQuery(id+"F2.wireOp",EDGE,"E2725"),sQuery(id+"F2.wireOp",EDGE,"E2726"),sQuery(id+"F2.wireOp",EDGE,"E2727"),sQuery(id+"F2.wireOp",EDGE,"E2728"),sQuery(id+"F2.wireOp",EDGE,"E2729"),sQuery(id+"F2.wireOp",EDGE,"E2730"),sQuery(id+"F2.wireOp",EDGE,"E2731"),sQuery(id+"F2.wireOp",EDGE,"E2732"),sQuery(id+"F2.wireOp",EDGE,"E2733"),sQuery(id+"F2.wireOp",EDGE,"E2734"),sQuery(id+"F2.wireOp",EDGE,"E2735"),sQuery(id+"F2.wireOp",EDGE,"E2736"),sQuery(id+"F2.wireOp",EDGE,"E2737"),sQuery(id+"F2.wireOp",EDGE,"E2738"),sQuery(id+"F2.wireOp",EDGE,"E2739"),sQuery(id+"F2.wireOp",EDGE,"E2740"),sQuery(id+"F2.wireOp",EDGE,"E2741"),sQuery(id+"F2.wireOp",EDGE,"E2742"),sQuery(id+"F2.wireOp",EDGE,"E2743"),sQuery(id+"F2.wireOp",EDGE,"E2744"),sQuery(id+"F2.wireOp",EDGE,"E2745"),sQuery(id+"F2.wireOp",EDGE,"E2746"),sQuery(id+"F2.wireOp",EDGE,"E2747"),sQuery(id+"F2.wireOp",EDGE,"E2748"),sQuery(id+"F2.wireOp",EDGE,"E2749"),sQuery(id+"F2.wireOp",EDGE,"E2750"),sQuery(id+"F2.wireOp",EDGE,"E2751"),sQuery(id+"F2.wireOp",EDGE,"E2752"),sQuery(id+"F2.wireOp",EDGE,"E2753"),sQuery(id+"F2.wireOp",EDGE,"E2754"),sQuery(id+"F2.wireOp",EDGE,"E2755"),sQuery(id+"F2.wireOp",EDGE,"E2756"),sQuery(id+"F2.wireOp",EDGE,"E2757"),sQuery(id+"F2.wireOp",EDGE,"E2758"),sQuery(id+"F2.wireOp",EDGE,"E2759"),sQuery(id+"F2.wireOp",EDGE,"E2760"),sQuery(id+"F2.wireOp",EDGE,"E2761"),sQuery(id+"F2.wireOp",EDGE,"E2762"),sQuery(id+"F2.wireOp",EDGE,"E2763"),sQuery(id+"F2.wireOp",EDGE,"E2764"),sQuery(id+"F2.wireOp",EDGE,"E2765"),sQuery(id+"F2.wireOp",EDGE,"E2766"),sQuery(id+"F2.wireOp",EDGE,"E2767"),sQuery(id+"F2.wireOp",EDGE,"E2768"),sQuery(id+"F2.wireOp",EDGE,"E2769"),sQuery(id+"F2.wireOp",EDGE,"E2770"),sQuery(id+"F2.wireOp",EDGE,"E2771"),sQuery(id+"F2.wireOp",EDGE,"E2772"),sQuery(id+"F2.wireOp",EDGE,"E2773"),sQuery(id+"F2.wireOp",EDGE,"E2774"),sQuery(id+"F2.wireOp",EDGE,"E2775"),sQuery(id+"F2.wireOp",EDGE,"E2776"),sQuery(id+"F2.wireOp",EDGE,"E2777"),sQuery(id+"F2.wireOp",EDGE,"E2778"),sQuery(id+"F2.wireOp",EDGE,"E2779"),sQuery(id+"F2.wireOp",EDGE,"E2780"),sQuery(id+"F2.wireOp",EDGE,"E2781"),sQuery(id+"F2.wireOp",EDGE,"E2782"),sQuery(id+"F2.wireOp",EDGE,"E2783"),sQuery(id+"F2.wireOp",EDGE,"E2784"),sQuery(id+"F2.wireOp",EDGE,"E2785"),sQuery(id+"F2.wireOp",EDGE,"E2786"),sQuery(id+"F2.wireOp",EDGE,"E2787"),sQuery(id+"F2.wireOp",EDGE,"E2788"),sQuery(id+"F2.wireOp",EDGE,"E2789"),sQuery(id+"F2.wireOp",EDGE,"E2790"),sQuery(id+"F2.wireOp",EDGE,"E2791"),sQuery(id+"F2.wireOp",EDGE,"E2792"),sQuery(id+"F2.wireOp",EDGE,"E2793"),sQuery(id+"F2.wireOp",EDGE,"E2794"),sQuery(id+"F2.wireOp",EDGE,"E2795"),sQuery(id+"F2.wireOp",EDGE,"E2796"),sQuery(id+"F2.wireOp",EDGE,"E2797"),sQuery(id+"F2.wireOp",EDGE,"E2798"),sQuery(id+"F2.wireOp",EDGE,"E2799"),sQuery(id+"F2.wireOp",EDGE,"E2800"),sQuery(id+"F2.wireOp",EDGE,"E2801"),sQuery(id+"F2.wireOp",EDGE,"E2802"),sQuery(id+"F2.wireOp",EDGE,"E2803"),sQuery(id+"F2.wireOp",EDGE,"E2804"),sQuery(id+"F2.wireOp",EDGE,"E2805"),sQuery(id+"F2.wireOp",EDGE,"E2806"),sQuery(id+"F2.wireOp",EDGE,"E2807"),sQuery(id+"F2.wireOp",EDGE,"E2808"),sQuery(id+"F2.wireOp",EDGE,"E2809"),sQuery(id+"F2.wireOp",EDGE,"E2810"),sQuery(id+"F2.wireOp",EDGE,"E2811"),sQuery(id+"F2.wireOp",EDGE,"E2812"),sQuery(id+"F2.wireOp",EDGE,"E2813"),sQuery(id+"F2.wireOp",EDGE,"E2814"),sQuery(id+"F2.wireOp",EDGE,"E2815"),sQuery(id+"F2.wireOp",EDGE,"E2816"),sQuery(id+"F2.wireOp",EDGE,"E2817"),sQuery(id+"F2.wireOp",EDGE,"E2818"),sQuery(id+"F2.wireOp",EDGE,"E2819"),sQuery(id+"F2.wireOp",EDGE,"E2820"),sQuery(id+"F2.wireOp",EDGE,"E2821"),sQuery(id+"F2.wireOp",EDGE,"E2822"),sQuery(id+"F2.wireOp",EDGE,"E2823"),sQuery(id+"F2.wireOp",EDGE,"E2824"),sQuery(id+"F2.wireOp",EDGE,"E2825"),sQuery(id+"F2.wireOp",EDGE,"E2826"),sQuery(id+"F2.wireOp",EDGE,"E2827"),sQuery(id+"F2.wireOp",EDGE,"E2828"),sQuery(id+"F2.wireOp",EDGE,"E2829"),sQuery(id+"F2.wireOp",EDGE,"E2830"),sQuery(id+"F2.wireOp",EDGE,"E2831"),sQuery(id+"F2.wireOp",EDGE,"E2832"),sQuery(id+"F2.wireOp",EDGE,"E2833"),sQuery(id+"F2.wireOp",EDGE,"E2834"),sQuery(id+"F2.wireOp",EDGE,"E2835"),sQuery(id+"F2.wireOp",EDGE,"E2836"),sQuery(id+"F2.wireOp",EDGE,"E2837"),sQuery(id+"F2.wireOp",EDGE,"E2838"),sQuery(id+"F2.wireOp",EDGE,"E2839"),sQuery(id+"F2.wireOp",EDGE,"E2840"),sQuery(id+"F2.wireOp",EDGE,"E2841"),sQuery(id+"F2.wireOp",EDGE,"E2842"),sQuery(id+"F2.wireOp",EDGE,"E2843"),sQuery(id+"F2.wireOp",EDGE,"E2844"),sQuery(id+"F2.wireOp",EDGE,"E2845"),sQuery(id+"F2.wireOp",EDGE,"E2846"),sQuery(id+"F2.wireOp",EDGE,"E2847"),sQuery(id+"F2.wireOp",EDGE,"E2848"),sQuery(id+"F2.wireOp",EDGE,"E2849"),sQuery(id+"F2.wireOp",EDGE,"E2850"),sQuery(id+"F2.wireOp",EDGE,"E2851"),sQuery(id+"F2.wireOp",EDGE,"E2852"),sQuery(id+"F2.wireOp",EDGE,"E2853"),sQuery(id+"F2.wireOp",EDGE,"E2854"),sQuery(id+"F2.wireOp",EDGE,"E2855"),sQuery(id+"F2.wireOp",EDGE,"E2856"),sQuery(id+"F2.wireOp",EDGE,"E2857"),sQuery(id+"F2.wireOp",EDGE,"E2858"),sQuery(id+"F2.wireOp",EDGE,"E2859"),sQuery(id+"F2.wireOp",EDGE,"E2860"),sQuery(id+"F2.wireOp",EDGE,"E2861"),sQuery(id+"F2.wireOp",EDGE,"E2862"),sQuery(id+"F2.wireOp",EDGE,"E2863"),sQuery(id+"F2.wireOp",EDGE,"E2864"),sQuery(id+"F2.wireOp",EDGE,"E2865"),sQuery(id+"F2.wireOp",EDGE,"E2866"),sQuery(id+"F2.wireOp",EDGE,"E2867"),sQuery(id+"F2.wireOp",EDGE,"E2868"),sQuery(id+"F2.wireOp",EDGE,"E2869"),sQuery(id+"F2.wireOp",EDGE,"E2870"),sQuery(id+"F2.wireOp",EDGE,"E2871"),sQuery(id+"F2.wireOp",EDGE,"E2872"),sQuery(id+"F2.wireOp",EDGE,"E2873"),sQuery(id+"F2.wireOp",EDGE,"E2874"),sQuery(id+"F2.wireOp",EDGE,"E2875"),sQuery(id+"F2.wireOp",EDGE,"E2876"),sQuery(id+"F2.wireOp",EDGE,"E2877"),sQuery(id+"F2.wireOp",EDGE,"E2878"),sQuery(id+"F2.wireOp",EDGE,"E2879"),sQuery(id+"F2.wireOp",EDGE,"E2880"),sQuery(id+"F2.wireOp",EDGE,"E2881"),sQuery(id+"F2.wireOp",EDGE,"E2882"),sQuery(id+"F2.wireOp",EDGE,"E2883"),sQuery(id+"F2.wireOp",EDGE,"E2884"),sQuery(id+"F2.wireOp",EDGE,"E2885"),sQuery(id+"F2.wireOp",EDGE,"E2886"),sQuery(id+"F2.wireOp",EDGE,"E2887"),sQuery(id+"F2.wireOp",EDGE,"E2888"),sQuery(id+"F2.wireOp",EDGE,"E2889"),sQuery(id+"F2.wireOp",EDGE,"E2890"),sQuery(id+"F2.wireOp",EDGE,"E2891"),sQuery(id+"F2.wireOp",EDGE,"E2892"),sQuery(id+"F2.wireOp",EDGE,"E2893"),sQuery(id+"F2.wireOp",EDGE,"E2894"),sQuery(id+"F2.wireOp",EDGE,"E2895"),sQuery(id+"F2.wireOp",EDGE,"E2896"),sQuery(id+"F2.wireOp",EDGE,"E2897"),sQuery(id+"F2.wireOp",EDGE,"E2898"),sQuery(id+"F2.wireOp",EDGE,"E2899"),sQuery(id+"F2.wireOp",EDGE,"E2900"),sQuery(id+"F2.wireOp",EDGE,"E2901"),sQuery(id+"F2.wireOp",EDGE,"E2902"),sQuery(id+"F2.wireOp",EDGE,"E2903"),sQuery(id+"F2.wireOp",EDGE,"E2904"),sQuery(id+"F2.wireOp",EDGE,"E2905"),sQuery(id+"F2.wireOp",EDGE,"E2906"),sQuery(id+"F2.wireOp",EDGE,"E2907"),sQuery(id+"F2.wireOp",EDGE,"E2908"),sQuery(id+"F2.wireOp",EDGE,"E2914.trimOffspring"),sQuery(id+"F2.wireOp",EDGE,"E2921")])],"isStart":false});
            extrude(context, id + "F4", {"entities" : qUnion([Q0, Q1, Q2, Q3]), "operationType" : NewBodyOperationType.ADD, "endBound" : BoundingType.UP_TO_SURFACE, "depth" : 25 * mm, "endBoundEntityFace" : qUnion([Q4]), "offsetDistance" : 25 * mm});
        }
    });
